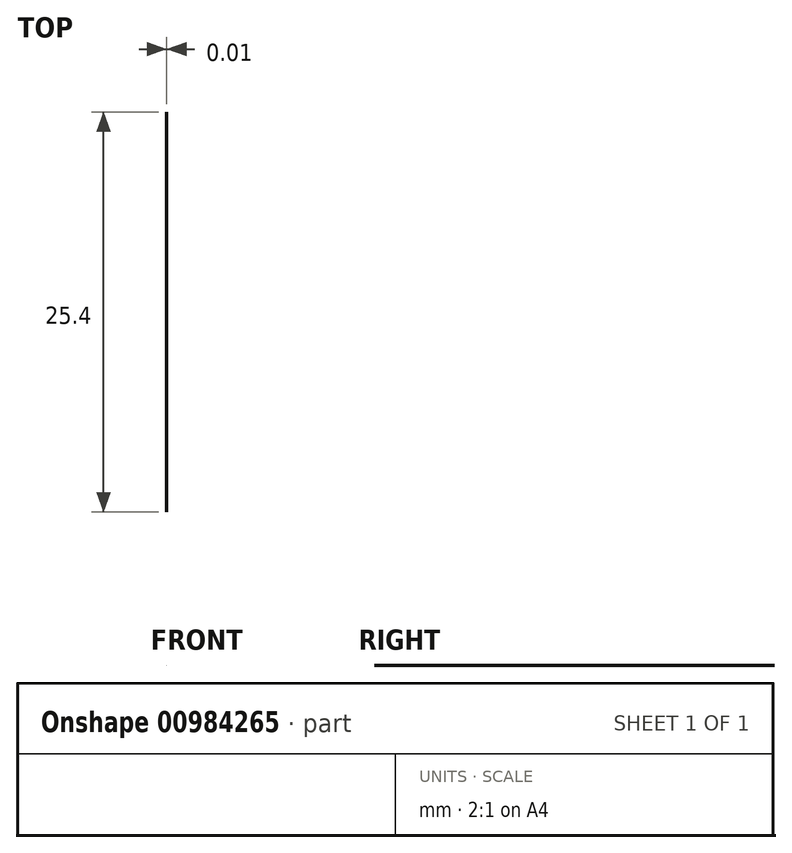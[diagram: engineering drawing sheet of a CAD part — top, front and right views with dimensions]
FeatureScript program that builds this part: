
annotation { "Feature Type Name" : "Feature", "Feature Type Description" : "" }
export const myFeature = defineFeature(function(context is Context, id is Id, definition is map)
    precondition{}
    {
        {
            var Q0;
            Q0=qCreatedBy(makeId("Front.planeOp"),FACE);
            var sketch = newSketch(context, id + "F0", { "sketchPlane" : qUnion([Q0])});
            skLineSegment(sketch, "E0", {"start": v(0.03, 1.18) * mm, "end": v(0.02, 1.18) * mm});
            skLineSegment(sketch, "E1", {"start": v(0.02, 1.18) * mm, "end": v(-0.02, 1.17) * mm});
            skLineSegment(sketch, "E2", {"start": v(-0.02, 1.17) * mm, "end": v(-0.06, 1.16) * mm});
            skLineSegment(sketch, "E3", {"start": v(-0.06, 1.16) * mm, "end": v(-0.1, 1.15) * mm});
            skLineSegment(sketch, "E4", {"start": v(-0.1, 1.15) * mm, "end": v(-0.11, 1.15) * mm});
            skLineSegment(sketch, "E5", {"start": v(-0.11, 1.15) * mm, "end": v(-0.12, 1.14) * mm});
            skLineSegment(sketch, "E6", {"start": v(-0.12, 1.14) * mm, "end": v(-0.12, 1.14) * mm});
            skLineSegment(sketch, "E7", {"start": v(-0.12, 1.14) * mm, "end": v(-0.15, 1.13) * mm});
            skLineSegment(sketch, "E8", {"start": v(-0.15, 1.13) * mm, "end": v(-0.2, 1.12) * mm});
            skLineSegment(sketch, "E9", {"start": v(-0.2, 1.12) * mm, "end": v(-0.24, 1.13) * mm});
            skLineSegment(sketch, "E10", {"start": v(-0.24, 1.13) * mm, "end": v(-0.26, 1.14) * mm});
            skLineSegment(sketch, "E11", {"start": v(-0.26, 1.14) * mm, "end": v(-0.27, 1.14) * mm});
            skLineSegment(sketch, "E12", {"start": v(-0.27, 1.14) * mm, "end": v(-0.27, 1.14) * mm});
            skLineSegment(sketch, "E13", {"start": v(-0.27, 1.14) * mm, "end": v(-0.29, 1.16) * mm});
            skLineSegment(sketch, "E14", {"start": v(-0.29, 1.16) * mm, "end": v(-0.3, 1.16) * mm});
            skLineSegment(sketch, "E15", {"start": v(-0.3, 1.16) * mm, "end": v(-0.3, 1.16) * mm});
            skLineSegment(sketch, "E16", {"start": v(-0.3, 1.16) * mm, "end": v(-0.31, 1.16) * mm});
            skLineSegment(sketch, "E17", {"start": v(-0.31, 1.16) * mm, "end": v(-0.33, 1.16) * mm});
            skLineSegment(sketch, "E18", {"start": v(-0.33, 1.16) * mm, "end": v(-0.34, 1.17) * mm});
            skLineSegment(sketch, "E19", {"start": v(-0.34, 1.17) * mm, "end": v(-0.34, 1.17) * mm});
            skLineSegment(sketch, "E20", {"start": v(-0.34, 1.17) * mm, "end": v(-0.35, 1.18) * mm});
            skLineSegment(sketch, "E21", {"start": v(-0.35, 1.18) * mm, "end": v(-0.37, 1.18) * mm});
            skLineSegment(sketch, "E22", {"start": v(-0.37, 1.18) * mm, "end": v(-0.42, 1.18) * mm});
            skLineSegment(sketch, "E23", {"start": v(-0.42, 1.18) * mm, "end": v(-0.5, 1.17) * mm});
            skLineSegment(sketch, "E24", {"start": v(-0.5, 1.17) * mm, "end": v(-0.55, 1.16) * mm});
            skLineSegment(sketch, "E25", {"start": v(-0.55, 1.16) * mm, "end": v(-0.57, 1.15) * mm});
            skLineSegment(sketch, "E26", {"start": v(-0.57, 1.15) * mm, "end": v(-0.58, 1.15) * mm});
            skLineSegment(sketch, "E27", {"start": v(-0.58, 1.15) * mm, "end": v(-0.62, 1.15) * mm});
            skLineSegment(sketch, "E28", {"start": v(-0.62, 1.15) * mm, "end": v(-0.65, 1.14) * mm});
            skLineSegment(sketch, "E29", {"start": v(-0.65, 1.14) * mm, "end": v(-0.65, 1.14) * mm});
            skLineSegment(sketch, "E30", {"start": v(-0.65, 1.14) * mm, "end": v(-0.66, 1.14) * mm});
            skLineSegment(sketch, "E31", {"start": v(-0.66, 1.14) * mm, "end": v(-0.68, 1.14) * mm});
            skLineSegment(sketch, "E32", {"start": v(-0.68, 1.14) * mm, "end": v(-0.7, 1.13) * mm});
            skLineSegment(sketch, "E33", {"start": v(-0.7, 1.13) * mm, "end": v(-0.7, 1.13) * mm});
            skLineSegment(sketch, "E34", {"start": v(-0.7, 1.13) * mm, "end": v(-0.72, 1.13) * mm});
            skLineSegment(sketch, "E35", {"start": v(-0.72, 1.13) * mm, "end": v(-0.72, 1.13) * mm});
            skLineSegment(sketch, "E36", {"start": v(-0.72, 1.13) * mm, "end": v(-0.72, 1.14) * mm});
            skLineSegment(sketch, "E37", {"start": v(-0.72, 1.14) * mm, "end": v(-0.74, 1.14) * mm});
            skLineSegment(sketch, "E38", {"start": v(-0.74, 1.14) * mm, "end": v(-0.76, 1.13) * mm});
            skLineSegment(sketch, "E39", {"start": v(-0.76, 1.13) * mm, "end": v(-0.76, 1.13) * mm});
            skLineSegment(sketch, "E40", {"start": v(-0.76, 1.13) * mm, "end": v(-0.76, 1.12) * mm});
            skLineSegment(sketch, "E41", {"start": v(-0.76, 1.12) * mm, "end": v(-0.78, 1.11) * mm});
            skLineSegment(sketch, "E42", {"start": v(-0.78, 1.11) * mm, "end": v(-0.8, 1.1) * mm});
            skLineSegment(sketch, "E43", {"start": v(-0.8, 1.1) * mm, "end": v(-0.8, 1.1) * mm});
            skLineSegment(sketch, "E44", {"start": v(-0.8, 1.1) * mm, "end": v(-0.8, 1.09) * mm});
            skLineSegment(sketch, "E45", {"start": v(-0.8, 1.09) * mm, "end": v(-0.8, 1.08) * mm});
            skLineSegment(sketch, "E46", {"start": v(-0.8, 1.08) * mm, "end": v(-0.81, 1.08) * mm});
            skLineSegment(sketch, "E47", {"start": v(-0.81, 1.08) * mm, "end": v(-0.82, 1.06) * mm});
            skLineSegment(sketch, "E48", {"start": v(-0.82, 1.06) * mm, "end": v(-0.83, 1.04) * mm});
            skLineSegment(sketch, "E49", {"start": v(-0.83, 1.04) * mm, "end": v(-0.85, 1.03) * mm});
            skLineSegment(sketch, "E50", {"start": v(-0.85, 1.03) * mm, "end": v(-0.87, 1) * mm});
            skLineSegment(sketch, "E51", {"start": v(-0.87, 1) * mm, "end": v(-0.88, 1) * mm});
            skLineSegment(sketch, "E52", {"start": v(-0.88, 1) * mm, "end": v(-0.9, 0.98) * mm});
            skLineSegment(sketch, "E53", {"start": v(-0.9, 0.98) * mm, "end": v(-0.9, 0.98) * mm});
            skLineSegment(sketch, "E54", {"start": v(-0.9, 0.98) * mm, "end": v(-0.92, 0.97) * mm});
            skLineSegment(sketch, "E55", {"start": v(-0.92, 0.97) * mm, "end": v(-0.92, 0.96) * mm});
            skLineSegment(sketch, "E56", {"start": v(-0.92, 0.96) * mm, "end": v(-0.93, 0.96) * mm});
            skLineSegment(sketch, "E57", {"start": v(-0.93, 0.96) * mm, "end": v(-0.93, 0.95) * mm});
            skLineSegment(sketch, "E58", {"start": v(-0.93, 0.95) * mm, "end": v(-0.93, 0.94) * mm});
            skLineSegment(sketch, "E59", {"start": v(-0.93, 0.94) * mm, "end": v(-0.95, 0.91) * mm});
            skLineSegment(sketch, "E60", {"start": v(-0.95, 0.91) * mm, "end": v(-0.98, 0.88) * mm});
            skLineSegment(sketch, "E61", {"start": v(-0.98, 0.88) * mm, "end": v(-1, 0.84) * mm});
            skLineSegment(sketch, "E62", {"start": v(-1, 0.84) * mm, "end": v(-1.02, 0.83) * mm});
            skLineSegment(sketch, "E63", {"start": v(-1.02, 0.83) * mm, "end": v(-1.02, 0.83) * mm});
            skLineSegment(sketch, "E64", {"start": v(-1.02, 0.83) * mm, "end": v(-1.04, 0.8) * mm});
            skLineSegment(sketch, "E65", {"start": v(-1.04, 0.8) * mm, "end": v(-1.06, 0.74) * mm});
            skLineSegment(sketch, "E66", {"start": v(-1.06, 0.74) * mm, "end": v(-1.1, 0.66) * mm});
            skLineSegment(sketch, "E67", {"start": v(-1.1, 0.66) * mm, "end": v(-1.1, 0.61) * mm});
            skLineSegment(sketch, "E68", {"start": v(-1.1, 0.61) * mm, "end": v(-1.12, 0.6) * mm});
            skLineSegment(sketch, "E69", {"start": v(-1.12, 0.6) * mm, "end": v(-1.12, 0.58) * mm});
            skLineSegment(sketch, "E70", {"start": v(-1.12, 0.58) * mm, "end": v(-1.13, 0.56) * mm});
            skLineSegment(sketch, "E71", {"start": v(-1.13, 0.56) * mm, "end": v(-1.14, 0.54) * mm});
            skLineSegment(sketch, "E72", {"start": v(-1.14, 0.54) * mm, "end": v(-1.17, 0.52) * mm});
            skLineSegment(sketch, "E73", {"start": v(-1.17, 0.52) * mm, "end": v(-1.2, 0.5) * mm});
            skLineSegment(sketch, "E74", {"start": v(-1.2, 0.5) * mm, "end": v(-1.2, 0.5) * mm});
            skLineSegment(sketch, "E75", {"start": v(-1.2, 0.5) * mm, "end": v(-1.22, 0.5) * mm});
            skLineSegment(sketch, "E76", {"start": v(-1.22, 0.5) * mm, "end": v(-1.27, 0.47) * mm});
            skLineSegment(sketch, "E77", {"start": v(-1.27, 0.47) * mm, "end": v(-1.31, 0.44) * mm});
            skLineSegment(sketch, "E78", {"start": v(-1.31, 0.44) * mm, "end": v(-1.32, 0.43) * mm});
            skLineSegment(sketch, "E79", {"start": v(-1.32, 0.43) * mm, "end": v(-1.37, 0.38) * mm});
            skLineSegment(sketch, "E80", {"start": v(-1.37, 0.38) * mm, "end": v(-1.36, 0.47) * mm});
            skLineSegment(sketch, "E81", {"start": v(-1.36, 0.47) * mm, "end": v(-1.36, 0.5) * mm});
            skLineSegment(sketch, "E82", {"start": v(-1.36, 0.5) * mm, "end": v(-1.34, 0.57) * mm});
            skLineSegment(sketch, "E83", {"start": v(-1.34, 0.57) * mm, "end": v(-1.32, 0.68) * mm});
            skLineSegment(sketch, "E84", {"start": v(-1.32, 0.68) * mm, "end": v(-1.3, 0.77) * mm});
            skLineSegment(sketch, "E85", {"start": v(-1.3, 0.77) * mm, "end": v(-1.25, 0.85) * mm});
            skLineSegment(sketch, "E86", {"start": v(-1.25, 0.85) * mm, "end": v(-1.21, 0.92) * mm});
            skLineSegment(sketch, "E87", {"start": v(-1.21, 0.92) * mm, "end": v(-1.16, 0.97) * mm});
            skLineSegment(sketch, "E88", {"start": v(-1.16, 0.97) * mm, "end": v(-1.11, 1) * mm});
            skLineSegment(sketch, "E89", {"start": v(-1.11, 1) * mm, "end": v(-1.07, 1.03) * mm});
            skLineSegment(sketch, "E90", {"start": v(-1.07, 1.03) * mm, "end": v(-1.06, 1.03) * mm});
            skLineSegment(sketch, "E91", {"start": v(-1.06, 1.03) * mm, "end": v(-1.05, 1.03) * mm});
            skLineSegment(sketch, "E92", {"start": v(-1.05, 1.03) * mm, "end": v(-1.03, 1.04) * mm});
            skLineSegment(sketch, "E93", {"start": v(-1.03, 1.04) * mm, "end": v(-1, 1.05) * mm});
            skLineSegment(sketch, "E94", {"start": v(-1, 1.05) * mm, "end": v(-0.97, 1.06) * mm});
            skLineSegment(sketch, "E95", {"start": v(-0.97, 1.06) * mm, "end": v(-0.94, 1.07) * mm});
            skLineSegment(sketch, "E96", {"start": v(-0.94, 1.07) * mm, "end": v(-0.91, 1.07) * mm});
            skLineSegment(sketch, "E97", {"start": v(-0.91, 1.07) * mm, "end": v(-0.9, 1.08) * mm});
            skLineSegment(sketch, "E98", {"start": v(-0.9, 1.08) * mm, "end": v(-0.9, 1.08) * mm});
            skLineSegment(sketch, "E99", {"start": v(-0.9, 1.08) * mm, "end": v(-0.91, 1.08) * mm});
            skLineSegment(sketch, "E100", {"start": v(-0.91, 1.08) * mm, "end": v(-0.93, 1.08) * mm});
            skLineSegment(sketch, "E101", {"start": v(-0.93, 1.08) * mm, "end": v(-0.98, 1.07) * mm});
            skLineSegment(sketch, "E102", {"start": v(-0.98, 1.07) * mm, "end": v(-1.03, 1.06) * mm});
            skLineSegment(sketch, "E103", {"start": v(-1.03, 1.06) * mm, "end": v(-1.07, 1.06) * mm});
            skLineSegment(sketch, "E104", {"start": v(-1.07, 1.06) * mm, "end": v(-1.09, 1.06) * mm});
            skLineSegment(sketch, "E105", {"start": v(-1.09, 1.06) * mm, "end": v(-1.1, 1.05) * mm});
            skLineSegment(sketch, "E106", {"start": v(-1.1, 1.05) * mm, "end": v(-1.14, 1.05) * mm});
            skLineSegment(sketch, "E107", {"start": v(-1.14, 1.05) * mm, "end": v(-1.2, 1.04) * mm});
            skLineSegment(sketch, "E108", {"start": v(-1.2, 1.04) * mm, "end": v(-1.24, 1.03) * mm});
            skLineSegment(sketch, "E109", {"start": v(-1.24, 1.03) * mm, "end": v(-1.27, 1.03) * mm});
            skLineSegment(sketch, "E110", {"start": v(-1.27, 1.03) * mm, "end": v(-1.27, 1.03) * mm});
            skLineSegment(sketch, "E111", {"start": v(-1.27, 1.03) * mm, "end": v(-1.3, 1.03) * mm});
            skLineSegment(sketch, "E112", {"start": v(-1.3, 1.03) * mm, "end": v(-1.35, 1) * mm});
            skLineSegment(sketch, "E113", {"start": v(-1.35, 1) * mm, "end": v(-1.43, 0.97) * mm});
            skLineSegment(sketch, "E114", {"start": v(-1.43, 0.97) * mm, "end": v(-1.52, 0.92) * mm});
            skLineSegment(sketch, "E115", {"start": v(-1.52, 0.92) * mm, "end": v(-1.56, 0.9) * mm});
            skLineSegment(sketch, "E116", {"start": v(-1.56, 0.9) * mm, "end": v(-1.58, 0.88) * mm});
            skLineSegment(sketch, "E117", {"start": v(-1.58, 0.88) * mm, "end": v(-1.58, 0.87) * mm});
            skLineSegment(sketch, "E118", {"start": v(-1.58, 0.87) * mm, "end": v(-1.62, 0.84) * mm});
            skLineSegment(sketch, "E119", {"start": v(-1.62, 0.84) * mm, "end": v(-1.65, 0.81) * mm});
            skLineSegment(sketch, "E120", {"start": v(-1.65, 0.81) * mm, "end": v(-1.66, 0.8) * mm});
            skLineSegment(sketch, "E121", {"start": v(-1.66, 0.8) * mm, "end": v(-1.66, 0.8) * mm});
            skLineSegment(sketch, "E122", {"start": v(-1.66, 0.8) * mm, "end": v(-1.69, 0.79) * mm});
            skLineSegment(sketch, "E123", {"start": v(-1.69, 0.79) * mm, "end": v(-1.7, 0.77) * mm});
            skLineSegment(sketch, "E124", {"start": v(-1.7, 0.77) * mm, "end": v(-1.7, 0.77) * mm});
            skLineSegment(sketch, "E125", {"start": v(-1.7, 0.77) * mm, "end": v(-1.7, 0.76) * mm});
            skLineSegment(sketch, "E126", {"start": v(-1.7, 0.76) * mm, "end": v(-1.7, 0.75) * mm});
            skLineSegment(sketch, "E127", {"start": v(-1.7, 0.75) * mm, "end": v(-1.7, 0.74) * mm});
            skLineSegment(sketch, "E128", {"start": v(-1.7, 0.74) * mm, "end": v(-1.7, 0.74) * mm});
            skLineSegment(sketch, "E129", {"start": v(-1.7, 0.74) * mm, "end": v(-1.71, 0.74) * mm});
            skLineSegment(sketch, "E130", {"start": v(-1.71, 0.74) * mm, "end": v(-1.72, 0.74) * mm});
            skLineSegment(sketch, "E131", {"start": v(-1.72, 0.74) * mm, "end": v(-1.73, 0.73) * mm});
            skLineSegment(sketch, "E132", {"start": v(-1.73, 0.73) * mm, "end": v(-1.75, 0.7) * mm});
            skLineSegment(sketch, "E133", {"start": v(-1.75, 0.7) * mm, "end": v(-1.76, 0.68) * mm});
            skLineSegment(sketch, "E134", {"start": v(-1.76, 0.68) * mm, "end": v(-1.78, 0.66) * mm});
            skLineSegment(sketch, "E135", {"start": v(-1.78, 0.66) * mm, "end": v(-1.8, 0.63) * mm});
            skLineSegment(sketch, "E136", {"start": v(-1.8, 0.63) * mm, "end": v(-1.8, 0.61) * mm});
            skLineSegment(sketch, "E137", {"start": v(-1.8, 0.61) * mm, "end": v(-1.81, 0.6) * mm});
            skLineSegment(sketch, "E138", {"start": v(-1.81, 0.6) * mm, "end": v(-1.81, 0.6) * mm});
            skLineSegment(sketch, "E139", {"start": v(-1.81, 0.6) * mm, "end": v(-1.83, 0.54) * mm});
            skLineSegment(sketch, "E140", {"start": v(-1.83, 0.54) * mm, "end": v(-1.86, 0.4) * mm});
            skLineSegment(sketch, "E141", {"start": v(-1.86, 0.4) * mm, "end": v(-1.89, 0.2) * mm});
            skLineSegment(sketch, "E142", {"start": v(-1.89, 0.2) * mm, "end": v(-1.9, 0) * mm});
            skLineSegment(sketch, "E143", {"start": v(-1.9, 0) * mm, "end": v(-1.88, -0.18) * mm});
            skLineSegment(sketch, "E144", {"start": v(-1.88, -0.18) * mm, "end": v(-1.84, -0.35) * mm});
            skLineSegment(sketch, "E145", {"start": v(-1.84, -0.35) * mm, "end": v(-1.79, -0.52) * mm});
            skLineSegment(sketch, "E146", {"start": v(-1.79, -0.52) * mm, "end": v(-1.72, -0.66) * mm});
            skLineSegment(sketch, "E147", {"start": v(-1.72, -0.66) * mm, "end": v(-1.65, -0.76) * mm});
            skLineSegment(sketch, "E148", {"start": v(-1.65, -0.76) * mm, "end": v(-1.63, -0.78) * mm});
            skLineSegment(sketch, "E149", {"start": v(-1.63, -0.78) * mm, "end": v(-1.61, -0.8) * mm});
            skLineSegment(sketch, "E150", {"start": v(-1.61, -0.8) * mm, "end": v(-1.57, -0.84) * mm});
            skLineSegment(sketch, "E151", {"start": v(-1.57, -0.84) * mm, "end": v(-1.51, -0.9) * mm});
            skLineSegment(sketch, "E152", {"start": v(-1.51, -0.9) * mm, "end": v(-1.45, -0.97) * mm});
            skLineSegment(sketch, "E153", {"start": v(-1.45, -0.97) * mm, "end": v(-1.41, -1) * mm});
            skLineSegment(sketch, "E154", {"start": v(-1.41, -1) * mm, "end": v(-1.4, -1.02) * mm});
            skLineSegment(sketch, "E155", {"start": v(-1.4, -1.02) * mm, "end": v(-1.4, -1.02) * mm});
            skLineSegment(sketch, "E156", {"start": v(-1.4, -1.02) * mm, "end": v(-1.38, -1.04) * mm});
            skLineSegment(sketch, "E157", {"start": v(-1.38, -1.04) * mm, "end": v(-1.36, -1.06) * mm});
            skLineSegment(sketch, "E158", {"start": v(-1.36, -1.06) * mm, "end": v(-1.34, -1.08) * mm});
            skLineSegment(sketch, "E159", {"start": v(-1.34, -1.08) * mm, "end": v(-1.34, -1.1) * mm});
            skLineSegment(sketch, "E160", {"start": v(-1.34, -1.1) * mm, "end": v(-1.34, -1.1) * mm});
            skLineSegment(sketch, "E161", {"start": v(-1.34, -1.1) * mm, "end": v(-1.33, -1.11) * mm});
            skLineSegment(sketch, "E162", {"start": v(-1.33, -1.11) * mm, "end": v(-1.3, -1.11) * mm});
            skLineSegment(sketch, "E163", {"start": v(-1.3, -1.11) * mm, "end": v(-1.3, -1.11) * mm});
            skLineSegment(sketch, "E164", {"start": v(-1.3, -1.11) * mm, "end": v(-1.27, -1.12) * mm});
            skLineSegment(sketch, "E165", {"start": v(-1.27, -1.12) * mm, "end": v(-1.23, -1.14) * mm});
            skLineSegment(sketch, "E166", {"start": v(-1.23, -1.14) * mm, "end": v(-1.22, -1.14) * mm});
            skLineSegment(sketch, "E167", {"start": v(-1.22, -1.14) * mm, "end": v(-1.21, -1.15) * mm});
            skLineSegment(sketch, "E168", {"start": v(-1.21, -1.15) * mm, "end": v(-1.17, -1.16) * mm});
            skLineSegment(sketch, "E169", {"start": v(-1.17, -1.16) * mm, "end": v(-1.11, -1.17) * mm});
            skLineSegment(sketch, "E170", {"start": v(-1.11, -1.17) * mm, "end": v(-1.1, -1.17) * mm});
            skLineSegment(sketch, "E171", {"start": v(-1.1, -1.17) * mm, "end": v(-1.1, -1.17) * mm});
            skLineSegment(sketch, "E172", {"start": v(-1.1, -1.17) * mm, "end": v(-1.07, -1.17) * mm});
            skLineSegment(sketch, "E173", {"start": v(-1.07, -1.17) * mm, "end": v(-1.05, -1.17) * mm});
            skLineSegment(sketch, "E174", {"start": v(-1.05, -1.17) * mm, "end": v(-1.06, -1.16) * mm});
            skLineSegment(sketch, "E175", {"start": v(-1.06, -1.16) * mm, "end": v(-1.08, -1.16) * mm});
            skLineSegment(sketch, "E176", {"start": v(-1.08, -1.16) * mm, "end": v(-1.09, -1.16) * mm});
            skLineSegment(sketch, "E177", {"start": v(-1.09, -1.16) * mm, "end": v(-1.1, -1.16) * mm});
            skLineSegment(sketch, "E178", {"start": v(-1.1, -1.16) * mm, "end": v(-1.12, -1.15) * mm});
            skLineSegment(sketch, "E179", {"start": v(-1.12, -1.15) * mm, "end": v(-1.16, -1.14) * mm});
            skLineSegment(sketch, "E180", {"start": v(-1.16, -1.14) * mm, "end": v(-1.2, -1.12) * mm});
            skLineSegment(sketch, "E181", {"start": v(-1.2, -1.12) * mm, "end": v(-1.22, -1.1) * mm});
            skLineSegment(sketch, "E182", {"start": v(-1.22, -1.1) * mm, "end": v(-1.25, -1.09) * mm});
            skLineSegment(sketch, "E183", {"start": v(-1.25, -1.09) * mm, "end": v(-1.26, -1.07) * mm});
            skLineSegment(sketch, "E184", {"start": v(-1.26, -1.07) * mm, "end": v(-1.26, -1.06) * mm});
            skLineSegment(sketch, "E185", {"start": v(-1.26, -1.06) * mm, "end": v(-1.26, -1.05) * mm});
            skLineSegment(sketch, "E186", {"start": v(-1.26, -1.05) * mm, "end": v(-1.26, -1.05) * mm});
            skLineSegment(sketch, "E187", {"start": v(-1.26, -1.05) * mm, "end": v(-1.25, -1.05) * mm});
            skLineSegment(sketch, "E188", {"start": v(-1.25, -1.05) * mm, "end": v(-1.23, -1.04) * mm});
            skLineSegment(sketch, "E189", {"start": v(-1.23, -1.04) * mm, "end": v(-1.21, -1.02) * mm});
            skLineSegment(sketch, "E190", {"start": v(-1.21, -1.02) * mm, "end": v(-1.2, -1.02) * mm});
            skLineSegment(sketch, "E191", {"start": v(-1.2, -1.02) * mm, "end": v(-1.18, -1) * mm});
            skLineSegment(sketch, "E192", {"start": v(-1.18, -1) * mm, "end": v(-1.2, -1) * mm});
            skLineSegment(sketch, "E193", {"start": v(-1.2, -1) * mm, "end": v(-1.21, -1) * mm});
            skLineSegment(sketch, "E194", {"start": v(-1.21, -1) * mm, "end": v(-1.23, -1.01) * mm});
            skLineSegment(sketch, "E195", {"start": v(-1.23, -1.01) * mm, "end": v(-1.23, -1.02) * mm});
            skLineSegment(sketch, "E196", {"start": v(-1.23, -1.02) * mm, "end": v(-1.23, -1) * mm});
            skLineSegment(sketch, "E197", {"start": v(-1.23, -1) * mm, "end": v(-1.23, -1) * mm});
            skLineSegment(sketch, "E198", {"start": v(-1.23, -1) * mm, "end": v(-1.22, -0.98) * mm});
            skLineSegment(sketch, "E199", {"start": v(-1.22, -0.98) * mm, "end": v(-1.18, -0.94) * mm});
            skLineSegment(sketch, "E200", {"start": v(-1.18, -0.94) * mm, "end": v(-1.08, -0.86) * mm});
            skLineSegment(sketch, "E201", {"start": v(-1.08, -0.86) * mm, "end": v(-0.97, -0.78) * mm});
            skLineSegment(sketch, "E202", {"start": v(-0.97, -0.78) * mm, "end": v(-0.88, -0.73) * mm});
            skLineSegment(sketch, "E203", {"start": v(-0.88, -0.73) * mm, "end": v(-0.85, -0.71) * mm});
            skLineSegment(sketch, "E204", {"start": v(-0.85, -0.71) * mm, "end": v(-0.84, -0.7) * mm});
            skLineSegment(sketch, "E205", {"start": v(-0.84, -0.7) * mm, "end": v(-0.81, -0.7) * mm});
            skLineSegment(sketch, "E206", {"start": v(-0.81, -0.7) * mm, "end": v(-0.8, -0.7) * mm});
            skLineSegment(sketch, "E207", {"start": v(-0.8, -0.7) * mm, "end": v(-0.8, -0.7) * mm});
            skLineSegment(sketch, "E208", {"start": v(-0.8, -0.7) * mm, "end": v(-0.82, -0.73) * mm});
            skLineSegment(sketch, "E209", {"start": v(-0.82, -0.73) * mm, "end": v(-0.82, -0.74) * mm});
            skLineSegment(sketch, "E210", {"start": v(-0.82, -0.74) * mm, "end": v(-0.83, -0.75) * mm});
            skLineSegment(sketch, "E211", {"start": v(-0.83, -0.75) * mm, "end": v(-0.85, -0.79) * mm});
            skLineSegment(sketch, "E212", {"start": v(-0.85, -0.79) * mm, "end": v(-0.88, -0.85) * mm});
            skLineSegment(sketch, "E213", {"start": v(-0.88, -0.85) * mm, "end": v(-0.91, -0.92) * mm});
            skLineSegment(sketch, "E214", {"start": v(-0.91, -0.92) * mm, "end": v(-0.94, -1) * mm});
            skLineSegment(sketch, "E215", {"start": v(-0.94, -1) * mm, "end": v(-0.96, -1.06) * mm});
            skLineSegment(sketch, "E216", {"start": v(-0.96, -1.06) * mm, "end": v(-0.97, -1.12) * mm});
            skLineSegment(sketch, "E217", {"start": v(-0.97, -1.12) * mm, "end": v(-0.98, -1.16) * mm});
            skLineSegment(sketch, "E218", {"start": v(-0.98, -1.16) * mm, "end": v(-0.97, -1.17) * mm});
            skLineSegment(sketch, "E219", {"start": v(-0.97, -1.17) * mm, "end": v(-0.97, -1.17) * mm});
            skLineSegment(sketch, "E220", {"start": v(-0.97, -1.17) * mm, "end": v(-0.96, -1.17) * mm});
            skLineSegment(sketch, "E221", {"start": v(-0.96, -1.17) * mm, "end": v(-0.95, -1.16) * mm});
            skLineSegment(sketch, "E222", {"start": v(-0.95, -1.16) * mm, "end": v(-0.95, -1.15) * mm});
            skLineSegment(sketch, "E223", {"start": v(-0.95, -1.15) * mm, "end": v(-0.95, -1.14) * mm});
            skLineSegment(sketch, "E224", {"start": v(-0.95, -1.14) * mm, "end": v(-0.95, -1.13) * mm});
            skLineSegment(sketch, "E225", {"start": v(-0.95, -1.13) * mm, "end": v(-0.94, -1.1) * mm});
            skLineSegment(sketch, "E226", {"start": v(-0.94, -1.1) * mm, "end": v(-0.92, -1.05) * mm});
            skLineSegment(sketch, "E227", {"start": v(-0.92, -1.05) * mm, "end": v(-0.9, -0.98) * mm});
            skLineSegment(sketch, "E228", {"start": v(-0.9, -0.98) * mm, "end": v(-0.87, -0.9) * mm});
            skLineSegment(sketch, "E229", {"start": v(-0.87, -0.9) * mm, "end": v(-0.84, -0.84) * mm});
            skLineSegment(sketch, "E230", {"start": v(-0.84, -0.84) * mm, "end": v(-0.82, -0.78) * mm});
            skLineSegment(sketch, "E231", {"start": v(-0.82, -0.78) * mm, "end": v(-0.8, -0.74) * mm});
            skLineSegment(sketch, "E232", {"start": v(-0.8, -0.74) * mm, "end": v(-0.79, -0.73) * mm});
            skLineSegment(sketch, "E233", {"start": v(-0.79, -0.73) * mm, "end": v(-0.79, -0.73) * mm});
            skLineSegment(sketch, "E234", {"start": v(-0.79, -0.73) * mm, "end": v(-0.78, -0.74) * mm});
            skLineSegment(sketch, "E235", {"start": v(-0.78, -0.74) * mm, "end": v(-0.79, -0.76) * mm});
            skLineSegment(sketch, "E236", {"start": v(-0.79, -0.76) * mm, "end": v(-0.79, -0.8) * mm});
            skLineSegment(sketch, "E237", {"start": v(-0.79, -0.8) * mm, "end": v(-0.8, -0.82) * mm});
            skLineSegment(sketch, "E238", {"start": v(-0.8, -0.82) * mm, "end": v(-0.8, -0.83) * mm});
            skLineSegment(sketch, "E239", {"start": v(-0.8, -0.83) * mm, "end": v(-0.8, -0.86) * mm});
            skLineSegment(sketch, "E240", {"start": v(-0.8, -0.86) * mm, "end": v(-0.8, -0.97) * mm});
            skLineSegment(sketch, "E241", {"start": v(-0.8, -0.97) * mm, "end": v(-0.8, -1.08) * mm});
            skLineSegment(sketch, "E242", {"start": v(-0.8, -1.08) * mm, "end": v(-0.8, -1.15) * mm});
            skLineSegment(sketch, "E243", {"start": v(-0.8, -1.15) * mm, "end": v(-0.77, -1.17) * mm});
            skLineSegment(sketch, "E244", {"start": v(-0.77, -1.17) * mm, "end": v(-0.77, -1.17) * mm});
            skLineSegment(sketch, "E245", {"start": v(-0.77, -1.17) * mm, "end": v(-0.76, -1.17) * mm});
            skLineSegment(sketch, "E246", {"start": v(-0.76, -1.17) * mm, "end": v(-0.74, -1.17) * mm});
            skLineSegment(sketch, "E247", {"start": v(-0.74, -1.17) * mm, "end": v(-0.73, -1.15) * mm});
            skLineSegment(sketch, "E248", {"start": v(-0.73, -1.15) * mm, "end": v(-0.72, -1.14) * mm});
            skLineSegment(sketch, "E249", {"start": v(-0.72, -1.14) * mm, "end": v(-0.72, -1.13) * mm});
            skLineSegment(sketch, "E250", {"start": v(-0.72, -1.13) * mm, "end": v(-0.72, -1.12) * mm});
            skLineSegment(sketch, "E251", {"start": v(-0.72, -1.12) * mm, "end": v(-0.73, -1.12) * mm});
            skLineSegment(sketch, "E252", {"start": v(-0.73, -1.12) * mm, "end": v(-0.74, -1.11) * mm});
            skLineSegment(sketch, "E253", {"start": v(-0.74, -1.11) * mm, "end": v(-0.74, -1.1) * mm});
            skLineSegment(sketch, "E254", {"start": v(-0.74, -1.1) * mm, "end": v(-0.73, -1.1) * mm});
            skLineSegment(sketch, "E255", {"start": v(-0.73, -1.1) * mm, "end": v(-0.7, -1.09) * mm});
            skLineSegment(sketch, "E256", {"start": v(-0.7, -1.09) * mm, "end": v(-0.7, -1.09) * mm});
            skLineSegment(sketch, "E257", {"start": v(-0.7, -1.09) * mm, "end": v(-0.68, -1.1) * mm});
            skLineSegment(sketch, "E258", {"start": v(-0.68, -1.1) * mm, "end": v(-0.67, -1.1) * mm});
            skLineSegment(sketch, "E259", {"start": v(-0.67, -1.1) * mm, "end": v(-0.67, -1.1) * mm});
            skLineSegment(sketch, "E260", {"start": v(-0.67, -1.1) * mm, "end": v(-0.67, -1.11) * mm});
            skLineSegment(sketch, "E261", {"start": v(-0.67, -1.11) * mm, "end": v(-0.67, -1.13) * mm});
            skLineSegment(sketch, "E262", {"start": v(-0.67, -1.13) * mm, "end": v(-0.65, -1.14) * mm});
            skLineSegment(sketch, "E263", {"start": v(-0.65, -1.14) * mm, "end": v(-0.64, -1.14) * mm});
            skLineSegment(sketch, "E264", {"start": v(-0.64, -1.14) * mm, "end": v(-0.63, -1.13) * mm});
            skLineSegment(sketch, "E265", {"start": v(-0.63, -1.13) * mm, "end": v(-0.63, -1.13) * mm});
            skLineSegment(sketch, "E266", {"start": v(-0.63, -1.13) * mm, "end": v(-0.61, -1.13) * mm});
            skLineSegment(sketch, "E267", {"start": v(-0.61, -1.13) * mm, "end": v(-0.6, -1.14) * mm});
            skLineSegment(sketch, "E268", {"start": v(-0.6, -1.14) * mm, "end": v(-0.6, -1.15) * mm});
            skLineSegment(sketch, "E269", {"start": v(-0.6, -1.15) * mm, "end": v(-0.6, -1.15) * mm});
            skLineSegment(sketch, "E270", {"start": v(-0.6, -1.15) * mm, "end": v(-0.58, -1.16) * mm});
            skLineSegment(sketch, "E271", {"start": v(-0.58, -1.16) * mm, "end": v(-0.57, -1.17) * mm});
            skLineSegment(sketch, "E272", {"start": v(-0.57, -1.17) * mm, "end": v(-0.57, -1.17) * mm});
            skLineSegment(sketch, "E273", {"start": v(-0.57, -1.17) * mm, "end": v(-0.56, -1.16) * mm});
            skLineSegment(sketch, "E274", {"start": v(-0.56, -1.16) * mm, "end": v(-0.56, -1.16) * mm});
            skLineSegment(sketch, "E275", {"start": v(-0.56, -1.16) * mm, "end": v(-0.55, -1.15) * mm});
            skLineSegment(sketch, "E276", {"start": v(-0.55, -1.15) * mm, "end": v(-0.54, -1.15) * mm});
            skLineSegment(sketch, "E277", {"start": v(-0.54, -1.15) * mm, "end": v(-0.54, -1.15) * mm});
            skLineSegment(sketch, "E278", {"start": v(-0.54, -1.15) * mm, "end": v(-0.53, -1.16) * mm});
            skLineSegment(sketch, "E279", {"start": v(-0.53, -1.16) * mm, "end": v(-0.53, -1.16) * mm});
            skLineSegment(sketch, "E280", {"start": v(-0.53, -1.16) * mm, "end": v(-0.51, -1.16) * mm});
            skLineSegment(sketch, "E281", {"start": v(-0.51, -1.16) * mm, "end": v(-0.5, -1.16) * mm});
            skLineSegment(sketch, "E282", {"start": v(-0.5, -1.16) * mm, "end": v(-0.5, -1.16) * mm});
            skLineSegment(sketch, "E283", {"start": v(-0.5, -1.16) * mm, "end": v(-0.5, -1.15) * mm});
            skLineSegment(sketch, "E284", {"start": v(-0.5, -1.15) * mm, "end": v(-0.51, -1.13) * mm});
            skLineSegment(sketch, "E285", {"start": v(-0.51, -1.13) * mm, "end": v(-0.53, -1.11) * mm});
            skLineSegment(sketch, "E286", {"start": v(-0.53, -1.11) * mm, "end": v(-0.53, -1.1) * mm});
            skLineSegment(sketch, "E287", {"start": v(-0.53, -1.1) * mm, "end": v(-0.54, -1.1) * mm});
            skLineSegment(sketch, "E288", {"start": v(-0.54, -1.1) * mm, "end": v(-0.56, -1.07) * mm});
            skLineSegment(sketch, "E289", {"start": v(-0.56, -1.07) * mm, "end": v(-0.58, -1.03) * mm});
            skLineSegment(sketch, "E290", {"start": v(-0.58, -1.03) * mm, "end": v(-0.58, -1) * mm});
            skLineSegment(sketch, "E291", {"start": v(-0.58, -1) * mm, "end": v(-0.58, -0.98) * mm});
            skLineSegment(sketch, "E292", {"start": v(-0.58, -0.98) * mm, "end": v(-0.58, -0.98) * mm});
            skLineSegment(sketch, "E293", {"start": v(-0.58, -0.98) * mm, "end": v(-0.58, -0.97) * mm});
            skLineSegment(sketch, "E294", {"start": v(-0.58, -0.97) * mm, "end": v(-0.59, -0.97) * mm});
            skLineSegment(sketch, "E295", {"start": v(-0.59, -0.97) * mm, "end": v(-0.6, -0.97) * mm});
            skLineSegment(sketch, "E296", {"start": v(-0.6, -0.97) * mm, "end": v(-0.6, -0.97) * mm});
            skLineSegment(sketch, "E297", {"start": v(-0.6, -0.97) * mm, "end": v(-0.61, -0.96) * mm});
            skLineSegment(sketch, "E298", {"start": v(-0.61, -0.96) * mm, "end": v(-0.62, -0.93) * mm});
            skLineSegment(sketch, "E299", {"start": v(-0.62, -0.93) * mm, "end": v(-0.63, -0.9) * mm});
            skLineSegment(sketch, "E300", {"start": v(-0.63, -0.9) * mm, "end": v(-0.63, -0.89) * mm});
            skLineSegment(sketch, "E301", {"start": v(-0.63, -0.89) * mm, "end": v(-0.64, -0.88) * mm});
            skLineSegment(sketch, "E302", {"start": v(-0.64, -0.88) * mm, "end": v(-0.64, -0.85) * mm});
            skLineSegment(sketch, "E303", {"start": v(-0.64, -0.85) * mm, "end": v(-0.65, -0.81) * mm});
            skLineSegment(sketch, "E304", {"start": v(-0.65, -0.81) * mm, "end": v(-0.65, -0.8) * mm});
            skLineSegment(sketch, "E305", {"start": v(-0.65, -0.8) * mm, "end": v(-0.65, -0.78) * mm});
            skLineSegment(sketch, "E306", {"start": v(-0.65, -0.78) * mm, "end": v(-0.64, -0.79) * mm});
            skLineSegment(sketch, "E307", {"start": v(-0.64, -0.79) * mm, "end": v(-0.63, -0.8) * mm});
            skLineSegment(sketch, "E308", {"start": v(-0.63, -0.8) * mm, "end": v(-0.6, -0.82) * mm});
            skLineSegment(sketch, "E309", {"start": v(-0.6, -0.82) * mm, "end": v(-0.58, -0.84) * mm});
            skLineSegment(sketch, "E310", {"start": v(-0.58, -0.84) * mm, "end": v(-0.58, -0.85) * mm});
            skLineSegment(sketch, "E311", {"start": v(-0.58, -0.85) * mm, "end": v(-0.56, -0.87) * mm});
            skLineSegment(sketch, "E312", {"start": v(-0.56, -0.87) * mm, "end": v(-0.52, -0.9) * mm});
            skLineSegment(sketch, "E313", {"start": v(-0.52, -0.9) * mm, "end": v(-0.45, -0.97) * mm});
            skLineSegment(sketch, "E314", {"start": v(-0.45, -0.97) * mm, "end": v(-0.38, -1.02) * mm});
            skLineSegment(sketch, "E315", {"start": v(-0.38, -1.02) * mm, "end": v(-0.3, -1.07) * mm});
            skLineSegment(sketch, "E316", {"start": v(-0.3, -1.07) * mm, "end": v(-0.24, -1.11) * mm});
            skLineSegment(sketch, "E317", {"start": v(-0.24, -1.11) * mm, "end": v(-0.18, -1.14) * mm});
            skLineSegment(sketch, "E318", {"start": v(-0.18, -1.14) * mm, "end": v(-0.13, -1.16) * mm});
            skLineSegment(sketch, "E319", {"start": v(-0.13, -1.16) * mm, "end": v(-0.1, -1.17) * mm});
            skLineSegment(sketch, "E320", {"start": v(-0.1, -1.17) * mm, "end": v(-0.09, -1.17) * mm});
            skLineSegment(sketch, "E321", {"start": v(-0.09, -1.17) * mm, "end": v(-0.08, -1.17) * mm});
            skLineSegment(sketch, "E322", {"start": v(-0.08, -1.17) * mm, "end": v(-0.07, -1.17) * mm});
            skLineSegment(sketch, "E323", {"start": v(-0.07, -1.17) * mm, "end": v(-0.07, -1.16) * mm});
            skLineSegment(sketch, "E324", {"start": v(-0.07, -1.16) * mm, "end": v(-0.08, -1.16) * mm});
            skLineSegment(sketch, "E325", {"start": v(-0.08, -1.16) * mm, "end": v(-0.1, -1.15) * mm});
            skLineSegment(sketch, "E326", {"start": v(-0.1, -1.15) * mm, "end": v(-0.1, -1.15) * mm});
            skLineSegment(sketch, "E327", {"start": v(-0.1, -1.15) * mm, "end": v(-0.11, -1.14) * mm});
            skLineSegment(sketch, "E328", {"start": v(-0.11, -1.14) * mm, "end": v(-0.16, -1.13) * mm});
            skLineSegment(sketch, "E329", {"start": v(-0.16, -1.13) * mm, "end": v(-0.2, -1.1) * mm});
            skLineSegment(sketch, "E330", {"start": v(-0.2, -1.1) * mm, "end": v(-0.2, -1.1) * mm});
            skLineSegment(sketch, "E331", {"start": v(-0.2, -1.1) * mm, "end": v(-0.21, -1.1) * mm});
            skLineSegment(sketch, "E332", {"start": v(-0.21, -1.1) * mm, "end": v(-0.23, -1.08) * mm});
            skLineSegment(sketch, "E333", {"start": v(-0.23, -1.08) * mm, "end": v(-0.27, -1.05) * mm});
            skLineSegment(sketch, "E334", {"start": v(-0.27, -1.05) * mm, "end": v(-0.32, -1.02) * mm});
            skLineSegment(sketch, "E335", {"start": v(-0.32, -1.02) * mm, "end": v(-0.36, -1) * mm});
            skLineSegment(sketch, "E336", {"start": v(-0.36, -1) * mm, "end": v(-0.37, -0.99) * mm});
            skLineSegment(sketch, "E337", {"start": v(-0.37, -0.99) * mm, "end": v(-0.38, -0.98) * mm});
            skLineSegment(sketch, "E338", {"start": v(-0.38, -0.98) * mm, "end": v(-0.41, -0.96) * mm});
            skLineSegment(sketch, "E339", {"start": v(-0.41, -0.96) * mm, "end": v(-0.45, -0.93) * mm});
            skLineSegment(sketch, "E340", {"start": v(-0.45, -0.93) * mm, "end": v(-0.5, -0.9) * mm});
            skLineSegment(sketch, "E341", {"start": v(-0.5, -0.9) * mm, "end": v(-0.52, -0.88) * mm});
            skLineSegment(sketch, "E342", {"start": v(-0.52, -0.88) * mm, "end": v(-0.55, -0.86) * mm});
            skLineSegment(sketch, "E343", {"start": v(-0.55, -0.86) * mm, "end": v(-0.57, -0.84) * mm});
            skLineSegment(sketch, "E344", {"start": v(-0.57, -0.84) * mm, "end": v(-0.58, -0.83) * mm});
            skLineSegment(sketch, "E345", {"start": v(-0.58, -0.83) * mm, "end": v(-0.58, -0.83) * mm});
            skLineSegment(sketch, "E346", {"start": v(-0.58, -0.83) * mm, "end": v(-0.57, -0.83) * mm});
            skLineSegment(sketch, "E347", {"start": v(-0.57, -0.83) * mm, "end": v(-0.56, -0.83) * mm});
            skLineSegment(sketch, "E348", {"start": v(-0.56, -0.83) * mm, "end": v(-0.54, -0.84) * mm});
            skLineSegment(sketch, "E349", {"start": v(-0.54, -0.84) * mm, "end": v(-0.52, -0.85) * mm});
            skLineSegment(sketch, "E350", {"start": v(-0.52, -0.85) * mm, "end": v(-0.51, -0.85) * mm});
            skLineSegment(sketch, "E351", {"start": v(-0.51, -0.85) * mm, "end": v(-0.49, -0.86) * mm});
            skLineSegment(sketch, "E352", {"start": v(-0.49, -0.86) * mm, "end": v(-0.36, -0.88) * mm});
            skLineSegment(sketch, "E353", {"start": v(-0.36, -0.88) * mm, "end": v(-0.25, -0.85) * mm});
            skLineSegment(sketch, "E354", {"start": v(-0.25, -0.85) * mm, "end": v(-0.22, -0.84) * mm});
            skLineSegment(sketch, "E355", {"start": v(-0.22, -0.84) * mm, "end": v(-0.22, -0.84) * mm});
            skLineSegment(sketch, "E356", {"start": v(-0.22, -0.84) * mm, "end": v(-0.2, -0.82) * mm});
            skLineSegment(sketch, "E357", {"start": v(-0.2, -0.82) * mm, "end": v(-0.17, -0.8) * mm});
            skLineSegment(sketch, "E358", {"start": v(-0.17, -0.8) * mm, "end": v(-0.16, -0.8) * mm});
            skLineSegment(sketch, "E359", {"start": v(-0.16, -0.8) * mm, "end": v(-0.15, -0.8) * mm});
            skLineSegment(sketch, "E360", {"start": v(-0.15, -0.8) * mm, "end": v(-0.15, -0.8) * mm});
            skLineSegment(sketch, "E361", {"start": v(-0.15, -0.8) * mm, "end": v(-0.14, -0.82) * mm});
            skLineSegment(sketch, "E362", {"start": v(-0.14, -0.82) * mm, "end": v(-0.1, -0.87) * mm});
            skLineSegment(sketch, "E363", {"start": v(-0.1, -0.87) * mm, "end": v(-0.06, -0.97) * mm});
            skLineSegment(sketch, "E364", {"start": v(-0.06, -0.97) * mm, "end": v(-0.03, -1.06) * mm});
            skLineSegment(sketch, "E365", {"start": v(-0.03, -1.06) * mm, "end": v(-0.02, -1.12) * mm});
            skLineSegment(sketch, "E366", {"start": v(-0.02, -1.12) * mm, "end": v(-0.02, -1.13) * mm});
            skLineSegment(sketch, "E367", {"start": v(-0.02, -1.13) * mm, "end": v(-0.02, -1.14) * mm});
            skLineSegment(sketch, "E368", {"start": v(-0.02, -1.14) * mm, "end": v(0, -1.16) * mm});
            skLineSegment(sketch, "E369", {"start": v(0, -1.16) * mm, "end": v(0.01, -1.17) * mm});
            skLineSegment(sketch, "E370", {"start": v(0.01, -1.17) * mm, "end": v(0.04, -1.16) * mm});
            skLineSegment(sketch, "E371", {"start": v(0.04, -1.16) * mm, "end": v(0.05, -1.13) * mm});
            skLineSegment(sketch, "E372", {"start": v(0.05, -1.13) * mm, "end": v(0.05, -1.12) * mm});
            skLineSegment(sketch, "E373", {"start": v(0.05, -1.12) * mm, "end": v(0.05, -1.12) * mm});
            skLineSegment(sketch, "E374", {"start": v(0.05, -1.12) * mm, "end": v(0.06, -1.1) * mm});
            skLineSegment(sketch, "E375", {"start": v(0.06, -1.1) * mm, "end": v(0.08, -1.05) * mm});
            skLineSegment(sketch, "E376", {"start": v(0.08, -1.05) * mm, "end": v(0.1, -1) * mm});
            skLineSegment(sketch, "E377", {"start": v(0.1, -1) * mm, "end": v(0.13, -0.96) * mm});
            skLineSegment(sketch, "E378", {"start": v(0.13, -0.96) * mm, "end": v(0.16, -0.91) * mm});
            skLineSegment(sketch, "E379", {"start": v(0.16, -0.91) * mm, "end": v(0.19, -0.87) * mm});
            skLineSegment(sketch, "E380", {"start": v(0.19, -0.87) * mm, "end": v(0.21, -0.85) * mm});
            skLineSegment(sketch, "E381", {"start": v(0.21, -0.85) * mm, "end": v(0.22, -0.84) * mm});
            skLineSegment(sketch, "E382", {"start": v(0.22, -0.84) * mm, "end": v(0.23, -0.84) * mm});
            skLineSegment(sketch, "E383", {"start": v(0.23, -0.84) * mm, "end": v(0.23, -0.85) * mm});
            skLineSegment(sketch, "E384", {"start": v(0.23, -0.85) * mm, "end": v(0.24, -0.87) * mm});
            skLineSegment(sketch, "E385", {"start": v(0.24, -0.87) * mm, "end": v(0.26, -0.94) * mm});
            skLineSegment(sketch, "E386", {"start": v(0.26, -0.94) * mm, "end": v(0.28, -1.02) * mm});
            skLineSegment(sketch, "E387", {"start": v(0.28, -1.02) * mm, "end": v(0.3, -1.09) * mm});
            skLineSegment(sketch, "E388", {"start": v(0.3, -1.09) * mm, "end": v(0.3, -1.1) * mm});
            skLineSegment(sketch, "E389", {"start": v(0.3, -1.1) * mm, "end": v(0.3, -1.12) * mm});
            skLineSegment(sketch, "E390", {"start": v(0.3, -1.12) * mm, "end": v(0.3, -1.15) * mm});
            skLineSegment(sketch, "E391", {"start": v(0.3, -1.15) * mm, "end": v(0.32, -1.17) * mm});
            skLineSegment(sketch, "E392", {"start": v(0.32, -1.17) * mm, "end": v(0.32, -1.17) * mm});
            skLineSegment(sketch, "E393", {"start": v(0.32, -1.17) * mm, "end": v(0.33, -1.15) * mm});
            skLineSegment(sketch, "E394", {"start": v(0.33, -1.15) * mm, "end": v(0.33, -1.08) * mm});
            skLineSegment(sketch, "E395", {"start": v(0.33, -1.08) * mm, "end": v(0.31, -1) * mm});
            skLineSegment(sketch, "E396", {"start": v(0.31, -1) * mm, "end": v(0.3, -0.94) * mm});
            skLineSegment(sketch, "E397", {"start": v(0.3, -0.94) * mm, "end": v(0.29, -0.92) * mm});
            skLineSegment(sketch, "E398", {"start": v(0.29, -0.92) * mm, "end": v(0.28, -0.9) * mm});
            skLineSegment(sketch, "E399", {"start": v(0.28, -0.9) * mm, "end": v(0.27, -0.86) * mm});
            skLineSegment(sketch, "E400", {"start": v(0.27, -0.86) * mm, "end": v(0.26, -0.84) * mm});
            skLineSegment(sketch, "E401", {"start": v(0.26, -0.84) * mm, "end": v(0.28, -0.83) * mm});
            skLineSegment(sketch, "E402", {"start": v(0.28, -0.83) * mm, "end": v(0.3, -0.83) * mm});
            skLineSegment(sketch, "E403", {"start": v(0.3, -0.83) * mm, "end": v(0.3, -0.83) * mm});
            skLineSegment(sketch, "E404", {"start": v(0.3, -0.83) * mm, "end": v(0.32, -0.83) * mm});
            skLineSegment(sketch, "E405", {"start": v(0.32, -0.83) * mm, "end": v(0.36, -0.84) * mm});
            skLineSegment(sketch, "E406", {"start": v(0.36, -0.84) * mm, "end": v(0.4, -0.84) * mm});
            skLineSegment(sketch, "E407", {"start": v(0.4, -0.84) * mm, "end": v(0.46, -0.83) * mm});
            skLineSegment(sketch, "E408", {"start": v(0.46, -0.83) * mm, "end": v(0.49, -0.82) * mm});
            skLineSegment(sketch, "E409", {"start": v(0.49, -0.82) * mm, "end": v(0.5, -0.82) * mm});
            skLineSegment(sketch, "E410", {"start": v(0.5, -0.82) * mm, "end": v(0.5, -0.81) * mm});
            skLineSegment(sketch, "E411", {"start": v(0.5, -0.81) * mm, "end": v(0.53, -0.8) * mm});
            skLineSegment(sketch, "E412", {"start": v(0.53, -0.8) * mm, "end": v(0.54, -0.8) * mm});
            skLineSegment(sketch, "E413", {"start": v(0.54, -0.8) * mm, "end": v(0.54, -0.8) * mm});
            skLineSegment(sketch, "E414", {"start": v(0.54, -0.8) * mm, "end": v(0.54, -0.81) * mm});
            skLineSegment(sketch, "E415", {"start": v(0.54, -0.81) * mm, "end": v(0.53, -0.85) * mm});
            skLineSegment(sketch, "E416", {"start": v(0.53, -0.85) * mm, "end": v(0.52, -0.9) * mm});
            skLineSegment(sketch, "E417", {"start": v(0.52, -0.9) * mm, "end": v(0.5, -0.96) * mm});
            skLineSegment(sketch, "E418", {"start": v(0.5, -0.96) * mm, "end": v(0.5, -0.98) * mm});
            skLineSegment(sketch, "E419", {"start": v(0.5, -0.98) * mm, "end": v(0.5, -0.98) * mm});
            skLineSegment(sketch, "E420", {"start": v(0.5, -0.98) * mm, "end": v(0.5, -1) * mm});
            skLineSegment(sketch, "E421", {"start": v(0.5, -1) * mm, "end": v(0.49, -1.03) * mm});
            skLineSegment(sketch, "E422", {"start": v(0.49, -1.03) * mm, "end": v(0.48, -1.07) * mm});
            skLineSegment(sketch, "E423", {"start": v(0.48, -1.07) * mm, "end": v(0.48, -1.1) * mm});
            skLineSegment(sketch, "E424", {"start": v(0.48, -1.1) * mm, "end": v(0.48, -1.13) * mm});
            skLineSegment(sketch, "E425", {"start": v(0.48, -1.13) * mm, "end": v(0.49, -1.15) * mm});
            skLineSegment(sketch, "E426", {"start": v(0.49, -1.15) * mm, "end": v(0.5, -1.17) * mm});
            skLineSegment(sketch, "E427", {"start": v(0.5, -1.17) * mm, "end": v(0.5, -1.17) * mm});
            skLineSegment(sketch, "E428", {"start": v(0.5, -1.17) * mm, "end": v(0.52, -1.17) * mm});
            skLineSegment(sketch, "E429", {"start": v(0.52, -1.17) * mm, "end": v(0.54, -1.14) * mm});
            skLineSegment(sketch, "E430", {"start": v(0.54, -1.14) * mm, "end": v(0.55, -1.1) * mm});
            skLineSegment(sketch, "E431", {"start": v(0.55, -1.1) * mm, "end": v(0.55, -1.07) * mm});
            skLineSegment(sketch, "E432", {"start": v(0.55, -1.07) * mm, "end": v(0.55, -1.06) * mm});
            skLineSegment(sketch, "E433", {"start": v(0.55, -1.06) * mm, "end": v(0.55, -1.05) * mm});
            skLineSegment(sketch, "E434", {"start": v(0.55, -1.05) * mm, "end": v(0.55, -1) * mm});
            skLineSegment(sketch, "E435", {"start": v(0.55, -1) * mm, "end": v(0.56, -0.98) * mm});
            skLineSegment(sketch, "E436", {"start": v(0.56, -0.98) * mm, "end": v(0.56, -0.98) * mm});
            skLineSegment(sketch, "E437", {"start": v(0.56, -0.98) * mm, "end": v(0.57, -0.99) * mm});
            skLineSegment(sketch, "E438", {"start": v(0.57, -0.99) * mm, "end": v(0.57, -1.02) * mm});
            skLineSegment(sketch, "E439", {"start": v(0.57, -1.02) * mm, "end": v(0.57, -1.03) * mm});
            skLineSegment(sketch, "E440", {"start": v(0.57, -1.03) * mm, "end": v(0.56, -1.04) * mm});
            skLineSegment(sketch, "E441", {"start": v(0.56, -1.04) * mm, "end": v(0.57, -1.08) * mm});
            skLineSegment(sketch, "E442", {"start": v(0.57, -1.08) * mm, "end": v(0.58, -1.1) * mm});
            skLineSegment(sketch, "E443", {"start": v(0.58, -1.1) * mm, "end": v(0.6, -1.12) * mm});
            skLineSegment(sketch, "E444", {"start": v(0.6, -1.12) * mm, "end": v(0.6, -1.11) * mm});
            skLineSegment(sketch, "E445", {"start": v(0.6, -1.11) * mm, "end": v(0.61, -1.1) * mm});
            skLineSegment(sketch, "E446", {"start": v(0.61, -1.1) * mm, "end": v(0.62, -1.1) * mm});
            skLineSegment(sketch, "E447", {"start": v(0.62, -1.1) * mm, "end": v(0.63, -1.1) * mm});
            skLineSegment(sketch, "E448", {"start": v(0.63, -1.1) * mm, "end": v(0.63, -1.1) * mm});
            skLineSegment(sketch, "E449", {"start": v(0.63, -1.1) * mm, "end": v(0.64, -1.1) * mm});
            skLineSegment(sketch, "E450", {"start": v(0.64, -1.1) * mm, "end": v(0.63, -1.1) * mm});
            skLineSegment(sketch, "E451", {"start": v(0.63, -1.1) * mm, "end": v(0.63, -1.11) * mm});
            skLineSegment(sketch, "E452", {"start": v(0.63, -1.11) * mm, "end": v(0.63, -1.12) * mm});
            skLineSegment(sketch, "E453", {"start": v(0.63, -1.12) * mm, "end": v(0.63, -1.14) * mm});
            skLineSegment(sketch, "E454", {"start": v(0.63, -1.14) * mm, "end": v(0.63, -1.15) * mm});
            skLineSegment(sketch, "E455", {"start": v(0.63, -1.15) * mm, "end": v(0.64, -1.15) * mm});
            skLineSegment(sketch, "E456", {"start": v(0.64, -1.15) * mm, "end": v(0.64, -1.15) * mm});
            skLineSegment(sketch, "E457", {"start": v(0.64, -1.15) * mm, "end": v(0.65, -1.15) * mm});
            skLineSegment(sketch, "E458", {"start": v(0.65, -1.15) * mm, "end": v(0.65, -1.15) * mm});
            skLineSegment(sketch, "E459", {"start": v(0.65, -1.15) * mm, "end": v(0.65, -1.14) * mm});
            skLineSegment(sketch, "E460", {"start": v(0.65, -1.14) * mm, "end": v(0.65, -1.13) * mm});
            skLineSegment(sketch, "E461", {"start": v(0.65, -1.13) * mm, "end": v(0.66, -1.12) * mm});
            skLineSegment(sketch, "E462", {"start": v(0.66, -1.12) * mm, "end": v(0.66, -1.11) * mm});
            skLineSegment(sketch, "E463", {"start": v(0.66, -1.11) * mm, "end": v(0.66, -1.1) * mm});
            skLineSegment(sketch, "E464", {"start": v(0.66, -1.1) * mm, "end": v(0.66, -1.1) * mm});
            skLineSegment(sketch, "E465", {"start": v(0.66, -1.1) * mm, "end": v(0.65, -1.08) * mm});
            skLineSegment(sketch, "E466", {"start": v(0.65, -1.08) * mm, "end": v(0.65, -1.08) * mm});
            skLineSegment(sketch, "E467", {"start": v(0.65, -1.08) * mm, "end": v(0.64, -1.08) * mm});
            skLineSegment(sketch, "E468", {"start": v(0.64, -1.08) * mm, "end": v(0.64, -1.06) * mm});
            skLineSegment(sketch, "E469", {"start": v(0.64, -1.06) * mm, "end": v(0.64, -1.03) * mm});
            skLineSegment(sketch, "E470", {"start": v(0.64, -1.03) * mm, "end": v(0.64, -1) * mm});
            skLineSegment(sketch, "E471", {"start": v(0.64, -1) * mm, "end": v(0.64, -1) * mm});
            skLineSegment(sketch, "E472", {"start": v(0.64, -1) * mm, "end": v(0.65, -1) * mm});
            skLineSegment(sketch, "E473", {"start": v(0.65, -1) * mm, "end": v(0.66, -1) * mm});
            skLineSegment(sketch, "E474", {"start": v(0.66, -1) * mm, "end": v(0.68, -1.02) * mm});
            skLineSegment(sketch, "E475", {"start": v(0.68, -1.02) * mm, "end": v(0.7, -1.05) * mm});
            skLineSegment(sketch, "E476", {"start": v(0.7, -1.05) * mm, "end": v(0.7, -1.06) * mm});
            skLineSegment(sketch, "E477", {"start": v(0.7, -1.06) * mm, "end": v(0.7, -1.06) * mm});
            skLineSegment(sketch, "E478", {"start": v(0.7, -1.06) * mm, "end": v(0.69, -1.06) * mm});
            skLineSegment(sketch, "E479", {"start": v(0.69, -1.06) * mm, "end": v(0.68, -1.07) * mm});
            skLineSegment(sketch, "E480", {"start": v(0.68, -1.07) * mm, "end": v(0.67, -1.08) * mm});
            skLineSegment(sketch, "E481", {"start": v(0.67, -1.08) * mm, "end": v(0.68, -1.1) * mm});
            skLineSegment(sketch, "E482", {"start": v(0.68, -1.1) * mm, "end": v(0.68, -1.11) * mm});
            skLineSegment(sketch, "E483", {"start": v(0.68, -1.11) * mm, "end": v(0.7, -1.13) * mm});
            skLineSegment(sketch, "E484", {"start": v(0.7, -1.13) * mm, "end": v(0.71, -1.14) * mm});
            skLineSegment(sketch, "E485", {"start": v(0.71, -1.14) * mm, "end": v(0.73, -1.15) * mm});
            skLineSegment(sketch, "E486", {"start": v(0.73, -1.15) * mm, "end": v(0.75, -1.15) * mm});
            skLineSegment(sketch, "E487", {"start": v(0.75, -1.15) * mm, "end": v(0.75, -1.15) * mm});
            skLineSegment(sketch, "E488", {"start": v(0.75, -1.15) * mm, "end": v(0.76, -1.15) * mm});
            skLineSegment(sketch, "E489", {"start": v(0.76, -1.15) * mm, "end": v(0.77, -1.15) * mm});
            skLineSegment(sketch, "E490", {"start": v(0.77, -1.15) * mm, "end": v(0.78, -1.13) * mm});
            skLineSegment(sketch, "E491", {"start": v(0.78, -1.13) * mm, "end": v(0.78, -1.1) * mm});
            skLineSegment(sketch, "E492", {"start": v(0.78, -1.1) * mm, "end": v(0.79, -1.04) * mm});
            skLineSegment(sketch, "E493", {"start": v(0.79, -1.04) * mm, "end": v(0.79, -1.02) * mm});
            skLineSegment(sketch, "E494", {"start": v(0.79, -1.02) * mm, "end": v(0.79, -1) * mm});
            skLineSegment(sketch, "E495", {"start": v(0.79, -1) * mm, "end": v(0.78, -0.93) * mm});
            skLineSegment(sketch, "E496", {"start": v(0.78, -0.93) * mm, "end": v(0.77, -0.83) * mm});
            skLineSegment(sketch, "E497", {"start": v(0.77, -0.83) * mm, "end": v(0.75, -0.77) * mm});
            skLineSegment(sketch, "E498", {"start": v(0.75, -0.77) * mm, "end": v(0.74, -0.75) * mm});
            skLineSegment(sketch, "E499", {"start": v(0.74, -0.75) * mm, "end": v(0.74, -0.75) * mm});
            skLineSegment(sketch, "E500", {"start": v(0.74, -0.75) * mm, "end": v(0.73, -0.74) * mm});
            skLineSegment(sketch, "E501", {"start": v(0.73, -0.74) * mm, "end": v(0.73, -0.72) * mm});
            skLineSegment(sketch, "E502", {"start": v(0.73, -0.72) * mm, "end": v(0.73, -0.71) * mm});
            skLineSegment(sketch, "E503", {"start": v(0.73, -0.71) * mm, "end": v(0.73, -0.7) * mm});
            skLineSegment(sketch, "E504", {"start": v(0.73, -0.7) * mm, "end": v(0.73, -0.69) * mm});
            skLineSegment(sketch, "E505", {"start": v(0.73, -0.69) * mm, "end": v(0.73, -0.67) * mm});
            skLineSegment(sketch, "E506", {"start": v(0.73, -0.67) * mm, "end": v(0.75, -0.68) * mm});
            skLineSegment(sketch, "E507", {"start": v(0.75, -0.68) * mm, "end": v(0.77, -0.7) * mm});
            skLineSegment(sketch, "E508", {"start": v(0.77, -0.7) * mm, "end": v(0.78, -0.7) * mm});
            skLineSegment(sketch, "E509", {"start": v(0.78, -0.7) * mm, "end": v(0.8, -0.71) * mm});
            skLineSegment(sketch, "E510", {"start": v(0.8, -0.71) * mm, "end": v(0.86, -0.76) * mm});
            skLineSegment(sketch, "E511", {"start": v(0.86, -0.76) * mm, "end": v(0.93, -0.83) * mm});
            skLineSegment(sketch, "E512", {"start": v(0.93, -0.83) * mm, "end": v(0.98, -0.9) * mm});
            skLineSegment(sketch, "E513", {"start": v(0.98, -0.9) * mm, "end": v(1.03, -0.96) * mm});
            skLineSegment(sketch, "E514", {"start": v(1.03, -0.96) * mm, "end": v(1.05, -1.02) * mm});
            skLineSegment(sketch, "E515", {"start": v(1.05, -1.02) * mm, "end": v(1.06, -1.07) * mm});
            skLineSegment(sketch, "E516", {"start": v(1.06, -1.07) * mm, "end": v(1.04, -1.1) * mm});
            skLineSegment(sketch, "E517", {"start": v(1.04, -1.1) * mm, "end": v(1, -1.12) * mm});
            skLineSegment(sketch, "E518", {"start": v(1, -1.12) * mm, "end": v(1, -1.12) * mm});
            skLineSegment(sketch, "E519", {"start": v(1, -1.12) * mm, "end": v(0.95, -1.13) * mm});
            skLineSegment(sketch, "E520", {"start": v(0.95, -1.13) * mm, "end": v(0.9, -1.14) * mm});
            skLineSegment(sketch, "E521", {"start": v(0.9, -1.14) * mm, "end": v(0.9, -1.15) * mm});
            skLineSegment(sketch, "E522", {"start": v(0.9, -1.15) * mm, "end": v(0.84, -1.17) * mm});
            skLineSegment(sketch, "E523", {"start": v(0.84, -1.17) * mm, "end": v(0.9, -1.16) * mm});
            skLineSegment(sketch, "E524", {"start": v(0.9, -1.16) * mm, "end": v(0.92, -1.16) * mm});
            skLineSegment(sketch, "E525", {"start": v(0.92, -1.16) * mm, "end": v(0.99, -1.15) * mm});
            skLineSegment(sketch, "E526", {"start": v(0.99, -1.15) * mm, "end": v(1.05, -1.13) * mm});
            skLineSegment(sketch, "E527", {"start": v(1.05, -1.13) * mm, "end": v(1.1, -1.12) * mm});
            skLineSegment(sketch, "E528", {"start": v(1.1, -1.12) * mm, "end": v(1.15, -1.1) * mm});
            skLineSegment(sketch, "E529", {"start": v(1.15, -1.1) * mm, "end": v(1.17, -1.1) * mm});
            skLineSegment(sketch, "E530", {"start": v(1.17, -1.1) * mm, "end": v(1.18, -1.1) * mm});
            skLineSegment(sketch, "E531", {"start": v(1.18, -1.1) * mm, "end": v(1.2, -1.08) * mm});
            skLineSegment(sketch, "E532", {"start": v(1.2, -1.08) * mm, "end": v(1.24, -1.07) * mm});
            skLineSegment(sketch, "E533", {"start": v(1.24, -1.07) * mm, "end": v(1.27, -1.06) * mm});
            skLineSegment(sketch, "E534", {"start": v(1.27, -1.06) * mm, "end": v(1.28, -1.06) * mm});
            skLineSegment(sketch, "E535", {"start": v(1.28, -1.06) * mm, "end": v(1.29, -1.06) * mm});
            skLineSegment(sketch, "E536", {"start": v(1.29, -1.06) * mm, "end": v(1.29, -1.06) * mm});
            skLineSegment(sketch, "E537", {"start": v(1.29, -1.06) * mm, "end": v(1.3, -1.05) * mm});
            skLineSegment(sketch, "E538", {"start": v(1.3, -1.05) * mm, "end": v(1.3, -1.05) * mm});
            skLineSegment(sketch, "E539", {"start": v(1.3, -1.05) * mm, "end": v(1.32, -1.04) * mm});
            skLineSegment(sketch, "E540", {"start": v(1.32, -1.04) * mm, "end": v(1.33, -1.03) * mm});
            skLineSegment(sketch, "E541", {"start": v(1.33, -1.03) * mm, "end": v(1.35, -1.02) * mm});
            skLineSegment(sketch, "E542", {"start": v(1.35, -1.02) * mm, "end": v(1.38, -1) * mm});
            skLineSegment(sketch, "E543", {"start": v(1.38, -1) * mm, "end": v(1.41, -0.97) * mm});
            skLineSegment(sketch, "E544", {"start": v(1.41, -0.97) * mm, "end": v(1.44, -0.94) * mm});
            skLineSegment(sketch, "E545", {"start": v(1.44, -0.94) * mm, "end": v(1.45, -0.93) * mm});
            skLineSegment(sketch, "E546", {"start": v(1.45, -0.93) * mm, "end": v(1.46, -0.92) * mm});
            skLineSegment(sketch, "E547", {"start": v(1.46, -0.92) * mm, "end": v(1.49, -0.9) * mm});
            skLineSegment(sketch, "E548", {"start": v(1.49, -0.9) * mm, "end": v(1.53, -0.85) * mm});
            skLineSegment(sketch, "E549", {"start": v(1.53, -0.85) * mm, "end": v(1.56, -0.8) * mm});
            skLineSegment(sketch, "E550", {"start": v(1.56, -0.8) * mm, "end": v(1.58, -0.78) * mm});
            skLineSegment(sketch, "E551", {"start": v(1.58, -0.78) * mm, "end": v(1.59, -0.77) * mm});
            skLineSegment(sketch, "E552", {"start": v(1.59, -0.77) * mm, "end": v(1.6, -0.77) * mm});
            skLineSegment(sketch, "E553", {"start": v(1.6, -0.77) * mm, "end": v(1.6, -0.74) * mm});
            skLineSegment(sketch, "E554", {"start": v(1.6, -0.74) * mm, "end": v(1.64, -0.69) * mm});
            skLineSegment(sketch, "E555", {"start": v(1.64, -0.69) * mm, "end": v(1.67, -0.64) * mm});
            skLineSegment(sketch, "E556", {"start": v(1.67, -0.64) * mm, "end": v(1.7, -0.6) * mm});
            skLineSegment(sketch, "E557", {"start": v(1.7, -0.6) * mm, "end": v(1.7, -0.59) * mm});
            skLineSegment(sketch, "E558", {"start": v(1.7, -0.59) * mm, "end": v(1.72, -0.57) * mm});
            skLineSegment(sketch, "E559", {"start": v(1.72, -0.57) * mm, "end": v(1.76, -0.5) * mm});
            skLineSegment(sketch, "E560", {"start": v(1.76, -0.5) * mm, "end": v(1.8, -0.43) * mm});
            skLineSegment(sketch, "E561", {"start": v(1.8, -0.43) * mm, "end": v(1.83, -0.36) * mm});
            skLineSegment(sketch, "E562", {"start": v(1.83, -0.36) * mm, "end": v(1.85, -0.28) * mm});
            skLineSegment(sketch, "E563", {"start": v(1.85, -0.28) * mm, "end": v(1.87, -0.2) * mm});
            skLineSegment(sketch, "E564", {"start": v(1.87, -0.2) * mm, "end": v(1.88, -0.1) * mm});
            skLineSegment(sketch, "E565", {"start": v(1.88, -0.1) * mm, "end": v(1.89, 0) * mm});
            skLineSegment(sketch, "E566", {"start": v(1.89, 0) * mm, "end": v(1.9, 0.09) * mm});
            skLineSegment(sketch, "E567", {"start": v(1.9, 0.09) * mm, "end": v(1.9, 0.12) * mm});
            skLineSegment(sketch, "E568", {"start": v(1.9, 0.12) * mm, "end": v(1.9, 0.15) * mm});
            skLineSegment(sketch, "E569", {"start": v(1.9, 0.15) * mm, "end": v(1.89, 0.26) * mm});
            skLineSegment(sketch, "E570", {"start": v(1.89, 0.26) * mm, "end": v(1.88, 0.35) * mm});
            skLineSegment(sketch, "E571", {"start": v(1.88, 0.35) * mm, "end": v(1.87, 0.4) * mm});
            skLineSegment(sketch, "E572", {"start": v(1.87, 0.4) * mm, "end": v(1.85, 0.44) * mm});
            skLineSegment(sketch, "E573", {"start": v(1.85, 0.44) * mm, "end": v(1.84, 0.44) * mm});
            skLineSegment(sketch, "E574", {"start": v(1.84, 0.44) * mm, "end": v(1.84, 0.45) * mm});
            skLineSegment(sketch, "E575", {"start": v(1.84, 0.45) * mm, "end": v(1.82, 0.47) * mm});
            skLineSegment(sketch, "E576", {"start": v(1.82, 0.47) * mm, "end": v(1.82, 0.48) * mm});
            skLineSegment(sketch, "E577", {"start": v(1.82, 0.48) * mm, "end": v(1.82, 0.49) * mm});
            skLineSegment(sketch, "E578", {"start": v(1.82, 0.49) * mm, "end": v(1.82, 0.5) * mm});
            skLineSegment(sketch, "E579", {"start": v(1.82, 0.5) * mm, "end": v(1.8, 0.5) * mm});
            skLineSegment(sketch, "E580", {"start": v(1.8, 0.5) * mm, "end": v(1.78, 0.55) * mm});
            skLineSegment(sketch, "E581", {"start": v(1.78, 0.55) * mm, "end": v(1.74, 0.6) * mm});
            skLineSegment(sketch, "E582", {"start": v(1.74, 0.6) * mm, "end": v(1.7, 0.65) * mm});
            skLineSegment(sketch, "E583", {"start": v(1.7, 0.65) * mm, "end": v(1.65, 0.7) * mm});
            skLineSegment(sketch, "E584", {"start": v(1.65, 0.7) * mm, "end": v(1.6, 0.75) * mm});
            skLineSegment(sketch, "E585", {"start": v(1.6, 0.75) * mm, "end": v(1.56, 0.8) * mm});
            skLineSegment(sketch, "E586", {"start": v(1.56, 0.8) * mm, "end": v(1.53, 0.82) * mm});
            skLineSegment(sketch, "E587", {"start": v(1.53, 0.82) * mm, "end": v(1.52, 0.83) * mm});
            skLineSegment(sketch, "E588", {"start": v(1.52, 0.83) * mm, "end": v(1.52, 0.84) * mm});
            skLineSegment(sketch, "E589", {"start": v(1.52, 0.84) * mm, "end": v(1.5, 0.85) * mm});
            skLineSegment(sketch, "E590", {"start": v(1.5, 0.85) * mm, "end": v(1.47, 0.87) * mm});
            skLineSegment(sketch, "E591", {"start": v(1.47, 0.87) * mm, "end": v(1.45, 0.9) * mm});
            skLineSegment(sketch, "E592", {"start": v(1.45, 0.9) * mm, "end": v(1.44, 0.9) * mm});
            skLineSegment(sketch, "E593", {"start": v(1.44, 0.9) * mm, "end": v(1.44, 0.9) * mm});
            skLineSegment(sketch, "E594", {"start": v(1.44, 0.9) * mm, "end": v(1.43, 0.91) * mm});
            skLineSegment(sketch, "E595", {"start": v(1.43, 0.91) * mm, "end": v(1.42, 0.91) * mm});
            skLineSegment(sketch, "E596", {"start": v(1.42, 0.91) * mm, "end": v(1.42, 0.91) * mm});
            skLineSegment(sketch, "E597", {"start": v(1.42, 0.91) * mm, "end": v(1.41, 0.91) * mm});
            skLineSegment(sketch, "E598", {"start": v(1.41, 0.91) * mm, "end": v(1.39, 0.92) * mm});
            skLineSegment(sketch, "E599", {"start": v(1.39, 0.92) * mm, "end": v(1.36, 0.93) * mm});
            skLineSegment(sketch, "E600", {"start": v(1.36, 0.93) * mm, "end": v(1.34, 0.94) * mm});
            skLineSegment(sketch, "E601", {"start": v(1.34, 0.94) * mm, "end": v(1.34, 0.94) * mm});
            skLineSegment(sketch, "E602", {"start": v(1.34, 0.94) * mm, "end": v(1.33, 0.95) * mm});
            skLineSegment(sketch, "E603", {"start": v(1.33, 0.95) * mm, "end": v(1.3, 0.96) * mm});
            skLineSegment(sketch, "E604", {"start": v(1.3, 0.96) * mm, "end": v(1.28, 0.97) * mm});
            skLineSegment(sketch, "E605", {"start": v(1.28, 0.97) * mm, "end": v(1.25, 0.98) * mm});
            skLineSegment(sketch, "E606", {"start": v(1.25, 0.98) * mm, "end": v(1.24, 0.99) * mm});
            skLineSegment(sketch, "E607", {"start": v(1.24, 0.99) * mm, "end": v(1.23, 0.99) * mm});
            skLineSegment(sketch, "E608", {"start": v(1.23, 0.99) * mm, "end": v(1.23, 0.99) * mm});
            skLineSegment(sketch, "E609", {"start": v(1.23, 0.99) * mm, "end": v(1.2, 1) * mm});
            skLineSegment(sketch, "E610", {"start": v(1.2, 1) * mm, "end": v(1.17, 1.02) * mm});
            skLineSegment(sketch, "E611", {"start": v(1.17, 1.02) * mm, "end": v(1.16, 1.02) * mm});
            skLineSegment(sketch, "E612", {"start": v(1.16, 1.02) * mm, "end": v(1.15, 1.03) * mm});
            skLineSegment(sketch, "E613", {"start": v(1.15, 1.03) * mm, "end": v(1.12, 1.04) * mm});
            skLineSegment(sketch, "E614", {"start": v(1.12, 1.04) * mm, "end": v(1.05, 1.06) * mm});
            skLineSegment(sketch, "E615", {"start": v(1.05, 1.06) * mm, "end": v(0.96, 1.07) * mm});
            skLineSegment(sketch, "E616", {"start": v(0.96, 1.07) * mm, "end": v(0.88, 1.07) * mm});
            skLineSegment(sketch, "E617", {"start": v(0.88, 1.07) * mm, "end": v(0.85, 1.07) * mm});
            skLineSegment(sketch, "E618", {"start": v(0.85, 1.07) * mm, "end": v(0.83, 1.07) * mm});
            skLineSegment(sketch, "E619", {"start": v(0.83, 1.07) * mm, "end": v(0.75, 1.08) * mm});
            skLineSegment(sketch, "E620", {"start": v(0.75, 1.08) * mm, "end": v(0.7, 1.1) * mm});
            skLineSegment(sketch, "E621", {"start": v(0.7, 1.1) * mm, "end": v(0.68, 1.1) * mm});
            skLineSegment(sketch, "E622", {"start": v(0.68, 1.1) * mm, "end": v(0.65, 1.11) * mm});
            skLineSegment(sketch, "E623", {"start": v(0.65, 1.11) * mm, "end": v(0.54, 1.15) * mm});
            skLineSegment(sketch, "E624", {"start": v(0.54, 1.15) * mm, "end": v(0.37, 1.18) * mm});
            skLineSegment(sketch, "E625", {"start": v(0.37, 1.18) * mm, "end": v(0.2, 1.2) * mm});
            skLineSegment(sketch, "E626", {"start": v(0.2, 1.2) * mm, "end": v(0.07, 1.19) * mm});
            skLineSegment(sketch, "E627", {"start": v(0.07, 1.19) * mm, "end": v(0.03, 1.18) * mm});
            skLineSegment(sketch, "E628", {"start": v(0.48, 1.13) * mm, "end": v(0.5, 1.13) * mm});
            skLineSegment(sketch, "E629", {"start": v(0.5, 1.13) * mm, "end": v(0.55, 1.12) * mm});
            skLineSegment(sketch, "E630", {"start": v(0.55, 1.12) * mm, "end": v(0.61, 1.1) * mm});
            skLineSegment(sketch, "E631", {"start": v(0.61, 1.1) * mm, "end": v(0.65, 1.09) * mm});
            skLineSegment(sketch, "E632", {"start": v(0.65, 1.09) * mm, "end": v(0.67, 1.08) * mm});
            skLineSegment(sketch, "E633", {"start": v(0.67, 1.08) * mm, "end": v(0.66, 1.07) * mm});
            skLineSegment(sketch, "E634", {"start": v(0.66, 1.07) * mm, "end": v(0.64, 1.06) * mm});
            skLineSegment(sketch, "E635", {"start": v(0.64, 1.06) * mm, "end": v(0.6, 1.04) * mm});
            skLineSegment(sketch, "E636", {"start": v(0.6, 1.04) * mm, "end": v(0.56, 1.03) * mm});
            skLineSegment(sketch, "E637", {"start": v(0.56, 1.03) * mm, "end": v(0.55, 1.03) * mm});
            skLineSegment(sketch, "E638", {"start": v(0.55, 1.03) * mm, "end": v(0.53, 1.02) * mm});
            skLineSegment(sketch, "E639", {"start": v(0.53, 1.02) * mm, "end": v(0.47, 1.02) * mm});
            skLineSegment(sketch, "E640", {"start": v(0.47, 1.02) * mm, "end": v(0.4, 1.01) * mm});
            skLineSegment(sketch, "E641", {"start": v(0.4, 1.01) * mm, "end": v(0.34, 1.02) * mm});
            skLineSegment(sketch, "E642", {"start": v(0.34, 1.02) * mm, "end": v(0.31, 1.03) * mm});
            skLineSegment(sketch, "E643", {"start": v(0.31, 1.03) * mm, "end": v(0.3, 1.03) * mm});
            skLineSegment(sketch, "E644", {"start": v(0.3, 1.03) * mm, "end": v(0.3, 1.03) * mm});
            skLineSegment(sketch, "E645", {"start": v(0.3, 1.03) * mm, "end": v(0.3, 1.04) * mm});
            skLineSegment(sketch, "E646", {"start": v(0.3, 1.04) * mm, "end": v(0.29, 1.04) * mm});
            skLineSegment(sketch, "E647", {"start": v(0.29, 1.04) * mm, "end": v(0.27, 1.04) * mm});
            skLineSegment(sketch, "E648", {"start": v(0.27, 1.04) * mm, "end": v(0.24, 1.03) * mm});
            skLineSegment(sketch, "E649", {"start": v(0.24, 1.03) * mm, "end": v(0.24, 1.03) * mm});
            skLineSegment(sketch, "E650", {"start": v(0.24, 1.03) * mm, "end": v(0.23, 1.03) * mm});
            skLineSegment(sketch, "E651", {"start": v(0.23, 1.03) * mm, "end": v(0.2, 1.03) * mm});
            skLineSegment(sketch, "E652", {"start": v(0.2, 1.03) * mm, "end": v(0.17, 1.02) * mm});
            skLineSegment(sketch, "E653", {"start": v(0.17, 1.02) * mm, "end": v(0.14, 1.03) * mm});
            skLineSegment(sketch, "E654", {"start": v(0.14, 1.03) * mm, "end": v(0.1, 1.04) * mm});
            skLineSegment(sketch, "E655", {"start": v(0.1, 1.04) * mm, "end": v(0.1, 1.04) * mm});
            skLineSegment(sketch, "E656", {"start": v(0.1, 1.04) * mm, "end": v(0.08, 1.04) * mm});
            skLineSegment(sketch, "E657", {"start": v(0.08, 1.04) * mm, "end": v(0.05, 1.05) * mm});
            skLineSegment(sketch, "E658", {"start": v(0.05, 1.05) * mm, "end": v(0, 1.06) * mm});
            skLineSegment(sketch, "E659", {"start": v(0, 1.06) * mm, "end": v(-0.03, 1.07) * mm});
            skLineSegment(sketch, "E660", {"start": v(-0.03, 1.07) * mm, "end": v(-0.05, 1.08) * mm});
            skLineSegment(sketch, "E661", {"start": v(-0.05, 1.08) * mm, "end": v(-0.06, 1.08) * mm});
            skLineSegment(sketch, "E662", {"start": v(-0.06, 1.08) * mm, "end": v(-0.07, 1.08) * mm});
            skLineSegment(sketch, "E663", {"start": v(-0.07, 1.08) * mm, "end": v(-0.1, 1.1) * mm});
            skLineSegment(sketch, "E664", {"start": v(-0.1, 1.1) * mm, "end": v(-0.12, 1.1) * mm});
            skLineSegment(sketch, "E665", {"start": v(-0.12, 1.1) * mm, "end": v(-0.11, 1.12) * mm});
            skLineSegment(sketch, "E666", {"start": v(-0.11, 1.12) * mm, "end": v(-0.09, 1.12) * mm});
            skLineSegment(sketch, "E667", {"start": v(-0.09, 1.12) * mm, "end": v(-0.08, 1.12) * mm});
            skLineSegment(sketch, "E668", {"start": v(-0.08, 1.12) * mm, "end": v(-0.07, 1.12) * mm});
            skLineSegment(sketch, "E669", {"start": v(-0.07, 1.12) * mm, "end": v(-0.06, 1.12) * mm});
            skLineSegment(sketch, "E670", {"start": v(-0.06, 1.12) * mm, "end": v(-0.04, 1.13) * mm});
            skLineSegment(sketch, "E671", {"start": v(-0.04, 1.13) * mm, "end": v(-0.04, 1.13) * mm});
            skLineSegment(sketch, "E672", {"start": v(-0.04, 1.13) * mm, "end": v(-0.03, 1.14) * mm});
            skLineSegment(sketch, "E673", {"start": v(-0.03, 1.14) * mm, "end": v(0.03, 1.16) * mm});
            skLineSegment(sketch, "E674", {"start": v(0.03, 1.16) * mm, "end": v(0.15, 1.17) * mm});
            skLineSegment(sketch, "E675", {"start": v(0.15, 1.17) * mm, "end": v(0.3, 1.16) * mm});
            skLineSegment(sketch, "E676", {"start": v(0.3, 1.16) * mm, "end": v(0.43, 1.14) * mm});
            skLineSegment(sketch, "E677", {"start": v(0.43, 1.14) * mm, "end": v(0.48, 1.13) * mm});
            skLineSegment(sketch, "E678", {"start": v(-0.3, 1.12) * mm, "end": v(-0.3, 1.12) * mm});
            skLineSegment(sketch, "E679", {"start": v(-0.3, 1.12) * mm, "end": v(-0.31, 1.11) * mm});
            skLineSegment(sketch, "E680", {"start": v(-0.31, 1.11) * mm, "end": v(-0.32, 1.1) * mm});
            skLineSegment(sketch, "E681", {"start": v(-0.32, 1.1) * mm, "end": v(-0.3, 1.1) * mm});
            skLineSegment(sketch, "E682", {"start": v(-0.3, 1.1) * mm, "end": v(-0.3, 1.1) * mm});
            skLineSegment(sketch, "E683", {"start": v(-0.3, 1.1) * mm, "end": v(-0.29, 1.1) * mm});
            skLineSegment(sketch, "E684", {"start": v(-0.29, 1.1) * mm, "end": v(-0.28, 1.1) * mm});
            skLineSegment(sketch, "E685", {"start": v(-0.28, 1.1) * mm, "end": v(-0.26, 1.1) * mm});
            skLineSegment(sketch, "E686", {"start": v(-0.26, 1.1) * mm, "end": v(-0.26, 1.1) * mm});
            skLineSegment(sketch, "E687", {"start": v(-0.26, 1.1) * mm, "end": v(-0.3, 1.07) * mm});
            skLineSegment(sketch, "E688", {"start": v(-0.3, 1.07) * mm, "end": v(-0.34, 1.06) * mm});
            skLineSegment(sketch, "E689", {"start": v(-0.34, 1.06) * mm, "end": v(-0.36, 1.05) * mm});
            skLineSegment(sketch, "E690", {"start": v(-0.36, 1.05) * mm, "end": v(-0.37, 1.05) * mm});
            skLineSegment(sketch, "E691", {"start": v(-0.37, 1.05) * mm, "end": v(-0.4, 1.03) * mm});
            skLineSegment(sketch, "E692", {"start": v(-0.4, 1.03) * mm, "end": v(-0.45, 1) * mm});
            skLineSegment(sketch, "E693", {"start": v(-0.45, 1) * mm, "end": v(-0.5, 0.98) * mm});
            skLineSegment(sketch, "E694", {"start": v(-0.5, 0.98) * mm, "end": v(-0.52, 0.96) * mm});
            skLineSegment(sketch, "E695", {"start": v(-0.52, 0.96) * mm, "end": v(-0.53, 0.96) * mm});
            skLineSegment(sketch, "E696", {"start": v(-0.53, 0.96) * mm, "end": v(-0.54, 0.95) * mm});
            skLineSegment(sketch, "E697", {"start": v(-0.54, 0.95) * mm, "end": v(-0.57, 0.93) * mm});
            skLineSegment(sketch, "E698", {"start": v(-0.57, 0.93) * mm, "end": v(-0.6, 0.91) * mm});
            skLineSegment(sketch, "E699", {"start": v(-0.6, 0.91) * mm, "end": v(-0.62, 0.9) * mm});
            skLineSegment(sketch, "E700", {"start": v(-0.62, 0.9) * mm, "end": v(-0.63, 0.9) * mm});
            skLineSegment(sketch, "E701", {"start": v(-0.63, 0.9) * mm, "end": v(-0.63, 0.9) * mm});
            skLineSegment(sketch, "E702", {"start": v(-0.63, 0.9) * mm, "end": v(-0.64, 0.9) * mm});
            skLineSegment(sketch, "E703", {"start": v(-0.64, 0.9) * mm, "end": v(-0.67, 0.88) * mm});
            skLineSegment(sketch, "E704", {"start": v(-0.67, 0.88) * mm, "end": v(-0.74, 0.83) * mm});
            skLineSegment(sketch, "E705", {"start": v(-0.74, 0.83) * mm, "end": v(-0.82, 0.76) * mm});
            skLineSegment(sketch, "E706", {"start": v(-0.82, 0.76) * mm, "end": v(-0.87, 0.71) * mm});
            skLineSegment(sketch, "E707", {"start": v(-0.87, 0.71) * mm, "end": v(-0.89, 0.7) * mm});
            skLineSegment(sketch, "E708", {"start": v(-0.89, 0.7) * mm, "end": v(-0.94, 0.64) * mm});
            skLineSegment(sketch, "E709", {"start": v(-0.94, 0.64) * mm, "end": v(-0.9, 0.68) * mm});
            skLineSegment(sketch, "E710", {"start": v(-0.9, 0.68) * mm, "end": v(-0.84, 0.72) * mm});
            skLineSegment(sketch, "E711", {"start": v(-0.84, 0.72) * mm, "end": v(-0.8, 0.68) * mm});
            skLineSegment(sketch, "E712", {"start": v(-0.8, 0.68) * mm, "end": v(-0.8, 0.67) * mm});
            skLineSegment(sketch, "E713", {"start": v(-0.8, 0.67) * mm, "end": v(-0.78, 0.65) * mm});
            skLineSegment(sketch, "E714", {"start": v(-0.78, 0.65) * mm, "end": v(-0.76, 0.62) * mm});
            skLineSegment(sketch, "E715", {"start": v(-0.76, 0.62) * mm, "end": v(-0.74, 0.59) * mm});
            skLineSegment(sketch, "E716", {"start": v(-0.74, 0.59) * mm, "end": v(-0.73, 0.56) * mm});
            skLineSegment(sketch, "E717", {"start": v(-0.73, 0.56) * mm, "end": v(-0.72, 0.53) * mm});
            skLineSegment(sketch, "E718", {"start": v(-0.72, 0.53) * mm, "end": v(-0.72, 0.51) * mm});
            skLineSegment(sketch, "E719", {"start": v(-0.72, 0.51) * mm, "end": v(-0.72, 0.5) * mm});
            skLineSegment(sketch, "E720", {"start": v(-0.72, 0.5) * mm, "end": v(-0.73, 0.5) * mm});
            skLineSegment(sketch, "E721", {"start": v(-0.73, 0.5) * mm, "end": v(-0.73, 0.5) * mm});
            skLineSegment(sketch, "E722", {"start": v(-0.73, 0.5) * mm, "end": v(-0.73, 0.49) * mm});
            skLineSegment(sketch, "E723", {"start": v(-0.73, 0.49) * mm, "end": v(-0.72, 0.48) * mm});
            skLineSegment(sketch, "E724", {"start": v(-0.72, 0.48) * mm, "end": v(-0.72, 0.48) * mm});
            skLineSegment(sketch, "E725", {"start": v(-0.72, 0.48) * mm, "end": v(-0.7, 0.47) * mm});
            skLineSegment(sketch, "E726", {"start": v(-0.7, 0.47) * mm, "end": v(-0.7, 0.45) * mm});
            skLineSegment(sketch, "E727", {"start": v(-0.7, 0.45) * mm, "end": v(-0.68, 0.43) * mm});
            skLineSegment(sketch, "E728", {"start": v(-0.68, 0.43) * mm, "end": v(-0.67, 0.4) * mm});
            skLineSegment(sketch, "E729", {"start": v(-0.67, 0.4) * mm, "end": v(-0.66, 0.37) * mm});
            skLineSegment(sketch, "E730", {"start": v(-0.66, 0.37) * mm, "end": v(-0.65, 0.35) * mm});
            skLineSegment(sketch, "E731", {"start": v(-0.65, 0.35) * mm, "end": v(-0.64, 0.33) * mm});
            skLineSegment(sketch, "E732", {"start": v(-0.64, 0.33) * mm, "end": v(-0.65, 0.32) * mm});
            skLineSegment(sketch, "E733", {"start": v(-0.65, 0.32) * mm, "end": v(-0.65, 0.32) * mm});
            skLineSegment(sketch, "E734", {"start": v(-0.65, 0.32) * mm, "end": v(-0.66, 0.33) * mm});
            skLineSegment(sketch, "E735", {"start": v(-0.66, 0.33) * mm, "end": v(-0.68, 0.35) * mm});
            skLineSegment(sketch, "E736", {"start": v(-0.68, 0.35) * mm, "end": v(-0.7, 0.37) * mm});
            skLineSegment(sketch, "E737", {"start": v(-0.7, 0.37) * mm, "end": v(-0.7, 0.37) * mm});
            skLineSegment(sketch, "E738", {"start": v(-0.7, 0.37) * mm, "end": v(-0.7, 0.4) * mm});
            skLineSegment(sketch, "E739", {"start": v(-0.7, 0.4) * mm, "end": v(-0.76, 0.44) * mm});
            skLineSegment(sketch, "E740", {"start": v(-0.76, 0.44) * mm, "end": v(-0.85, 0.5) * mm});
            skLineSegment(sketch, "E741", {"start": v(-0.85, 0.5) * mm, "end": v(-0.94, 0.52) * mm});
            skLineSegment(sketch, "E742", {"start": v(-0.94, 0.52) * mm, "end": v(-1, 0.52) * mm});
            skLineSegment(sketch, "E743", {"start": v(-1, 0.52) * mm, "end": v(-1, 0.51) * mm});
            skLineSegment(sketch, "E744", {"start": v(-1, 0.51) * mm, "end": v(-1, 0.51) * mm});
            skLineSegment(sketch, "E745", {"start": v(-1, 0.51) * mm, "end": v(-1.02, 0.5) * mm});
            skLineSegment(sketch, "E746", {"start": v(-1.02, 0.5) * mm, "end": v(-1.03, 0.52) * mm});
            skLineSegment(sketch, "E747", {"start": v(-1.03, 0.52) * mm, "end": v(-1.03, 0.54) * mm});
            skLineSegment(sketch, "E748", {"start": v(-1.03, 0.54) * mm, "end": v(-1.02, 0.57) * mm});
            skLineSegment(sketch, "E749", {"start": v(-1.02, 0.57) * mm, "end": v(-1, 0.61) * mm});
            skLineSegment(sketch, "E750", {"start": v(-1, 0.61) * mm, "end": v(-0.98, 0.65) * mm});
            skLineSegment(sketch, "E751", {"start": v(-0.98, 0.65) * mm, "end": v(-0.96, 0.7) * mm});
            skLineSegment(sketch, "E752", {"start": v(-0.96, 0.7) * mm, "end": v(-0.94, 0.72) * mm});
            skLineSegment(sketch, "E753", {"start": v(-0.94, 0.72) * mm, "end": v(-0.93, 0.73) * mm});
            skLineSegment(sketch, "E754", {"start": v(-0.93, 0.73) * mm, "end": v(-0.93, 0.74) * mm});
            skLineSegment(sketch, "E755", {"start": v(-0.93, 0.74) * mm, "end": v(-0.9, 0.77) * mm});
            skLineSegment(sketch, "E756", {"start": v(-0.9, 0.77) * mm, "end": v(-0.87, 0.8) * mm});
            skLineSegment(sketch, "E757", {"start": v(-0.87, 0.8) * mm, "end": v(-0.86, 0.83) * mm});
            skLineSegment(sketch, "E758", {"start": v(-0.86, 0.83) * mm, "end": v(-0.85, 0.84) * mm});
            skLineSegment(sketch, "E759", {"start": v(-0.85, 0.84) * mm, "end": v(-0.85, 0.84) * mm});
            skLineSegment(sketch, "E760", {"start": v(-0.85, 0.84) * mm, "end": v(-0.85, 0.85) * mm});
            skLineSegment(sketch, "E761", {"start": v(-0.85, 0.85) * mm, "end": v(-0.85, 0.85) * mm});
            skLineSegment(sketch, "E762", {"start": v(-0.85, 0.85) * mm, "end": v(-0.84, 0.85) * mm});
            skLineSegment(sketch, "E763", {"start": v(-0.84, 0.85) * mm, "end": v(-0.84, 0.85) * mm});
            skLineSegment(sketch, "E764", {"start": v(-0.84, 0.85) * mm, "end": v(-0.83, 0.85) * mm});
            skLineSegment(sketch, "E765", {"start": v(-0.83, 0.85) * mm, "end": v(-0.82, 0.85) * mm});
            skLineSegment(sketch, "E766", {"start": v(-0.82, 0.85) * mm, "end": v(-0.81, 0.86) * mm});
            skLineSegment(sketch, "E767", {"start": v(-0.81, 0.86) * mm, "end": v(-0.81, 0.86) * mm});
            skLineSegment(sketch, "E768", {"start": v(-0.81, 0.86) * mm, "end": v(-0.81, 0.87) * mm});
            skLineSegment(sketch, "E769", {"start": v(-0.81, 0.87) * mm, "end": v(-0.8, 0.89) * mm});
            skLineSegment(sketch, "E770", {"start": v(-0.8, 0.89) * mm, "end": v(-0.76, 0.92) * mm});
            skLineSegment(sketch, "E771", {"start": v(-0.76, 0.92) * mm, "end": v(-0.71, 0.96) * mm});
            skLineSegment(sketch, "E772", {"start": v(-0.71, 0.96) * mm, "end": v(-0.66, 1) * mm});
            skLineSegment(sketch, "E773", {"start": v(-0.66, 1) * mm, "end": v(-0.6, 1.02) * mm});
            skLineSegment(sketch, "E774", {"start": v(-0.6, 1.02) * mm, "end": v(-0.55, 1.05) * mm});
            skLineSegment(sketch, "E775", {"start": v(-0.55, 1.05) * mm, "end": v(-0.5, 1.07) * mm});
            skLineSegment(sketch, "E776", {"start": v(-0.5, 1.07) * mm, "end": v(-0.48, 1.08) * mm});
            skLineSegment(sketch, "E777", {"start": v(-0.48, 1.08) * mm, "end": v(-0.48, 1.08) * mm});
            skLineSegment(sketch, "E778", {"start": v(-0.48, 1.08) * mm, "end": v(-0.47, 1.08) * mm});
            skLineSegment(sketch, "E779", {"start": v(-0.47, 1.08) * mm, "end": v(-0.45, 1.08) * mm});
            skLineSegment(sketch, "E780", {"start": v(-0.45, 1.08) * mm, "end": v(-0.42, 1.1) * mm});
            skLineSegment(sketch, "E781", {"start": v(-0.42, 1.1) * mm, "end": v(-0.41, 1.1) * mm});
            skLineSegment(sketch, "E782", {"start": v(-0.41, 1.1) * mm, "end": v(-0.4, 1.1) * mm});
            skLineSegment(sketch, "E783", {"start": v(-0.4, 1.1) * mm, "end": v(-0.35, 1.12) * mm});
            skLineSegment(sketch, "E784", {"start": v(-0.35, 1.12) * mm, "end": v(-0.3, 1.13) * mm});
            skLineSegment(sketch, "E785", {"start": v(-0.3, 1.13) * mm, "end": v(-0.3, 1.13) * mm});
            skLineSegment(sketch, "E786", {"start": v(-0.3, 1.13) * mm, "end": v(-0.29, 1.13) * mm});
            skLineSegment(sketch, "E787", {"start": v(-0.29, 1.13) * mm, "end": v(-0.3, 1.12) * mm});
            skLineSegment(sketch, "E788", {"start": v(-0.03, 1.05) * mm, "end": v(-0.01, 1.04) * mm});
            skLineSegment(sketch, "E789", {"start": v(-0.01, 1.04) * mm, "end": v(0.04, 1.03) * mm});
            skLineSegment(sketch, "E790", {"start": v(0.04, 1.03) * mm, "end": v(0.1, 1.01) * mm});
            skLineSegment(sketch, "E791", {"start": v(0.1, 1.01) * mm, "end": v(0.14, 1) * mm});
            skLineSegment(sketch, "E792", {"start": v(0.14, 1) * mm, "end": v(0.19, 1) * mm});
            skLineSegment(sketch, "E793", {"start": v(0.19, 1) * mm, "end": v(0.2, 1) * mm});
            skLineSegment(sketch, "E794", {"start": v(0.2, 1) * mm, "end": v(0.2, 1) * mm});
            skLineSegment(sketch, "E795", {"start": v(0.2, 1) * mm, "end": v(0.2, 0.99) * mm});
            skLineSegment(sketch, "E796", {"start": v(0.2, 0.99) * mm, "end": v(0.2, 0.96) * mm});
            skLineSegment(sketch, "E797", {"start": v(0.2, 0.96) * mm, "end": v(0.2, 0.93) * mm});
            skLineSegment(sketch, "E798", {"start": v(0.2, 0.93) * mm, "end": v(0.18, 0.9) * mm});
            skLineSegment(sketch, "E799", {"start": v(0.18, 0.9) * mm, "end": v(0.18, 0.89) * mm});
            skLineSegment(sketch, "E800", {"start": v(0.18, 0.89) * mm, "end": v(0.17, 0.88) * mm});
            skLineSegment(sketch, "E801", {"start": v(0.17, 0.88) * mm, "end": v(0.16, 0.84) * mm});
            skLineSegment(sketch, "E802", {"start": v(0.16, 0.84) * mm, "end": v(0.14, 0.77) * mm});
            skLineSegment(sketch, "E803", {"start": v(0.14, 0.77) * mm, "end": v(0.13, 0.7) * mm});
            skLineSegment(sketch, "E804", {"start": v(0.13, 0.7) * mm, "end": v(0.12, 0.65) * mm});
            skLineSegment(sketch, "E805", {"start": v(0.12, 0.65) * mm, "end": v(0.12, 0.63) * mm});
            skLineSegment(sketch, "E806", {"start": v(0.12, 0.63) * mm, "end": v(0.12, 0.64) * mm});
            skLineSegment(sketch, "E807", {"start": v(0.12, 0.64) * mm, "end": v(0.1, 0.66) * mm});
            skLineSegment(sketch, "E808", {"start": v(0.1, 0.66) * mm, "end": v(0.09, 0.69) * mm});
            skLineSegment(sketch, "E809", {"start": v(0.09, 0.69) * mm, "end": v(0.07, 0.72) * mm});
            skLineSegment(sketch, "E810", {"start": v(0.07, 0.72) * mm, "end": v(0.06, 0.73) * mm});
            skLineSegment(sketch, "E811", {"start": v(0.06, 0.73) * mm, "end": v(0.05, 0.75) * mm});
            skLineSegment(sketch, "E812", {"start": v(0.05, 0.75) * mm, "end": v(0.02, 0.82) * mm});
            skLineSegment(sketch, "E813", {"start": v(0.02, 0.82) * mm, "end": v(-0.03, 0.89) * mm});
            skLineSegment(sketch, "E814", {"start": v(-0.03, 0.89) * mm, "end": v(-0.07, 0.95) * mm});
            skLineSegment(sketch, "E815", {"start": v(-0.07, 0.95) * mm, "end": v(-0.11, 1) * mm});
            skLineSegment(sketch, "E816", {"start": v(-0.11, 1) * mm, "end": v(-0.12, 1) * mm});
            skLineSegment(sketch, "E817", {"start": v(-0.12, 1) * mm, "end": v(-0.13, 1.01) * mm});
            skLineSegment(sketch, "E818", {"start": v(-0.13, 1.01) * mm, "end": v(-0.15, 1.04) * mm});
            skLineSegment(sketch, "E819", {"start": v(-0.15, 1.04) * mm, "end": v(-0.17, 1.06) * mm});
            skLineSegment(sketch, "E820", {"start": v(-0.17, 1.06) * mm, "end": v(-0.18, 1.07) * mm});
            skLineSegment(sketch, "E821", {"start": v(-0.18, 1.07) * mm, "end": v(-0.17, 1.08) * mm});
            skLineSegment(sketch, "E822", {"start": v(-0.17, 1.08) * mm, "end": v(-0.16, 1.08) * mm});
            skLineSegment(sketch, "E823", {"start": v(-0.16, 1.08) * mm, "end": v(-0.13, 1.08) * mm});
            skLineSegment(sketch, "E824", {"start": v(-0.13, 1.08) * mm, "end": v(-0.08, 1.07) * mm});
            skLineSegment(sketch, "E825", {"start": v(-0.08, 1.07) * mm, "end": v(-0.04, 1.05) * mm});
            skLineSegment(sketch, "E826", {"start": v(-0.04, 1.05) * mm, "end": v(-0.03, 1.05) * mm});
            skLineSegment(sketch, "E827", {"start": v(-0.1, 0.92) * mm, "end": v(-0.09, 0.91) * mm});
            skLineSegment(sketch, "E828", {"start": v(-0.09, 0.91) * mm, "end": v(-0.07, 0.88) * mm});
            skLineSegment(sketch, "E829", {"start": v(-0.07, 0.88) * mm, "end": v(-0.04, 0.83) * mm});
            skLineSegment(sketch, "E830", {"start": v(-0.04, 0.83) * mm, "end": v(0, 0.78) * mm});
            skLineSegment(sketch, "E831", {"start": v(0, 0.78) * mm, "end": v(0.03, 0.72) * mm});
            skLineSegment(sketch, "E832", {"start": v(0.03, 0.72) * mm, "end": v(0.06, 0.66) * mm});
            skLineSegment(sketch, "E833", {"start": v(0.06, 0.66) * mm, "end": v(0.09, 0.62) * mm});
            skLineSegment(sketch, "E834", {"start": v(0.09, 0.62) * mm, "end": v(0.1, 0.58) * mm});
            skLineSegment(sketch, "E835", {"start": v(0.1, 0.58) * mm, "end": v(0.1, 0.57) * mm});
            skLineSegment(sketch, "E836", {"start": v(0.1, 0.57) * mm, "end": v(0.1, 0.56) * mm});
            skLineSegment(sketch, "E837", {"start": v(0.1, 0.56) * mm, "end": v(0.1, 0.56) * mm});
            skLineSegment(sketch, "E838", {"start": v(0.1, 0.56) * mm, "end": v(0.09, 0.57) * mm});
            skLineSegment(sketch, "E839", {"start": v(0.09, 0.57) * mm, "end": v(0.06, 0.58) * mm});
            skLineSegment(sketch, "E840", {"start": v(0.06, 0.58) * mm, "end": v(0.04, 0.6) * mm});
            skLineSegment(sketch, "E841", {"start": v(0.04, 0.6) * mm, "end": v(0.04, 0.6) * mm});
            skLineSegment(sketch, "E842", {"start": v(0.04, 0.6) * mm, "end": v(0.03, 0.6) * mm});
            skLineSegment(sketch, "E843", {"start": v(0.03, 0.6) * mm, "end": v(0, 0.62) * mm});
            skLineSegment(sketch, "E844", {"start": v(0, 0.62) * mm, "end": v(-0.02, 0.63) * mm});
            skLineSegment(sketch, "E845", {"start": v(-0.02, 0.63) * mm, "end": v(-0.04, 0.64) * mm});
            skLineSegment(sketch, "E846", {"start": v(-0.04, 0.64) * mm, "end": v(-0.05, 0.65) * mm});
            skLineSegment(sketch, "E847", {"start": v(-0.05, 0.65) * mm, "end": v(-0.06, 0.65) * mm});
            skLineSegment(sketch, "E848", {"start": v(-0.06, 0.65) * mm, "end": v(-0.06, 0.65) * mm});
            skLineSegment(sketch, "E849", {"start": v(-0.06, 0.65) * mm, "end": v(-0.07, 0.64) * mm});
            skLineSegment(sketch, "E850", {"start": v(-0.07, 0.64) * mm, "end": v(-0.1, 0.64) * mm});
            skLineSegment(sketch, "E851", {"start": v(-0.1, 0.64) * mm, "end": v(-0.12, 0.63) * mm});
            skLineSegment(sketch, "E852", {"start": v(-0.12, 0.63) * mm, "end": v(-0.15, 0.62) * mm});
            skLineSegment(sketch, "E853", {"start": v(-0.15, 0.62) * mm, "end": v(-0.18, 0.6) * mm});
            skLineSegment(sketch, "E854", {"start": v(-0.18, 0.6) * mm, "end": v(-0.21, 0.6) * mm});
            skLineSegment(sketch, "E855", {"start": v(-0.21, 0.6) * mm, "end": v(-0.23, 0.58) * mm});
            skLineSegment(sketch, "E856", {"start": v(-0.23, 0.58) * mm, "end": v(-0.25, 0.58) * mm});
            skLineSegment(sketch, "E857", {"start": v(-0.25, 0.58) * mm, "end": v(-0.25, 0.58) * mm});
            skLineSegment(sketch, "E858", {"start": v(-0.25, 0.58) * mm, "end": v(-0.25, 0.57) * mm});
            skLineSegment(sketch, "E859", {"start": v(-0.25, 0.57) * mm, "end": v(-0.26, 0.57) * mm});
            skLineSegment(sketch, "E860", {"start": v(-0.26, 0.57) * mm, "end": v(-0.26, 0.57) * mm});
            skLineSegment(sketch, "E861", {"start": v(-0.26, 0.57) * mm, "end": v(-0.26, 0.6) * mm});
            skLineSegment(sketch, "E862", {"start": v(-0.26, 0.6) * mm, "end": v(-0.26, 0.62) * mm});
            skLineSegment(sketch, "E863", {"start": v(-0.26, 0.62) * mm, "end": v(-0.26, 0.63) * mm});
            skLineSegment(sketch, "E864", {"start": v(-0.26, 0.63) * mm, "end": v(-0.26, 0.64) * mm});
            skLineSegment(sketch, "E865", {"start": v(-0.26, 0.64) * mm, "end": v(-0.25, 0.71) * mm});
            skLineSegment(sketch, "E866", {"start": v(-0.25, 0.71) * mm, "end": v(-0.25, 0.78) * mm});
            skLineSegment(sketch, "E867", {"start": v(-0.25, 0.78) * mm, "end": v(-0.25, 0.8) * mm});
            skLineSegment(sketch, "E868", {"start": v(-0.25, 0.8) * mm, "end": v(-0.24, 0.81) * mm});
            skLineSegment(sketch, "E869", {"start": v(-0.24, 0.81) * mm, "end": v(-0.23, 0.88) * mm});
            skLineSegment(sketch, "E870", {"start": v(-0.23, 0.88) * mm, "end": v(-0.22, 0.96) * mm});
            skLineSegment(sketch, "E871", {"start": v(-0.22, 0.96) * mm, "end": v(-0.2, 1.02) * mm});
            skLineSegment(sketch, "E872", {"start": v(-0.2, 1.02) * mm, "end": v(-0.18, 1.04) * mm});
            skLineSegment(sketch, "E873", {"start": v(-0.18, 1.04) * mm, "end": v(-0.18, 1.04) * mm});
            skLineSegment(sketch, "E874", {"start": v(-0.18, 1.04) * mm, "end": v(-0.17, 1.03) * mm});
            skLineSegment(sketch, "E875", {"start": v(-0.17, 1.03) * mm, "end": v(-0.15, 1) * mm});
            skLineSegment(sketch, "E876", {"start": v(-0.15, 1) * mm, "end": v(-0.13, 0.97) * mm});
            skLineSegment(sketch, "E877", {"start": v(-0.13, 0.97) * mm, "end": v(-0.1, 0.93) * mm});
            skLineSegment(sketch, "E878", {"start": v(-0.1, 0.93) * mm, "end": v(-0.1, 0.92) * mm});
            skLineSegment(sketch, "E879", {"start": v(1, 1.04) * mm, "end": v(1, 1.03) * mm});
            skLineSegment(sketch, "E880", {"start": v(1, 1.03) * mm, "end": v(1, 1.03) * mm});
            skLineSegment(sketch, "E881", {"start": v(1, 1.03) * mm, "end": v(1.02, 1.02) * mm});
            skLineSegment(sketch, "E882", {"start": v(1.02, 1.02) * mm, "end": v(1.03, 1.01) * mm});
            skLineSegment(sketch, "E883", {"start": v(1.03, 1.01) * mm, "end": v(1.04, 1) * mm});
            skLineSegment(sketch, "E884", {"start": v(1.04, 1) * mm, "end": v(1.05, 0.98) * mm});
            skLineSegment(sketch, "E885", {"start": v(1.05, 0.98) * mm, "end": v(1.06, 0.95) * mm});
            skLineSegment(sketch, "E886", {"start": v(1.06, 0.95) * mm, "end": v(1.07, 0.92) * mm});
            skLineSegment(sketch, "E887", {"start": v(1.07, 0.92) * mm, "end": v(1.08, 0.89) * mm});
            skLineSegment(sketch, "E888", {"start": v(1.08, 0.89) * mm, "end": v(1.09, 0.88) * mm});
            skLineSegment(sketch, "E889", {"start": v(1.09, 0.88) * mm, "end": v(1.1, 0.86) * mm});
            skLineSegment(sketch, "E890", {"start": v(1.1, 0.86) * mm, "end": v(1.1, 0.8) * mm});
            skLineSegment(sketch, "E891", {"start": v(1.1, 0.8) * mm, "end": v(1.12, 0.73) * mm});
            skLineSegment(sketch, "E892", {"start": v(1.12, 0.73) * mm, "end": v(1.13, 0.66) * mm});
            skLineSegment(sketch, "E893", {"start": v(1.13, 0.66) * mm, "end": v(1.14, 0.59) * mm});
            skLineSegment(sketch, "E894", {"start": v(1.14, 0.59) * mm, "end": v(1.14, 0.52) * mm});
            skLineSegment(sketch, "E895", {"start": v(1.14, 0.52) * mm, "end": v(1.14, 0.47) * mm});
            skLineSegment(sketch, "E896", {"start": v(1.14, 0.47) * mm, "end": v(1.13, 0.44) * mm});
            skLineSegment(sketch, "E897", {"start": v(1.13, 0.44) * mm, "end": v(1.12, 0.42) * mm});
            skLineSegment(sketch, "E898", {"start": v(1.12, 0.42) * mm, "end": v(1.12, 0.42) * mm});
            skLineSegment(sketch, "E899", {"start": v(1.12, 0.42) * mm, "end": v(1.11, 0.43) * mm});
            skLineSegment(sketch, "E900", {"start": v(1.11, 0.43) * mm, "end": v(1.1, 0.44) * mm});
            skLineSegment(sketch, "E901", {"start": v(1.1, 0.44) * mm, "end": v(1.1, 0.45) * mm});
            skLineSegment(sketch, "E902", {"start": v(1.1, 0.45) * mm, "end": v(1.1, 0.46) * mm});
            skLineSegment(sketch, "E903", {"start": v(1.1, 0.46) * mm, "end": v(1.1, 0.5) * mm});
            skLineSegment(sketch, "E904", {"start": v(1.1, 0.5) * mm, "end": v(1.08, 0.56) * mm});
            skLineSegment(sketch, "E905", {"start": v(1.08, 0.56) * mm, "end": v(1.04, 0.64) * mm});
            skLineSegment(sketch, "E906", {"start": v(1.04, 0.64) * mm, "end": v(1, 0.73) * mm});
            skLineSegment(sketch, "E907", {"start": v(1, 0.73) * mm, "end": v(0.95, 0.81) * mm});
            skLineSegment(sketch, "E908", {"start": v(0.95, 0.81) * mm, "end": v(0.9, 0.89) * mm});
            skLineSegment(sketch, "E909", {"start": v(0.9, 0.89) * mm, "end": v(0.86, 0.95) * mm});
            skLineSegment(sketch, "E910", {"start": v(0.86, 0.95) * mm, "end": v(0.83, 0.98) * mm});
            skLineSegment(sketch, "E911", {"start": v(0.83, 0.98) * mm, "end": v(0.82, 0.98) * mm});
            skLineSegment(sketch, "E912", {"start": v(0.82, 0.98) * mm, "end": v(0.82, 0.99) * mm});
            skLineSegment(sketch, "E913", {"start": v(0.82, 0.99) * mm, "end": v(0.8, 1) * mm});
            skLineSegment(sketch, "E914", {"start": v(0.8, 1) * mm, "end": v(0.78, 1.02) * mm});
            skLineSegment(sketch, "E915", {"start": v(0.78, 1.02) * mm, "end": v(0.77, 1.03) * mm});
            skLineSegment(sketch, "E916", {"start": v(0.77, 1.03) * mm, "end": v(0.76, 1.04) * mm});
            skLineSegment(sketch, "E917", {"start": v(0.76, 1.04) * mm, "end": v(0.76, 1.04) * mm});
            skLineSegment(sketch, "E918", {"start": v(0.76, 1.04) * mm, "end": v(0.8, 1.05) * mm});
            skLineSegment(sketch, "E919", {"start": v(0.8, 1.05) * mm, "end": v(0.86, 1.05) * mm});
            skLineSegment(sketch, "E920", {"start": v(0.86, 1.05) * mm, "end": v(0.94, 1.05) * mm});
            skLineSegment(sketch, "E921", {"start": v(0.94, 1.05) * mm, "end": v(0.98, 1.04) * mm});
            skLineSegment(sketch, "E922", {"start": v(0.98, 1.04) * mm, "end": v(1, 1.04) * mm});
            skLineSegment(sketch, "E923", {"start": v(0.75, 0.97) * mm, "end": v(0.77, 0.94) * mm});
            skLineSegment(sketch, "E924", {"start": v(0.77, 0.94) * mm, "end": v(0.84, 0.79) * mm});
            skLineSegment(sketch, "E925", {"start": v(0.84, 0.79) * mm, "end": v(0.88, 0.64) * mm});
            skLineSegment(sketch, "E926", {"start": v(0.88, 0.64) * mm, "end": v(0.88, 0.61) * mm});
            skLineSegment(sketch, "E927", {"start": v(0.88, 0.61) * mm, "end": v(0.9, 0.5) * mm});
            skLineSegment(sketch, "E928", {"start": v(0.9, 0.5) * mm, "end": v(0.82, 0.5) * mm});
            skLineSegment(sketch, "E929", {"start": v(0.82, 0.5) * mm, "end": v(0.8, 0.5) * mm});
            skLineSegment(sketch, "E930", {"start": v(0.8, 0.5) * mm, "end": v(0.75, 0.5) * mm});
            skLineSegment(sketch, "E931", {"start": v(0.75, 0.5) * mm, "end": v(0.69, 0.5) * mm});
            skLineSegment(sketch, "E932", {"start": v(0.69, 0.5) * mm, "end": v(0.64, 0.48) * mm});
            skLineSegment(sketch, "E933", {"start": v(0.64, 0.48) * mm, "end": v(0.6, 0.46) * mm});
            skLineSegment(sketch, "E934", {"start": v(0.6, 0.46) * mm, "end": v(0.6, 0.45) * mm});
            skLineSegment(sketch, "E935", {"start": v(0.6, 0.45) * mm, "end": v(0.6, 0.45) * mm});
            skLineSegment(sketch, "E936", {"start": v(0.6, 0.45) * mm, "end": v(0.57, 0.43) * mm});
            skLineSegment(sketch, "E937", {"start": v(0.57, 0.43) * mm, "end": v(0.56, 0.43) * mm});
            skLineSegment(sketch, "E938", {"start": v(0.56, 0.43) * mm, "end": v(0.56, 0.45) * mm});
            skLineSegment(sketch, "E939", {"start": v(0.56, 0.45) * mm, "end": v(0.56, 0.48) * mm});
            skLineSegment(sketch, "E940", {"start": v(0.56, 0.48) * mm, "end": v(0.56, 0.49) * mm});
            skLineSegment(sketch, "E941", {"start": v(0.56, 0.49) * mm, "end": v(0.57, 0.5) * mm});
            skLineSegment(sketch, "E942", {"start": v(0.57, 0.5) * mm, "end": v(0.57, 0.52) * mm});
            skLineSegment(sketch, "E943", {"start": v(0.57, 0.52) * mm, "end": v(0.58, 0.56) * mm});
            skLineSegment(sketch, "E944", {"start": v(0.58, 0.56) * mm, "end": v(0.58, 0.6) * mm});
            skLineSegment(sketch, "E945", {"start": v(0.58, 0.6) * mm, "end": v(0.58, 0.63) * mm});
            skLineSegment(sketch, "E946", {"start": v(0.58, 0.63) * mm, "end": v(0.59, 0.64) * mm});
            skLineSegment(sketch, "E947", {"start": v(0.59, 0.64) * mm, "end": v(0.59, 0.66) * mm});
            skLineSegment(sketch, "E948", {"start": v(0.59, 0.66) * mm, "end": v(0.6, 0.69) * mm});
            skLineSegment(sketch, "E949", {"start": v(0.6, 0.69) * mm, "end": v(0.6, 0.75) * mm});
            skLineSegment(sketch, "E950", {"start": v(0.6, 0.75) * mm, "end": v(0.62, 0.8) * mm});
            skLineSegment(sketch, "E951", {"start": v(0.62, 0.8) * mm, "end": v(0.64, 0.87) * mm});
            skLineSegment(sketch, "E952", {"start": v(0.64, 0.87) * mm, "end": v(0.66, 0.93) * mm});
            skLineSegment(sketch, "E953", {"start": v(0.66, 0.93) * mm, "end": v(0.68, 0.98) * mm});
            skLineSegment(sketch, "E954", {"start": v(0.68, 0.98) * mm, "end": v(0.7, 1) * mm});
            skLineSegment(sketch, "E955", {"start": v(0.7, 1) * mm, "end": v(0.7, 1.02) * mm});
            skLineSegment(sketch, "E956", {"start": v(0.7, 1.02) * mm, "end": v(0.7, 1.02) * mm});
            skLineSegment(sketch, "E957", {"start": v(0.7, 1.02) * mm, "end": v(0.71, 1.02) * mm});
            skLineSegment(sketch, "E958", {"start": v(0.71, 1.02) * mm, "end": v(0.72, 1) * mm});
            skLineSegment(sketch, "E959", {"start": v(0.72, 1) * mm, "end": v(0.74, 1) * mm});
            skLineSegment(sketch, "E960", {"start": v(0.74, 1) * mm, "end": v(0.75, 0.98) * mm});
            skLineSegment(sketch, "E961", {"start": v(0.75, 0.98) * mm, "end": v(0.75, 0.97) * mm});
            skLineSegment(sketch, "E962", {"start": v(-1.22, 0.95) * mm, "end": v(-1.22, 0.95) * mm});
            skLineSegment(sketch, "E963", {"start": v(-1.22, 0.95) * mm, "end": v(-1.24, 0.94) * mm});
            skLineSegment(sketch, "E964", {"start": v(-1.24, 0.94) * mm, "end": v(-1.26, 0.93) * mm});
            skLineSegment(sketch, "E965", {"start": v(-1.26, 0.93) * mm, "end": v(-1.26, 0.93) * mm});
            skLineSegment(sketch, "E966", {"start": v(-1.26, 0.93) * mm, "end": v(-1.26, 0.94) * mm});
            skLineSegment(sketch, "E967", {"start": v(-1.26, 0.94) * mm, "end": v(-1.26, 0.94) * mm});
            skLineSegment(sketch, "E968", {"start": v(-1.26, 0.94) * mm, "end": v(-1.26, 0.93) * mm});
            skLineSegment(sketch, "E969", {"start": v(-1.26, 0.93) * mm, "end": v(-1.26, 0.9) * mm});
            skLineSegment(sketch, "E970", {"start": v(-1.26, 0.9) * mm, "end": v(-1.28, 0.86) * mm});
            skLineSegment(sketch, "E971", {"start": v(-1.28, 0.86) * mm, "end": v(-1.28, 0.86) * mm});
            skLineSegment(sketch, "E972", {"start": v(-1.28, 0.86) * mm, "end": v(-1.3, 0.82) * mm});
            skLineSegment(sketch, "E973", {"start": v(-1.3, 0.82) * mm, "end": v(-1.33, 0.72) * mm});
            skLineSegment(sketch, "E974", {"start": v(-1.33, 0.72) * mm, "end": v(-1.37, 0.55) * mm});
            skLineSegment(sketch, "E975", {"start": v(-1.37, 0.55) * mm, "end": v(-1.4, 0.34) * mm});
            skLineSegment(sketch, "E976", {"start": v(-1.4, 0.34) * mm, "end": v(-1.4, 0.17) * mm});
            skLineSegment(sketch, "E977", {"start": v(-1.4, 0.17) * mm, "end": v(-1.4, 0.12) * mm});
            skLineSegment(sketch, "E978", {"start": v(-1.4, 0.12) * mm, "end": v(-1.4, 0.1) * mm});
            skLineSegment(sketch, "E979", {"start": v(-1.4, 0.1) * mm, "end": v(-1.4, 0.07) * mm});
            skLineSegment(sketch, "E980", {"start": v(-1.4, 0.07) * mm, "end": v(-1.4, 0.06) * mm});
            skLineSegment(sketch, "E981", {"start": v(-1.4, 0.06) * mm, "end": v(-1.42, 0.09) * mm});
            skLineSegment(sketch, "E982", {"start": v(-1.42, 0.09) * mm, "end": v(-1.45, 0.14) * mm});
            skLineSegment(sketch, "E983", {"start": v(-1.45, 0.14) * mm, "end": v(-1.45, 0.16) * mm});
            skLineSegment(sketch, "E984", {"start": v(-1.45, 0.16) * mm, "end": v(-1.46, 0.2) * mm});
            skLineSegment(sketch, "E985", {"start": v(-1.46, 0.2) * mm, "end": v(-1.5, 0.37) * mm});
            skLineSegment(sketch, "E986", {"start": v(-1.5, 0.37) * mm, "end": v(-1.49, 0.54) * mm});
            skLineSegment(sketch, "E987", {"start": v(-1.49, 0.54) * mm, "end": v(-1.48, 0.57) * mm});
            skLineSegment(sketch, "E988", {"start": v(-1.48, 0.57) * mm, "end": v(-1.48, 0.59) * mm});
            skLineSegment(sketch, "E989", {"start": v(-1.48, 0.59) * mm, "end": v(-1.47, 0.63) * mm});
            skLineSegment(sketch, "E990", {"start": v(-1.47, 0.63) * mm, "end": v(-1.47, 0.66) * mm});
            skLineSegment(sketch, "E991", {"start": v(-1.47, 0.66) * mm, "end": v(-1.47, 0.68) * mm});
            skLineSegment(sketch, "E992", {"start": v(-1.47, 0.68) * mm, "end": v(-1.48, 0.69) * mm});
            skLineSegment(sketch, "E993", {"start": v(-1.48, 0.69) * mm, "end": v(-1.48, 0.7) * mm});
            skLineSegment(sketch, "E994", {"start": v(-1.48, 0.7) * mm, "end": v(-1.48, 0.7) * mm});
            skLineSegment(sketch, "E995", {"start": v(-1.48, 0.7) * mm, "end": v(-1.49, 0.7) * mm});
            skLineSegment(sketch, "E996", {"start": v(-1.49, 0.7) * mm, "end": v(-1.48, 0.7) * mm});
            skLineSegment(sketch, "E997", {"start": v(-1.48, 0.7) * mm, "end": v(-1.47, 0.7) * mm});
            skLineSegment(sketch, "E998", {"start": v(-1.47, 0.7) * mm, "end": v(-1.45, 0.72) * mm});
            skLineSegment(sketch, "E999", {"start": v(-1.45, 0.72) * mm, "end": v(-1.44, 0.74) * mm});
            skLineSegment(sketch, "E1000", {"start": v(-1.44, 0.74) * mm, "end": v(-1.43, 0.75) * mm});
            skLineSegment(sketch, "E1001", {"start": v(-1.43, 0.75) * mm, "end": v(-1.43, 0.76) * mm});
            skLineSegment(sketch, "E1002", {"start": v(-1.43, 0.76) * mm, "end": v(-1.42, 0.78) * mm});
            skLineSegment(sketch, "E1003", {"start": v(-1.42, 0.78) * mm, "end": v(-1.43, 0.79) * mm});
            skLineSegment(sketch, "E1004", {"start": v(-1.43, 0.79) * mm, "end": v(-1.42, 0.8) * mm});
            skLineSegment(sketch, "E1005", {"start": v(-1.42, 0.8) * mm, "end": v(-1.41, 0.8) * mm});
            skLineSegment(sketch, "E1006", {"start": v(-1.41, 0.8) * mm, "end": v(-1.39, 0.83) * mm});
            skLineSegment(sketch, "E1007", {"start": v(-1.39, 0.83) * mm, "end": v(-1.37, 0.86) * mm});
            skLineSegment(sketch, "E1008", {"start": v(-1.37, 0.86) * mm, "end": v(-1.36, 0.87) * mm});
            skLineSegment(sketch, "E1009", {"start": v(-1.36, 0.87) * mm, "end": v(-1.35, 0.87) * mm});
            skLineSegment(sketch, "E1010", {"start": v(-1.35, 0.87) * mm, "end": v(-1.32, 0.9) * mm});
            skLineSegment(sketch, "E1011", {"start": v(-1.32, 0.9) * mm, "end": v(-1.3, 0.93) * mm});
            skLineSegment(sketch, "E1012", {"start": v(-1.3, 0.93) * mm, "end": v(-1.26, 0.95) * mm});
            skLineSegment(sketch, "E1013", {"start": v(-1.26, 0.95) * mm, "end": v(-1.23, 0.97) * mm});
            skLineSegment(sketch, "E1014", {"start": v(-1.23, 0.97) * mm, "end": v(-1.2, 0.98) * mm});
            skLineSegment(sketch, "E1015", {"start": v(-1.2, 0.98) * mm, "end": v(-1.2, 0.98) * mm});
            skLineSegment(sketch, "E1016", {"start": v(-1.2, 0.98) * mm, "end": v(-1.2, 0.97) * mm});
            skLineSegment(sketch, "E1017", {"start": v(-1.2, 0.97) * mm, "end": v(-1.21, 0.96) * mm});
            skLineSegment(sketch, "E1018", {"start": v(-1.21, 0.96) * mm, "end": v(-1.22, 0.95) * mm});
            skLineSegment(sketch, "E1019", {"start": v(0.96, 0.72) * mm, "end": v(0.97, 0.7) * mm});
            skLineSegment(sketch, "E1020", {"start": v(0.97, 0.7) * mm, "end": v(1, 0.64) * mm});
            skLineSegment(sketch, "E1021", {"start": v(1, 0.64) * mm, "end": v(1.03, 0.58) * mm});
            skLineSegment(sketch, "E1022", {"start": v(1.03, 0.58) * mm, "end": v(1.05, 0.53) * mm});
            skLineSegment(sketch, "E1023", {"start": v(1.05, 0.53) * mm, "end": v(1.07, 0.5) * mm});
            skLineSegment(sketch, "E1024", {"start": v(1.07, 0.5) * mm, "end": v(1.09, 0.47) * mm});
            skLineSegment(sketch, "E1025", {"start": v(1.09, 0.47) * mm, "end": v(1.1, 0.44) * mm});
            skLineSegment(sketch, "E1026", {"start": v(1.1, 0.44) * mm, "end": v(1.1, 0.42) * mm});
            skLineSegment(sketch, "E1027", {"start": v(1.1, 0.42) * mm, "end": v(1.1, 0.4) * mm});
            skLineSegment(sketch, "E1028", {"start": v(1.1, 0.4) * mm, "end": v(1.1, 0.4) * mm});
            skLineSegment(sketch, "E1029", {"start": v(1.1, 0.4) * mm, "end": v(1.11, 0.39) * mm});
            skLineSegment(sketch, "E1030", {"start": v(1.11, 0.39) * mm, "end": v(1.12, 0.35) * mm});
            skLineSegment(sketch, "E1031", {"start": v(1.12, 0.35) * mm, "end": v(1.11, 0.34) * mm});
            skLineSegment(sketch, "E1032", {"start": v(1.11, 0.34) * mm, "end": v(1.1, 0.35) * mm});
            skLineSegment(sketch, "E1033", {"start": v(1.1, 0.35) * mm, "end": v(1.06, 0.38) * mm});
            skLineSegment(sketch, "E1034", {"start": v(1.06, 0.38) * mm, "end": v(1.05, 0.39) * mm});
            skLineSegment(sketch, "E1035", {"start": v(1.05, 0.39) * mm, "end": v(1.05, 0.4) * mm});
            skLineSegment(sketch, "E1036", {"start": v(1.05, 0.4) * mm, "end": v(1.03, 0.42) * mm});
            skLineSegment(sketch, "E1037", {"start": v(1.03, 0.42) * mm, "end": v(1, 0.44) * mm});
            skLineSegment(sketch, "E1038", {"start": v(1, 0.44) * mm, "end": v(0.97, 0.46) * mm});
            skLineSegment(sketch, "E1039", {"start": v(0.97, 0.46) * mm, "end": v(0.96, 0.47) * mm});
            skLineSegment(sketch, "E1040", {"start": v(0.96, 0.47) * mm, "end": v(0.95, 0.48) * mm});
            skLineSegment(sketch, "E1041", {"start": v(0.95, 0.48) * mm, "end": v(0.95, 0.48) * mm});
            skLineSegment(sketch, "E1042", {"start": v(0.95, 0.48) * mm, "end": v(0.93, 0.5) * mm});
            skLineSegment(sketch, "E1043", {"start": v(0.93, 0.5) * mm, "end": v(0.92, 0.5) * mm});
            skLineSegment(sketch, "E1044", {"start": v(0.92, 0.5) * mm, "end": v(0.92, 0.52) * mm});
            skLineSegment(sketch, "E1045", {"start": v(0.92, 0.52) * mm, "end": v(0.91, 0.54) * mm});
            skLineSegment(sketch, "E1046", {"start": v(0.91, 0.54) * mm, "end": v(0.91, 0.55) * mm});
            skLineSegment(sketch, "E1047", {"start": v(0.91, 0.55) * mm, "end": v(0.91, 0.58) * mm});
            skLineSegment(sketch, "E1048", {"start": v(0.91, 0.58) * mm, "end": v(0.9, 0.66) * mm});
            skLineSegment(sketch, "E1049", {"start": v(0.9, 0.66) * mm, "end": v(0.87, 0.78) * mm});
            skLineSegment(sketch, "E1050", {"start": v(0.87, 0.78) * mm, "end": v(0.83, 0.89) * mm});
            skLineSegment(sketch, "E1051", {"start": v(0.83, 0.89) * mm, "end": v(0.8, 0.94) * mm});
            skLineSegment(sketch, "E1052", {"start": v(0.8, 0.94) * mm, "end": v(0.79, 0.95) * mm});
            skLineSegment(sketch, "E1053", {"start": v(0.79, 0.95) * mm, "end": v(0.79, 0.95) * mm});
            skLineSegment(sketch, "E1054", {"start": v(0.79, 0.95) * mm, "end": v(0.78, 0.96) * mm});
            skLineSegment(sketch, "E1055", {"start": v(0.78, 0.96) * mm, "end": v(0.78, 0.97) * mm});
            skLineSegment(sketch, "E1056", {"start": v(0.78, 0.97) * mm, "end": v(0.78, 0.97) * mm});
            skLineSegment(sketch, "E1057", {"start": v(0.78, 0.97) * mm, "end": v(0.78, 0.98) * mm});
            skLineSegment(sketch, "E1058", {"start": v(0.78, 0.98) * mm, "end": v(0.8, 0.97) * mm});
            skLineSegment(sketch, "E1059", {"start": v(0.8, 0.97) * mm, "end": v(0.82, 0.94) * mm});
            skLineSegment(sketch, "E1060", {"start": v(0.82, 0.94) * mm, "end": v(0.85, 0.9) * mm});
            skLineSegment(sketch, "E1061", {"start": v(0.85, 0.9) * mm, "end": v(0.88, 0.87) * mm});
            skLineSegment(sketch, "E1062", {"start": v(0.88, 0.87) * mm, "end": v(0.9, 0.82) * mm});
            skLineSegment(sketch, "E1063", {"start": v(0.9, 0.82) * mm, "end": v(0.94, 0.77) * mm});
            skLineSegment(sketch, "E1064", {"start": v(0.94, 0.77) * mm, "end": v(0.96, 0.73) * mm});
            skLineSegment(sketch, "E1065", {"start": v(0.96, 0.73) * mm, "end": v(0.96, 0.72) * mm});
            skLineSegment(sketch, "E1066", {"start": v(-0.4, 0.96) * mm, "end": v(-0.39, 0.95) * mm});
            skLineSegment(sketch, "E1067", {"start": v(-0.39, 0.95) * mm, "end": v(-0.37, 0.93) * mm});
            skLineSegment(sketch, "E1068", {"start": v(-0.37, 0.93) * mm, "end": v(-0.36, 0.88) * mm});
            skLineSegment(sketch, "E1069", {"start": v(-0.36, 0.88) * mm, "end": v(-0.34, 0.8) * mm});
            skLineSegment(sketch, "E1070", {"start": v(-0.34, 0.8) * mm, "end": v(-0.33, 0.7) * mm});
            skLineSegment(sketch, "E1071", {"start": v(-0.33, 0.7) * mm, "end": v(-0.33, 0.67) * mm});
            skLineSegment(sketch, "E1072", {"start": v(-0.33, 0.67) * mm, "end": v(-0.33, 0.66) * mm});
            skLineSegment(sketch, "E1073", {"start": v(-0.33, 0.66) * mm, "end": v(-0.32, 0.62) * mm});
            skLineSegment(sketch, "E1074", {"start": v(-0.32, 0.62) * mm, "end": v(-0.32, 0.58) * mm});
            skLineSegment(sketch, "E1075", {"start": v(-0.32, 0.58) * mm, "end": v(-0.31, 0.56) * mm});
            skLineSegment(sketch, "E1076", {"start": v(-0.31, 0.56) * mm, "end": v(-0.3, 0.54) * mm});
            skLineSegment(sketch, "E1077", {"start": v(-0.3, 0.54) * mm, "end": v(-0.3, 0.54) * mm});
            skLineSegment(sketch, "E1078", {"start": v(-0.3, 0.54) * mm, "end": v(-0.31, 0.52) * mm});
            skLineSegment(sketch, "E1079", {"start": v(-0.31, 0.52) * mm, "end": v(-0.34, 0.49) * mm});
            skLineSegment(sketch, "E1080", {"start": v(-0.34, 0.49) * mm, "end": v(-0.34, 0.48) * mm});
            skLineSegment(sketch, "E1081", {"start": v(-0.34, 0.48) * mm, "end": v(-0.35, 0.47) * mm});
            skLineSegment(sketch, "E1082", {"start": v(-0.35, 0.47) * mm, "end": v(-0.37, 0.45) * mm});
            skLineSegment(sketch, "E1083", {"start": v(-0.37, 0.45) * mm, "end": v(-0.4, 0.42) * mm});
            skLineSegment(sketch, "E1084", {"start": v(-0.4, 0.42) * mm, "end": v(-0.43, 0.38) * mm});
            skLineSegment(sketch, "E1085", {"start": v(-0.43, 0.38) * mm, "end": v(-0.45, 0.35) * mm});
            skLineSegment(sketch, "E1086", {"start": v(-0.45, 0.35) * mm, "end": v(-0.45, 0.34) * mm});
            skLineSegment(sketch, "E1087", {"start": v(-0.45, 0.34) * mm, "end": v(-0.46, 0.33) * mm});
            skLineSegment(sketch, "E1088", {"start": v(-0.46, 0.33) * mm, "end": v(-0.48, 0.3) * mm});
            skLineSegment(sketch, "E1089", {"start": v(-0.48, 0.3) * mm, "end": v(-0.5, 0.26) * mm});
            skLineSegment(sketch, "E1090", {"start": v(-0.5, 0.26) * mm, "end": v(-0.53, 0.25) * mm});
            skLineSegment(sketch, "E1091", {"start": v(-0.53, 0.25) * mm, "end": v(-0.54, 0.24) * mm});
            skLineSegment(sketch, "E1092", {"start": v(-0.54, 0.24) * mm, "end": v(-0.55, 0.25) * mm});
            skLineSegment(sketch, "E1093", {"start": v(-0.55, 0.25) * mm, "end": v(-0.55, 0.27) * mm});
            skLineSegment(sketch, "E1094", {"start": v(-0.55, 0.27) * mm, "end": v(-0.54, 0.3) * mm});
            skLineSegment(sketch, "E1095", {"start": v(-0.54, 0.3) * mm, "end": v(-0.53, 0.33) * mm});
            skLineSegment(sketch, "E1096", {"start": v(-0.53, 0.33) * mm, "end": v(-0.53, 0.34) * mm});
            skLineSegment(sketch, "E1097", {"start": v(-0.53, 0.34) * mm, "end": v(-0.52, 0.36) * mm});
            skLineSegment(sketch, "E1098", {"start": v(-0.52, 0.36) * mm, "end": v(-0.52, 0.43) * mm});
            skLineSegment(sketch, "E1099", {"start": v(-0.52, 0.43) * mm, "end": v(-0.51, 0.56) * mm});
            skLineSegment(sketch, "E1100", {"start": v(-0.51, 0.56) * mm, "end": v(-0.52, 0.69) * mm});
            skLineSegment(sketch, "E1101", {"start": v(-0.52, 0.69) * mm, "end": v(-0.52, 0.76) * mm});
            skLineSegment(sketch, "E1102", {"start": v(-0.52, 0.76) * mm, "end": v(-0.53, 0.79) * mm});
            skLineSegment(sketch, "E1103", {"start": v(-0.53, 0.79) * mm, "end": v(-0.55, 0.88) * mm});
            skLineSegment(sketch, "E1104", {"start": v(-0.55, 0.88) * mm, "end": v(-0.5, 0.92) * mm});
            skLineSegment(sketch, "E1105", {"start": v(-0.5, 0.92) * mm, "end": v(-0.5, 0.93) * mm});
            skLineSegment(sketch, "E1106", {"start": v(-0.5, 0.93) * mm, "end": v(-0.47, 0.95) * mm});
            skLineSegment(sketch, "E1107", {"start": v(-0.47, 0.95) * mm, "end": v(-0.44, 0.96) * mm});
            skLineSegment(sketch, "E1108", {"start": v(-0.44, 0.96) * mm, "end": v(-0.42, 0.96) * mm});
            skLineSegment(sketch, "E1109", {"start": v(-0.42, 0.96) * mm, "end": v(-0.4, 0.96) * mm});
            skLineSegment(sketch, "E1110", {"start": v(-0.4, 0.96) * mm, "end": v(-0.4, 0.96) * mm});
            skLineSegment(sketch, "E1111", {"start": v(0.46, 0.94) * mm, "end": v(0.47, 0.94) * mm});
            skLineSegment(sketch, "E1112", {"start": v(0.47, 0.94) * mm, "end": v(0.48, 0.93) * mm});
            skLineSegment(sketch, "E1113", {"start": v(0.48, 0.93) * mm, "end": v(0.48, 0.93) * mm});
            skLineSegment(sketch, "E1114", {"start": v(0.48, 0.93) * mm, "end": v(0.48, 0.94) * mm});
            skLineSegment(sketch, "E1115", {"start": v(0.48, 0.94) * mm, "end": v(0.48, 0.94) * mm});
            skLineSegment(sketch, "E1116", {"start": v(0.48, 0.94) * mm, "end": v(0.49, 0.95) * mm});
            skLineSegment(sketch, "E1117", {"start": v(0.49, 0.95) * mm, "end": v(0.5, 0.95) * mm});
            skLineSegment(sketch, "E1118", {"start": v(0.5, 0.95) * mm, "end": v(0.52, 0.95) * mm});
            skLineSegment(sketch, "E1119", {"start": v(0.52, 0.95) * mm, "end": v(0.52, 0.94) * mm});
            skLineSegment(sketch, "E1120", {"start": v(0.52, 0.94) * mm, "end": v(0.52, 0.94) * mm});
            skLineSegment(sketch, "E1121", {"start": v(0.52, 0.94) * mm, "end": v(0.52, 0.93) * mm});
            skLineSegment(sketch, "E1122", {"start": v(0.52, 0.93) * mm, "end": v(0.51, 0.92) * mm});
            skLineSegment(sketch, "E1123", {"start": v(0.51, 0.92) * mm, "end": v(0.51, 0.92) * mm});
            skLineSegment(sketch, "E1124", {"start": v(0.51, 0.92) * mm, "end": v(0.5, 0.92) * mm});
            skLineSegment(sketch, "E1125", {"start": v(0.5, 0.92) * mm, "end": v(0.5, 0.92) * mm});
            skLineSegment(sketch, "E1126", {"start": v(0.5, 0.92) * mm, "end": v(0.5, 0.9) * mm});
            skLineSegment(sketch, "E1127", {"start": v(0.5, 0.9) * mm, "end": v(0.5, 0.9) * mm});
            skLineSegment(sketch, "E1128", {"start": v(0.5, 0.9) * mm, "end": v(0.5, 0.89) * mm});
            skLineSegment(sketch, "E1129", {"start": v(0.5, 0.89) * mm, "end": v(0.5, 0.88) * mm});
            skLineSegment(sketch, "E1130", {"start": v(0.5, 0.88) * mm, "end": v(0.5, 0.88) * mm});
            skLineSegment(sketch, "E1131", {"start": v(0.5, 0.88) * mm, "end": v(0.49, 0.88) * mm});
            skLineSegment(sketch, "E1132", {"start": v(0.49, 0.88) * mm, "end": v(0.48, 0.87) * mm});
            skLineSegment(sketch, "E1133", {"start": v(0.48, 0.87) * mm, "end": v(0.48, 0.87) * mm});
            skLineSegment(sketch, "E1134", {"start": v(0.48, 0.87) * mm, "end": v(0.49, 0.86) * mm});
            skLineSegment(sketch, "E1135", {"start": v(0.49, 0.86) * mm, "end": v(0.5, 0.86) * mm});
            skLineSegment(sketch, "E1136", {"start": v(0.5, 0.86) * mm, "end": v(0.5, 0.86) * mm});
            skLineSegment(sketch, "E1137", {"start": v(0.5, 0.86) * mm, "end": v(0.5, 0.85) * mm});
            skLineSegment(sketch, "E1138", {"start": v(0.5, 0.85) * mm, "end": v(0.5, 0.85) * mm});
            skLineSegment(sketch, "E1139", {"start": v(0.5, 0.85) * mm, "end": v(0.5, 0.83) * mm});
            skLineSegment(sketch, "E1140", {"start": v(0.5, 0.83) * mm, "end": v(0.48, 0.84) * mm});
            skLineSegment(sketch, "E1141", {"start": v(0.48, 0.84) * mm, "end": v(0.47, 0.84) * mm});
            skLineSegment(sketch, "E1142", {"start": v(0.47, 0.84) * mm, "end": v(0.47, 0.85) * mm});
            skLineSegment(sketch, "E1143", {"start": v(0.47, 0.85) * mm, "end": v(0.46, 0.86) * mm});
            skLineSegment(sketch, "E1144", {"start": v(0.46, 0.86) * mm, "end": v(0.46, 0.87) * mm});
            skLineSegment(sketch, "E1145", {"start": v(0.46, 0.87) * mm, "end": v(0.46, 0.87) * mm});
            skLineSegment(sketch, "E1146", {"start": v(0.46, 0.87) * mm, "end": v(0.47, 0.88) * mm});
            skLineSegment(sketch, "E1147", {"start": v(0.47, 0.88) * mm, "end": v(0.46, 0.88) * mm});
            skLineSegment(sketch, "E1148", {"start": v(0.46, 0.88) * mm, "end": v(0.45, 0.88) * mm});
            skLineSegment(sketch, "E1149", {"start": v(0.45, 0.88) * mm, "end": v(0.44, 0.87) * mm});
            skLineSegment(sketch, "E1150", {"start": v(0.44, 0.87) * mm, "end": v(0.43, 0.87) * mm});
            skLineSegment(sketch, "E1151", {"start": v(0.43, 0.87) * mm, "end": v(0.43, 0.87) * mm});
            skLineSegment(sketch, "E1152", {"start": v(0.43, 0.87) * mm, "end": v(0.42, 0.86) * mm});
            skLineSegment(sketch, "E1153", {"start": v(0.42, 0.86) * mm, "end": v(0.41, 0.88) * mm});
            skLineSegment(sketch, "E1154", {"start": v(0.41, 0.88) * mm, "end": v(0.4, 0.88) * mm});
            skLineSegment(sketch, "E1155", {"start": v(0.4, 0.88) * mm, "end": v(0.4, 0.89) * mm});
            skLineSegment(sketch, "E1156", {"start": v(0.4, 0.89) * mm, "end": v(0.4, 0.9) * mm});
            skLineSegment(sketch, "E1157", {"start": v(0.4, 0.9) * mm, "end": v(0.4, 0.9) * mm});
            skLineSegment(sketch, "E1158", {"start": v(0.4, 0.9) * mm, "end": v(0.42, 0.9) * mm});
            skLineSegment(sketch, "E1159", {"start": v(0.42, 0.9) * mm, "end": v(0.43, 0.9) * mm});
            skLineSegment(sketch, "E1160", {"start": v(0.43, 0.9) * mm, "end": v(0.43, 0.9) * mm});
            skLineSegment(sketch, "E1161", {"start": v(0.43, 0.9) * mm, "end": v(0.45, 0.9) * mm});
            skLineSegment(sketch, "E1162", {"start": v(0.45, 0.9) * mm, "end": v(0.45, 0.91) * mm});
            skLineSegment(sketch, "E1163", {"start": v(0.45, 0.91) * mm, "end": v(0.45, 0.92) * mm});
            skLineSegment(sketch, "E1164", {"start": v(0.45, 0.92) * mm, "end": v(0.44, 0.92) * mm});
            skLineSegment(sketch, "E1165", {"start": v(0.44, 0.92) * mm, "end": v(0.43, 0.94) * mm});
            skLineSegment(sketch, "E1166", {"start": v(0.43, 0.94) * mm, "end": v(0.43, 0.96) * mm});
            skLineSegment(sketch, "E1167", {"start": v(0.43, 0.96) * mm, "end": v(0.44, 0.96) * mm});
            skLineSegment(sketch, "E1168", {"start": v(0.44, 0.96) * mm, "end": v(0.46, 0.95) * mm});
            skLineSegment(sketch, "E1169", {"start": v(0.46, 0.95) * mm, "end": v(0.46, 0.94) * mm});
            skLineSegment(sketch, "E1170", {"start": v(0.3, 0.86) * mm, "end": v(0.3, 0.86) * mm});
            skLineSegment(sketch, "E1171", {"start": v(0.3, 0.86) * mm, "end": v(0.31, 0.83) * mm});
            skLineSegment(sketch, "E1172", {"start": v(0.31, 0.83) * mm, "end": v(0.33, 0.81) * mm});
            skLineSegment(sketch, "E1173", {"start": v(0.33, 0.81) * mm, "end": v(0.35, 0.8) * mm});
            skLineSegment(sketch, "E1174", {"start": v(0.35, 0.8) * mm, "end": v(0.36, 0.8) * mm});
            skLineSegment(sketch, "E1175", {"start": v(0.36, 0.8) * mm, "end": v(0.36, 0.8) * mm});
            skLineSegment(sketch, "E1176", {"start": v(0.36, 0.8) * mm, "end": v(0.37, 0.8) * mm});
            skLineSegment(sketch, "E1177", {"start": v(0.37, 0.8) * mm, "end": v(0.37, 0.78) * mm});
            skLineSegment(sketch, "E1178", {"start": v(0.37, 0.78) * mm, "end": v(0.36, 0.78) * mm});
            skLineSegment(sketch, "E1179", {"start": v(0.36, 0.78) * mm, "end": v(0.36, 0.78) * mm});
            skLineSegment(sketch, "E1180", {"start": v(0.36, 0.78) * mm, "end": v(0.36, 0.76) * mm});
            skLineSegment(sketch, "E1181", {"start": v(0.36, 0.76) * mm, "end": v(0.37, 0.75) * mm});
            skLineSegment(sketch, "E1182", {"start": v(0.37, 0.75) * mm, "end": v(0.37, 0.74) * mm});
            skLineSegment(sketch, "E1183", {"start": v(0.37, 0.74) * mm, "end": v(0.38, 0.74) * mm});
            skLineSegment(sketch, "E1184", {"start": v(0.38, 0.74) * mm, "end": v(0.4, 0.72) * mm});
            skLineSegment(sketch, "E1185", {"start": v(0.4, 0.72) * mm, "end": v(0.42, 0.68) * mm});
            skLineSegment(sketch, "E1186", {"start": v(0.42, 0.68) * mm, "end": v(0.44, 0.65) * mm});
            skLineSegment(sketch, "E1187", {"start": v(0.44, 0.65) * mm, "end": v(0.44, 0.64) * mm});
            skLineSegment(sketch, "E1188", {"start": v(0.44, 0.64) * mm, "end": v(0.44, 0.63) * mm});
            skLineSegment(sketch, "E1189", {"start": v(0.44, 0.63) * mm, "end": v(0.44, 0.63) * mm});
            skLineSegment(sketch, "E1190", {"start": v(0.44, 0.63) * mm, "end": v(0.45, 0.6) * mm});
            skLineSegment(sketch, "E1191", {"start": v(0.45, 0.6) * mm, "end": v(0.47, 0.59) * mm});
            skLineSegment(sketch, "E1192", {"start": v(0.47, 0.59) * mm, "end": v(0.47, 0.58) * mm});
            skLineSegment(sketch, "E1193", {"start": v(0.47, 0.58) * mm, "end": v(0.48, 0.58) * mm});
            skLineSegment(sketch, "E1194", {"start": v(0.48, 0.58) * mm, "end": v(0.5, 0.56) * mm});
            skLineSegment(sketch, "E1195", {"start": v(0.5, 0.56) * mm, "end": v(0.48, 0.55) * mm});
            skLineSegment(sketch, "E1196", {"start": v(0.48, 0.55) * mm, "end": v(0.48, 0.55) * mm});
            skLineSegment(sketch, "E1197", {"start": v(0.48, 0.55) * mm, "end": v(0.47, 0.55) * mm});
            skLineSegment(sketch, "E1198", {"start": v(0.47, 0.55) * mm, "end": v(0.48, 0.54) * mm});
            skLineSegment(sketch, "E1199", {"start": v(0.48, 0.54) * mm, "end": v(0.48, 0.54) * mm});
            skLineSegment(sketch, "E1200", {"start": v(0.48, 0.54) * mm, "end": v(0.48, 0.53) * mm});
            skLineSegment(sketch, "E1201", {"start": v(0.48, 0.53) * mm, "end": v(0.5, 0.51) * mm});
            skLineSegment(sketch, "E1202", {"start": v(0.5, 0.51) * mm, "end": v(0.52, 0.48) * mm});
            skLineSegment(sketch, "E1203", {"start": v(0.52, 0.48) * mm, "end": v(0.52, 0.44) * mm});
            skLineSegment(sketch, "E1204", {"start": v(0.52, 0.44) * mm, "end": v(0.5, 0.4) * mm});
            skLineSegment(sketch, "E1205", {"start": v(0.5, 0.4) * mm, "end": v(0.48, 0.36) * mm});
            skLineSegment(sketch, "E1206", {"start": v(0.48, 0.36) * mm, "end": v(0.45, 0.33) * mm});
            skLineSegment(sketch, "E1207", {"start": v(0.45, 0.33) * mm, "end": v(0.42, 0.3) * mm});
            skLineSegment(sketch, "E1208", {"start": v(0.42, 0.3) * mm, "end": v(0.38, 0.3) * mm});
            skLineSegment(sketch, "E1209", {"start": v(0.38, 0.3) * mm, "end": v(0.37, 0.3) * mm});
            skLineSegment(sketch, "E1210", {"start": v(0.37, 0.3) * mm, "end": v(0.36, 0.3) * mm});
            skLineSegment(sketch, "E1211", {"start": v(0.36, 0.3) * mm, "end": v(0.3, 0.31) * mm});
            skLineSegment(sketch, "E1212", {"start": v(0.3, 0.31) * mm, "end": v(0.25, 0.35) * mm});
            skLineSegment(sketch, "E1213", {"start": v(0.25, 0.35) * mm, "end": v(0.2, 0.4) * mm});
            skLineSegment(sketch, "E1214", {"start": v(0.2, 0.4) * mm, "end": v(0.17, 0.49) * mm});
            skLineSegment(sketch, "E1215", {"start": v(0.17, 0.49) * mm, "end": v(0.16, 0.58) * mm});
            skLineSegment(sketch, "E1216", {"start": v(0.16, 0.58) * mm, "end": v(0.16, 0.68) * mm});
            skLineSegment(sketch, "E1217", {"start": v(0.16, 0.68) * mm, "end": v(0.18, 0.8) * mm});
            skLineSegment(sketch, "E1218", {"start": v(0.18, 0.8) * mm, "end": v(0.2, 0.9) * mm});
            skLineSegment(sketch, "E1219", {"start": v(0.2, 0.9) * mm, "end": v(0.21, 0.92) * mm});
            skLineSegment(sketch, "E1220", {"start": v(0.21, 0.92) * mm, "end": v(0.21, 0.93) * mm});
            skLineSegment(sketch, "E1221", {"start": v(0.21, 0.93) * mm, "end": v(0.22, 0.94) * mm});
            skLineSegment(sketch, "E1222", {"start": v(0.22, 0.94) * mm, "end": v(0.23, 0.93) * mm});
            skLineSegment(sketch, "E1223", {"start": v(0.23, 0.93) * mm, "end": v(0.25, 0.9) * mm});
            skLineSegment(sketch, "E1224", {"start": v(0.25, 0.9) * mm, "end": v(0.28, 0.87) * mm});
            skLineSegment(sketch, "E1225", {"start": v(0.28, 0.87) * mm, "end": v(0.3, 0.86) * mm});
            skLineSegment(sketch, "E1226", {"start": v(1.3, 0.9) * mm, "end": v(1.3, 0.9) * mm});
            skLineSegment(sketch, "E1227", {"start": v(1.3, 0.9) * mm, "end": v(1.3, 0.89) * mm});
            skLineSegment(sketch, "E1228", {"start": v(1.3, 0.89) * mm, "end": v(1.3, 0.88) * mm});
            skLineSegment(sketch, "E1229", {"start": v(1.3, 0.88) * mm, "end": v(1.3, 0.88) * mm});
            skLineSegment(sketch, "E1230", {"start": v(1.3, 0.88) * mm, "end": v(1.31, 0.88) * mm});
            skLineSegment(sketch, "E1231", {"start": v(1.31, 0.88) * mm, "end": v(1.3, 0.86) * mm});
            skLineSegment(sketch, "E1232", {"start": v(1.3, 0.86) * mm, "end": v(1.3, 0.86) * mm});
            skLineSegment(sketch, "E1233", {"start": v(1.3, 0.86) * mm, "end": v(1.3, 0.85) * mm});
            skLineSegment(sketch, "E1234", {"start": v(1.3, 0.85) * mm, "end": v(1.3, 0.83) * mm});
            skLineSegment(sketch, "E1235", {"start": v(1.3, 0.83) * mm, "end": v(1.3, 0.8) * mm});
            skLineSegment(sketch, "E1236", {"start": v(1.3, 0.8) * mm, "end": v(1.3, 0.8) * mm});
            skLineSegment(sketch, "E1237", {"start": v(1.3, 0.8) * mm, "end": v(1.31, 0.8) * mm});
            skLineSegment(sketch, "E1238", {"start": v(1.31, 0.8) * mm, "end": v(1.32, 0.79) * mm});
            skLineSegment(sketch, "E1239", {"start": v(1.32, 0.79) * mm, "end": v(1.31, 0.8) * mm});
            skLineSegment(sketch, "E1240", {"start": v(1.31, 0.8) * mm, "end": v(1.31, 0.8) * mm});
            skLineSegment(sketch, "E1241", {"start": v(1.31, 0.8) * mm, "end": v(1.3, 0.8) * mm});
            skLineSegment(sketch, "E1242", {"start": v(1.3, 0.8) * mm, "end": v(1.31, 0.83) * mm});
            skLineSegment(sketch, "E1243", {"start": v(1.31, 0.83) * mm, "end": v(1.33, 0.84) * mm});
            skLineSegment(sketch, "E1244", {"start": v(1.33, 0.84) * mm, "end": v(1.36, 0.85) * mm});
            skLineSegment(sketch, "E1245", {"start": v(1.36, 0.85) * mm, "end": v(1.38, 0.84) * mm});
            skLineSegment(sketch, "E1246", {"start": v(1.38, 0.84) * mm, "end": v(1.38, 0.84) * mm});
            skLineSegment(sketch, "E1247", {"start": v(1.38, 0.84) * mm, "end": v(1.4, 0.82) * mm});
            skLineSegment(sketch, "E1248", {"start": v(1.4, 0.82) * mm, "end": v(1.4, 0.8) * mm});
            skLineSegment(sketch, "E1249", {"start": v(1.4, 0.8) * mm, "end": v(1.39, 0.78) * mm});
            skLineSegment(sketch, "E1250", {"start": v(1.39, 0.78) * mm, "end": v(1.38, 0.77) * mm});
            skLineSegment(sketch, "E1251", {"start": v(1.38, 0.77) * mm, "end": v(1.37, 0.77) * mm});
            skLineSegment(sketch, "E1252", {"start": v(1.37, 0.77) * mm, "end": v(1.37, 0.77) * mm});
            skLineSegment(sketch, "E1253", {"start": v(1.37, 0.77) * mm, "end": v(1.37, 0.76) * mm});
            skLineSegment(sketch, "E1254", {"start": v(1.37, 0.76) * mm, "end": v(1.37, 0.74) * mm});
            skLineSegment(sketch, "E1255", {"start": v(1.37, 0.74) * mm, "end": v(1.37, 0.73) * mm});
            skLineSegment(sketch, "E1256", {"start": v(1.37, 0.73) * mm, "end": v(1.37, 0.72) * mm});
            skLineSegment(sketch, "E1257", {"start": v(1.37, 0.72) * mm, "end": v(1.37, 0.7) * mm});
            skLineSegment(sketch, "E1258", {"start": v(1.37, 0.7) * mm, "end": v(1.36, 0.69) * mm});
            skLineSegment(sketch, "E1259", {"start": v(1.36, 0.69) * mm, "end": v(1.36, 0.69) * mm});
            skLineSegment(sketch, "E1260", {"start": v(1.36, 0.69) * mm, "end": v(1.35, 0.7) * mm});
            skLineSegment(sketch, "E1261", {"start": v(1.35, 0.7) * mm, "end": v(1.35, 0.7) * mm});
            skLineSegment(sketch, "E1262", {"start": v(1.35, 0.7) * mm, "end": v(1.36, 0.71) * mm});
            skLineSegment(sketch, "E1263", {"start": v(1.36, 0.71) * mm, "end": v(1.35, 0.71) * mm});
            skLineSegment(sketch, "E1264", {"start": v(1.35, 0.71) * mm, "end": v(1.35, 0.71) * mm});
            skLineSegment(sketch, "E1265", {"start": v(1.35, 0.71) * mm, "end": v(1.34, 0.7) * mm});
            skLineSegment(sketch, "E1266", {"start": v(1.34, 0.7) * mm, "end": v(1.34, 0.7) * mm});
            skLineSegment(sketch, "E1267", {"start": v(1.34, 0.7) * mm, "end": v(1.34, 0.68) * mm});
            skLineSegment(sketch, "E1268", {"start": v(1.34, 0.68) * mm, "end": v(1.34, 0.68) * mm});
            skLineSegment(sketch, "E1269", {"start": v(1.34, 0.68) * mm, "end": v(1.34, 0.67) * mm});
            skLineSegment(sketch, "E1270", {"start": v(1.34, 0.67) * mm, "end": v(1.34, 0.64) * mm});
            skLineSegment(sketch, "E1271", {"start": v(1.34, 0.64) * mm, "end": v(1.33, 0.62) * mm});
            skLineSegment(sketch, "E1272", {"start": v(1.33, 0.62) * mm, "end": v(1.32, 0.6) * mm});
            skLineSegment(sketch, "E1273", {"start": v(1.32, 0.6) * mm, "end": v(1.3, 0.56) * mm});
            skLineSegment(sketch, "E1274", {"start": v(1.3, 0.56) * mm, "end": v(1.3, 0.54) * mm});
            skLineSegment(sketch, "E1275", {"start": v(1.3, 0.54) * mm, "end": v(1.29, 0.53) * mm});
            skLineSegment(sketch, "E1276", {"start": v(1.29, 0.53) * mm, "end": v(1.28, 0.52) * mm});
            skLineSegment(sketch, "E1277", {"start": v(1.28, 0.52) * mm, "end": v(1.28, 0.52) * mm});
            skLineSegment(sketch, "E1278", {"start": v(1.28, 0.52) * mm, "end": v(1.27, 0.52) * mm});
            skLineSegment(sketch, "E1279", {"start": v(1.27, 0.52) * mm, "end": v(1.26, 0.52) * mm});
            skLineSegment(sketch, "E1280", {"start": v(1.26, 0.52) * mm, "end": v(1.27, 0.51) * mm});
            skLineSegment(sketch, "E1281", {"start": v(1.27, 0.51) * mm, "end": v(1.27, 0.51) * mm});
            skLineSegment(sketch, "E1282", {"start": v(1.27, 0.51) * mm, "end": v(1.27, 0.5) * mm});
            skLineSegment(sketch, "E1283", {"start": v(1.27, 0.5) * mm, "end": v(1.28, 0.5) * mm});
            skLineSegment(sketch, "E1284", {"start": v(1.28, 0.5) * mm, "end": v(1.28, 0.47) * mm});
            skLineSegment(sketch, "E1285", {"start": v(1.28, 0.47) * mm, "end": v(1.27, 0.44) * mm});
            skLineSegment(sketch, "E1286", {"start": v(1.27, 0.44) * mm, "end": v(1.25, 0.43) * mm});
            skLineSegment(sketch, "E1287", {"start": v(1.25, 0.43) * mm, "end": v(1.25, 0.43) * mm});
            skLineSegment(sketch, "E1288", {"start": v(1.25, 0.43) * mm, "end": v(1.24, 0.43) * mm});
            skLineSegment(sketch, "E1289", {"start": v(1.24, 0.43) * mm, "end": v(1.23, 0.44) * mm});
            skLineSegment(sketch, "E1290", {"start": v(1.23, 0.44) * mm, "end": v(1.22, 0.46) * mm});
            skLineSegment(sketch, "E1291", {"start": v(1.22, 0.46) * mm, "end": v(1.22, 0.47) * mm});
            skLineSegment(sketch, "E1292", {"start": v(1.22, 0.47) * mm, "end": v(1.22, 0.47) * mm});
            skLineSegment(sketch, "E1293", {"start": v(1.22, 0.47) * mm, "end": v(1.22, 0.5) * mm});
            skLineSegment(sketch, "E1294", {"start": v(1.22, 0.5) * mm, "end": v(1.23, 0.5) * mm});
            skLineSegment(sketch, "E1295", {"start": v(1.23, 0.5) * mm, "end": v(1.23, 0.5) * mm});
            skLineSegment(sketch, "E1296", {"start": v(1.23, 0.5) * mm, "end": v(1.24, 0.5) * mm});
            skLineSegment(sketch, "E1297", {"start": v(1.24, 0.5) * mm, "end": v(1.24, 0.52) * mm});
            skLineSegment(sketch, "E1298", {"start": v(1.24, 0.52) * mm, "end": v(1.25, 0.56) * mm});
            skLineSegment(sketch, "E1299", {"start": v(1.25, 0.56) * mm, "end": v(1.24, 0.6) * mm});
            skLineSegment(sketch, "E1300", {"start": v(1.24, 0.6) * mm, "end": v(1.24, 0.62) * mm});
            skLineSegment(sketch, "E1301", {"start": v(1.24, 0.62) * mm, "end": v(1.23, 0.63) * mm});
            skLineSegment(sketch, "E1302", {"start": v(1.23, 0.63) * mm, "end": v(1.23, 0.64) * mm});
            skLineSegment(sketch, "E1303", {"start": v(1.23, 0.64) * mm, "end": v(1.23, 0.65) * mm});
            skLineSegment(sketch, "E1304", {"start": v(1.23, 0.65) * mm, "end": v(1.23, 0.68) * mm});
            skLineSegment(sketch, "E1305", {"start": v(1.23, 0.68) * mm, "end": v(1.24, 0.7) * mm});
            skLineSegment(sketch, "E1306", {"start": v(1.24, 0.7) * mm, "end": v(1.25, 0.7) * mm});
            skLineSegment(sketch, "E1307", {"start": v(1.25, 0.7) * mm, "end": v(1.25, 0.7) * mm});
            skLineSegment(sketch, "E1308", {"start": v(1.25, 0.7) * mm, "end": v(1.26, 0.7) * mm});
            skLineSegment(sketch, "E1309", {"start": v(1.26, 0.7) * mm, "end": v(1.26, 0.7) * mm});
            skLineSegment(sketch, "E1310", {"start": v(1.26, 0.7) * mm, "end": v(1.26, 0.71) * mm});
            skLineSegment(sketch, "E1311", {"start": v(1.26, 0.71) * mm, "end": v(1.26, 0.72) * mm});
            skLineSegment(sketch, "E1312", {"start": v(1.26, 0.72) * mm, "end": v(1.24, 0.72) * mm});
            skLineSegment(sketch, "E1313", {"start": v(1.24, 0.72) * mm, "end": v(1.24, 0.72) * mm});
            skLineSegment(sketch, "E1314", {"start": v(1.24, 0.72) * mm, "end": v(1.23, 0.73) * mm});
            skLineSegment(sketch, "E1315", {"start": v(1.23, 0.73) * mm, "end": v(1.22, 0.76) * mm});
            skLineSegment(sketch, "E1316", {"start": v(1.22, 0.76) * mm, "end": v(1.22, 0.79) * mm});
            skLineSegment(sketch, "E1317", {"start": v(1.22, 0.79) * mm, "end": v(1.23, 0.8) * mm});
            skLineSegment(sketch, "E1318", {"start": v(1.23, 0.8) * mm, "end": v(1.23, 0.8) * mm});
            skLineSegment(sketch, "E1319", {"start": v(1.23, 0.8) * mm, "end": v(1.24, 0.8) * mm});
            skLineSegment(sketch, "E1320", {"start": v(1.24, 0.8) * mm, "end": v(1.24, 0.8) * mm});
            skLineSegment(sketch, "E1321", {"start": v(1.24, 0.8) * mm, "end": v(1.24, 0.79) * mm});
            skLineSegment(sketch, "E1322", {"start": v(1.24, 0.79) * mm, "end": v(1.24, 0.78) * mm});
            skLineSegment(sketch, "E1323", {"start": v(1.24, 0.78) * mm, "end": v(1.24, 0.76) * mm});
            skLineSegment(sketch, "E1324", {"start": v(1.24, 0.76) * mm, "end": v(1.25, 0.76) * mm});
            skLineSegment(sketch, "E1325", {"start": v(1.25, 0.76) * mm, "end": v(1.25, 0.76) * mm});
            skLineSegment(sketch, "E1326", {"start": v(1.25, 0.76) * mm, "end": v(1.26, 0.78) * mm});
            skLineSegment(sketch, "E1327", {"start": v(1.26, 0.78) * mm, "end": v(1.27, 0.81) * mm});
            skLineSegment(sketch, "E1328", {"start": v(1.27, 0.81) * mm, "end": v(1.26, 0.85) * mm});
            skLineSegment(sketch, "E1329", {"start": v(1.26, 0.85) * mm, "end": v(1.25, 0.86) * mm});
            skLineSegment(sketch, "E1330", {"start": v(1.25, 0.86) * mm, "end": v(1.25, 0.87) * mm});
            skLineSegment(sketch, "E1331", {"start": v(1.25, 0.87) * mm, "end": v(1.25, 0.87) * mm});
            skLineSegment(sketch, "E1332", {"start": v(1.25, 0.87) * mm, "end": v(1.24, 0.87) * mm});
            skLineSegment(sketch, "E1333", {"start": v(1.24, 0.87) * mm, "end": v(1.23, 0.86) * mm});
            skLineSegment(sketch, "E1334", {"start": v(1.23, 0.86) * mm, "end": v(1.23, 0.86) * mm});
            skLineSegment(sketch, "E1335", {"start": v(1.23, 0.86) * mm, "end": v(1.23, 0.85) * mm});
            skLineSegment(sketch, "E1336", {"start": v(1.23, 0.85) * mm, "end": v(1.23, 0.85) * mm});
            skLineSegment(sketch, "E1337", {"start": v(1.23, 0.85) * mm, "end": v(1.22, 0.84) * mm});
            skLineSegment(sketch, "E1338", {"start": v(1.22, 0.84) * mm, "end": v(1.22, 0.84) * mm});
            skLineSegment(sketch, "E1339", {"start": v(1.22, 0.84) * mm, "end": v(1.2, 0.85) * mm});
            skLineSegment(sketch, "E1340", {"start": v(1.2, 0.85) * mm, "end": v(1.2, 0.86) * mm});
            skLineSegment(sketch, "E1341", {"start": v(1.2, 0.86) * mm, "end": v(1.2, 0.86) * mm});
            skLineSegment(sketch, "E1342", {"start": v(1.2, 0.86) * mm, "end": v(1.2, 0.87) * mm});
            skLineSegment(sketch, "E1343", {"start": v(1.2, 0.87) * mm, "end": v(1.21, 0.88) * mm});
            skLineSegment(sketch, "E1344", {"start": v(1.21, 0.88) * mm, "end": v(1.23, 0.88) * mm});
            skLineSegment(sketch, "E1345", {"start": v(1.23, 0.88) * mm, "end": v(1.23, 0.88) * mm});
            skLineSegment(sketch, "E1346", {"start": v(1.23, 0.88) * mm, "end": v(1.24, 0.88) * mm});
            skLineSegment(sketch, "E1347", {"start": v(1.24, 0.88) * mm, "end": v(1.25, 0.9) * mm});
            skLineSegment(sketch, "E1348", {"start": v(1.25, 0.9) * mm, "end": v(1.27, 0.9) * mm});
            skLineSegment(sketch, "E1349", {"start": v(1.27, 0.9) * mm, "end": v(1.27, 0.91) * mm});
            skLineSegment(sketch, "E1350", {"start": v(1.27, 0.91) * mm, "end": v(1.27, 0.92) * mm});
            skLineSegment(sketch, "E1351", {"start": v(1.27, 0.92) * mm, "end": v(1.28, 0.93) * mm});
            skLineSegment(sketch, "E1352", {"start": v(1.28, 0.93) * mm, "end": v(1.29, 0.93) * mm});
            skLineSegment(sketch, "E1353", {"start": v(1.29, 0.93) * mm, "end": v(1.29, 0.92) * mm});
            skLineSegment(sketch, "E1354", {"start": v(1.29, 0.92) * mm, "end": v(1.3, 0.92) * mm});
            skLineSegment(sketch, "E1355", {"start": v(1.3, 0.92) * mm, "end": v(1.3, 0.9) * mm});
            skLineSegment(sketch, "E1356", {"start": v(-0.56, 0.76) * mm, "end": v(-0.56, 0.74) * mm});
            skLineSegment(sketch, "E1357", {"start": v(-0.56, 0.74) * mm, "end": v(-0.55, 0.63) * mm});
            skLineSegment(sketch, "E1358", {"start": v(-0.55, 0.63) * mm, "end": v(-0.55, 0.49) * mm});
            skLineSegment(sketch, "E1359", {"start": v(-0.55, 0.49) * mm, "end": v(-0.55, 0.45) * mm});
            skLineSegment(sketch, "E1360", {"start": v(-0.55, 0.45) * mm, "end": v(-0.55, 0.43) * mm});
            skLineSegment(sketch, "E1361", {"start": v(-0.55, 0.43) * mm, "end": v(-0.56, 0.37) * mm});
            skLineSegment(sketch, "E1362", {"start": v(-0.56, 0.37) * mm, "end": v(-0.56, 0.3) * mm});
            skLineSegment(sketch, "E1363", {"start": v(-0.56, 0.3) * mm, "end": v(-0.56, 0.25) * mm});
            skLineSegment(sketch, "E1364", {"start": v(-0.56, 0.25) * mm, "end": v(-0.56, 0.23) * mm});
            skLineSegment(sketch, "E1365", {"start": v(-0.56, 0.23) * mm, "end": v(-0.56, 0.23) * mm});
            skLineSegment(sketch, "E1366", {"start": v(-0.56, 0.23) * mm, "end": v(-0.56, 0.22) * mm});
            skLineSegment(sketch, "E1367", {"start": v(-0.56, 0.22) * mm, "end": v(-0.56, 0.2) * mm});
            skLineSegment(sketch, "E1368", {"start": v(-0.56, 0.2) * mm, "end": v(-0.57, 0.2) * mm});
            skLineSegment(sketch, "E1369", {"start": v(-0.57, 0.2) * mm, "end": v(-0.57, 0.2) * mm});
            skLineSegment(sketch, "E1370", {"start": v(-0.57, 0.2) * mm, "end": v(-0.58, 0.2) * mm});
            skLineSegment(sketch, "E1371", {"start": v(-0.58, 0.2) * mm, "end": v(-0.59, 0.2) * mm});
            skLineSegment(sketch, "E1372", {"start": v(-0.59, 0.2) * mm, "end": v(-0.59, 0.2) * mm});
            skLineSegment(sketch, "E1373", {"start": v(-0.59, 0.2) * mm, "end": v(-0.59, 0.22) * mm});
            skLineSegment(sketch, "E1374", {"start": v(-0.59, 0.22) * mm, "end": v(-0.6, 0.25) * mm});
            skLineSegment(sketch, "E1375", {"start": v(-0.6, 0.25) * mm, "end": v(-0.6, 0.31) * mm});
            skLineSegment(sketch, "E1376", {"start": v(-0.6, 0.31) * mm, "end": v(-0.63, 0.39) * mm});
            skLineSegment(sketch, "E1377", {"start": v(-0.63, 0.39) * mm, "end": v(-0.66, 0.46) * mm});
            skLineSegment(sketch, "E1378", {"start": v(-0.66, 0.46) * mm, "end": v(-0.7, 0.54) * mm});
            skLineSegment(sketch, "E1379", {"start": v(-0.7, 0.54) * mm, "end": v(-0.73, 0.61) * mm});
            skLineSegment(sketch, "E1380", {"start": v(-0.73, 0.61) * mm, "end": v(-0.76, 0.66) * mm});
            skLineSegment(sketch, "E1381", {"start": v(-0.76, 0.66) * mm, "end": v(-0.77, 0.69) * mm});
            skLineSegment(sketch, "E1382", {"start": v(-0.77, 0.69) * mm, "end": v(-0.78, 0.7) * mm});
            skLineSegment(sketch, "E1383", {"start": v(-0.78, 0.7) * mm, "end": v(-0.79, 0.7) * mm});
            skLineSegment(sketch, "E1384", {"start": v(-0.79, 0.7) * mm, "end": v(-0.8, 0.72) * mm});
            skLineSegment(sketch, "E1385", {"start": v(-0.8, 0.72) * mm, "end": v(-0.8, 0.74) * mm});
            skLineSegment(sketch, "E1386", {"start": v(-0.8, 0.74) * mm, "end": v(-0.79, 0.76) * mm});
            skLineSegment(sketch, "E1387", {"start": v(-0.79, 0.76) * mm, "end": v(-0.76, 0.79) * mm});
            skLineSegment(sketch, "E1388", {"start": v(-0.76, 0.79) * mm, "end": v(-0.75, 0.8) * mm});
            skLineSegment(sketch, "E1389", {"start": v(-0.75, 0.8) * mm, "end": v(-0.74, 0.8) * mm});
            skLineSegment(sketch, "E1390", {"start": v(-0.74, 0.8) * mm, "end": v(-0.7, 0.83) * mm});
            skLineSegment(sketch, "E1391", {"start": v(-0.7, 0.83) * mm, "end": v(-0.65, 0.86) * mm});
            skLineSegment(sketch, "E1392", {"start": v(-0.65, 0.86) * mm, "end": v(-0.62, 0.88) * mm});
            skLineSegment(sketch, "E1393", {"start": v(-0.62, 0.88) * mm, "end": v(-0.6, 0.88) * mm});
            skLineSegment(sketch, "E1394", {"start": v(-0.6, 0.88) * mm, "end": v(-0.59, 0.87) * mm});
            skLineSegment(sketch, "E1395", {"start": v(-0.59, 0.87) * mm, "end": v(-0.58, 0.85) * mm});
            skLineSegment(sketch, "E1396", {"start": v(-0.58, 0.85) * mm, "end": v(-0.57, 0.81) * mm});
            skLineSegment(sketch, "E1397", {"start": v(-0.57, 0.81) * mm, "end": v(-0.56, 0.77) * mm});
            skLineSegment(sketch, "E1398", {"start": v(-0.56, 0.77) * mm, "end": v(-0.56, 0.76) * mm});
            skLineSegment(sketch, "E1399", {"start": v(0.57, 0.87) * mm, "end": v(0.56, 0.87) * mm});
            skLineSegment(sketch, "E1400", {"start": v(0.56, 0.87) * mm, "end": v(0.56, 0.85) * mm});
            skLineSegment(sketch, "E1401", {"start": v(0.56, 0.85) * mm, "end": v(0.56, 0.82) * mm});
            skLineSegment(sketch, "E1402", {"start": v(0.56, 0.82) * mm, "end": v(0.55, 0.81) * mm});
            skLineSegment(sketch, "E1403", {"start": v(0.55, 0.81) * mm, "end": v(0.55, 0.8) * mm});
            skLineSegment(sketch, "E1404", {"start": v(0.55, 0.8) * mm, "end": v(0.54, 0.8) * mm});
            skLineSegment(sketch, "E1405", {"start": v(0.54, 0.8) * mm, "end": v(0.54, 0.8) * mm});
            skLineSegment(sketch, "E1406", {"start": v(0.54, 0.8) * mm, "end": v(0.53, 0.83) * mm});
            skLineSegment(sketch, "E1407", {"start": v(0.53, 0.83) * mm, "end": v(0.53, 0.86) * mm});
            skLineSegment(sketch, "E1408", {"start": v(0.53, 0.86) * mm, "end": v(0.53, 0.87) * mm});
            skLineSegment(sketch, "E1409", {"start": v(0.53, 0.87) * mm, "end": v(0.54, 0.87) * mm});
            skLineSegment(sketch, "E1410", {"start": v(0.54, 0.87) * mm, "end": v(0.54, 0.89) * mm});
            skLineSegment(sketch, "E1411", {"start": v(0.54, 0.89) * mm, "end": v(0.55, 0.9) * mm});
            skLineSegment(sketch, "E1412", {"start": v(0.55, 0.9) * mm, "end": v(0.56, 0.9) * mm});
            skLineSegment(sketch, "E1413", {"start": v(0.56, 0.9) * mm, "end": v(0.57, 0.88) * mm});
            skLineSegment(sketch, "E1414", {"start": v(0.57, 0.88) * mm, "end": v(0.57, 0.87) * mm});
            skLineSegment(sketch, "E1415", {"start": v(-1.47, 0.8) * mm, "end": v(-1.47, 0.8) * mm});
            skLineSegment(sketch, "E1416", {"start": v(-1.47, 0.8) * mm, "end": v(-1.48, 0.79) * mm});
            skLineSegment(sketch, "E1417", {"start": v(-1.48, 0.79) * mm, "end": v(-1.49, 0.79) * mm});
            skLineSegment(sketch, "E1418", {"start": v(-1.49, 0.79) * mm, "end": v(-1.49, 0.79) * mm});
            skLineSegment(sketch, "E1419", {"start": v(-1.49, 0.79) * mm, "end": v(-1.5, 0.8) * mm});
            skLineSegment(sketch, "E1420", {"start": v(-1.5, 0.8) * mm, "end": v(-1.5, 0.8) * mm});
            skLineSegment(sketch, "E1421", {"start": v(-1.5, 0.8) * mm, "end": v(-1.5, 0.81) * mm});
            skLineSegment(sketch, "E1422", {"start": v(-1.5, 0.81) * mm, "end": v(-1.5, 0.81) * mm});
            skLineSegment(sketch, "E1423", {"start": v(-1.5, 0.81) * mm, "end": v(-1.52, 0.8) * mm});
            skLineSegment(sketch, "E1424", {"start": v(-1.52, 0.8) * mm, "end": v(-1.52, 0.8) * mm});
            skLineSegment(sketch, "E1425", {"start": v(-1.52, 0.8) * mm, "end": v(-1.53, 0.8) * mm});
            skLineSegment(sketch, "E1426", {"start": v(-1.53, 0.8) * mm, "end": v(-1.54, 0.8) * mm});
            skLineSegment(sketch, "E1427", {"start": v(-1.54, 0.8) * mm, "end": v(-1.53, 0.79) * mm});
            skLineSegment(sketch, "E1428", {"start": v(-1.53, 0.79) * mm, "end": v(-1.53, 0.79) * mm});
            skLineSegment(sketch, "E1429", {"start": v(-1.53, 0.79) * mm, "end": v(-1.53, 0.77) * mm});
            skLineSegment(sketch, "E1430", {"start": v(-1.53, 0.77) * mm, "end": v(-1.53, 0.73) * mm});
            skLineSegment(sketch, "E1431", {"start": v(-1.53, 0.73) * mm, "end": v(-1.55, 0.7) * mm});
            skLineSegment(sketch, "E1432", {"start": v(-1.55, 0.7) * mm, "end": v(-1.56, 0.67) * mm});
            skLineSegment(sketch, "E1433", {"start": v(-1.56, 0.67) * mm, "end": v(-1.56, 0.67) * mm});
            skLineSegment(sketch, "E1434", {"start": v(-1.56, 0.67) * mm, "end": v(-1.57, 0.67) * mm});
            skLineSegment(sketch, "E1435", {"start": v(-1.57, 0.67) * mm, "end": v(-1.57, 0.65) * mm});
            skLineSegment(sketch, "E1436", {"start": v(-1.57, 0.65) * mm, "end": v(-1.56, 0.64) * mm});
            skLineSegment(sketch, "E1437", {"start": v(-1.56, 0.64) * mm, "end": v(-1.56, 0.64) * mm});
            skLineSegment(sketch, "E1438", {"start": v(-1.56, 0.64) * mm, "end": v(-1.57, 0.62) * mm});
            skLineSegment(sketch, "E1439", {"start": v(-1.57, 0.62) * mm, "end": v(-1.57, 0.6) * mm});
            skLineSegment(sketch, "E1440", {"start": v(-1.57, 0.6) * mm, "end": v(-1.57, 0.6) * mm});
            skLineSegment(sketch, "E1441", {"start": v(-1.57, 0.6) * mm, "end": v(-1.58, 0.6) * mm});
            skLineSegment(sketch, "E1442", {"start": v(-1.58, 0.6) * mm, "end": v(-1.58, 0.58) * mm});
            skLineSegment(sketch, "E1443", {"start": v(-1.58, 0.58) * mm, "end": v(-1.58, 0.58) * mm});
            skLineSegment(sketch, "E1444", {"start": v(-1.58, 0.58) * mm, "end": v(-1.57, 0.58) * mm});
            skLineSegment(sketch, "E1445", {"start": v(-1.57, 0.58) * mm, "end": v(-1.57, 0.58) * mm});
            skLineSegment(sketch, "E1446", {"start": v(-1.57, 0.58) * mm, "end": v(-1.57, 0.57) * mm});
            skLineSegment(sketch, "E1447", {"start": v(-1.57, 0.57) * mm, "end": v(-1.56, 0.55) * mm});
            skLineSegment(sketch, "E1448", {"start": v(-1.56, 0.55) * mm, "end": v(-1.56, 0.51) * mm});
            skLineSegment(sketch, "E1449", {"start": v(-1.56, 0.51) * mm, "end": v(-1.56, 0.47) * mm});
            skLineSegment(sketch, "E1450", {"start": v(-1.56, 0.47) * mm, "end": v(-1.56, 0.46) * mm});
            skLineSegment(sketch, "E1451", {"start": v(-1.56, 0.46) * mm, "end": v(-1.56, 0.44) * mm});
            skLineSegment(sketch, "E1452", {"start": v(-1.56, 0.44) * mm, "end": v(-1.57, 0.4) * mm});
            skLineSegment(sketch, "E1453", {"start": v(-1.57, 0.4) * mm, "end": v(-1.56, 0.36) * mm});
            skLineSegment(sketch, "E1454", {"start": v(-1.56, 0.36) * mm, "end": v(-1.56, 0.33) * mm});
            skLineSegment(sketch, "E1455", {"start": v(-1.56, 0.33) * mm, "end": v(-1.55, 0.32) * mm});
            skLineSegment(sketch, "E1456", {"start": v(-1.55, 0.32) * mm, "end": v(-1.54, 0.31) * mm});
            skLineSegment(sketch, "E1457", {"start": v(-1.54, 0.31) * mm, "end": v(-1.54, 0.3) * mm});
            skLineSegment(sketch, "E1458", {"start": v(-1.54, 0.3) * mm, "end": v(-1.53, 0.29) * mm});
            skLineSegment(sketch, "E1459", {"start": v(-1.53, 0.29) * mm, "end": v(-1.52, 0.28) * mm});
            skLineSegment(sketch, "E1460", {"start": v(-1.52, 0.28) * mm, "end": v(-1.52, 0.27) * mm});
            skLineSegment(sketch, "E1461", {"start": v(-1.52, 0.27) * mm, "end": v(-1.53, 0.28) * mm});
            skLineSegment(sketch, "E1462", {"start": v(-1.53, 0.28) * mm, "end": v(-1.54, 0.28) * mm});
            skLineSegment(sketch, "E1463", {"start": v(-1.54, 0.28) * mm, "end": v(-1.54, 0.28) * mm});
            skLineSegment(sketch, "E1464", {"start": v(-1.54, 0.28) * mm, "end": v(-1.55, 0.28) * mm});
            skLineSegment(sketch, "E1465", {"start": v(-1.55, 0.28) * mm, "end": v(-1.55, 0.26) * mm});
            skLineSegment(sketch, "E1466", {"start": v(-1.55, 0.26) * mm, "end": v(-1.55, 0.25) * mm});
            skLineSegment(sketch, "E1467", {"start": v(-1.55, 0.25) * mm, "end": v(-1.55, 0.25) * mm});
            skLineSegment(sketch, "E1468", {"start": v(-1.55, 0.25) * mm, "end": v(-1.55, 0.24) * mm});
            skLineSegment(sketch, "E1469", {"start": v(-1.55, 0.24) * mm, "end": v(-1.55, 0.24) * mm});
            skLineSegment(sketch, "E1470", {"start": v(-1.55, 0.24) * mm, "end": v(-1.56, 0.25) * mm});
            skLineSegment(sketch, "E1471", {"start": v(-1.56, 0.25) * mm, "end": v(-1.58, 0.26) * mm});
            skLineSegment(sketch, "E1472", {"start": v(-1.58, 0.26) * mm, "end": v(-1.58, 0.26) * mm});
            skLineSegment(sketch, "E1473", {"start": v(-1.58, 0.26) * mm, "end": v(-1.59, 0.26) * mm});
            skLineSegment(sketch, "E1474", {"start": v(-1.59, 0.26) * mm, "end": v(-1.6, 0.27) * mm});
            skLineSegment(sketch, "E1475", {"start": v(-1.6, 0.27) * mm, "end": v(-1.6, 0.3) * mm});
            skLineSegment(sketch, "E1476", {"start": v(-1.6, 0.3) * mm, "end": v(-1.6, 0.32) * mm});
            skLineSegment(sketch, "E1477", {"start": v(-1.6, 0.32) * mm, "end": v(-1.6, 0.33) * mm});
            skLineSegment(sketch, "E1478", {"start": v(-1.6, 0.33) * mm, "end": v(-1.6, 0.35) * mm});
            skLineSegment(sketch, "E1479", {"start": v(-1.6, 0.35) * mm, "end": v(-1.6, 0.38) * mm});
            skLineSegment(sketch, "E1480", {"start": v(-1.6, 0.38) * mm, "end": v(-1.6, 0.41) * mm});
            skLineSegment(sketch, "E1481", {"start": v(-1.6, 0.41) * mm, "end": v(-1.62, 0.42) * mm});
            skLineSegment(sketch, "E1482", {"start": v(-1.62, 0.42) * mm, "end": v(-1.63, 0.4) * mm});
            skLineSegment(sketch, "E1483", {"start": v(-1.63, 0.4) * mm, "end": v(-1.64, 0.4) * mm});
            skLineSegment(sketch, "E1484", {"start": v(-1.64, 0.4) * mm, "end": v(-1.64, 0.4) * mm});
            skLineSegment(sketch, "E1485", {"start": v(-1.64, 0.4) * mm, "end": v(-1.65, 0.39) * mm});
            skLineSegment(sketch, "E1486", {"start": v(-1.65, 0.39) * mm, "end": v(-1.66, 0.39) * mm});
            skLineSegment(sketch, "E1487", {"start": v(-1.66, 0.39) * mm, "end": v(-1.66, 0.39) * mm});
            skLineSegment(sketch, "E1488", {"start": v(-1.66, 0.39) * mm, "end": v(-1.67, 0.4) * mm});
            skLineSegment(sketch, "E1489", {"start": v(-1.67, 0.4) * mm, "end": v(-1.67, 0.4) * mm});
            skLineSegment(sketch, "E1490", {"start": v(-1.67, 0.4) * mm, "end": v(-1.66, 0.4) * mm});
            skLineSegment(sketch, "E1491", {"start": v(-1.66, 0.4) * mm, "end": v(-1.66, 0.4) * mm});
            skLineSegment(sketch, "E1492", {"start": v(-1.66, 0.4) * mm, "end": v(-1.65, 0.42) * mm});
            skLineSegment(sketch, "E1493", {"start": v(-1.65, 0.42) * mm, "end": v(-1.65, 0.45) * mm});
            skLineSegment(sketch, "E1494", {"start": v(-1.65, 0.45) * mm, "end": v(-1.66, 0.48) * mm});
            skLineSegment(sketch, "E1495", {"start": v(-1.66, 0.48) * mm, "end": v(-1.67, 0.5) * mm});
            skLineSegment(sketch, "E1496", {"start": v(-1.67, 0.5) * mm, "end": v(-1.67, 0.5) * mm});
            skLineSegment(sketch, "E1497", {"start": v(-1.67, 0.5) * mm, "end": v(-1.68, 0.5) * mm});
            skLineSegment(sketch, "E1498", {"start": v(-1.68, 0.5) * mm, "end": v(-1.68, 0.5) * mm});
            skLineSegment(sketch, "E1499", {"start": v(-1.68, 0.5) * mm, "end": v(-1.67, 0.5) * mm});
            skLineSegment(sketch, "E1500", {"start": v(-1.67, 0.5) * mm, "end": v(-1.66, 0.51) * mm});
            skLineSegment(sketch, "E1501", {"start": v(-1.66, 0.51) * mm, "end": v(-1.65, 0.52) * mm});
            skLineSegment(sketch, "E1502", {"start": v(-1.65, 0.52) * mm, "end": v(-1.64, 0.53) * mm});
            skLineSegment(sketch, "E1503", {"start": v(-1.64, 0.53) * mm, "end": v(-1.64, 0.54) * mm});
            skLineSegment(sketch, "E1504", {"start": v(-1.64, 0.54) * mm, "end": v(-1.64, 0.54) * mm});
            skLineSegment(sketch, "E1505", {"start": v(-1.64, 0.54) * mm, "end": v(-1.65, 0.54) * mm});
            skLineSegment(sketch, "E1506", {"start": v(-1.65, 0.54) * mm, "end": v(-1.66, 0.54) * mm});
            skLineSegment(sketch, "E1507", {"start": v(-1.66, 0.54) * mm, "end": v(-1.66, 0.54) * mm});
            skLineSegment(sketch, "E1508", {"start": v(-1.66, 0.54) * mm, "end": v(-1.67, 0.53) * mm});
            skLineSegment(sketch, "E1509", {"start": v(-1.67, 0.53) * mm, "end": v(-1.68, 0.53) * mm});
            skLineSegment(sketch, "E1510", {"start": v(-1.68, 0.53) * mm, "end": v(-1.69, 0.54) * mm});
            skLineSegment(sketch, "E1511", {"start": v(-1.69, 0.54) * mm, "end": v(-1.7, 0.54) * mm});
            skLineSegment(sketch, "E1512", {"start": v(-1.7, 0.54) * mm, "end": v(-1.7, 0.55) * mm});
            skLineSegment(sketch, "E1513", {"start": v(-1.7, 0.55) * mm, "end": v(-1.7, 0.58) * mm});
            skLineSegment(sketch, "E1514", {"start": v(-1.7, 0.58) * mm, "end": v(-1.7, 0.6) * mm});
            skLineSegment(sketch, "E1515", {"start": v(-1.7, 0.6) * mm, "end": v(-1.7, 0.6) * mm});
            skLineSegment(sketch, "E1516", {"start": v(-1.7, 0.6) * mm, "end": v(-1.68, 0.59) * mm});
            skLineSegment(sketch, "E1517", {"start": v(-1.68, 0.59) * mm, "end": v(-1.67, 0.58) * mm});
            skLineSegment(sketch, "E1518", {"start": v(-1.67, 0.58) * mm, "end": v(-1.66, 0.58) * mm});
            skLineSegment(sketch, "E1519", {"start": v(-1.66, 0.58) * mm, "end": v(-1.64, 0.56) * mm});
            skLineSegment(sketch, "E1520", {"start": v(-1.64, 0.56) * mm, "end": v(-1.63, 0.54) * mm});
            skLineSegment(sketch, "E1521", {"start": v(-1.63, 0.54) * mm, "end": v(-1.63, 0.54) * mm});
            skLineSegment(sketch, "E1522", {"start": v(-1.63, 0.54) * mm, "end": v(-1.62, 0.53) * mm});
            skLineSegment(sketch, "E1523", {"start": v(-1.62, 0.53) * mm, "end": v(-1.61, 0.53) * mm});
            skLineSegment(sketch, "E1524", {"start": v(-1.61, 0.53) * mm, "end": v(-1.61, 0.53) * mm});
            skLineSegment(sketch, "E1525", {"start": v(-1.61, 0.53) * mm, "end": v(-1.6, 0.53) * mm});
            skLineSegment(sketch, "E1526", {"start": v(-1.6, 0.53) * mm, "end": v(-1.6, 0.53) * mm});
            skLineSegment(sketch, "E1527", {"start": v(-1.6, 0.53) * mm, "end": v(-1.62, 0.52) * mm});
            skLineSegment(sketch, "E1528", {"start": v(-1.62, 0.52) * mm, "end": v(-1.62, 0.52) * mm});
            skLineSegment(sketch, "E1529", {"start": v(-1.62, 0.52) * mm, "end": v(-1.62, 0.51) * mm});
            skLineSegment(sketch, "E1530", {"start": v(-1.62, 0.51) * mm, "end": v(-1.63, 0.5) * mm});
            skLineSegment(sketch, "E1531", {"start": v(-1.63, 0.5) * mm, "end": v(-1.63, 0.5) * mm});
            skLineSegment(sketch, "E1532", {"start": v(-1.63, 0.5) * mm, "end": v(-1.62, 0.49) * mm});
            skLineSegment(sketch, "E1533", {"start": v(-1.62, 0.49) * mm, "end": v(-1.6, 0.47) * mm});
            skLineSegment(sketch, "E1534", {"start": v(-1.6, 0.47) * mm, "end": v(-1.6, 0.46) * mm});
            skLineSegment(sketch, "E1535", {"start": v(-1.6, 0.46) * mm, "end": v(-1.6, 0.46) * mm});
            skLineSegment(sketch, "E1536", {"start": v(-1.6, 0.46) * mm, "end": v(-1.6, 0.45) * mm});
            skLineSegment(sketch, "E1537", {"start": v(-1.6, 0.45) * mm, "end": v(-1.6, 0.45) * mm});
            skLineSegment(sketch, "E1538", {"start": v(-1.6, 0.45) * mm, "end": v(-1.59, 0.46) * mm});
            skLineSegment(sketch, "E1539", {"start": v(-1.59, 0.46) * mm, "end": v(-1.6, 0.48) * mm});
            skLineSegment(sketch, "E1540", {"start": v(-1.6, 0.48) * mm, "end": v(-1.6, 0.49) * mm});
            skLineSegment(sketch, "E1541", {"start": v(-1.6, 0.49) * mm, "end": v(-1.6, 0.5) * mm});
            skLineSegment(sketch, "E1542", {"start": v(-1.6, 0.5) * mm, "end": v(-1.6, 0.53) * mm});
            skLineSegment(sketch, "E1543", {"start": v(-1.6, 0.53) * mm, "end": v(-1.6, 0.56) * mm});
            skLineSegment(sketch, "E1544", {"start": v(-1.6, 0.56) * mm, "end": v(-1.6, 0.56) * mm});
            skLineSegment(sketch, "E1545", {"start": v(-1.6, 0.56) * mm, "end": v(-1.6, 0.57) * mm});
            skLineSegment(sketch, "E1546", {"start": v(-1.6, 0.57) * mm, "end": v(-1.61, 0.57) * mm});
            skLineSegment(sketch, "E1547", {"start": v(-1.61, 0.57) * mm, "end": v(-1.6, 0.57) * mm});
            skLineSegment(sketch, "E1548", {"start": v(-1.6, 0.57) * mm, "end": v(-1.6, 0.57) * mm});
            skLineSegment(sketch, "E1549", {"start": v(-1.6, 0.57) * mm, "end": v(-1.6, 0.58) * mm});
            skLineSegment(sketch, "E1550", {"start": v(-1.6, 0.58) * mm, "end": v(-1.6, 0.58) * mm});
            skLineSegment(sketch, "E1551", {"start": v(-1.6, 0.58) * mm, "end": v(-1.6, 0.59) * mm});
            skLineSegment(sketch, "E1552", {"start": v(-1.6, 0.59) * mm, "end": v(-1.6, 0.6) * mm});
            skLineSegment(sketch, "E1553", {"start": v(-1.6, 0.6) * mm, "end": v(-1.62, 0.6) * mm});
            skLineSegment(sketch, "E1554", {"start": v(-1.62, 0.6) * mm, "end": v(-1.62, 0.6) * mm});
            skLineSegment(sketch, "E1555", {"start": v(-1.62, 0.6) * mm, "end": v(-1.63, 0.6) * mm});
            skLineSegment(sketch, "E1556", {"start": v(-1.63, 0.6) * mm, "end": v(-1.64, 0.6) * mm});
            skLineSegment(sketch, "E1557", {"start": v(-1.64, 0.6) * mm, "end": v(-1.64, 0.6) * mm});
            skLineSegment(sketch, "E1558", {"start": v(-1.64, 0.6) * mm, "end": v(-1.63, 0.61) * mm});
            skLineSegment(sketch, "E1559", {"start": v(-1.63, 0.61) * mm, "end": v(-1.65, 0.61) * mm});
            skLineSegment(sketch, "E1560", {"start": v(-1.65, 0.61) * mm, "end": v(-1.65, 0.61) * mm});
            skLineSegment(sketch, "E1561", {"start": v(-1.65, 0.61) * mm, "end": v(-1.65, 0.6) * mm});
            skLineSegment(sketch, "E1562", {"start": v(-1.65, 0.6) * mm, "end": v(-1.66, 0.6) * mm});
            skLineSegment(sketch, "E1563", {"start": v(-1.66, 0.6) * mm, "end": v(-1.67, 0.62) * mm});
            skLineSegment(sketch, "E1564", {"start": v(-1.67, 0.62) * mm, "end": v(-1.67, 0.62) * mm});
            skLineSegment(sketch, "E1565", {"start": v(-1.67, 0.62) * mm, "end": v(-1.67, 0.63) * mm});
            skLineSegment(sketch, "E1566", {"start": v(-1.67, 0.63) * mm, "end": v(-1.66, 0.63) * mm});
            skLineSegment(sketch, "E1567", {"start": v(-1.66, 0.63) * mm, "end": v(-1.66, 0.63) * mm});
            skLineSegment(sketch, "E1568", {"start": v(-1.66, 0.63) * mm, "end": v(-1.65, 0.63) * mm});
            skLineSegment(sketch, "E1569", {"start": v(-1.65, 0.63) * mm, "end": v(-1.64, 0.65) * mm});
            skLineSegment(sketch, "E1570", {"start": v(-1.64, 0.65) * mm, "end": v(-1.64, 0.67) * mm});
            skLineSegment(sketch, "E1571", {"start": v(-1.64, 0.67) * mm, "end": v(-1.63, 0.7) * mm});
            skLineSegment(sketch, "E1572", {"start": v(-1.63, 0.7) * mm, "end": v(-1.64, 0.71) * mm});
            skLineSegment(sketch, "E1573", {"start": v(-1.64, 0.71) * mm, "end": v(-1.64, 0.71) * mm});
            skLineSegment(sketch, "E1574", {"start": v(-1.64, 0.71) * mm, "end": v(-1.65, 0.72) * mm});
            skLineSegment(sketch, "E1575", {"start": v(-1.65, 0.72) * mm, "end": v(-1.64, 0.74) * mm});
            skLineSegment(sketch, "E1576", {"start": v(-1.64, 0.74) * mm, "end": v(-1.64, 0.75) * mm});
            skLineSegment(sketch, "E1577", {"start": v(-1.64, 0.75) * mm, "end": v(-1.64, 0.75) * mm});
            skLineSegment(sketch, "E1578", {"start": v(-1.64, 0.75) * mm, "end": v(-1.63, 0.77) * mm});
            skLineSegment(sketch, "E1579", {"start": v(-1.63, 0.77) * mm, "end": v(-1.62, 0.77) * mm});
            skLineSegment(sketch, "E1580", {"start": v(-1.62, 0.77) * mm, "end": v(-1.6, 0.76) * mm});
            skLineSegment(sketch, "E1581", {"start": v(-1.6, 0.76) * mm, "end": v(-1.6, 0.75) * mm});
            skLineSegment(sketch, "E1582", {"start": v(-1.6, 0.75) * mm, "end": v(-1.61, 0.74) * mm});
            skLineSegment(sketch, "E1583", {"start": v(-1.61, 0.74) * mm, "end": v(-1.61, 0.74) * mm});
            skLineSegment(sketch, "E1584", {"start": v(-1.61, 0.74) * mm, "end": v(-1.61, 0.73) * mm});
            skLineSegment(sketch, "E1585", {"start": v(-1.61, 0.73) * mm, "end": v(-1.61, 0.72) * mm});
            skLineSegment(sketch, "E1586", {"start": v(-1.61, 0.72) * mm, "end": v(-1.6, 0.73) * mm});
            skLineSegment(sketch, "E1587", {"start": v(-1.6, 0.73) * mm, "end": v(-1.59, 0.74) * mm});
            skLineSegment(sketch, "E1588", {"start": v(-1.59, 0.74) * mm, "end": v(-1.58, 0.75) * mm});
            skLineSegment(sketch, "E1589", {"start": v(-1.58, 0.75) * mm, "end": v(-1.58, 0.75) * mm});
            skLineSegment(sketch, "E1590", {"start": v(-1.58, 0.75) * mm, "end": v(-1.56, 0.77) * mm});
            skLineSegment(sketch, "E1591", {"start": v(-1.56, 0.77) * mm, "end": v(-1.55, 0.79) * mm});
            skLineSegment(sketch, "E1592", {"start": v(-1.55, 0.79) * mm, "end": v(-1.55, 0.79) * mm});
            skLineSegment(sketch, "E1593", {"start": v(-1.55, 0.79) * mm, "end": v(-1.55, 0.8) * mm});
            skLineSegment(sketch, "E1594", {"start": v(-1.55, 0.8) * mm, "end": v(-1.55, 0.81) * mm});
            skLineSegment(sketch, "E1595", {"start": v(-1.55, 0.81) * mm, "end": v(-1.55, 0.81) * mm});
            skLineSegment(sketch, "E1596", {"start": v(-1.55, 0.81) * mm, "end": v(-1.55, 0.82) * mm});
            skLineSegment(sketch, "E1597", {"start": v(-1.55, 0.82) * mm, "end": v(-1.53, 0.83) * mm});
            skLineSegment(sketch, "E1598", {"start": v(-1.53, 0.83) * mm, "end": v(-1.5, 0.83) * mm});
            skLineSegment(sketch, "E1599", {"start": v(-1.5, 0.83) * mm, "end": v(-1.48, 0.82) * mm});
            skLineSegment(sketch, "E1600", {"start": v(-1.48, 0.82) * mm, "end": v(-1.47, 0.81) * mm});
            skLineSegment(sketch, "E1601", {"start": v(-1.47, 0.81) * mm, "end": v(-1.47, 0.8) * mm});
            skLineSegment(sketch, "E1602", {"start": v(1.56, 0.75) * mm, "end": v(1.57, 0.74) * mm});
            skLineSegment(sketch, "E1603", {"start": v(1.57, 0.74) * mm, "end": v(1.6, 0.71) * mm});
            skLineSegment(sketch, "E1604", {"start": v(1.6, 0.71) * mm, "end": v(1.63, 0.68) * mm});
            skLineSegment(sketch, "E1605", {"start": v(1.63, 0.68) * mm, "end": v(1.65, 0.65) * mm});
            skLineSegment(sketch, "E1606", {"start": v(1.65, 0.65) * mm, "end": v(1.67, 0.63) * mm});
            skLineSegment(sketch, "E1607", {"start": v(1.67, 0.63) * mm, "end": v(1.67, 0.62) * mm});
            skLineSegment(sketch, "E1608", {"start": v(1.67, 0.62) * mm, "end": v(1.67, 0.6) * mm});
            skLineSegment(sketch, "E1609", {"start": v(1.67, 0.6) * mm, "end": v(1.66, 0.59) * mm});
            skLineSegment(sketch, "E1610", {"start": v(1.66, 0.59) * mm, "end": v(1.65, 0.57) * mm});
            skLineSegment(sketch, "E1611", {"start": v(1.65, 0.57) * mm, "end": v(1.65, 0.56) * mm});
            skLineSegment(sketch, "E1612", {"start": v(1.65, 0.56) * mm, "end": v(1.64, 0.55) * mm});
            skLineSegment(sketch, "E1613", {"start": v(1.64, 0.55) * mm, "end": v(1.61, 0.5) * mm});
            skLineSegment(sketch, "E1614", {"start": v(1.61, 0.5) * mm, "end": v(1.56, 0.43) * mm});
            skLineSegment(sketch, "E1615", {"start": v(1.56, 0.43) * mm, "end": v(1.5, 0.36) * mm});
            skLineSegment(sketch, "E1616", {"start": v(1.5, 0.36) * mm, "end": v(1.47, 0.32) * mm});
            skLineSegment(sketch, "E1617", {"start": v(1.47, 0.32) * mm, "end": v(1.46, 0.31) * mm});
            skLineSegment(sketch, "E1618", {"start": v(1.46, 0.31) * mm, "end": v(1.46, 0.3) * mm});
            skLineSegment(sketch, "E1619", {"start": v(1.46, 0.3) * mm, "end": v(1.43, 0.29) * mm});
            skLineSegment(sketch, "E1620", {"start": v(1.43, 0.29) * mm, "end": v(1.4, 0.26) * mm});
            skLineSegment(sketch, "E1621", {"start": v(1.4, 0.26) * mm, "end": v(1.35, 0.23) * mm});
            skLineSegment(sketch, "E1622", {"start": v(1.35, 0.23) * mm, "end": v(1.3, 0.21) * mm});
            skLineSegment(sketch, "E1623", {"start": v(1.3, 0.21) * mm, "end": v(1.27, 0.2) * mm});
            skLineSegment(sketch, "E1624", {"start": v(1.27, 0.2) * mm, "end": v(1.24, 0.18) * mm});
            skLineSegment(sketch, "E1625", {"start": v(1.24, 0.18) * mm, "end": v(1.21, 0.18) * mm});
            skLineSegment(sketch, "E1626", {"start": v(1.21, 0.18) * mm, "end": v(1.2, 0.18) * mm});
            skLineSegment(sketch, "E1627", {"start": v(1.2, 0.18) * mm, "end": v(1.2, 0.18) * mm});
            skLineSegment(sketch, "E1628", {"start": v(1.2, 0.18) * mm, "end": v(1.2, 0.19) * mm});
            skLineSegment(sketch, "E1629", {"start": v(1.2, 0.19) * mm, "end": v(1.2, 0.2) * mm});
            skLineSegment(sketch, "E1630", {"start": v(1.2, 0.2) * mm, "end": v(1.22, 0.22) * mm});
            skLineSegment(sketch, "E1631", {"start": v(1.22, 0.22) * mm, "end": v(1.23, 0.23) * mm});
            skLineSegment(sketch, "E1632", {"start": v(1.23, 0.23) * mm, "end": v(1.24, 0.23) * mm});
            skLineSegment(sketch, "E1633", {"start": v(1.24, 0.23) * mm, "end": v(1.25, 0.23) * mm});
            skLineSegment(sketch, "E1634", {"start": v(1.25, 0.23) * mm, "end": v(1.25, 0.23) * mm});
            skLineSegment(sketch, "E1635", {"start": v(1.25, 0.23) * mm, "end": v(1.26, 0.23) * mm});
            skLineSegment(sketch, "E1636", {"start": v(1.26, 0.23) * mm, "end": v(1.27, 0.24) * mm});
            skLineSegment(sketch, "E1637", {"start": v(1.27, 0.24) * mm, "end": v(1.28, 0.26) * mm});
            skLineSegment(sketch, "E1638", {"start": v(1.28, 0.26) * mm, "end": v(1.28, 0.28) * mm});
            skLineSegment(sketch, "E1639", {"start": v(1.28, 0.28) * mm, "end": v(1.28, 0.3) * mm});
            skLineSegment(sketch, "E1640", {"start": v(1.28, 0.3) * mm, "end": v(1.28, 0.3) * mm});
            skLineSegment(sketch, "E1641", {"start": v(1.28, 0.3) * mm, "end": v(1.29, 0.31) * mm});
            skLineSegment(sketch, "E1642", {"start": v(1.29, 0.31) * mm, "end": v(1.3, 0.32) * mm});
            skLineSegment(sketch, "E1643", {"start": v(1.3, 0.32) * mm, "end": v(1.3, 0.32) * mm});
            skLineSegment(sketch, "E1644", {"start": v(1.3, 0.32) * mm, "end": v(1.32, 0.33) * mm});
            skLineSegment(sketch, "E1645", {"start": v(1.32, 0.33) * mm, "end": v(1.33, 0.33) * mm});
            skLineSegment(sketch, "E1646", {"start": v(1.33, 0.33) * mm, "end": v(1.33, 0.33) * mm});
            skLineSegment(sketch, "E1647", {"start": v(1.33, 0.33) * mm, "end": v(1.32, 0.34) * mm});
            skLineSegment(sketch, "E1648", {"start": v(1.32, 0.34) * mm, "end": v(1.32, 0.34) * mm});
            skLineSegment(sketch, "E1649", {"start": v(1.32, 0.34) * mm, "end": v(1.31, 0.34) * mm});
            skLineSegment(sketch, "E1650", {"start": v(1.31, 0.34) * mm, "end": v(1.3, 0.35) * mm});
            skLineSegment(sketch, "E1651", {"start": v(1.3, 0.35) * mm, "end": v(1.3, 0.37) * mm});
            skLineSegment(sketch, "E1652", {"start": v(1.3, 0.37) * mm, "end": v(1.31, 0.37) * mm});
            skLineSegment(sketch, "E1653", {"start": v(1.31, 0.37) * mm, "end": v(1.32, 0.37) * mm});
            skLineSegment(sketch, "E1654", {"start": v(1.32, 0.37) * mm, "end": v(1.33, 0.4) * mm});
            skLineSegment(sketch, "E1655", {"start": v(1.33, 0.4) * mm, "end": v(1.33, 0.4) * mm});
            skLineSegment(sketch, "E1656", {"start": v(1.33, 0.4) * mm, "end": v(1.33, 0.41) * mm});
            skLineSegment(sketch, "E1657", {"start": v(1.33, 0.41) * mm, "end": v(1.33, 0.42) * mm});
            skLineSegment(sketch, "E1658", {"start": v(1.33, 0.42) * mm, "end": v(1.34, 0.43) * mm});
            skLineSegment(sketch, "E1659", {"start": v(1.34, 0.43) * mm, "end": v(1.35, 0.43) * mm});
            skLineSegment(sketch, "E1660", {"start": v(1.35, 0.43) * mm, "end": v(1.35, 0.43) * mm});
            skLineSegment(sketch, "E1661", {"start": v(1.35, 0.43) * mm, "end": v(1.36, 0.43) * mm});
            skLineSegment(sketch, "E1662", {"start": v(1.36, 0.43) * mm, "end": v(1.37, 0.45) * mm});
            skLineSegment(sketch, "E1663", {"start": v(1.37, 0.45) * mm, "end": v(1.38, 0.47) * mm});
            skLineSegment(sketch, "E1664", {"start": v(1.38, 0.47) * mm, "end": v(1.38, 0.5) * mm});
            skLineSegment(sketch, "E1665", {"start": v(1.38, 0.5) * mm, "end": v(1.38, 0.52) * mm});
            skLineSegment(sketch, "E1666", {"start": v(1.38, 0.52) * mm, "end": v(1.38, 0.52) * mm});
            skLineSegment(sketch, "E1667", {"start": v(1.38, 0.52) * mm, "end": v(1.38, 0.53) * mm});
            skLineSegment(sketch, "E1668", {"start": v(1.38, 0.53) * mm, "end": v(1.39, 0.53) * mm});
            skLineSegment(sketch, "E1669", {"start": v(1.39, 0.53) * mm, "end": v(1.39, 0.53) * mm});
            skLineSegment(sketch, "E1670", {"start": v(1.39, 0.53) * mm, "end": v(1.4, 0.54) * mm});
            skLineSegment(sketch, "E1671", {"start": v(1.4, 0.54) * mm, "end": v(1.41, 0.57) * mm});
            skLineSegment(sketch, "E1672", {"start": v(1.41, 0.57) * mm, "end": v(1.43, 0.62) * mm});
            skLineSegment(sketch, "E1673", {"start": v(1.43, 0.62) * mm, "end": v(1.43, 0.67) * mm});
            skLineSegment(sketch, "E1674", {"start": v(1.43, 0.67) * mm, "end": v(1.44, 0.68) * mm});
            skLineSegment(sketch, "E1675", {"start": v(1.44, 0.68) * mm, "end": v(1.44, 0.69) * mm});
            skLineSegment(sketch, "E1676", {"start": v(1.44, 0.69) * mm, "end": v(1.45, 0.72) * mm});
            skLineSegment(sketch, "E1677", {"start": v(1.45, 0.72) * mm, "end": v(1.45, 0.74) * mm});
            skLineSegment(sketch, "E1678", {"start": v(1.45, 0.74) * mm, "end": v(1.46, 0.75) * mm});
            skLineSegment(sketch, "E1679", {"start": v(1.46, 0.75) * mm, "end": v(1.46, 0.75) * mm});
            skLineSegment(sketch, "E1680", {"start": v(1.46, 0.75) * mm, "end": v(1.47, 0.77) * mm});
            skLineSegment(sketch, "E1681", {"start": v(1.47, 0.77) * mm, "end": v(1.47, 0.8) * mm});
            skLineSegment(sketch, "E1682", {"start": v(1.47, 0.8) * mm, "end": v(1.47, 0.8) * mm});
            skLineSegment(sketch, "E1683", {"start": v(1.47, 0.8) * mm, "end": v(1.47, 0.82) * mm});
            skLineSegment(sketch, "E1684", {"start": v(1.47, 0.82) * mm, "end": v(1.49, 0.82) * mm});
            skLineSegment(sketch, "E1685", {"start": v(1.49, 0.82) * mm, "end": v(1.51, 0.8) * mm});
            skLineSegment(sketch, "E1686", {"start": v(1.51, 0.8) * mm, "end": v(1.55, 0.77) * mm});
            skLineSegment(sketch, "E1687", {"start": v(1.55, 0.77) * mm, "end": v(1.56, 0.75) * mm});
            skLineSegment(sketch, "E1688", {"start": v(0.5, 0.76) * mm, "end": v(0.5, 0.76) * mm});
            skLineSegment(sketch, "E1689", {"start": v(0.5, 0.76) * mm, "end": v(0.5, 0.75) * mm});
            skLineSegment(sketch, "E1690", {"start": v(0.5, 0.75) * mm, "end": v(0.5, 0.74) * mm});
            skLineSegment(sketch, "E1691", {"start": v(0.5, 0.74) * mm, "end": v(0.5, 0.74) * mm});
            skLineSegment(sketch, "E1692", {"start": v(0.5, 0.74) * mm, "end": v(0.49, 0.74) * mm});
            skLineSegment(sketch, "E1693", {"start": v(0.49, 0.74) * mm, "end": v(0.48, 0.72) * mm});
            skLineSegment(sketch, "E1694", {"start": v(0.48, 0.72) * mm, "end": v(0.48, 0.72) * mm});
            skLineSegment(sketch, "E1695", {"start": v(0.48, 0.72) * mm, "end": v(0.48, 0.7) * mm});
            skLineSegment(sketch, "E1696", {"start": v(0.48, 0.7) * mm, "end": v(0.48, 0.7) * mm});
            skLineSegment(sketch, "E1697", {"start": v(0.48, 0.7) * mm, "end": v(0.47, 0.71) * mm});
            skLineSegment(sketch, "E1698", {"start": v(0.47, 0.71) * mm, "end": v(0.47, 0.72) * mm});
            skLineSegment(sketch, "E1699", {"start": v(0.47, 0.72) * mm, "end": v(0.46, 0.72) * mm});
            skLineSegment(sketch, "E1700", {"start": v(0.46, 0.72) * mm, "end": v(0.46, 0.73) * mm});
            skLineSegment(sketch, "E1701", {"start": v(0.46, 0.73) * mm, "end": v(0.45, 0.75) * mm});
            skLineSegment(sketch, "E1702", {"start": v(0.45, 0.75) * mm, "end": v(0.45, 0.76) * mm});
            skLineSegment(sketch, "E1703", {"start": v(0.45, 0.76) * mm, "end": v(0.45, 0.76) * mm});
            skLineSegment(sketch, "E1704", {"start": v(0.45, 0.76) * mm, "end": v(0.46, 0.77) * mm});
            skLineSegment(sketch, "E1705", {"start": v(0.46, 0.77) * mm, "end": v(0.48, 0.77) * mm});
            skLineSegment(sketch, "E1706", {"start": v(0.48, 0.77) * mm, "end": v(0.5, 0.77) * mm});
            skLineSegment(sketch, "E1707", {"start": v(0.5, 0.77) * mm, "end": v(0.5, 0.76) * mm});
            skLineSegment(sketch, "E1708", {"start": v(0.02, 0.58) * mm, "end": v(0.03, 0.58) * mm});
            skLineSegment(sketch, "E1709", {"start": v(0.03, 0.58) * mm, "end": v(0.05, 0.56) * mm});
            skLineSegment(sketch, "E1710", {"start": v(0.05, 0.56) * mm, "end": v(0.09, 0.52) * mm});
            skLineSegment(sketch, "E1711", {"start": v(0.09, 0.52) * mm, "end": v(0.12, 0.48) * mm});
            skLineSegment(sketch, "E1712", {"start": v(0.12, 0.48) * mm, "end": v(0.14, 0.44) * mm});
            skLineSegment(sketch, "E1713", {"start": v(0.14, 0.44) * mm, "end": v(0.15, 0.43) * mm});
            skLineSegment(sketch, "E1714", {"start": v(0.15, 0.43) * mm, "end": v(0.16, 0.41) * mm});
            skLineSegment(sketch, "E1715", {"start": v(0.16, 0.41) * mm, "end": v(0.2, 0.36) * mm});
            skLineSegment(sketch, "E1716", {"start": v(0.2, 0.36) * mm, "end": v(0.27, 0.3) * mm});
            skLineSegment(sketch, "E1717", {"start": v(0.27, 0.3) * mm, "end": v(0.35, 0.27) * mm});
            skLineSegment(sketch, "E1718", {"start": v(0.35, 0.27) * mm, "end": v(0.4, 0.26) * mm});
            skLineSegment(sketch, "E1719", {"start": v(0.4, 0.26) * mm, "end": v(0.42, 0.27) * mm});
            skLineSegment(sketch, "E1720", {"start": v(0.42, 0.27) * mm, "end": v(0.42, 0.27) * mm});
            skLineSegment(sketch, "E1721", {"start": v(0.42, 0.27) * mm, "end": v(0.43, 0.28) * mm});
            skLineSegment(sketch, "E1722", {"start": v(0.43, 0.28) * mm, "end": v(0.46, 0.3) * mm});
            skLineSegment(sketch, "E1723", {"start": v(0.46, 0.3) * mm, "end": v(0.5, 0.33) * mm});
            skLineSegment(sketch, "E1724", {"start": v(0.5, 0.33) * mm, "end": v(0.53, 0.35) * mm});
            skLineSegment(sketch, "E1725", {"start": v(0.53, 0.35) * mm, "end": v(0.54, 0.36) * mm});
            skLineSegment(sketch, "E1726", {"start": v(0.54, 0.36) * mm, "end": v(0.56, 0.38) * mm});
            skLineSegment(sketch, "E1727", {"start": v(0.56, 0.38) * mm, "end": v(0.64, 0.43) * mm});
            skLineSegment(sketch, "E1728", {"start": v(0.64, 0.43) * mm, "end": v(0.73, 0.47) * mm});
            skLineSegment(sketch, "E1729", {"start": v(0.73, 0.47) * mm, "end": v(0.83, 0.48) * mm});
            skLineSegment(sketch, "E1730", {"start": v(0.83, 0.48) * mm, "end": v(0.9, 0.47) * mm});
            skLineSegment(sketch, "E1731", {"start": v(0.9, 0.47) * mm, "end": v(0.92, 0.46) * mm});
            skLineSegment(sketch, "E1732", {"start": v(0.92, 0.46) * mm, "end": v(0.93, 0.45) * mm});
            skLineSegment(sketch, "E1733", {"start": v(0.93, 0.45) * mm, "end": v(0.95, 0.44) * mm});
            skLineSegment(sketch, "E1734", {"start": v(0.95, 0.44) * mm, "end": v(0.98, 0.42) * mm});
            skLineSegment(sketch, "E1735", {"start": v(0.98, 0.42) * mm, "end": v(1.02, 0.39) * mm});
            skLineSegment(sketch, "E1736", {"start": v(1.02, 0.39) * mm, "end": v(1.05, 0.36) * mm});
            skLineSegment(sketch, "E1737", {"start": v(1.05, 0.36) * mm, "end": v(1.08, 0.33) * mm});
            skLineSegment(sketch, "E1738", {"start": v(1.08, 0.33) * mm, "end": v(1.1, 0.3) * mm});
            skLineSegment(sketch, "E1739", {"start": v(1.1, 0.3) * mm, "end": v(1.12, 0.28) * mm});
            skLineSegment(sketch, "E1740", {"start": v(1.12, 0.28) * mm, "end": v(1.12, 0.27) * mm});
            skLineSegment(sketch, "E1741", {"start": v(1.12, 0.27) * mm, "end": v(1.12, 0.27) * mm});
            skLineSegment(sketch, "E1742", {"start": v(1.12, 0.27) * mm, "end": v(1.12, 0.26) * mm});
            skLineSegment(sketch, "E1743", {"start": v(1.12, 0.26) * mm, "end": v(1.12, 0.25) * mm});
            skLineSegment(sketch, "E1744", {"start": v(1.12, 0.25) * mm, "end": v(1.12, 0.23) * mm});
            skLineSegment(sketch, "E1745", {"start": v(1.12, 0.23) * mm, "end": v(1.13, 0.23) * mm});
            skLineSegment(sketch, "E1746", {"start": v(1.13, 0.23) * mm, "end": v(1.13, 0.22) * mm});
            skLineSegment(sketch, "E1747", {"start": v(1.13, 0.22) * mm, "end": v(1.14, 0.2) * mm});
            skLineSegment(sketch, "E1748", {"start": v(1.14, 0.2) * mm, "end": v(1.15, 0.18) * mm});
            skLineSegment(sketch, "E1749", {"start": v(1.15, 0.18) * mm, "end": v(1.15, 0.15) * mm});
            skLineSegment(sketch, "E1750", {"start": v(1.15, 0.15) * mm, "end": v(1.15, 0.12) * mm});
            skLineSegment(sketch, "E1751", {"start": v(1.15, 0.12) * mm, "end": v(1.15, 0.11) * mm});
            skLineSegment(sketch, "E1752", {"start": v(1.15, 0.11) * mm, "end": v(1.15, 0.08) * mm});
            skLineSegment(sketch, "E1753", {"start": v(1.15, 0.08) * mm, "end": v(1.14, 0) * mm});
            skLineSegment(sketch, "E1754", {"start": v(1.14, 0) * mm, "end": v(1.12, -0.08) * mm});
            skLineSegment(sketch, "E1755", {"start": v(1.12, -0.08) * mm, "end": v(1.09, -0.15) * mm});
            skLineSegment(sketch, "E1756", {"start": v(1.09, -0.15) * mm, "end": v(1.05, -0.2) * mm});
            skLineSegment(sketch, "E1757", {"start": v(1.05, -0.2) * mm, "end": v(1.03, -0.2) * mm});
            skLineSegment(sketch, "E1758", {"start": v(1.03, -0.2) * mm, "end": v(1.03, -0.21) * mm});
            skLineSegment(sketch, "E1759", {"start": v(1.03, -0.21) * mm, "end": v(1, -0.23) * mm});
            skLineSegment(sketch, "E1760", {"start": v(1, -0.23) * mm, "end": v(0.98, -0.26) * mm});
            skLineSegment(sketch, "E1761", {"start": v(0.98, -0.26) * mm, "end": v(0.97, -0.28) * mm});
            skLineSegment(sketch, "E1762", {"start": v(0.97, -0.28) * mm, "end": v(0.97, -0.3) * mm});
            skLineSegment(sketch, "E1763", {"start": v(0.97, -0.3) * mm, "end": v(0.97, -0.3) * mm});
            skLineSegment(sketch, "E1764", {"start": v(0.97, -0.3) * mm, "end": v(0.96, -0.32) * mm});
            skLineSegment(sketch, "E1765", {"start": v(0.96, -0.32) * mm, "end": v(0.93, -0.36) * mm});
            skLineSegment(sketch, "E1766", {"start": v(0.93, -0.36) * mm, "end": v(0.9, -0.41) * mm});
            skLineSegment(sketch, "E1767", {"start": v(0.9, -0.41) * mm, "end": v(0.84, -0.47) * mm});
            skLineSegment(sketch, "E1768", {"start": v(0.84, -0.47) * mm, "end": v(0.8, -0.53) * mm});
            skLineSegment(sketch, "E1769", {"start": v(0.8, -0.53) * mm, "end": v(0.74, -0.58) * mm});
            skLineSegment(sketch, "E1770", {"start": v(0.74, -0.58) * mm, "end": v(0.7, -0.6) * mm});
            skLineSegment(sketch, "E1771", {"start": v(0.7, -0.6) * mm, "end": v(0.69, -0.62) * mm});
            skLineSegment(sketch, "E1772", {"start": v(0.69, -0.62) * mm, "end": v(0.69, -0.62) * mm});
            skLineSegment(sketch, "E1773", {"start": v(0.69, -0.62) * mm, "end": v(0.68, -0.62) * mm});
            skLineSegment(sketch, "E1774", {"start": v(0.68, -0.62) * mm, "end": v(0.67, -0.63) * mm});
            skLineSegment(sketch, "E1775", {"start": v(0.67, -0.63) * mm, "end": v(0.66, -0.64) * mm});
            skLineSegment(sketch, "E1776", {"start": v(0.66, -0.64) * mm, "end": v(0.63, -0.66) * mm});
            skLineSegment(sketch, "E1777", {"start": v(0.63, -0.66) * mm, "end": v(0.62, -0.68) * mm});
            skLineSegment(sketch, "E1778", {"start": v(0.62, -0.68) * mm, "end": v(0.61, -0.7) * mm});
            skLineSegment(sketch, "E1779", {"start": v(0.61, -0.7) * mm, "end": v(0.59, -0.72) * mm});
            skLineSegment(sketch, "E1780", {"start": v(0.59, -0.72) * mm, "end": v(0.5, -0.78) * mm});
            skLineSegment(sketch, "E1781", {"start": v(0.5, -0.78) * mm, "end": v(0.38, -0.81) * mm});
            skLineSegment(sketch, "E1782", {"start": v(0.38, -0.81) * mm, "end": v(0.26, -0.79) * mm});
            skLineSegment(sketch, "E1783", {"start": v(0.26, -0.79) * mm, "end": v(0.18, -0.74) * mm});
            skLineSegment(sketch, "E1784", {"start": v(0.18, -0.74) * mm, "end": v(0.16, -0.71) * mm});
            skLineSegment(sketch, "E1785", {"start": v(0.16, -0.71) * mm, "end": v(0.15, -0.7) * mm});
            skLineSegment(sketch, "E1786", {"start": v(0.15, -0.7) * mm, "end": v(0.1, -0.65) * mm});
            skLineSegment(sketch, "E1787", {"start": v(0.1, -0.65) * mm, "end": v(0.03, -0.62) * mm});
            skLineSegment(sketch, "E1788", {"start": v(0.03, -0.62) * mm, "end": v(-0.04, -0.63) * mm});
            skLineSegment(sketch, "E1789", {"start": v(-0.04, -0.63) * mm, "end": v(-0.08, -0.66) * mm});
            skLineSegment(sketch, "E1790", {"start": v(-0.08, -0.66) * mm, "end": v(-0.1, -0.67) * mm});
            skLineSegment(sketch, "E1791", {"start": v(-0.1, -0.67) * mm, "end": v(-0.11, -0.7) * mm});
            skLineSegment(sketch, "E1792", {"start": v(-0.11, -0.7) * mm, "end": v(-0.17, -0.76) * mm});
            skLineSegment(sketch, "E1793", {"start": v(-0.17, -0.76) * mm, "end": v(-0.25, -0.81) * mm});
            skLineSegment(sketch, "E1794", {"start": v(-0.25, -0.81) * mm, "end": v(-0.32, -0.84) * mm});
            skLineSegment(sketch, "E1795", {"start": v(-0.32, -0.84) * mm, "end": v(-0.38, -0.85) * mm});
            skLineSegment(sketch, "E1796", {"start": v(-0.38, -0.85) * mm, "end": v(-0.4, -0.85) * mm});
            skLineSegment(sketch, "E1797", {"start": v(-0.4, -0.85) * mm, "end": v(-0.42, -0.85) * mm});
            skLineSegment(sketch, "E1798", {"start": v(-0.42, -0.85) * mm, "end": v(-0.48, -0.83) * mm});
            skLineSegment(sketch, "E1799", {"start": v(-0.48, -0.83) * mm, "end": v(-0.55, -0.8) * mm});
            skLineSegment(sketch, "E1800", {"start": v(-0.55, -0.8) * mm, "end": v(-0.61, -0.77) * mm});
            skLineSegment(sketch, "E1801", {"start": v(-0.61, -0.77) * mm, "end": v(-0.64, -0.75) * mm});
            skLineSegment(sketch, "E1802", {"start": v(-0.64, -0.75) * mm, "end": v(-0.64, -0.74) * mm});
            skLineSegment(sketch, "E1803", {"start": v(-0.64, -0.74) * mm, "end": v(-0.65, -0.73) * mm});
            skLineSegment(sketch, "E1804", {"start": v(-0.65, -0.73) * mm, "end": v(-0.66, -0.7) * mm});
            skLineSegment(sketch, "E1805", {"start": v(-0.66, -0.7) * mm, "end": v(-0.67, -0.67) * mm});
            skLineSegment(sketch, "E1806", {"start": v(-0.67, -0.67) * mm, "end": v(-0.67, -0.65) * mm});
            skLineSegment(sketch, "E1807", {"start": v(-0.67, -0.65) * mm, "end": v(-0.67, -0.63) * mm});
            skLineSegment(sketch, "E1808", {"start": v(-0.67, -0.63) * mm, "end": v(-0.67, -0.63) * mm});
            skLineSegment(sketch, "E1809", {"start": v(-0.67, -0.63) * mm, "end": v(-0.67, -0.62) * mm});
            skLineSegment(sketch, "E1810", {"start": v(-0.67, -0.62) * mm, "end": v(-0.69, -0.6) * mm});
            skLineSegment(sketch, "E1811", {"start": v(-0.69, -0.6) * mm, "end": v(-0.74, -0.58) * mm});
            skLineSegment(sketch, "E1812", {"start": v(-0.74, -0.58) * mm, "end": v(-0.84, -0.57) * mm});
            skLineSegment(sketch, "E1813", {"start": v(-0.84, -0.57) * mm, "end": v(-0.95, -0.56) * mm});
            skLineSegment(sketch, "E1814", {"start": v(-0.95, -0.56) * mm, "end": v(-0.99, -0.56) * mm});
            skLineSegment(sketch, "E1815", {"start": v(-0.99, -0.56) * mm, "end": v(-1.03, -0.56) * mm});
            skLineSegment(sketch, "E1816", {"start": v(-1.03, -0.56) * mm, "end": v(-1.14, -0.55) * mm});
            skLineSegment(sketch, "E1817", {"start": v(-1.14, -0.55) * mm, "end": v(-1.24, -0.53) * mm});
            skLineSegment(sketch, "E1818", {"start": v(-1.24, -0.53) * mm, "end": v(-1.32, -0.5) * mm});
            skLineSegment(sketch, "E1819", {"start": v(-1.32, -0.5) * mm, "end": v(-1.37, -0.48) * mm});
            skLineSegment(sketch, "E1820", {"start": v(-1.37, -0.48) * mm, "end": v(-1.39, -0.47) * mm});
            skLineSegment(sketch, "E1821", {"start": v(-1.39, -0.47) * mm, "end": v(-1.4, -0.47) * mm});
            skLineSegment(sketch, "E1822", {"start": v(-1.4, -0.47) * mm, "end": v(-1.42, -0.45) * mm});
            skLineSegment(sketch, "E1823", {"start": v(-1.42, -0.45) * mm, "end": v(-1.46, -0.41) * mm});
            skLineSegment(sketch, "E1824", {"start": v(-1.46, -0.41) * mm, "end": v(-1.49, -0.37) * mm});
            skLineSegment(sketch, "E1825", {"start": v(-1.49, -0.37) * mm, "end": v(-1.52, -0.33) * mm});
            skLineSegment(sketch, "E1826", {"start": v(-1.52, -0.33) * mm, "end": v(-1.54, -0.3) * mm});
            skLineSegment(sketch, "E1827", {"start": v(-1.54, -0.3) * mm, "end": v(-1.55, -0.26) * mm});
            skLineSegment(sketch, "E1828", {"start": v(-1.55, -0.26) * mm, "end": v(-1.54, -0.25) * mm});
            skLineSegment(sketch, "E1829", {"start": v(-1.54, -0.25) * mm, "end": v(-1.53, -0.25) * mm});
            skLineSegment(sketch, "E1830", {"start": v(-1.53, -0.25) * mm, "end": v(-1.52, -0.25) * mm});
            skLineSegment(sketch, "E1831", {"start": v(-1.52, -0.25) * mm, "end": v(-1.52, -0.25) * mm});
            skLineSegment(sketch, "E1832", {"start": v(-1.52, -0.25) * mm, "end": v(-1.5, -0.25) * mm});
            skLineSegment(sketch, "E1833", {"start": v(-1.5, -0.25) * mm, "end": v(-1.5, -0.24) * mm});
            skLineSegment(sketch, "E1834", {"start": v(-1.5, -0.24) * mm, "end": v(-1.5, -0.23) * mm});
            skLineSegment(sketch, "E1835", {"start": v(-1.5, -0.23) * mm, "end": v(-1.5, -0.23) * mm});
            skLineSegment(sketch, "E1836", {"start": v(-1.5, -0.23) * mm, "end": v(-1.51, -0.22) * mm});
            skLineSegment(sketch, "E1837", {"start": v(-1.51, -0.22) * mm, "end": v(-1.52, -0.21) * mm});
            skLineSegment(sketch, "E1838", {"start": v(-1.52, -0.21) * mm, "end": v(-1.53, -0.21) * mm});
            skLineSegment(sketch, "E1839", {"start": v(-1.53, -0.21) * mm, "end": v(-1.53, -0.21) * mm});
            skLineSegment(sketch, "E1840", {"start": v(-1.53, -0.21) * mm, "end": v(-1.54, -0.21) * mm});
            skLineSegment(sketch, "E1841", {"start": v(-1.54, -0.21) * mm, "end": v(-1.55, -0.2) * mm});
            skLineSegment(sketch, "E1842", {"start": v(-1.55, -0.2) * mm, "end": v(-1.55, -0.18) * mm});
            skLineSegment(sketch, "E1843", {"start": v(-1.55, -0.18) * mm, "end": v(-1.56, -0.16) * mm});
            skLineSegment(sketch, "E1844", {"start": v(-1.56, -0.16) * mm, "end": v(-1.56, -0.16) * mm});
            skLineSegment(sketch, "E1845", {"start": v(-1.56, -0.16) * mm, "end": v(-1.56, -0.15) * mm});
            skLineSegment(sketch, "E1846", {"start": v(-1.56, -0.15) * mm, "end": v(-1.55, -0.13) * mm});
            skLineSegment(sketch, "E1847", {"start": v(-1.55, -0.13) * mm, "end": v(-1.55, -0.1) * mm});
            skLineSegment(sketch, "E1848", {"start": v(-1.55, -0.1) * mm, "end": v(-1.53, -0.07) * mm});
            skLineSegment(sketch, "E1849", {"start": v(-1.53, -0.07) * mm, "end": v(-1.51, -0.05) * mm});
            skLineSegment(sketch, "E1850", {"start": v(-1.51, -0.05) * mm, "end": v(-1.5, -0.03) * mm});
            skLineSegment(sketch, "E1851", {"start": v(-1.5, -0.03) * mm, "end": v(-1.47, -0.02) * mm});
            skLineSegment(sketch, "E1852", {"start": v(-1.47, -0.02) * mm, "end": v(-1.44, 0) * mm});
            skLineSegment(sketch, "E1853", {"start": v(-1.44, 0) * mm, "end": v(-1.42, 0) * mm});
            skLineSegment(sketch, "E1854", {"start": v(-1.42, 0) * mm, "end": v(-1.41, 0) * mm});
            skLineSegment(sketch, "E1855", {"start": v(-1.41, 0) * mm, "end": v(-1.4, -0.01) * mm});
            skLineSegment(sketch, "E1856", {"start": v(-1.4, -0.01) * mm, "end": v(-1.38, 0) * mm});
            skLineSegment(sketch, "E1857", {"start": v(-1.38, 0) * mm, "end": v(-1.36, 0) * mm});
            skLineSegment(sketch, "E1858", {"start": v(-1.36, 0) * mm, "end": v(-1.35, 0.03) * mm});
            skLineSegment(sketch, "E1859", {"start": v(-1.35, 0.03) * mm, "end": v(-1.36, 0.04) * mm});
            skLineSegment(sketch, "E1860", {"start": v(-1.36, 0.04) * mm, "end": v(-1.37, 0.04) * mm});
            skLineSegment(sketch, "E1861", {"start": v(-1.37, 0.04) * mm, "end": v(-1.37, 0.05) * mm});
            skLineSegment(sketch, "E1862", {"start": v(-1.37, 0.05) * mm, "end": v(-1.38, 0.08) * mm});
            skLineSegment(sketch, "E1863", {"start": v(-1.38, 0.08) * mm, "end": v(-1.38, 0.14) * mm});
            skLineSegment(sketch, "E1864", {"start": v(-1.38, 0.14) * mm, "end": v(-1.37, 0.22) * mm});
            skLineSegment(sketch, "E1865", {"start": v(-1.37, 0.22) * mm, "end": v(-1.36, 0.28) * mm});
            skLineSegment(sketch, "E1866", {"start": v(-1.36, 0.28) * mm, "end": v(-1.36, 0.3) * mm});
            skLineSegment(sketch, "E1867", {"start": v(-1.36, 0.3) * mm, "end": v(-1.35, 0.32) * mm});
            skLineSegment(sketch, "E1868", {"start": v(-1.35, 0.32) * mm, "end": v(-1.3, 0.4) * mm});
            skLineSegment(sketch, "E1869", {"start": v(-1.3, 0.4) * mm, "end": v(-1.22, 0.47) * mm});
            skLineSegment(sketch, "E1870", {"start": v(-1.22, 0.47) * mm, "end": v(-1.1, 0.5) * mm});
            skLineSegment(sketch, "E1871", {"start": v(-1.1, 0.5) * mm, "end": v(-0.97, 0.49) * mm});
            skLineSegment(sketch, "E1872", {"start": v(-0.97, 0.49) * mm, "end": v(-0.93, 0.48) * mm});
            skLineSegment(sketch, "E1873", {"start": v(-0.93, 0.48) * mm, "end": v(-0.9, 0.48) * mm});
            skLineSegment(sketch, "E1874", {"start": v(-0.9, 0.48) * mm, "end": v(-0.83, 0.45) * mm});
            skLineSegment(sketch, "E1875", {"start": v(-0.83, 0.45) * mm, "end": v(-0.75, 0.4) * mm});
            skLineSegment(sketch, "E1876", {"start": v(-0.75, 0.4) * mm, "end": v(-0.69, 0.32) * mm});
            skLineSegment(sketch, "E1877", {"start": v(-0.69, 0.32) * mm, "end": v(-0.65, 0.25) * mm});
            skLineSegment(sketch, "E1878", {"start": v(-0.65, 0.25) * mm, "end": v(-0.64, 0.23) * mm});
            skLineSegment(sketch, "E1879", {"start": v(-0.64, 0.23) * mm, "end": v(-0.63, 0.21) * mm});
            skLineSegment(sketch, "E1880", {"start": v(-0.63, 0.21) * mm, "end": v(-0.6, 0.18) * mm});
            skLineSegment(sketch, "E1881", {"start": v(-0.6, 0.18) * mm, "end": v(-0.54, 0.2) * mm});
            skLineSegment(sketch, "E1882", {"start": v(-0.54, 0.2) * mm, "end": v(-0.48, 0.25) * mm});
            skLineSegment(sketch, "E1883", {"start": v(-0.48, 0.25) * mm, "end": v(-0.43, 0.32) * mm});
            skLineSegment(sketch, "E1884", {"start": v(-0.43, 0.32) * mm, "end": v(-0.41, 0.35) * mm});
            skLineSegment(sketch, "E1885", {"start": v(-0.41, 0.35) * mm, "end": v(-0.4, 0.38) * mm});
            skLineSegment(sketch, "E1886", {"start": v(-0.4, 0.38) * mm, "end": v(-0.32, 0.47) * mm});
            skLineSegment(sketch, "E1887", {"start": v(-0.32, 0.47) * mm, "end": v(-0.2, 0.56) * mm});
            skLineSegment(sketch, "E1888", {"start": v(-0.2, 0.56) * mm, "end": v(-0.09, 0.6) * mm});
            skLineSegment(sketch, "E1889", {"start": v(-0.09, 0.6) * mm, "end": v(0, 0.6) * mm});
            skLineSegment(sketch, "E1890", {"start": v(0, 0.6) * mm, "end": v(0.02, 0.58) * mm});
            skLineSegment(sketch, "E1891", {"start": v(-1.73, 0.56) * mm, "end": v(-1.74, 0.55) * mm});
            skLineSegment(sketch, "E1892", {"start": v(-1.74, 0.55) * mm, "end": v(-1.75, 0.5) * mm});
            skLineSegment(sketch, "E1893", {"start": v(-1.75, 0.5) * mm, "end": v(-1.74, 0.43) * mm});
            skLineSegment(sketch, "E1894", {"start": v(-1.74, 0.43) * mm, "end": v(-1.71, 0.35) * mm});
            skLineSegment(sketch, "E1895", {"start": v(-1.71, 0.35) * mm, "end": v(-1.69, 0.3) * mm});
            skLineSegment(sketch, "E1896", {"start": v(-1.69, 0.3) * mm, "end": v(-1.67, 0.28) * mm});
            skLineSegment(sketch, "E1897", {"start": v(-1.67, 0.28) * mm, "end": v(-1.67, 0.28) * mm});
            skLineSegment(sketch, "E1898", {"start": v(-1.67, 0.28) * mm, "end": v(-1.66, 0.27) * mm});
            skLineSegment(sketch, "E1899", {"start": v(-1.66, 0.27) * mm, "end": v(-1.66, 0.25) * mm});
            skLineSegment(sketch, "E1900", {"start": v(-1.66, 0.25) * mm, "end": v(-1.66, 0.25) * mm});
            skLineSegment(sketch, "E1901", {"start": v(-1.66, 0.25) * mm, "end": v(-1.66, 0.24) * mm});
            skLineSegment(sketch, "E1902", {"start": v(-1.66, 0.24) * mm, "end": v(-1.65, 0.23) * mm});
            skLineSegment(sketch, "E1903", {"start": v(-1.65, 0.23) * mm, "end": v(-1.63, 0.2) * mm});
            skLineSegment(sketch, "E1904", {"start": v(-1.63, 0.2) * mm, "end": v(-1.62, 0.2) * mm});
            skLineSegment(sketch, "E1905", {"start": v(-1.62, 0.2) * mm, "end": v(-1.62, 0.2) * mm});
            skLineSegment(sketch, "E1906", {"start": v(-1.62, 0.2) * mm, "end": v(-1.6, 0.17) * mm});
            skLineSegment(sketch, "E1907", {"start": v(-1.6, 0.17) * mm, "end": v(-1.59, 0.15) * mm});
            skLineSegment(sketch, "E1908", {"start": v(-1.59, 0.15) * mm, "end": v(-1.59, 0.15) * mm});
            skLineSegment(sketch, "E1909", {"start": v(-1.59, 0.15) * mm, "end": v(-1.58, 0.14) * mm});
            skLineSegment(sketch, "E1910", {"start": v(-1.58, 0.14) * mm, "end": v(-1.57, 0.13) * mm});
            skLineSegment(sketch, "E1911", {"start": v(-1.57, 0.13) * mm, "end": v(-1.56, 0.11) * mm});
            skLineSegment(sketch, "E1912", {"start": v(-1.56, 0.11) * mm, "end": v(-1.55, 0.1) * mm});
            skLineSegment(sketch, "E1913", {"start": v(-1.55, 0.1) * mm, "end": v(-1.55, 0.1) * mm});
            skLineSegment(sketch, "E1914", {"start": v(-1.55, 0.1) * mm, "end": v(-1.54, 0.09) * mm});
            skLineSegment(sketch, "E1915", {"start": v(-1.54, 0.09) * mm, "end": v(-1.52, 0.07) * mm});
            skLineSegment(sketch, "E1916", {"start": v(-1.52, 0.07) * mm, "end": v(-1.52, 0.06) * mm});
            skLineSegment(sketch, "E1917", {"start": v(-1.52, 0.06) * mm, "end": v(-1.52, 0.05) * mm});
            skLineSegment(sketch, "E1918", {"start": v(-1.52, 0.05) * mm, "end": v(-1.53, 0.05) * mm});
            skLineSegment(sketch, "E1919", {"start": v(-1.53, 0.05) * mm, "end": v(-1.53, 0.05) * mm});
            skLineSegment(sketch, "E1920", {"start": v(-1.53, 0.05) * mm, "end": v(-1.55, 0.05) * mm});
            skLineSegment(sketch, "E1921", {"start": v(-1.55, 0.05) * mm, "end": v(-1.6, 0.04) * mm});
            skLineSegment(sketch, "E1922", {"start": v(-1.6, 0.04) * mm, "end": v(-1.7, 0.01) * mm});
            skLineSegment(sketch, "E1923", {"start": v(-1.7, 0.01) * mm, "end": v(-1.77, -0.02) * mm});
            skLineSegment(sketch, "E1924", {"start": v(-1.77, -0.02) * mm, "end": v(-1.81, -0.04) * mm});
            skLineSegment(sketch, "E1925", {"start": v(-1.81, -0.04) * mm, "end": v(-1.82, -0.05) * mm});
            skLineSegment(sketch, "E1926", {"start": v(-1.82, -0.05) * mm, "end": v(-1.83, -0.06) * mm});
            skLineSegment(sketch, "E1927", {"start": v(-1.83, -0.06) * mm, "end": v(-1.84, -0.07) * mm});
            skLineSegment(sketch, "E1928", {"start": v(-1.84, -0.07) * mm, "end": v(-1.85, -0.07) * mm});
            skLineSegment(sketch, "E1929", {"start": v(-1.85, -0.07) * mm, "end": v(-1.85, -0.07) * mm});
            skLineSegment(sketch, "E1930", {"start": v(-1.85, -0.07) * mm, "end": v(-1.86, -0.06) * mm});
            skLineSegment(sketch, "E1931", {"start": v(-1.86, -0.06) * mm, "end": v(-1.86, -0.03) * mm});
            skLineSegment(sketch, "E1932", {"start": v(-1.86, -0.03) * mm, "end": v(-1.86, 0) * mm});
            skLineSegment(sketch, "E1933", {"start": v(-1.86, 0) * mm, "end": v(-1.86, 0.05) * mm});
            skLineSegment(sketch, "E1934", {"start": v(-1.86, 0.05) * mm, "end": v(-1.86, 0.1) * mm});
            skLineSegment(sketch, "E1935", {"start": v(-1.86, 0.1) * mm, "end": v(-1.86, 0.1) * mm});
            skLineSegment(sketch, "E1936", {"start": v(-1.86, 0.1) * mm, "end": v(-1.86, 0.15) * mm});
            skLineSegment(sketch, "E1937", {"start": v(-1.86, 0.15) * mm, "end": v(-1.85, 0.25) * mm});
            skLineSegment(sketch, "E1938", {"start": v(-1.85, 0.25) * mm, "end": v(-1.83, 0.38) * mm});
            skLineSegment(sketch, "E1939", {"start": v(-1.83, 0.38) * mm, "end": v(-1.8, 0.47) * mm});
            skLineSegment(sketch, "E1940", {"start": v(-1.8, 0.47) * mm, "end": v(-1.8, 0.52) * mm});
            skLineSegment(sketch, "E1941", {"start": v(-1.8, 0.52) * mm, "end": v(-1.78, 0.53) * mm});
            skLineSegment(sketch, "E1942", {"start": v(-1.78, 0.53) * mm, "end": v(-1.78, 0.54) * mm});
            skLineSegment(sketch, "E1943", {"start": v(-1.78, 0.54) * mm, "end": v(-1.76, 0.56) * mm});
            skLineSegment(sketch, "E1944", {"start": v(-1.76, 0.56) * mm, "end": v(-1.75, 0.58) * mm});
            skLineSegment(sketch, "E1945", {"start": v(-1.75, 0.58) * mm, "end": v(-1.75, 0.6) * mm});
            skLineSegment(sketch, "E1946", {"start": v(-1.75, 0.6) * mm, "end": v(-1.75, 0.6) * mm});
            skLineSegment(sketch, "E1947", {"start": v(-1.75, 0.6) * mm, "end": v(-1.74, 0.6) * mm});
            skLineSegment(sketch, "E1948", {"start": v(-1.74, 0.6) * mm, "end": v(-1.74, 0.6) * mm});
            skLineSegment(sketch, "E1949", {"start": v(-1.74, 0.6) * mm, "end": v(-1.74, 0.59) * mm});
            skLineSegment(sketch, "E1950", {"start": v(-1.74, 0.59) * mm, "end": v(-1.73, 0.57) * mm});
            skLineSegment(sketch, "E1951", {"start": v(-1.73, 0.57) * mm, "end": v(-1.73, 0.56) * mm});
            skLineSegment(sketch, "E1952", {"start": v(-1.73, 0.56) * mm, "end": v(-1.73, 0.56) * mm});
            skLineSegment(sketch, "E1953", {"start": v(1.75, 0.54) * mm, "end": v(1.77, 0.5) * mm});
            skLineSegment(sketch, "E1954", {"start": v(1.77, 0.5) * mm, "end": v(1.82, 0.38) * mm});
            skLineSegment(sketch, "E1955", {"start": v(1.82, 0.38) * mm, "end": v(1.8, 0.24) * mm});
            skLineSegment(sketch, "E1956", {"start": v(1.8, 0.24) * mm, "end": v(1.68, 0.1) * mm});
            skLineSegment(sketch, "E1957", {"start": v(1.68, 0.1) * mm, "end": v(1.54, 0) * mm});
            skLineSegment(sketch, "E1958", {"start": v(1.54, 0) * mm, "end": v(1.48, -0.02) * mm});
            skLineSegment(sketch, "E1959", {"start": v(1.48, -0.02) * mm, "end": v(1.47, -0.03) * mm});
            skLineSegment(sketch, "E1960", {"start": v(1.47, -0.03) * mm, "end": v(1.42, -0.06) * mm});
            skLineSegment(sketch, "E1961", {"start": v(1.42, -0.06) * mm, "end": v(1.35, -0.09) * mm});
            skLineSegment(sketch, "E1962", {"start": v(1.35, -0.09) * mm, "end": v(1.29, -0.11) * mm});
            skLineSegment(sketch, "E1963", {"start": v(1.29, -0.11) * mm, "end": v(1.26, -0.13) * mm});
            skLineSegment(sketch, "E1964", {"start": v(1.26, -0.13) * mm, "end": v(1.25, -0.13) * mm});
            skLineSegment(sketch, "E1965", {"start": v(1.25, -0.13) * mm, "end": v(1.24, -0.13) * mm});
            skLineSegment(sketch, "E1966", {"start": v(1.24, -0.13) * mm, "end": v(1.21, -0.14) * mm});
            skLineSegment(sketch, "E1967", {"start": v(1.21, -0.14) * mm, "end": v(1.18, -0.16) * mm});
            skLineSegment(sketch, "E1968", {"start": v(1.18, -0.16) * mm, "end": v(1.15, -0.18) * mm});
            skLineSegment(sketch, "E1969", {"start": v(1.15, -0.18) * mm, "end": v(1.13, -0.2) * mm});
            skLineSegment(sketch, "E1970", {"start": v(1.13, -0.2) * mm, "end": v(1.13, -0.2) * mm});
            skLineSegment(sketch, "E1971", {"start": v(1.13, -0.2) * mm, "end": v(1.12, -0.2) * mm});
            skLineSegment(sketch, "E1972", {"start": v(1.12, -0.2) * mm, "end": v(1.1, -0.22) * mm});
            skLineSegment(sketch, "E1973", {"start": v(1.1, -0.22) * mm, "end": v(1.08, -0.23) * mm});
            skLineSegment(sketch, "E1974", {"start": v(1.08, -0.23) * mm, "end": v(1.07, -0.22) * mm});
            skLineSegment(sketch, "E1975", {"start": v(1.07, -0.22) * mm, "end": v(1.08, -0.21) * mm});
            skLineSegment(sketch, "E1976", {"start": v(1.08, -0.21) * mm, "end": v(1.08, -0.2) * mm});
            skLineSegment(sketch, "E1977", {"start": v(1.08, -0.2) * mm, "end": v(1.1, -0.2) * mm});
            skLineSegment(sketch, "E1978", {"start": v(1.1, -0.2) * mm, "end": v(1.12, -0.15) * mm});
            skLineSegment(sketch, "E1979", {"start": v(1.12, -0.15) * mm, "end": v(1.15, -0.07) * mm});
            skLineSegment(sketch, "E1980", {"start": v(1.15, -0.07) * mm, "end": v(1.18, 0.02) * mm});
            skLineSegment(sketch, "E1981", {"start": v(1.18, 0.02) * mm, "end": v(1.2, 0.07) * mm});
            skLineSegment(sketch, "E1982", {"start": v(1.2, 0.07) * mm, "end": v(1.2, 0.1) * mm});
            skLineSegment(sketch, "E1983", {"start": v(1.2, 0.1) * mm, "end": v(1.2, 0.16) * mm});
            skLineSegment(sketch, "E1984", {"start": v(1.2, 0.16) * mm, "end": v(1.26, 0.15) * mm});
            skLineSegment(sketch, "E1985", {"start": v(1.26, 0.15) * mm, "end": v(1.28, 0.15) * mm});
            skLineSegment(sketch, "E1986", {"start": v(1.28, 0.15) * mm, "end": v(1.32, 0.15) * mm});
            skLineSegment(sketch, "E1987", {"start": v(1.32, 0.15) * mm, "end": v(1.34, 0.14) * mm});
            skLineSegment(sketch, "E1988", {"start": v(1.34, 0.14) * mm, "end": v(1.35, 0.12) * mm});
            skLineSegment(sketch, "E1989", {"start": v(1.35, 0.12) * mm, "end": v(1.34, 0.1) * mm});
            skLineSegment(sketch, "E1990", {"start": v(1.34, 0.1) * mm, "end": v(1.34, 0.1) * mm});
            skLineSegment(sketch, "E1991", {"start": v(1.34, 0.1) * mm, "end": v(1.33, 0.1) * mm});
            skLineSegment(sketch, "E1992", {"start": v(1.33, 0.1) * mm, "end": v(1.32, 0.09) * mm});
            skLineSegment(sketch, "E1993", {"start": v(1.32, 0.09) * mm, "end": v(1.32, 0.08) * mm});
            skLineSegment(sketch, "E1994", {"start": v(1.32, 0.08) * mm, "end": v(1.32, 0.07) * mm});
            skLineSegment(sketch, "E1995", {"start": v(1.32, 0.07) * mm, "end": v(1.32, 0.07) * mm});
            skLineSegment(sketch, "E1996", {"start": v(1.32, 0.07) * mm, "end": v(1.31, 0.06) * mm});
            skLineSegment(sketch, "E1997", {"start": v(1.31, 0.06) * mm, "end": v(1.3, 0.03) * mm});
            skLineSegment(sketch, "E1998", {"start": v(1.3, 0.03) * mm, "end": v(1.28, 0) * mm});
            skLineSegment(sketch, "E1999", {"start": v(1.28, 0) * mm, "end": v(1.26, -0.02) * mm});
            skLineSegment(sketch, "E2000", {"start": v(1.26, -0.02) * mm, "end": v(1.25, -0.03) * mm});
            skLineSegment(sketch, "E2001", {"start": v(1.25, -0.03) * mm, "end": v(1.25, -0.04) * mm});
            skLineSegment(sketch, "E2002", {"start": v(1.25, -0.04) * mm, "end": v(1.23, -0.07) * mm});
            skLineSegment(sketch, "E2003", {"start": v(1.23, -0.07) * mm, "end": v(1.2, -0.1) * mm});
            skLineSegment(sketch, "E2004", {"start": v(1.2, -0.1) * mm, "end": v(1.2, -0.12) * mm});
            skLineSegment(sketch, "E2005", {"start": v(1.2, -0.12) * mm, "end": v(1.2, -0.12) * mm});
            skLineSegment(sketch, "E2006", {"start": v(1.2, -0.12) * mm, "end": v(1.2, -0.13) * mm});
            skLineSegment(sketch, "E2007", {"start": v(1.2, -0.13) * mm, "end": v(1.2, -0.13) * mm});
            skLineSegment(sketch, "E2008", {"start": v(1.2, -0.13) * mm, "end": v(1.2, -0.12) * mm});
            skLineSegment(sketch, "E2009", {"start": v(1.2, -0.12) * mm, "end": v(1.23, -0.1) * mm});
            skLineSegment(sketch, "E2010", {"start": v(1.23, -0.1) * mm, "end": v(1.25, -0.07) * mm});
            skLineSegment(sketch, "E2011", {"start": v(1.25, -0.07) * mm, "end": v(1.28, -0.04) * mm});
            skLineSegment(sketch, "E2012", {"start": v(1.28, -0.04) * mm, "end": v(1.3, 0) * mm});
            skLineSegment(sketch, "E2013", {"start": v(1.3, 0) * mm, "end": v(1.32, 0.03) * mm});
            skLineSegment(sketch, "E2014", {"start": v(1.32, 0.03) * mm, "end": v(1.34, 0.05) * mm});
            skLineSegment(sketch, "E2015", {"start": v(1.34, 0.05) * mm, "end": v(1.34, 0.06) * mm});
            skLineSegment(sketch, "E2016", {"start": v(1.34, 0.06) * mm, "end": v(1.35, 0.07) * mm});
            skLineSegment(sketch, "E2017", {"start": v(1.35, 0.07) * mm, "end": v(1.36, 0.1) * mm});
            skLineSegment(sketch, "E2018", {"start": v(1.36, 0.1) * mm, "end": v(1.38, 0.12) * mm});
            skLineSegment(sketch, "E2019", {"start": v(1.38, 0.12) * mm, "end": v(1.4, 0.13) * mm});
            skLineSegment(sketch, "E2020", {"start": v(1.4, 0.13) * mm, "end": v(1.43, 0.13) * mm});
            skLineSegment(sketch, "E2021", {"start": v(1.43, 0.13) * mm, "end": v(1.44, 0.13) * mm});
            skLineSegment(sketch, "E2022", {"start": v(1.44, 0.13) * mm, "end": v(1.48, 0.13) * mm});
            skLineSegment(sketch, "E2023", {"start": v(1.48, 0.13) * mm, "end": v(1.6, 0.15) * mm});
            skLineSegment(sketch, "E2024", {"start": v(1.6, 0.15) * mm, "end": v(1.7, 0.19) * mm});
            skLineSegment(sketch, "E2025", {"start": v(1.7, 0.19) * mm, "end": v(1.72, 0.2) * mm});
            skLineSegment(sketch, "E2026", {"start": v(1.72, 0.2) * mm, "end": v(1.73, 0.2) * mm});
            skLineSegment(sketch, "E2027", {"start": v(1.73, 0.2) * mm, "end": v(1.76, 0.22) * mm});
            skLineSegment(sketch, "E2028", {"start": v(1.76, 0.22) * mm, "end": v(1.77, 0.24) * mm});
            skLineSegment(sketch, "E2029", {"start": v(1.77, 0.24) * mm, "end": v(1.75, 0.24) * mm});
            skLineSegment(sketch, "E2030", {"start": v(1.75, 0.24) * mm, "end": v(1.72, 0.22) * mm});
            skLineSegment(sketch, "E2031", {"start": v(1.72, 0.22) * mm, "end": v(1.71, 0.22) * mm});
            skLineSegment(sketch, "E2032", {"start": v(1.71, 0.22) * mm, "end": v(1.7, 0.2) * mm});
            skLineSegment(sketch, "E2033", {"start": v(1.7, 0.2) * mm, "end": v(1.64, 0.2) * mm});
            skLineSegment(sketch, "E2034", {"start": v(1.64, 0.2) * mm, "end": v(1.53, 0.17) * mm});
            skLineSegment(sketch, "E2035", {"start": v(1.53, 0.17) * mm, "end": v(1.42, 0.16) * mm});
            skLineSegment(sketch, "E2036", {"start": v(1.42, 0.16) * mm, "end": v(1.35, 0.16) * mm});
            skLineSegment(sketch, "E2037", {"start": v(1.35, 0.16) * mm, "end": v(1.34, 0.17) * mm});
            skLineSegment(sketch, "E2038", {"start": v(1.34, 0.17) * mm, "end": v(1.3, 0.18) * mm});
            skLineSegment(sketch, "E2039", {"start": v(1.3, 0.18) * mm, "end": v(1.35, 0.2) * mm});
            skLineSegment(sketch, "E2040", {"start": v(1.35, 0.2) * mm, "end": v(1.38, 0.21) * mm});
            skLineSegment(sketch, "E2041", {"start": v(1.38, 0.21) * mm, "end": v(1.44, 0.26) * mm});
            skLineSegment(sketch, "E2042", {"start": v(1.44, 0.26) * mm, "end": v(1.54, 0.34) * mm});
            skLineSegment(sketch, "E2043", {"start": v(1.54, 0.34) * mm, "end": v(1.62, 0.44) * mm});
            skLineSegment(sketch, "E2044", {"start": v(1.62, 0.44) * mm, "end": v(1.66, 0.52) * mm});
            skLineSegment(sketch, "E2045", {"start": v(1.66, 0.52) * mm, "end": v(1.67, 0.54) * mm});
            skLineSegment(sketch, "E2046", {"start": v(1.67, 0.54) * mm, "end": v(1.68, 0.55) * mm});
            skLineSegment(sketch, "E2047", {"start": v(1.68, 0.55) * mm, "end": v(1.69, 0.58) * mm});
            skLineSegment(sketch, "E2048", {"start": v(1.69, 0.58) * mm, "end": v(1.7, 0.59) * mm});
            skLineSegment(sketch, "E2049", {"start": v(1.7, 0.59) * mm, "end": v(1.72, 0.58) * mm});
            skLineSegment(sketch, "E2050", {"start": v(1.72, 0.58) * mm, "end": v(1.74, 0.55) * mm});
            skLineSegment(sketch, "E2051", {"start": v(1.74, 0.55) * mm, "end": v(1.75, 0.54) * mm});
            skLineSegment(sketch, "E2052", {"start": v(-1.47, 0.02) * mm, "end": v(-1.47, 0.02) * mm});
            skLineSegment(sketch, "E2053", {"start": v(-1.47, 0.02) * mm, "end": v(-1.47, 0.01) * mm});
            skLineSegment(sketch, "E2054", {"start": v(-1.47, 0.01) * mm, "end": v(-1.48, 0) * mm});
            skLineSegment(sketch, "E2055", {"start": v(-1.48, 0) * mm, "end": v(-1.49, 0) * mm});
            skLineSegment(sketch, "E2056", {"start": v(-1.49, 0) * mm, "end": v(-1.5, 0) * mm});
            skLineSegment(sketch, "E2057", {"start": v(-1.5, 0) * mm, "end": v(-1.53, -0.02) * mm});
            skLineSegment(sketch, "E2058", {"start": v(-1.53, -0.02) * mm, "end": v(-1.56, -0.06) * mm});
            skLineSegment(sketch, "E2059", {"start": v(-1.56, -0.06) * mm, "end": v(-1.58, -0.1) * mm});
            skLineSegment(sketch, "E2060", {"start": v(-1.58, -0.1) * mm, "end": v(-1.59, -0.14) * mm});
            skLineSegment(sketch, "E2061", {"start": v(-1.59, -0.14) * mm, "end": v(-1.59, -0.15) * mm});
            skLineSegment(sketch, "E2062", {"start": v(-1.59, -0.15) * mm, "end": v(-1.59, -0.16) * mm});
            skLineSegment(sketch, "E2063", {"start": v(-1.59, -0.16) * mm, "end": v(-1.59, -0.19) * mm});
            skLineSegment(sketch, "E2064", {"start": v(-1.59, -0.19) * mm, "end": v(-1.6, -0.2) * mm});
            skLineSegment(sketch, "E2065", {"start": v(-1.6, -0.2) * mm, "end": v(-1.6, -0.21) * mm});
            skLineSegment(sketch, "E2066", {"start": v(-1.6, -0.21) * mm, "end": v(-1.61, -0.21) * mm});
            skLineSegment(sketch, "E2067", {"start": v(-1.61, -0.21) * mm, "end": v(-1.62, -0.2) * mm});
            skLineSegment(sketch, "E2068", {"start": v(-1.62, -0.2) * mm, "end": v(-1.62, -0.2) * mm});
            skLineSegment(sketch, "E2069", {"start": v(-1.62, -0.2) * mm, "end": v(-1.64, -0.2) * mm});
            skLineSegment(sketch, "E2070", {"start": v(-1.64, -0.2) * mm, "end": v(-1.68, -0.19) * mm});
            skLineSegment(sketch, "E2071", {"start": v(-1.68, -0.19) * mm, "end": v(-1.71, -0.17) * mm});
            skLineSegment(sketch, "E2072", {"start": v(-1.71, -0.17) * mm, "end": v(-1.75, -0.16) * mm});
            skLineSegment(sketch, "E2073", {"start": v(-1.75, -0.16) * mm, "end": v(-1.78, -0.14) * mm});
            skLineSegment(sketch, "E2074", {"start": v(-1.78, -0.14) * mm, "end": v(-1.81, -0.12) * mm});
            skLineSegment(sketch, "E2075", {"start": v(-1.81, -0.12) * mm, "end": v(-1.83, -0.11) * mm});
            skLineSegment(sketch, "E2076", {"start": v(-1.83, -0.11) * mm, "end": v(-1.84, -0.1) * mm});
            skLineSegment(sketch, "E2077", {"start": v(-1.84, -0.1) * mm, "end": v(-1.84, -0.1) * mm});
            skLineSegment(sketch, "E2078", {"start": v(-1.84, -0.1) * mm, "end": v(-1.82, -0.08) * mm});
            skLineSegment(sketch, "E2079", {"start": v(-1.82, -0.08) * mm, "end": v(-1.78, -0.06) * mm});
            skLineSegment(sketch, "E2080", {"start": v(-1.78, -0.06) * mm, "end": v(-1.73, -0.03) * mm});
            skLineSegment(sketch, "E2081", {"start": v(-1.73, -0.03) * mm, "end": v(-1.66, 0) * mm});
            skLineSegment(sketch, "E2082", {"start": v(-1.66, 0) * mm, "end": v(-1.6, 0.01) * mm});
            skLineSegment(sketch, "E2083", {"start": v(-1.6, 0.01) * mm, "end": v(-1.54, 0.03) * mm});
            skLineSegment(sketch, "E2084", {"start": v(-1.54, 0.03) * mm, "end": v(-1.5, 0.03) * mm});
            skLineSegment(sketch, "E2085", {"start": v(-1.5, 0.03) * mm, "end": v(-1.47, 0.03) * mm});
            skLineSegment(sketch, "E2086", {"start": v(-1.47, 0.03) * mm, "end": v(-1.47, 0.02) * mm});
            skLineSegment(sketch, "E2087", {"start": v(1.72, -0.05) * mm, "end": v(1.72, -0.05) * mm});
            skLineSegment(sketch, "E2088", {"start": v(1.72, -0.05) * mm, "end": v(1.74, -0.06) * mm});
            skLineSegment(sketch, "E2089", {"start": v(1.74, -0.06) * mm, "end": v(1.77, -0.06) * mm});
            skLineSegment(sketch, "E2090", {"start": v(1.77, -0.06) * mm, "end": v(1.77, -0.07) * mm});
            skLineSegment(sketch, "E2091", {"start": v(1.77, -0.07) * mm, "end": v(1.78, -0.07) * mm});
            skLineSegment(sketch, "E2092", {"start": v(1.78, -0.07) * mm, "end": v(1.8, -0.07) * mm});
            skLineSegment(sketch, "E2093", {"start": v(1.8, -0.07) * mm, "end": v(1.82, -0.08) * mm});
            skLineSegment(sketch, "E2094", {"start": v(1.82, -0.08) * mm, "end": v(1.84, -0.1) * mm});
            skLineSegment(sketch, "E2095", {"start": v(1.84, -0.1) * mm, "end": v(1.84, -0.1) * mm});
            skLineSegment(sketch, "E2096", {"start": v(1.84, -0.1) * mm, "end": v(1.85, -0.13) * mm});
            skLineSegment(sketch, "E2097", {"start": v(1.85, -0.13) * mm, "end": v(1.84, -0.17) * mm});
            skLineSegment(sketch, "E2098", {"start": v(1.84, -0.17) * mm, "end": v(1.83, -0.21) * mm});
            skLineSegment(sketch, "E2099", {"start": v(1.83, -0.21) * mm, "end": v(1.82, -0.26) * mm});
            skLineSegment(sketch, "E2100", {"start": v(1.82, -0.26) * mm, "end": v(1.82, -0.28) * mm});
            skLineSegment(sketch, "E2101", {"start": v(1.82, -0.28) * mm, "end": v(1.81, -0.3) * mm});
            skLineSegment(sketch, "E2102", {"start": v(1.81, -0.3) * mm, "end": v(1.8, -0.34) * mm});
            skLineSegment(sketch, "E2103", {"start": v(1.8, -0.34) * mm, "end": v(1.79, -0.39) * mm});
            skLineSegment(sketch, "E2104", {"start": v(1.79, -0.39) * mm, "end": v(1.78, -0.42) * mm});
            skLineSegment(sketch, "E2105", {"start": v(1.78, -0.42) * mm, "end": v(1.76, -0.44) * mm});
            skLineSegment(sketch, "E2106", {"start": v(1.76, -0.44) * mm, "end": v(1.75, -0.45) * mm});
            skLineSegment(sketch, "E2107", {"start": v(1.75, -0.45) * mm, "end": v(1.74, -0.45) * mm});
            skLineSegment(sketch, "E2108", {"start": v(1.74, -0.45) * mm, "end": v(1.72, -0.44) * mm});
            skLineSegment(sketch, "E2109", {"start": v(1.72, -0.44) * mm, "end": v(1.7, -0.43) * mm});
            skLineSegment(sketch, "E2110", {"start": v(1.7, -0.43) * mm, "end": v(1.7, -0.43) * mm});
            skLineSegment(sketch, "E2111", {"start": v(1.7, -0.43) * mm, "end": v(1.68, -0.42) * mm});
            skLineSegment(sketch, "E2112", {"start": v(1.68, -0.42) * mm, "end": v(1.66, -0.4) * mm});
            skLineSegment(sketch, "E2113", {"start": v(1.66, -0.4) * mm, "end": v(1.65, -0.4) * mm});
            skLineSegment(sketch, "E2114", {"start": v(1.65, -0.4) * mm, "end": v(1.64, -0.4) * mm});
            skLineSegment(sketch, "E2115", {"start": v(1.64, -0.4) * mm, "end": v(1.64, -0.4) * mm});
            skLineSegment(sketch, "E2116", {"start": v(1.64, -0.4) * mm, "end": v(1.63, -0.4) * mm});
            skLineSegment(sketch, "E2117", {"start": v(1.63, -0.4) * mm, "end": v(1.6, -0.38) * mm});
            skLineSegment(sketch, "E2118", {"start": v(1.6, -0.38) * mm, "end": v(1.57, -0.36) * mm});
            skLineSegment(sketch, "E2119", {"start": v(1.57, -0.36) * mm, "end": v(1.54, -0.35) * mm});
            skLineSegment(sketch, "E2120", {"start": v(1.54, -0.35) * mm, "end": v(1.53, -0.35) * mm});
            skLineSegment(sketch, "E2121", {"start": v(1.53, -0.35) * mm, "end": v(1.5, -0.34) * mm});
            skLineSegment(sketch, "E2122", {"start": v(1.5, -0.34) * mm, "end": v(1.45, -0.31) * mm});
            skLineSegment(sketch, "E2123", {"start": v(1.45, -0.31) * mm, "end": v(1.37, -0.28) * mm});
            skLineSegment(sketch, "E2124", {"start": v(1.37, -0.28) * mm, "end": v(1.3, -0.26) * mm});
            skLineSegment(sketch, "E2125", {"start": v(1.3, -0.26) * mm, "end": v(1.25, -0.25) * mm});
            skLineSegment(sketch, "E2126", {"start": v(1.25, -0.25) * mm, "end": v(1.24, -0.25) * mm});
            skLineSegment(sketch, "E2127", {"start": v(1.24, -0.25) * mm, "end": v(1.24, -0.25) * mm});
            skLineSegment(sketch, "E2128", {"start": v(1.24, -0.25) * mm, "end": v(1.21, -0.25) * mm});
            skLineSegment(sketch, "E2129", {"start": v(1.21, -0.25) * mm, "end": v(1.18, -0.24) * mm});
            skLineSegment(sketch, "E2130", {"start": v(1.18, -0.24) * mm, "end": v(1.18, -0.24) * mm});
            skLineSegment(sketch, "E2131", {"start": v(1.18, -0.24) * mm, "end": v(1.14, -0.24) * mm});
            skLineSegment(sketch, "E2132", {"start": v(1.14, -0.24) * mm, "end": v(1.18, -0.22) * mm});
            skLineSegment(sketch, "E2133", {"start": v(1.18, -0.22) * mm, "end": v(1.18, -0.22) * mm});
            skLineSegment(sketch, "E2134", {"start": v(1.18, -0.22) * mm, "end": v(1.21, -0.2) * mm});
            skLineSegment(sketch, "E2135", {"start": v(1.21, -0.2) * mm, "end": v(1.24, -0.19) * mm});
            skLineSegment(sketch, "E2136", {"start": v(1.24, -0.19) * mm, "end": v(1.24, -0.18) * mm});
            skLineSegment(sketch, "E2137", {"start": v(1.24, -0.18) * mm, "end": v(1.24, -0.18) * mm});
            skLineSegment(sketch, "E2138", {"start": v(1.24, -0.18) * mm, "end": v(1.27, -0.17) * mm});
            skLineSegment(sketch, "E2139", {"start": v(1.27, -0.17) * mm, "end": v(1.3, -0.17) * mm});
            skLineSegment(sketch, "E2140", {"start": v(1.3, -0.17) * mm, "end": v(1.3, -0.17) * mm});
            skLineSegment(sketch, "E2141", {"start": v(1.3, -0.17) * mm, "end": v(1.33, -0.17) * mm});
            skLineSegment(sketch, "E2142", {"start": v(1.33, -0.17) * mm, "end": v(1.37, -0.15) * mm});
            skLineSegment(sketch, "E2143", {"start": v(1.37, -0.15) * mm, "end": v(1.38, -0.14) * mm});
            skLineSegment(sketch, "E2144", {"start": v(1.38, -0.14) * mm, "end": v(1.38, -0.14) * mm});
            skLineSegment(sketch, "E2145", {"start": v(1.38, -0.14) * mm, "end": v(1.4, -0.12) * mm});
            skLineSegment(sketch, "E2146", {"start": v(1.4, -0.12) * mm, "end": v(1.43, -0.1) * mm});
            skLineSegment(sketch, "E2147", {"start": v(1.43, -0.1) * mm, "end": v(1.47, -0.1) * mm});
            skLineSegment(sketch, "E2148", {"start": v(1.47, -0.1) * mm, "end": v(1.49, -0.09) * mm});
            skLineSegment(sketch, "E2149", {"start": v(1.49, -0.09) * mm, "end": v(1.5, -0.08) * mm});
            skLineSegment(sketch, "E2150", {"start": v(1.5, -0.08) * mm, "end": v(1.5, -0.08) * mm});
            skLineSegment(sketch, "E2151", {"start": v(1.5, -0.08) * mm, "end": v(1.53, -0.07) * mm});
            skLineSegment(sketch, "E2152", {"start": v(1.53, -0.07) * mm, "end": v(1.56, -0.06) * mm});
            skLineSegment(sketch, "E2153", {"start": v(1.56, -0.06) * mm, "end": v(1.58, -0.05) * mm});
            skLineSegment(sketch, "E2154", {"start": v(1.58, -0.05) * mm, "end": v(1.6, -0.05) * mm});
            skLineSegment(sketch, "E2155", {"start": v(1.6, -0.05) * mm, "end": v(1.6, -0.05) * mm});
            skLineSegment(sketch, "E2156", {"start": v(1.6, -0.05) * mm, "end": v(1.6, -0.04) * mm});
            skLineSegment(sketch, "E2157", {"start": v(1.6, -0.04) * mm, "end": v(1.62, -0.04) * mm});
            skLineSegment(sketch, "E2158", {"start": v(1.62, -0.04) * mm, "end": v(1.67, -0.03) * mm});
            skLineSegment(sketch, "E2159", {"start": v(1.67, -0.03) * mm, "end": v(1.7, -0.04) * mm});
            skLineSegment(sketch, "E2160", {"start": v(1.7, -0.04) * mm, "end": v(1.72, -0.04) * mm});
            skLineSegment(sketch, "E2161", {"start": v(1.72, -0.04) * mm, "end": v(1.72, -0.05) * mm});
            skLineSegment(sketch, "E2162", {"start": v(-1.75, -0.19) * mm, "end": v(-1.74, -0.2) * mm});
            skLineSegment(sketch, "E2163", {"start": v(-1.74, -0.2) * mm, "end": v(-1.72, -0.2) * mm});
            skLineSegment(sketch, "E2164", {"start": v(-1.72, -0.2) * mm, "end": v(-1.69, -0.22) * mm});
            skLineSegment(sketch, "E2165", {"start": v(-1.69, -0.22) * mm, "end": v(-1.66, -0.22) * mm});
            skLineSegment(sketch, "E2166", {"start": v(-1.66, -0.22) * mm, "end": v(-1.65, -0.23) * mm});
            skLineSegment(sketch, "E2167", {"start": v(-1.65, -0.23) * mm, "end": v(-1.64, -0.23) * mm});
            skLineSegment(sketch, "E2168", {"start": v(-1.64, -0.23) * mm, "end": v(-1.64, -0.23) * mm});
            skLineSegment(sketch, "E2169", {"start": v(-1.64, -0.23) * mm, "end": v(-1.62, -0.23) * mm});
            skLineSegment(sketch, "E2170", {"start": v(-1.62, -0.23) * mm, "end": v(-1.62, -0.25) * mm});
            skLineSegment(sketch, "E2171", {"start": v(-1.62, -0.25) * mm, "end": v(-1.62, -0.25) * mm});
            skLineSegment(sketch, "E2172", {"start": v(-1.62, -0.25) * mm, "end": v(-1.63, -0.27) * mm});
            skLineSegment(sketch, "E2173", {"start": v(-1.63, -0.27) * mm, "end": v(-1.65, -0.33) * mm});
            skLineSegment(sketch, "E2174", {"start": v(-1.65, -0.33) * mm, "end": v(-1.66, -0.4) * mm});
            skLineSegment(sketch, "E2175", {"start": v(-1.66, -0.4) * mm, "end": v(-1.67, -0.47) * mm});
            skLineSegment(sketch, "E2176", {"start": v(-1.67, -0.47) * mm, "end": v(-1.67, -0.53) * mm});
            skLineSegment(sketch, "E2177", {"start": v(-1.67, -0.53) * mm, "end": v(-1.66, -0.55) * mm});
            skLineSegment(sketch, "E2178", {"start": v(-1.66, -0.55) * mm, "end": v(-1.66, -0.57) * mm});
            skLineSegment(sketch, "E2179", {"start": v(-1.66, -0.57) * mm, "end": v(-1.66, -0.6) * mm});
            skLineSegment(sketch, "E2180", {"start": v(-1.66, -0.6) * mm, "end": v(-1.66, -0.64) * mm});
            skLineSegment(sketch, "E2181", {"start": v(-1.66, -0.64) * mm, "end": v(-1.66, -0.67) * mm});
            skLineSegment(sketch, "E2182", {"start": v(-1.66, -0.67) * mm, "end": v(-1.67, -0.67) * mm});
            skLineSegment(sketch, "E2183", {"start": v(-1.67, -0.67) * mm, "end": v(-1.68, -0.66) * mm});
            skLineSegment(sketch, "E2184", {"start": v(-1.68, -0.66) * mm, "end": v(-1.7, -0.64) * mm});
            skLineSegment(sketch, "E2185", {"start": v(-1.7, -0.64) * mm, "end": v(-1.72, -0.6) * mm});
            skLineSegment(sketch, "E2186", {"start": v(-1.72, -0.6) * mm, "end": v(-1.74, -0.55) * mm});
            skLineSegment(sketch, "E2187", {"start": v(-1.74, -0.55) * mm, "end": v(-1.75, -0.54) * mm});
            skLineSegment(sketch, "E2188", {"start": v(-1.75, -0.54) * mm, "end": v(-1.75, -0.53) * mm});
            skLineSegment(sketch, "E2189", {"start": v(-1.75, -0.53) * mm, "end": v(-1.77, -0.49) * mm});
            skLineSegment(sketch, "E2190", {"start": v(-1.77, -0.49) * mm, "end": v(-1.79, -0.43) * mm});
            skLineSegment(sketch, "E2191", {"start": v(-1.79, -0.43) * mm, "end": v(-1.8, -0.37) * mm});
            skLineSegment(sketch, "E2192", {"start": v(-1.8, -0.37) * mm, "end": v(-1.82, -0.3) * mm});
            skLineSegment(sketch, "E2193", {"start": v(-1.82, -0.3) * mm, "end": v(-1.84, -0.24) * mm});
            skLineSegment(sketch, "E2194", {"start": v(-1.84, -0.24) * mm, "end": v(-1.85, -0.2) * mm});
            skLineSegment(sketch, "E2195", {"start": v(-1.85, -0.2) * mm, "end": v(-1.85, -0.16) * mm});
            skLineSegment(sketch, "E2196", {"start": v(-1.85, -0.16) * mm, "end": v(-1.84, -0.14) * mm});
            skLineSegment(sketch, "E2197", {"start": v(-1.84, -0.14) * mm, "end": v(-1.84, -0.14) * mm});
            skLineSegment(sketch, "E2198", {"start": v(-1.84, -0.14) * mm, "end": v(-1.83, -0.15) * mm});
            skLineSegment(sketch, "E2199", {"start": v(-1.83, -0.15) * mm, "end": v(-1.81, -0.16) * mm});
            skLineSegment(sketch, "E2200", {"start": v(-1.81, -0.16) * mm, "end": v(-1.79, -0.17) * mm});
            skLineSegment(sketch, "E2201", {"start": v(-1.79, -0.17) * mm, "end": v(-1.76, -0.18) * mm});
            skLineSegment(sketch, "E2202", {"start": v(-1.76, -0.18) * mm, "end": v(-1.75, -0.19) * mm});
            skLineSegment(sketch, "E2203", {"start": v(-1.48, -0.42) * mm, "end": v(-1.43, -0.48) * mm});
            skLineSegment(sketch, "E2204", {"start": v(-1.43, -0.48) * mm, "end": v(-1.46, -0.55) * mm});
            skLineSegment(sketch, "E2205", {"start": v(-1.46, -0.55) * mm, "end": v(-1.46, -0.56) * mm});
            skLineSegment(sketch, "E2206", {"start": v(-1.46, -0.56) * mm, "end": v(-1.48, -0.6) * mm});
            skLineSegment(sketch, "E2207", {"start": v(-1.48, -0.6) * mm, "end": v(-1.5, -0.64) * mm});
            skLineSegment(sketch, "E2208", {"start": v(-1.5, -0.64) * mm, "end": v(-1.54, -0.68) * mm});
            skLineSegment(sketch, "E2209", {"start": v(-1.54, -0.68) * mm, "end": v(-1.58, -0.7) * mm});
            skLineSegment(sketch, "E2210", {"start": v(-1.58, -0.7) * mm, "end": v(-1.59, -0.7) * mm});
            skLineSegment(sketch, "E2211", {"start": v(-1.59, -0.7) * mm, "end": v(-1.63, -0.73) * mm});
            skLineSegment(sketch, "E2212", {"start": v(-1.63, -0.73) * mm, "end": v(-1.63, -0.62) * mm});
            skLineSegment(sketch, "E2213", {"start": v(-1.63, -0.62) * mm, "end": v(-1.63, -0.6) * mm});
            skLineSegment(sketch, "E2214", {"start": v(-1.63, -0.6) * mm, "end": v(-1.63, -0.58) * mm});
            skLineSegment(sketch, "E2215", {"start": v(-1.63, -0.58) * mm, "end": v(-1.63, -0.53) * mm});
            skLineSegment(sketch, "E2216", {"start": v(-1.63, -0.53) * mm, "end": v(-1.63, -0.5) * mm});
            skLineSegment(sketch, "E2217", {"start": v(-1.63, -0.5) * mm, "end": v(-1.63, -0.48) * mm});
            skLineSegment(sketch, "E2218", {"start": v(-1.63, -0.48) * mm, "end": v(-1.63, -0.47) * mm});
            skLineSegment(sketch, "E2219", {"start": v(-1.63, -0.47) * mm, "end": v(-1.64, -0.46) * mm});
            skLineSegment(sketch, "E2220", {"start": v(-1.64, -0.46) * mm, "end": v(-1.63, -0.43) * mm});
            skLineSegment(sketch, "E2221", {"start": v(-1.63, -0.43) * mm, "end": v(-1.63, -0.38) * mm});
            skLineSegment(sketch, "E2222", {"start": v(-1.63, -0.38) * mm, "end": v(-1.61, -0.33) * mm});
            skLineSegment(sketch, "E2223", {"start": v(-1.61, -0.33) * mm, "end": v(-1.6, -0.3) * mm});
            skLineSegment(sketch, "E2224", {"start": v(-1.6, -0.3) * mm, "end": v(-1.6, -0.28) * mm});
            skLineSegment(sketch, "E2225", {"start": v(-1.6, -0.28) * mm, "end": v(-1.58, -0.24) * mm});
            skLineSegment(sketch, "E2226", {"start": v(-1.58, -0.24) * mm, "end": v(-1.56, -0.3) * mm});
            skLineSegment(sketch, "E2227", {"start": v(-1.56, -0.3) * mm, "end": v(-1.55, -0.31) * mm});
            skLineSegment(sketch, "E2228", {"start": v(-1.55, -0.31) * mm, "end": v(-1.54, -0.34) * mm});
            skLineSegment(sketch, "E2229", {"start": v(-1.54, -0.34) * mm, "end": v(-1.52, -0.37) * mm});
            skLineSegment(sketch, "E2230", {"start": v(-1.52, -0.37) * mm, "end": v(-1.5, -0.4) * mm});
            skLineSegment(sketch, "E2231", {"start": v(-1.5, -0.4) * mm, "end": v(-1.49, -0.42) * mm});
            skLineSegment(sketch, "E2232", {"start": v(-1.49, -0.42) * mm, "end": v(-1.48, -0.42) * mm});
            skLineSegment(sketch, "E2233", {"start": v(1.12, -0.36) * mm, "end": v(1.13, -0.38) * mm});
            skLineSegment(sketch, "E2234", {"start": v(1.13, -0.38) * mm, "end": v(1.18, -0.46) * mm});
            skLineSegment(sketch, "E2235", {"start": v(1.18, -0.46) * mm, "end": v(1.23, -0.58) * mm});
            skLineSegment(sketch, "E2236", {"start": v(1.23, -0.58) * mm, "end": v(1.27, -0.7) * mm});
            skLineSegment(sketch, "E2237", {"start": v(1.27, -0.7) * mm, "end": v(1.3, -0.8) * mm});
            skLineSegment(sketch, "E2238", {"start": v(1.3, -0.8) * mm, "end": v(1.3, -0.84) * mm});
            skLineSegment(sketch, "E2239", {"start": v(1.3, -0.84) * mm, "end": v(1.3, -0.85) * mm});
            skLineSegment(sketch, "E2240", {"start": v(1.3, -0.85) * mm, "end": v(1.3, -0.89) * mm});
            skLineSegment(sketch, "E2241", {"start": v(1.3, -0.89) * mm, "end": v(1.3, -0.93) * mm});
            skLineSegment(sketch, "E2242", {"start": v(1.3, -0.93) * mm, "end": v(1.3, -0.96) * mm});
            skLineSegment(sketch, "E2243", {"start": v(1.3, -0.96) * mm, "end": v(1.3, -0.98) * mm});
            skLineSegment(sketch, "E2244", {"start": v(1.3, -0.98) * mm, "end": v(1.28, -1) * mm});
            skLineSegment(sketch, "E2245", {"start": v(1.28, -1) * mm, "end": v(1.26, -1.02) * mm});
            skLineSegment(sketch, "E2246", {"start": v(1.26, -1.02) * mm, "end": v(1.23, -1.04) * mm});
            skLineSegment(sketch, "E2247", {"start": v(1.23, -1.04) * mm, "end": v(1.21, -1.05) * mm});
            skLineSegment(sketch, "E2248", {"start": v(1.21, -1.05) * mm, "end": v(1.2, -1.05) * mm});
            skLineSegment(sketch, "E2249", {"start": v(1.2, -1.05) * mm, "end": v(1.2, -1.06) * mm});
            skLineSegment(sketch, "E2250", {"start": v(1.2, -1.06) * mm, "end": v(1.17, -1.07) * mm});
            skLineSegment(sketch, "E2251", {"start": v(1.17, -1.07) * mm, "end": v(1.14, -1.07) * mm});
            skLineSegment(sketch, "E2252", {"start": v(1.14, -1.07) * mm, "end": v(1.13, -1.08) * mm});
            skLineSegment(sketch, "E2253", {"start": v(1.13, -1.08) * mm, "end": v(1.12, -1.08) * mm});
            skLineSegment(sketch, "E2254", {"start": v(1.12, -1.08) * mm, "end": v(1.1, -1.07) * mm});
            skLineSegment(sketch, "E2255", {"start": v(1.1, -1.07) * mm, "end": v(1.1, -1.06) * mm});
            skLineSegment(sketch, "E2256", {"start": v(1.1, -1.06) * mm, "end": v(1.1, -1.04) * mm});
            skLineSegment(sketch, "E2257", {"start": v(1.1, -1.04) * mm, "end": v(1.1, -1.02) * mm});
            skLineSegment(sketch, "E2258", {"start": v(1.1, -1.02) * mm, "end": v(1.1, -1.02) * mm});
            skLineSegment(sketch, "E2259", {"start": v(1.1, -1.02) * mm, "end": v(1.1, -0.96) * mm});
            skLineSegment(sketch, "E2260", {"start": v(1.1, -0.96) * mm, "end": v(1.1, -0.78) * mm});
            skLineSegment(sketch, "E2261", {"start": v(1.1, -0.78) * mm, "end": v(1.1, -0.59) * mm});
            skLineSegment(sketch, "E2262", {"start": v(1.1, -0.59) * mm, "end": v(1.07, -0.44) * mm});
            skLineSegment(sketch, "E2263", {"start": v(1.07, -0.44) * mm, "end": v(1.04, -0.35) * mm});
            skLineSegment(sketch, "E2264", {"start": v(1.04, -0.35) * mm, "end": v(1.03, -0.33) * mm});
            skLineSegment(sketch, "E2265", {"start": v(1.03, -0.33) * mm, "end": v(1.03, -0.32) * mm});
            skLineSegment(sketch, "E2266", {"start": v(1.03, -0.32) * mm, "end": v(1.02, -0.31) * mm});
            skLineSegment(sketch, "E2267", {"start": v(1.02, -0.31) * mm, "end": v(1.02, -0.3) * mm});
            skLineSegment(sketch, "E2268", {"start": v(1.02, -0.3) * mm, "end": v(1.01, -0.3) * mm});
            skLineSegment(sketch, "E2269", {"start": v(1.01, -0.3) * mm, "end": v(1.01, -0.3) * mm});
            skLineSegment(sketch, "E2270", {"start": v(1.01, -0.3) * mm, "end": v(1.02, -0.32) * mm});
            skLineSegment(sketch, "E2271", {"start": v(1.02, -0.32) * mm, "end": v(1.02, -0.35) * mm});
            skLineSegment(sketch, "E2272", {"start": v(1.02, -0.35) * mm, "end": v(1.03, -0.38) * mm});
            skLineSegment(sketch, "E2273", {"start": v(1.03, -0.38) * mm, "end": v(1.04, -0.41) * mm});
            skLineSegment(sketch, "E2274", {"start": v(1.04, -0.41) * mm, "end": v(1.04, -0.42) * mm});
            skLineSegment(sketch, "E2275", {"start": v(1.04, -0.42) * mm, "end": v(1.04, -0.45) * mm});
            skLineSegment(sketch, "E2276", {"start": v(1.04, -0.45) * mm, "end": v(1.06, -0.51) * mm});
            skLineSegment(sketch, "E2277", {"start": v(1.06, -0.51) * mm, "end": v(1.07, -0.6) * mm});
            skLineSegment(sketch, "E2278", {"start": v(1.07, -0.6) * mm, "end": v(1.08, -0.7) * mm});
            skLineSegment(sketch, "E2279", {"start": v(1.08, -0.7) * mm, "end": v(1.09, -0.78) * mm});
            skLineSegment(sketch, "E2280", {"start": v(1.09, -0.78) * mm, "end": v(1.1, -0.85) * mm});
            skLineSegment(sketch, "E2281", {"start": v(1.1, -0.85) * mm, "end": v(1.09, -0.91) * mm});
            skLineSegment(sketch, "E2282", {"start": v(1.09, -0.91) * mm, "end": v(1.08, -0.95) * mm});
            skLineSegment(sketch, "E2283", {"start": v(1.08, -0.95) * mm, "end": v(1.07, -0.96) * mm});
            skLineSegment(sketch, "E2284", {"start": v(1.07, -0.96) * mm, "end": v(1.07, -0.96) * mm});
            skLineSegment(sketch, "E2285", {"start": v(1.07, -0.96) * mm, "end": v(1.06, -0.96) * mm});
            skLineSegment(sketch, "E2286", {"start": v(1.06, -0.96) * mm, "end": v(1.05, -0.94) * mm});
            skLineSegment(sketch, "E2287", {"start": v(1.05, -0.94) * mm, "end": v(1.03, -0.92) * mm});
            skLineSegment(sketch, "E2288", {"start": v(1.03, -0.92) * mm, "end": v(1.02, -0.9) * mm});
            skLineSegment(sketch, "E2289", {"start": v(1.02, -0.9) * mm, "end": v(1.01, -0.89) * mm});
            skLineSegment(sketch, "E2290", {"start": v(1.01, -0.89) * mm, "end": v(1, -0.87) * mm});
            skLineSegment(sketch, "E2291", {"start": v(1, -0.87) * mm, "end": v(0.9, -0.77) * mm});
            skLineSegment(sketch, "E2292", {"start": v(0.9, -0.77) * mm, "end": v(0.8, -0.69) * mm});
            skLineSegment(sketch, "E2293", {"start": v(0.8, -0.69) * mm, "end": v(0.78, -0.67) * mm});
            skLineSegment(sketch, "E2294", {"start": v(0.78, -0.67) * mm, "end": v(0.72, -0.64) * mm});
            skLineSegment(sketch, "E2295", {"start": v(0.72, -0.64) * mm, "end": v(0.83, -0.53) * mm});
            skLineSegment(sketch, "E2296", {"start": v(0.83, -0.53) * mm, "end": v(0.85, -0.52) * mm});
            skLineSegment(sketch, "E2297", {"start": v(0.85, -0.52) * mm, "end": v(0.88, -0.48) * mm});
            skLineSegment(sketch, "E2298", {"start": v(0.88, -0.48) * mm, "end": v(0.92, -0.43) * mm});
            skLineSegment(sketch, "E2299", {"start": v(0.92, -0.43) * mm, "end": v(0.96, -0.38) * mm});
            skLineSegment(sketch, "E2300", {"start": v(0.96, -0.38) * mm, "end": v(0.97, -0.35) * mm});
            skLineSegment(sketch, "E2301", {"start": v(0.97, -0.35) * mm, "end": v(0.98, -0.34) * mm});
            skLineSegment(sketch, "E2302", {"start": v(0.98, -0.34) * mm, "end": v(0.98, -0.33) * mm});
            skLineSegment(sketch, "E2303", {"start": v(0.98, -0.33) * mm, "end": v(1, -0.31) * mm});
            skLineSegment(sketch, "E2304", {"start": v(1, -0.31) * mm, "end": v(1, -0.3) * mm});
            skLineSegment(sketch, "E2305", {"start": v(1, -0.3) * mm, "end": v(1.02, -0.28) * mm});
            skLineSegment(sketch, "E2306", {"start": v(1.02, -0.28) * mm, "end": v(1.03, -0.27) * mm});
            skLineSegment(sketch, "E2307", {"start": v(1.03, -0.27) * mm, "end": v(1.05, -0.28) * mm});
            skLineSegment(sketch, "E2308", {"start": v(1.05, -0.28) * mm, "end": v(1.07, -0.3) * mm});
            skLineSegment(sketch, "E2309", {"start": v(1.07, -0.3) * mm, "end": v(1.09, -0.32) * mm});
            skLineSegment(sketch, "E2310", {"start": v(1.09, -0.32) * mm, "end": v(1.1, -0.35) * mm});
            skLineSegment(sketch, "E2311", {"start": v(1.1, -0.35) * mm, "end": v(1.12, -0.36) * mm});
            skLineSegment(sketch, "E2312", {"start": v(1.18, -0.34) * mm, "end": v(1.2, -0.35) * mm});
            skLineSegment(sketch, "E2313", {"start": v(1.2, -0.35) * mm, "end": v(1.24, -0.4) * mm});
            skLineSegment(sketch, "E2314", {"start": v(1.24, -0.4) * mm, "end": v(1.3, -0.44) * mm});
            skLineSegment(sketch, "E2315", {"start": v(1.3, -0.44) * mm, "end": v(1.36, -0.5) * mm});
            skLineSegment(sketch, "E2316", {"start": v(1.36, -0.5) * mm, "end": v(1.4, -0.55) * mm});
            skLineSegment(sketch, "E2317", {"start": v(1.4, -0.55) * mm, "end": v(1.45, -0.6) * mm});
            skLineSegment(sketch, "E2318", {"start": v(1.45, -0.6) * mm, "end": v(1.48, -0.64) * mm});
            skLineSegment(sketch, "E2319", {"start": v(1.48, -0.64) * mm, "end": v(1.5, -0.68) * mm});
            skLineSegment(sketch, "E2320", {"start": v(1.5, -0.68) * mm, "end": v(1.51, -0.7) * mm});
            skLineSegment(sketch, "E2321", {"start": v(1.51, -0.7) * mm, "end": v(1.51, -0.7) * mm});
            skLineSegment(sketch, "E2322", {"start": v(1.51, -0.7) * mm, "end": v(1.51, -0.71) * mm});
            skLineSegment(sketch, "E2323", {"start": v(1.51, -0.71) * mm, "end": v(1.52, -0.71) * mm});
            skLineSegment(sketch, "E2324", {"start": v(1.52, -0.71) * mm, "end": v(1.52, -0.71) * mm});
            skLineSegment(sketch, "E2325", {"start": v(1.52, -0.71) * mm, "end": v(1.53, -0.71) * mm});
            skLineSegment(sketch, "E2326", {"start": v(1.53, -0.71) * mm, "end": v(1.53, -0.72) * mm});
            skLineSegment(sketch, "E2327", {"start": v(1.53, -0.72) * mm, "end": v(1.54, -0.73) * mm});
            skLineSegment(sketch, "E2328", {"start": v(1.54, -0.73) * mm, "end": v(1.54, -0.73) * mm});
            skLineSegment(sketch, "E2329", {"start": v(1.54, -0.73) * mm, "end": v(1.54, -0.74) * mm});
            skLineSegment(sketch, "E2330", {"start": v(1.54, -0.74) * mm, "end": v(1.54, -0.75) * mm});
            skLineSegment(sketch, "E2331", {"start": v(1.54, -0.75) * mm, "end": v(1.55, -0.76) * mm});
            skLineSegment(sketch, "E2332", {"start": v(1.55, -0.76) * mm, "end": v(1.56, -0.76) * mm});
            skLineSegment(sketch, "E2333", {"start": v(1.56, -0.76) * mm, "end": v(1.56, -0.76) * mm});
            skLineSegment(sketch, "E2334", {"start": v(1.56, -0.76) * mm, "end": v(1.55, -0.77) * mm});
            skLineSegment(sketch, "E2335", {"start": v(1.55, -0.77) * mm, "end": v(1.53, -0.8) * mm});
            skLineSegment(sketch, "E2336", {"start": v(1.53, -0.8) * mm, "end": v(1.5, -0.84) * mm});
            skLineSegment(sketch, "E2337", {"start": v(1.5, -0.84) * mm, "end": v(1.46, -0.88) * mm});
            skLineSegment(sketch, "E2338", {"start": v(1.46, -0.88) * mm, "end": v(1.42, -0.92) * mm});
            skLineSegment(sketch, "E2339", {"start": v(1.42, -0.92) * mm, "end": v(1.38, -0.96) * mm});
            skLineSegment(sketch, "E2340", {"start": v(1.38, -0.96) * mm, "end": v(1.35, -0.98) * mm});
            skLineSegment(sketch, "E2341", {"start": v(1.35, -0.98) * mm, "end": v(1.34, -1) * mm});
            skLineSegment(sketch, "E2342", {"start": v(1.34, -1) * mm, "end": v(1.34, -1) * mm});
            skLineSegment(sketch, "E2343", {"start": v(1.34, -1) * mm, "end": v(1.33, -0.98) * mm});
            skLineSegment(sketch, "E2344", {"start": v(1.33, -0.98) * mm, "end": v(1.33, -0.95) * mm});
            skLineSegment(sketch, "E2345", {"start": v(1.33, -0.95) * mm, "end": v(1.32, -0.91) * mm});
            skLineSegment(sketch, "E2346", {"start": v(1.32, -0.91) * mm, "end": v(1.32, -0.88) * mm});
            skLineSegment(sketch, "E2347", {"start": v(1.32, -0.88) * mm, "end": v(1.32, -0.86) * mm});
            skLineSegment(sketch, "E2348", {"start": v(1.32, -0.86) * mm, "end": v(1.32, -0.83) * mm});
            skLineSegment(sketch, "E2349", {"start": v(1.32, -0.83) * mm, "end": v(1.3, -0.73) * mm});
            skLineSegment(sketch, "E2350", {"start": v(1.3, -0.73) * mm, "end": v(1.28, -0.6) * mm});
            skLineSegment(sketch, "E2351", {"start": v(1.28, -0.6) * mm, "end": v(1.22, -0.48) * mm});
            skLineSegment(sketch, "E2352", {"start": v(1.22, -0.48) * mm, "end": v(1.17, -0.4) * mm});
            skLineSegment(sketch, "E2353", {"start": v(1.17, -0.4) * mm, "end": v(1.15, -0.37) * mm});
            skLineSegment(sketch, "E2354", {"start": v(1.15, -0.37) * mm, "end": v(1.15, -0.36) * mm});
            skLineSegment(sketch, "E2355", {"start": v(1.15, -0.36) * mm, "end": v(1.13, -0.34) * mm});
            skLineSegment(sketch, "E2356", {"start": v(1.13, -0.34) * mm, "end": v(1.12, -0.32) * mm});
            skLineSegment(sketch, "E2357", {"start": v(1.12, -0.32) * mm, "end": v(1.1, -0.3) * mm});
            skLineSegment(sketch, "E2358", {"start": v(1.1, -0.3) * mm, "end": v(1.11, -0.3) * mm});
            skLineSegment(sketch, "E2359", {"start": v(1.11, -0.3) * mm, "end": v(1.12, -0.3) * mm});
            skLineSegment(sketch, "E2360", {"start": v(1.12, -0.3) * mm, "end": v(1.13, -0.3) * mm});
            skLineSegment(sketch, "E2361", {"start": v(1.13, -0.3) * mm, "end": v(1.15, -0.32) * mm});
            skLineSegment(sketch, "E2362", {"start": v(1.15, -0.32) * mm, "end": v(1.18, -0.34) * mm});
            skLineSegment(sketch, "E2363", {"start": v(1.18, -0.34) * mm, "end": v(1.18, -0.34) * mm});
            skLineSegment(sketch, "E2364", {"start": v(1.39, -0.37) * mm, "end": v(1.39, -0.37) * mm});
            skLineSegment(sketch, "E2365", {"start": v(1.39, -0.37) * mm, "end": v(1.39, -0.38) * mm});
            skLineSegment(sketch, "E2366", {"start": v(1.39, -0.38) * mm, "end": v(1.4, -0.37) * mm});
            skLineSegment(sketch, "E2367", {"start": v(1.4, -0.37) * mm, "end": v(1.4, -0.37) * mm});
            skLineSegment(sketch, "E2368", {"start": v(1.4, -0.37) * mm, "end": v(1.41, -0.38) * mm});
            skLineSegment(sketch, "E2369", {"start": v(1.41, -0.38) * mm, "end": v(1.41, -0.38) * mm});
            skLineSegment(sketch, "E2370", {"start": v(1.41, -0.38) * mm, "end": v(1.42, -0.4) * mm});
            skLineSegment(sketch, "E2371", {"start": v(1.42, -0.4) * mm, "end": v(1.43, -0.39) * mm});
            skLineSegment(sketch, "E2372", {"start": v(1.43, -0.39) * mm, "end": v(1.43, -0.38) * mm});
            skLineSegment(sketch, "E2373", {"start": v(1.43, -0.38) * mm, "end": v(1.43, -0.38) * mm});
            skLineSegment(sketch, "E2374", {"start": v(1.43, -0.38) * mm, "end": v(1.44, -0.38) * mm});
            skLineSegment(sketch, "E2375", {"start": v(1.44, -0.38) * mm, "end": v(1.45, -0.38) * mm});
            skLineSegment(sketch, "E2376", {"start": v(1.45, -0.38) * mm, "end": v(1.45, -0.4) * mm});
            skLineSegment(sketch, "E2377", {"start": v(1.45, -0.4) * mm, "end": v(1.45, -0.42) * mm});
            skLineSegment(sketch, "E2378", {"start": v(1.45, -0.42) * mm, "end": v(1.45, -0.43) * mm});
            skLineSegment(sketch, "E2379", {"start": v(1.45, -0.43) * mm, "end": v(1.45, -0.43) * mm});
            skLineSegment(sketch, "E2380", {"start": v(1.45, -0.43) * mm, "end": v(1.45, -0.45) * mm});
            skLineSegment(sketch, "E2381", {"start": v(1.45, -0.45) * mm, "end": v(1.45, -0.47) * mm});
            skLineSegment(sketch, "E2382", {"start": v(1.45, -0.47) * mm, "end": v(1.45, -0.47) * mm});
            skLineSegment(sketch, "E2383", {"start": v(1.45, -0.47) * mm, "end": v(1.44, -0.46) * mm});
            skLineSegment(sketch, "E2384", {"start": v(1.44, -0.46) * mm, "end": v(1.44, -0.46) * mm});
            skLineSegment(sketch, "E2385", {"start": v(1.44, -0.46) * mm, "end": v(1.44, -0.45) * mm});
            skLineSegment(sketch, "E2386", {"start": v(1.44, -0.45) * mm, "end": v(1.42, -0.42) * mm});
            skLineSegment(sketch, "E2387", {"start": v(1.42, -0.42) * mm, "end": v(1.4, -0.4) * mm});
            skLineSegment(sketch, "E2388", {"start": v(1.4, -0.4) * mm, "end": v(1.38, -0.39) * mm});
            skLineSegment(sketch, "E2389", {"start": v(1.38, -0.39) * mm, "end": v(1.38, -0.39) * mm});
            skLineSegment(sketch, "E2390", {"start": v(1.38, -0.39) * mm, "end": v(1.36, -0.37) * mm});
            skLineSegment(sketch, "E2391", {"start": v(1.36, -0.37) * mm, "end": v(1.35, -0.36) * mm});
            skLineSegment(sketch, "E2392", {"start": v(1.35, -0.36) * mm, "end": v(1.35, -0.35) * mm});
            skLineSegment(sketch, "E2393", {"start": v(1.35, -0.35) * mm, "end": v(1.36, -0.35) * mm});
            skLineSegment(sketch, "E2394", {"start": v(1.36, -0.35) * mm, "end": v(1.36, -0.35) * mm});
            skLineSegment(sketch, "E2395", {"start": v(1.36, -0.35) * mm, "end": v(1.37, -0.35) * mm});
            skLineSegment(sketch, "E2396", {"start": v(1.37, -0.35) * mm, "end": v(1.38, -0.36) * mm});
            skLineSegment(sketch, "E2397", {"start": v(1.38, -0.36) * mm, "end": v(1.39, -0.36) * mm});
            skLineSegment(sketch, "E2398", {"start": v(1.39, -0.36) * mm, "end": v(1.39, -0.37) * mm});
            skLineSegment(sketch, "E2399", {"start": v(1.5, -0.4) * mm, "end": v(1.5, -0.4) * mm});
            skLineSegment(sketch, "E2400", {"start": v(1.5, -0.4) * mm, "end": v(1.52, -0.41) * mm});
            skLineSegment(sketch, "E2401", {"start": v(1.52, -0.41) * mm, "end": v(1.54, -0.43) * mm});
            skLineSegment(sketch, "E2402", {"start": v(1.54, -0.43) * mm, "end": v(1.55, -0.43) * mm});
            skLineSegment(sketch, "E2403", {"start": v(1.55, -0.43) * mm, "end": v(1.56, -0.43) * mm});
            skLineSegment(sketch, "E2404", {"start": v(1.56, -0.43) * mm, "end": v(1.58, -0.45) * mm});
            skLineSegment(sketch, "E2405", {"start": v(1.58, -0.45) * mm, "end": v(1.6, -0.46) * mm});
            skLineSegment(sketch, "E2406", {"start": v(1.6, -0.46) * mm, "end": v(1.6, -0.47) * mm});
            skLineSegment(sketch, "E2407", {"start": v(1.6, -0.47) * mm, "end": v(1.58, -0.47) * mm});
            skLineSegment(sketch, "E2408", {"start": v(1.58, -0.47) * mm, "end": v(1.57, -0.47) * mm});
            skLineSegment(sketch, "E2409", {"start": v(1.57, -0.47) * mm, "end": v(1.57, -0.47) * mm});
            skLineSegment(sketch, "E2410", {"start": v(1.57, -0.47) * mm, "end": v(1.56, -0.47) * mm});
            skLineSegment(sketch, "E2411", {"start": v(1.56, -0.47) * mm, "end": v(1.56, -0.47) * mm});
            skLineSegment(sketch, "E2412", {"start": v(1.56, -0.47) * mm, "end": v(1.56, -0.48) * mm});
            skLineSegment(sketch, "E2413", {"start": v(1.56, -0.48) * mm, "end": v(1.56, -0.48) * mm});
            skLineSegment(sketch, "E2414", {"start": v(1.56, -0.48) * mm, "end": v(1.58, -0.49) * mm});
            skLineSegment(sketch, "E2415", {"start": v(1.58, -0.49) * mm, "end": v(1.6, -0.49) * mm});
            skLineSegment(sketch, "E2416", {"start": v(1.6, -0.49) * mm, "end": v(1.6, -0.49) * mm});
            skLineSegment(sketch, "E2417", {"start": v(1.6, -0.49) * mm, "end": v(1.6, -0.48) * mm});
            skLineSegment(sketch, "E2418", {"start": v(1.6, -0.48) * mm, "end": v(1.62, -0.48) * mm});
            skLineSegment(sketch, "E2419", {"start": v(1.62, -0.48) * mm, "end": v(1.63, -0.48) * mm});
            skLineSegment(sketch, "E2420", {"start": v(1.63, -0.48) * mm, "end": v(1.63, -0.49) * mm});
            skLineSegment(sketch, "E2421", {"start": v(1.63, -0.49) * mm, "end": v(1.63, -0.5) * mm});
            skLineSegment(sketch, "E2422", {"start": v(1.63, -0.5) * mm, "end": v(1.63, -0.5) * mm});
            skLineSegment(sketch, "E2423", {"start": v(1.63, -0.5) * mm, "end": v(1.63, -0.51) * mm});
            skLineSegment(sketch, "E2424", {"start": v(1.63, -0.51) * mm, "end": v(1.64, -0.52) * mm});
            skLineSegment(sketch, "E2425", {"start": v(1.64, -0.52) * mm, "end": v(1.65, -0.52) * mm});
            skLineSegment(sketch, "E2426", {"start": v(1.65, -0.52) * mm, "end": v(1.65, -0.52) * mm});
            skLineSegment(sketch, "E2427", {"start": v(1.65, -0.52) * mm, "end": v(1.66, -0.52) * mm});
            skLineSegment(sketch, "E2428", {"start": v(1.66, -0.52) * mm, "end": v(1.65, -0.53) * mm});
            skLineSegment(sketch, "E2429", {"start": v(1.65, -0.53) * mm, "end": v(1.65, -0.53) * mm});
            skLineSegment(sketch, "E2430", {"start": v(1.65, -0.53) * mm, "end": v(1.64, -0.54) * mm});
            skLineSegment(sketch, "E2431", {"start": v(1.64, -0.54) * mm, "end": v(1.65, -0.55) * mm});
            skLineSegment(sketch, "E2432", {"start": v(1.65, -0.55) * mm, "end": v(1.65, -0.55) * mm});
            skLineSegment(sketch, "E2433", {"start": v(1.65, -0.55) * mm, "end": v(1.66, -0.56) * mm});
            skLineSegment(sketch, "E2434", {"start": v(1.66, -0.56) * mm, "end": v(1.64, -0.56) * mm});
            skLineSegment(sketch, "E2435", {"start": v(1.64, -0.56) * mm, "end": v(1.63, -0.56) * mm});
            skLineSegment(sketch, "E2436", {"start": v(1.63, -0.56) * mm, "end": v(1.62, -0.56) * mm});
            skLineSegment(sketch, "E2437", {"start": v(1.62, -0.56) * mm, "end": v(1.6, -0.56) * mm});
            skLineSegment(sketch, "E2438", {"start": v(1.6, -0.56) * mm, "end": v(1.57, -0.55) * mm});
            skLineSegment(sketch, "E2439", {"start": v(1.57, -0.55) * mm, "end": v(1.55, -0.54) * mm});
            skLineSegment(sketch, "E2440", {"start": v(1.55, -0.54) * mm, "end": v(1.55, -0.53) * mm});
            skLineSegment(sketch, "E2441", {"start": v(1.55, -0.53) * mm, "end": v(1.56, -0.53) * mm});
            skLineSegment(sketch, "E2442", {"start": v(1.56, -0.53) * mm, "end": v(1.56, -0.52) * mm});
            skLineSegment(sketch, "E2443", {"start": v(1.56, -0.52) * mm, "end": v(1.55, -0.51) * mm});
            skLineSegment(sketch, "E2444", {"start": v(1.55, -0.51) * mm, "end": v(1.54, -0.5) * mm});
            skLineSegment(sketch, "E2445", {"start": v(1.54, -0.5) * mm, "end": v(1.52, -0.47) * mm});
            skLineSegment(sketch, "E2446", {"start": v(1.52, -0.47) * mm, "end": v(1.5, -0.46) * mm});
            skLineSegment(sketch, "E2447", {"start": v(1.5, -0.46) * mm, "end": v(1.5, -0.46) * mm});
            skLineSegment(sketch, "E2448", {"start": v(1.5, -0.46) * mm, "end": v(1.49, -0.46) * mm});
            skLineSegment(sketch, "E2449", {"start": v(1.49, -0.46) * mm, "end": v(1.48, -0.44) * mm});
            skLineSegment(sketch, "E2450", {"start": v(1.48, -0.44) * mm, "end": v(1.48, -0.44) * mm});
            skLineSegment(sketch, "E2451", {"start": v(1.48, -0.44) * mm, "end": v(1.48, -0.43) * mm});
            skLineSegment(sketch, "E2452", {"start": v(1.48, -0.43) * mm, "end": v(1.48, -0.42) * mm});
            skLineSegment(sketch, "E2453", {"start": v(1.48, -0.42) * mm, "end": v(1.48, -0.42) * mm});
            skLineSegment(sketch, "E2454", {"start": v(1.48, -0.42) * mm, "end": v(1.49, -0.42) * mm});
            skLineSegment(sketch, "E2455", {"start": v(1.49, -0.42) * mm, "end": v(1.5, -0.41) * mm});
            skLineSegment(sketch, "E2456", {"start": v(1.5, -0.41) * mm, "end": v(1.5, -0.4) * mm});
            skLineSegment(sketch, "E2457", {"start": v(1.5, -0.4) * mm, "end": v(1.5, -0.39) * mm});
            skLineSegment(sketch, "E2458", {"start": v(1.5, -0.39) * mm, "end": v(1.5, -0.38) * mm});
            skLineSegment(sketch, "E2459", {"start": v(1.5, -0.38) * mm, "end": v(1.5, -0.38) * mm});
            skLineSegment(sketch, "E2460", {"start": v(1.5, -0.38) * mm, "end": v(1.5, -0.39) * mm});
            skLineSegment(sketch, "E2461", {"start": v(1.5, -0.39) * mm, "end": v(1.5, -0.4) * mm});
            skLineSegment(sketch, "E2462", {"start": v(1.7, -0.56) * mm, "end": v(1.7, -0.57) * mm});
            skLineSegment(sketch, "E2463", {"start": v(1.7, -0.57) * mm, "end": v(1.7, -0.59) * mm});
            skLineSegment(sketch, "E2464", {"start": v(1.7, -0.59) * mm, "end": v(1.68, -0.6) * mm});
            skLineSegment(sketch, "E2465", {"start": v(1.68, -0.6) * mm, "end": v(1.67, -0.6) * mm});
            skLineSegment(sketch, "E2466", {"start": v(1.67, -0.6) * mm, "end": v(1.67, -0.6) * mm});
            skLineSegment(sketch, "E2467", {"start": v(1.67, -0.6) * mm, "end": v(1.67, -0.59) * mm});
            skLineSegment(sketch, "E2468", {"start": v(1.67, -0.59) * mm, "end": v(1.7, -0.55) * mm});
            skLineSegment(sketch, "E2469", {"start": v(1.7, -0.55) * mm, "end": v(1.71, -0.52) * mm});
            skLineSegment(sketch, "E2470", {"start": v(1.71, -0.52) * mm, "end": v(1.72, -0.5) * mm});
            skLineSegment(sketch, "E2471", {"start": v(1.72, -0.5) * mm, "end": v(1.73, -0.5) * mm});
            skLineSegment(sketch, "E2472", {"start": v(1.73, -0.5) * mm, "end": v(1.73, -0.51) * mm});
            skLineSegment(sketch, "E2473", {"start": v(1.73, -0.51) * mm, "end": v(1.72, -0.52) * mm});
            skLineSegment(sketch, "E2474", {"start": v(1.72, -0.52) * mm, "end": v(1.71, -0.54) * mm});
            skLineSegment(sketch, "E2475", {"start": v(1.71, -0.54) * mm, "end": v(1.7, -0.56) * mm});
            skLineSegment(sketch, "E2476", {"start": v(1.7, -0.56) * mm, "end": v(1.7, -0.56) * mm});
            skLineSegment(sketch, "E2477", {"start": v(-1.3, -0.55) * mm, "end": v(-1.28, -0.55) * mm});
            skLineSegment(sketch, "E2478", {"start": v(-1.28, -0.55) * mm, "end": v(-1.23, -0.57) * mm});
            skLineSegment(sketch, "E2479", {"start": v(-1.23, -0.57) * mm, "end": v(-1.15, -0.58) * mm});
            skLineSegment(sketch, "E2480", {"start": v(-1.15, -0.58) * mm, "end": v(-1.04, -0.59) * mm});
            skLineSegment(sketch, "E2481", {"start": v(-1.04, -0.59) * mm, "end": v(-0.93, -0.6) * mm});
            skLineSegment(sketch, "E2482", {"start": v(-0.93, -0.6) * mm, "end": v(-0.9, -0.6) * mm});
            skLineSegment(sketch, "E2483", {"start": v(-0.9, -0.6) * mm, "end": v(-0.88, -0.6) * mm});
            skLineSegment(sketch, "E2484", {"start": v(-0.88, -0.6) * mm, "end": v(-0.83, -0.6) * mm});
            skLineSegment(sketch, "E2485", {"start": v(-0.83, -0.6) * mm, "end": v(-0.78, -0.6) * mm});
            skLineSegment(sketch, "E2486", {"start": v(-0.78, -0.6) * mm, "end": v(-0.75, -0.6) * mm});
            skLineSegment(sketch, "E2487", {"start": v(-0.75, -0.6) * mm, "end": v(-0.73, -0.62) * mm});
            skLineSegment(sketch, "E2488", {"start": v(-0.73, -0.62) * mm, "end": v(-0.72, -0.63) * mm});
            skLineSegment(sketch, "E2489", {"start": v(-0.72, -0.63) * mm, "end": v(-0.74, -0.64) * mm});
            skLineSegment(sketch, "E2490", {"start": v(-0.74, -0.64) * mm, "end": v(-0.77, -0.66) * mm});
            skLineSegment(sketch, "E2491", {"start": v(-0.77, -0.66) * mm, "end": v(-0.8, -0.67) * mm});
            skLineSegment(sketch, "E2492", {"start": v(-0.8, -0.67) * mm, "end": v(-0.81, -0.67) * mm});
            skLineSegment(sketch, "E2493", {"start": v(-0.81, -0.67) * mm, "end": v(-0.84, -0.68) * mm});
            skLineSegment(sketch, "E2494", {"start": v(-0.84, -0.68) * mm, "end": v(-0.92, -0.72) * mm});
            skLineSegment(sketch, "E2495", {"start": v(-0.92, -0.72) * mm, "end": v(-1.05, -0.8) * mm});
            skLineSegment(sketch, "E2496", {"start": v(-1.05, -0.8) * mm, "end": v(-1.16, -0.89) * mm});
            skLineSegment(sketch, "E2497", {"start": v(-1.16, -0.89) * mm, "end": v(-1.22, -0.95) * mm});
            skLineSegment(sketch, "E2498", {"start": v(-1.22, -0.95) * mm, "end": v(-1.24, -0.97) * mm});
            skLineSegment(sketch, "E2499", {"start": v(-1.24, -0.97) * mm, "end": v(-1.24, -0.98) * mm});
            skLineSegment(sketch, "E2500", {"start": v(-1.24, -0.98) * mm, "end": v(-1.26, -1) * mm});
            skLineSegment(sketch, "E2501", {"start": v(-1.26, -1) * mm, "end": v(-1.27, -1.01) * mm});
            skLineSegment(sketch, "E2502", {"start": v(-1.27, -1.01) * mm, "end": v(-1.29, -1.02) * mm});
            skLineSegment(sketch, "E2503", {"start": v(-1.29, -1.02) * mm, "end": v(-1.3, -1.01) * mm});
            skLineSegment(sketch, "E2504", {"start": v(-1.3, -1.01) * mm, "end": v(-1.3, -1) * mm});
            skLineSegment(sketch, "E2505", {"start": v(-1.3, -1) * mm, "end": v(-1.3, -0.96) * mm});
            skLineSegment(sketch, "E2506", {"start": v(-1.3, -0.96) * mm, "end": v(-1.31, -0.9) * mm});
            skLineSegment(sketch, "E2507", {"start": v(-1.31, -0.9) * mm, "end": v(-1.31, -0.86) * mm});
            skLineSegment(sketch, "E2508", {"start": v(-1.31, -0.86) * mm, "end": v(-1.31, -0.84) * mm});
            skLineSegment(sketch, "E2509", {"start": v(-1.31, -0.84) * mm, "end": v(-1.32, -0.81) * mm});
            skLineSegment(sketch, "E2510", {"start": v(-1.32, -0.81) * mm, "end": v(-1.33, -0.7) * mm});
            skLineSegment(sketch, "E2511", {"start": v(-1.33, -0.7) * mm, "end": v(-1.34, -0.61) * mm});
            skLineSegment(sketch, "E2512", {"start": v(-1.34, -0.61) * mm, "end": v(-1.34, -0.6) * mm});
            skLineSegment(sketch, "E2513", {"start": v(-1.34, -0.6) * mm, "end": v(-1.35, -0.6) * mm});
            skLineSegment(sketch, "E2514", {"start": v(-1.35, -0.6) * mm, "end": v(-1.35, -0.57) * mm});
            skLineSegment(sketch, "E2515", {"start": v(-1.35, -0.57) * mm, "end": v(-1.36, -0.55) * mm});
            skLineSegment(sketch, "E2516", {"start": v(-1.36, -0.55) * mm, "end": v(-1.36, -0.53) * mm});
            skLineSegment(sketch, "E2517", {"start": v(-1.36, -0.53) * mm, "end": v(-1.36, -0.53) * mm});
            skLineSegment(sketch, "E2518", {"start": v(-1.36, -0.53) * mm, "end": v(-1.35, -0.52) * mm});
            skLineSegment(sketch, "E2519", {"start": v(-1.35, -0.52) * mm, "end": v(-1.34, -0.53) * mm});
            skLineSegment(sketch, "E2520", {"start": v(-1.34, -0.53) * mm, "end": v(-1.32, -0.53) * mm});
            skLineSegment(sketch, "E2521", {"start": v(-1.32, -0.53) * mm, "end": v(-1.3, -0.54) * mm});
            skLineSegment(sketch, "E2522", {"start": v(-1.3, -0.54) * mm, "end": v(-1.3, -0.55) * mm});
            skLineSegment(sketch, "E2523", {"start": v(0.04, -0.66) * mm, "end": v(0.05, -0.66) * mm});
            skLineSegment(sketch, "E2524", {"start": v(0.05, -0.66) * mm, "end": v(0.06, -0.67) * mm});
            skLineSegment(sketch, "E2525", {"start": v(0.06, -0.67) * mm, "end": v(0.1, -0.69) * mm});
            skLineSegment(sketch, "E2526", {"start": v(0.1, -0.69) * mm, "end": v(0.12, -0.7) * mm});
            skLineSegment(sketch, "E2527", {"start": v(0.12, -0.7) * mm, "end": v(0.14, -0.73) * mm});
            skLineSegment(sketch, "E2528", {"start": v(0.14, -0.73) * mm, "end": v(0.15, -0.73) * mm});
            skLineSegment(sketch, "E2529", {"start": v(0.15, -0.73) * mm, "end": v(0.2, -0.8) * mm});
            skLineSegment(sketch, "E2530", {"start": v(0.2, -0.8) * mm, "end": v(0.15, -0.87) * mm});
            skLineSegment(sketch, "E2531", {"start": v(0.15, -0.87) * mm, "end": v(0.14, -0.88) * mm});
            skLineSegment(sketch, "E2532", {"start": v(0.14, -0.88) * mm, "end": v(0.1, -0.93) * mm});
            skLineSegment(sketch, "E2533", {"start": v(0.1, -0.93) * mm, "end": v(0.07, -0.98) * mm});
            skLineSegment(sketch, "E2534", {"start": v(0.07, -0.98) * mm, "end": v(0.05, -1.03) * mm});
            skLineSegment(sketch, "E2535", {"start": v(0.05, -1.03) * mm, "end": v(0.03, -1.07) * mm});
            skLineSegment(sketch, "E2536", {"start": v(0.03, -1.07) * mm, "end": v(0.03, -1.09) * mm});
            skLineSegment(sketch, "E2537", {"start": v(0.03, -1.09) * mm, "end": v(0.03, -1.1) * mm});
            skLineSegment(sketch, "E2538", {"start": v(0.03, -1.1) * mm, "end": v(0.02, -1.12) * mm});
            skLineSegment(sketch, "E2539", {"start": v(0.02, -1.12) * mm, "end": v(0.02, -1.13) * mm});
            skLineSegment(sketch, "E2540", {"start": v(0.02, -1.13) * mm, "end": v(0.01, -1.13) * mm});
            skLineSegment(sketch, "E2541", {"start": v(0.01, -1.13) * mm, "end": v(0.01, -1.12) * mm});
            skLineSegment(sketch, "E2542", {"start": v(0.01, -1.12) * mm, "end": v(0.01, -1.12) * mm});
            skLineSegment(sketch, "E2543", {"start": v(0.01, -1.12) * mm, "end": v(0.01, -1.1) * mm});
            skLineSegment(sketch, "E2544", {"start": v(0.01, -1.1) * mm, "end": v(0, -1.06) * mm});
            skLineSegment(sketch, "E2545", {"start": v(0, -1.06) * mm, "end": v(-0.03, -0.98) * mm});
            skLineSegment(sketch, "E2546", {"start": v(-0.03, -0.98) * mm, "end": v(-0.06, -0.9) * mm});
            skLineSegment(sketch, "E2547", {"start": v(-0.06, -0.9) * mm, "end": v(-0.08, -0.85) * mm});
            skLineSegment(sketch, "E2548", {"start": v(-0.08, -0.85) * mm, "end": v(-0.1, -0.84) * mm});
            skLineSegment(sketch, "E2549", {"start": v(-0.1, -0.84) * mm, "end": v(-0.1, -0.83) * mm});
            skLineSegment(sketch, "E2550", {"start": v(-0.1, -0.83) * mm, "end": v(-0.12, -0.8) * mm});
            skLineSegment(sketch, "E2551", {"start": v(-0.12, -0.8) * mm, "end": v(-0.12, -0.76) * mm});
            skLineSegment(sketch, "E2552", {"start": v(-0.12, -0.76) * mm, "end": v(-0.1, -0.73) * mm});
            skLineSegment(sketch, "E2553", {"start": v(-0.1, -0.73) * mm, "end": v(-0.07, -0.7) * mm});
            skLineSegment(sketch, "E2554", {"start": v(-0.07, -0.7) * mm, "end": v(-0.06, -0.68) * mm});
            skLineSegment(sketch, "E2555", {"start": v(-0.06, -0.68) * mm, "end": v(-0.06, -0.68) * mm});
            skLineSegment(sketch, "E2556", {"start": v(-0.06, -0.68) * mm, "end": v(-0.04, -0.66) * mm});
            skLineSegment(sketch, "E2557", {"start": v(-0.04, -0.66) * mm, "end": v(-0.02, -0.65) * mm});
            skLineSegment(sketch, "E2558", {"start": v(-0.02, -0.65) * mm, "end": v(0, -0.65) * mm});
            skLineSegment(sketch, "E2559", {"start": v(0, -0.65) * mm, "end": v(0.03, -0.66) * mm});
            skLineSegment(sketch, "E2560", {"start": v(0.03, -0.66) * mm, "end": v(0.04, -0.66) * mm});
            skLineSegment(sketch, "E2561", {"start": v(-1.41, -0.75) * mm, "end": v(-1.42, -0.76) * mm});
            skLineSegment(sketch, "E2562", {"start": v(-1.42, -0.76) * mm, "end": v(-1.43, -0.76) * mm});
            skLineSegment(sketch, "E2563", {"start": v(-1.43, -0.76) * mm, "end": v(-1.47, -0.76) * mm});
            skLineSegment(sketch, "E2564", {"start": v(-1.47, -0.76) * mm, "end": v(-1.5, -0.76) * mm});
            skLineSegment(sketch, "E2565", {"start": v(-1.5, -0.76) * mm, "end": v(-1.51, -0.75) * mm});
            skLineSegment(sketch, "E2566", {"start": v(-1.51, -0.75) * mm, "end": v(-1.51, -0.75) * mm});
            skLineSegment(sketch, "E2567", {"start": v(-1.51, -0.75) * mm, "end": v(-1.5, -0.74) * mm});
            skLineSegment(sketch, "E2568", {"start": v(-1.5, -0.74) * mm, "end": v(-1.47, -0.74) * mm});
            skLineSegment(sketch, "E2569", {"start": v(-1.47, -0.74) * mm, "end": v(-1.47, -0.74) * mm});
            skLineSegment(sketch, "E2570", {"start": v(-1.47, -0.74) * mm, "end": v(-1.46, -0.74) * mm});
            skLineSegment(sketch, "E2571", {"start": v(-1.46, -0.74) * mm, "end": v(-1.44, -0.74) * mm});
            skLineSegment(sketch, "E2572", {"start": v(-1.44, -0.74) * mm, "end": v(-1.44, -0.73) * mm});
            skLineSegment(sketch, "E2573", {"start": v(-1.44, -0.73) * mm, "end": v(-1.44, -0.73) * mm});
            skLineSegment(sketch, "E2574", {"start": v(-1.44, -0.73) * mm, "end": v(-1.44, -0.7) * mm});
            skLineSegment(sketch, "E2575", {"start": v(-1.44, -0.7) * mm, "end": v(-1.44, -0.69) * mm});
            skLineSegment(sketch, "E2576", {"start": v(-1.44, -0.69) * mm, "end": v(-1.44, -0.68) * mm});
            skLineSegment(sketch, "E2577", {"start": v(-1.44, -0.68) * mm, "end": v(-1.44, -0.68) * mm});
            skLineSegment(sketch, "E2578", {"start": v(-1.44, -0.68) * mm, "end": v(-1.43, -0.67) * mm});
            skLineSegment(sketch, "E2579", {"start": v(-1.43, -0.67) * mm, "end": v(-1.43, -0.66) * mm});
            skLineSegment(sketch, "E2580", {"start": v(-1.43, -0.66) * mm, "end": v(-1.42, -0.67) * mm});
            skLineSegment(sketch, "E2581", {"start": v(-1.42, -0.67) * mm, "end": v(-1.42, -0.7) * mm});
            skLineSegment(sketch, "E2582", {"start": v(-1.42, -0.7) * mm, "end": v(-1.42, -0.7) * mm});
            skLineSegment(sketch, "E2583", {"start": v(-1.42, -0.7) * mm, "end": v(-1.41, -0.74) * mm});
            skLineSegment(sketch, "E2584", {"start": v(-1.41, -0.74) * mm, "end": v(-1.41, -0.75) * mm});
            skLineSegment(sketch, "E2585", {"start": v(-1.41, -0.75) * mm, "end": v(-1.41, -0.75) * mm});
            skLineSegment(sketch, "E2586", {"start": v(0.66, -0.8) * mm, "end": v(0.66, -0.8) * mm});
            skLineSegment(sketch, "E2587", {"start": v(0.66, -0.8) * mm, "end": v(0.67, -0.8) * mm});
            skLineSegment(sketch, "E2588", {"start": v(0.67, -0.8) * mm, "end": v(0.68, -0.81) * mm});
            skLineSegment(sketch, "E2589", {"start": v(0.68, -0.81) * mm, "end": v(0.68, -0.81) * mm});
            skLineSegment(sketch, "E2590", {"start": v(0.68, -0.81) * mm, "end": v(0.69, -0.81) * mm});
            skLineSegment(sketch, "E2591", {"start": v(0.69, -0.81) * mm, "end": v(0.7, -0.81) * mm});
            skLineSegment(sketch, "E2592", {"start": v(0.7, -0.81) * mm, "end": v(0.7, -0.82) * mm});
            skLineSegment(sketch, "E2593", {"start": v(0.7, -0.82) * mm, "end": v(0.7, -0.83) * mm});
            skLineSegment(sketch, "E2594", {"start": v(0.7, -0.83) * mm, "end": v(0.7, -0.85) * mm});
            skLineSegment(sketch, "E2595", {"start": v(0.7, -0.85) * mm, "end": v(0.7, -0.85) * mm});
            skLineSegment(sketch, "E2596", {"start": v(0.7, -0.85) * mm, "end": v(0.68, -0.86) * mm});
            skLineSegment(sketch, "E2597", {"start": v(0.68, -0.86) * mm, "end": v(0.67, -0.86) * mm});
            skLineSegment(sketch, "E2598", {"start": v(0.67, -0.86) * mm, "end": v(0.67, -0.85) * mm});
            skLineSegment(sketch, "E2599", {"start": v(0.67, -0.85) * mm, "end": v(0.67, -0.85) * mm});
            skLineSegment(sketch, "E2600", {"start": v(0.67, -0.85) * mm, "end": v(0.66, -0.85) * mm});
            skLineSegment(sketch, "E2601", {"start": v(0.66, -0.85) * mm, "end": v(0.65, -0.85) * mm});
            skLineSegment(sketch, "E2602", {"start": v(0.65, -0.85) * mm, "end": v(0.65, -0.85) * mm});
            skLineSegment(sketch, "E2603", {"start": v(0.65, -0.85) * mm, "end": v(0.64, -0.84) * mm});
            skLineSegment(sketch, "E2604", {"start": v(0.64, -0.84) * mm, "end": v(0.64, -0.82) * mm});
            skLineSegment(sketch, "E2605", {"start": v(0.64, -0.82) * mm, "end": v(0.64, -0.81) * mm});
            skLineSegment(sketch, "E2606", {"start": v(0.64, -0.81) * mm, "end": v(0.64, -0.8) * mm});
            skLineSegment(sketch, "E2607", {"start": v(0.64, -0.8) * mm, "end": v(0.64, -0.78) * mm});
            skLineSegment(sketch, "E2608", {"start": v(0.64, -0.78) * mm, "end": v(0.65, -0.77) * mm});
            skLineSegment(sketch, "E2609", {"start": v(0.65, -0.77) * mm, "end": v(0.65, -0.77) * mm});
            skLineSegment(sketch, "E2610", {"start": v(0.65, -0.77) * mm, "end": v(0.66, -0.78) * mm});
            skLineSegment(sketch, "E2611", {"start": v(0.66, -0.78) * mm, "end": v(0.66, -0.79) * mm});
            skLineSegment(sketch, "E2612", {"start": v(0.66, -0.79) * mm, "end": v(0.66, -0.8) * mm});
            skLineSegment(sketch, "E2613", {"start": v(0.65, -0.94) * mm, "end": v(0.65, -0.95) * mm});
            skLineSegment(sketch, "E2614", {"start": v(0.65, -0.95) * mm, "end": v(0.64, -0.97) * mm});
            skLineSegment(sketch, "E2615", {"start": v(0.64, -0.97) * mm, "end": v(0.63, -0.98) * mm});
            skLineSegment(sketch, "E2616", {"start": v(0.63, -0.98) * mm, "end": v(0.63, -0.98) * mm});
            skLineSegment(sketch, "E2617", {"start": v(0.63, -0.98) * mm, "end": v(0.62, -0.99) * mm});
            skLineSegment(sketch, "E2618", {"start": v(0.62, -0.99) * mm, "end": v(0.6, -0.98) * mm});
            skLineSegment(sketch, "E2619", {"start": v(0.6, -0.98) * mm, "end": v(0.61, -0.97) * mm});
            skLineSegment(sketch, "E2620", {"start": v(0.61, -0.97) * mm, "end": v(0.62, -0.95) * mm});
            skLineSegment(sketch, "E2621", {"start": v(0.62, -0.95) * mm, "end": v(0.62, -0.94) * mm});
            skLineSegment(sketch, "E2622", {"start": v(0.62, -0.94) * mm, "end": v(0.62, -0.93) * mm});
            skLineSegment(sketch, "E2623", {"start": v(0.62, -0.93) * mm, "end": v(0.63, -0.92) * mm});
            skLineSegment(sketch, "E2624", {"start": v(0.63, -0.92) * mm, "end": v(0.64, -0.9) * mm});
            skLineSegment(sketch, "E2625", {"start": v(0.64, -0.9) * mm, "end": v(0.65, -0.92) * mm});
            skLineSegment(sketch, "E2626", {"start": v(0.65, -0.92) * mm, "end": v(0.65, -0.94) * mm});
            skLineSegment(sketch, "E2627", {"start": v(0.65, -0.94) * mm, "end": v(0.65, -0.94) * mm});
            skLineSegment(sketch, "E2628", {"start": v(1.3, 0.74) * mm, "end": v(1.3, 0.74) * mm});
            skLineSegment(sketch, "E2629", {"start": v(1.3, 0.74) * mm, "end": v(1.3, 0.72) * mm});
            skLineSegment(sketch, "E2630", {"start": v(1.3, 0.72) * mm, "end": v(1.29, 0.7) * mm});
            skLineSegment(sketch, "E2631", {"start": v(1.29, 0.7) * mm, "end": v(1.3, 0.68) * mm});
            skLineSegment(sketch, "E2632", {"start": v(1.3, 0.68) * mm, "end": v(1.3, 0.67) * mm});
            skLineSegment(sketch, "E2633", {"start": v(1.3, 0.67) * mm, "end": v(1.3, 0.67) * mm});
            skLineSegment(sketch, "E2634", {"start": v(1.3, 0.67) * mm, "end": v(1.31, 0.69) * mm});
            skLineSegment(sketch, "E2635", {"start": v(1.31, 0.69) * mm, "end": v(1.32, 0.71) * mm});
            skLineSegment(sketch, "E2636", {"start": v(1.32, 0.71) * mm, "end": v(1.33, 0.74) * mm});
            skLineSegment(sketch, "E2637", {"start": v(1.33, 0.74) * mm, "end": v(1.33, 0.75) * mm});
            skLineSegment(sketch, "E2638", {"start": v(1.33, 0.75) * mm, "end": v(1.32, 0.75) * mm});
            skLineSegment(sketch, "E2639", {"start": v(1.32, 0.75) * mm, "end": v(1.32, 0.76) * mm});
            skLineSegment(sketch, "E2640", {"start": v(1.32, 0.76) * mm, "end": v(1.32, 0.75) * mm});
            skLineSegment(sketch, "E2641", {"start": v(1.32, 0.75) * mm, "end": v(1.3, 0.74) * mm});
            skLineSegment(sketch, "E2642", {"start": v(-0.23, 0.46) * mm, "end": v(-0.23, 0.46) * mm});
            skLineSegment(sketch, "E2643", {"start": v(-0.23, 0.46) * mm, "end": v(-0.27, 0.43) * mm});
            skLineSegment(sketch, "E2644", {"start": v(-0.27, 0.43) * mm, "end": v(-0.31, 0.39) * mm});
            skLineSegment(sketch, "E2645", {"start": v(-0.31, 0.39) * mm, "end": v(-0.32, 0.38) * mm});
            skLineSegment(sketch, "E2646", {"start": v(-0.32, 0.38) * mm, "end": v(-0.32, 0.37) * mm});
            skLineSegment(sketch, "E2647", {"start": v(-0.32, 0.37) * mm, "end": v(-0.34, 0.35) * mm});
            skLineSegment(sketch, "E2648", {"start": v(-0.34, 0.35) * mm, "end": v(-0.36, 0.32) * mm});
            skLineSegment(sketch, "E2649", {"start": v(-0.36, 0.32) * mm, "end": v(-0.38, 0.29) * mm});
            skLineSegment(sketch, "E2650", {"start": v(-0.38, 0.29) * mm, "end": v(-0.39, 0.27) * mm});
            skLineSegment(sketch, "E2651", {"start": v(-0.39, 0.27) * mm, "end": v(-0.4, 0.27) * mm});
            skLineSegment(sketch, "E2652", {"start": v(-0.4, 0.27) * mm, "end": v(-0.4, 0.26) * mm});
            skLineSegment(sketch, "E2653", {"start": v(-0.4, 0.26) * mm, "end": v(-0.41, 0.24) * mm});
            skLineSegment(sketch, "E2654", {"start": v(-0.41, 0.24) * mm, "end": v(-0.42, 0.22) * mm});
            skLineSegment(sketch, "E2655", {"start": v(-0.42, 0.22) * mm, "end": v(-0.42, 0.21) * mm});
            skLineSegment(sketch, "E2656", {"start": v(-0.42, 0.21) * mm, "end": v(-0.42, 0.2) * mm});
            skLineSegment(sketch, "E2657", {"start": v(-0.42, 0.2) * mm, "end": v(-0.43, 0.17) * mm});
            skLineSegment(sketch, "E2658", {"start": v(-0.43, 0.17) * mm, "end": v(-0.46, 0.14) * mm});
            skLineSegment(sketch, "E2659", {"start": v(-0.46, 0.14) * mm, "end": v(-0.5, 0.11) * mm});
            skLineSegment(sketch, "E2660", {"start": v(-0.5, 0.11) * mm, "end": v(-0.55, 0.1) * mm});
            skLineSegment(sketch, "E2661", {"start": v(-0.55, 0.1) * mm, "end": v(-0.56, 0.1) * mm});
            skLineSegment(sketch, "E2662", {"start": v(-0.56, 0.1) * mm, "end": v(-0.57, 0.1) * mm});
            skLineSegment(sketch, "E2663", {"start": v(-0.57, 0.1) * mm, "end": v(-0.6, 0.1) * mm});
            skLineSegment(sketch, "E2664", {"start": v(-0.6, 0.1) * mm, "end": v(-0.62, 0.1) * mm});
            skLineSegment(sketch, "E2665", {"start": v(-0.62, 0.1) * mm, "end": v(-0.63, 0.1) * mm});
            skLineSegment(sketch, "E2666", {"start": v(-0.63, 0.1) * mm, "end": v(-0.63, 0.1) * mm});
            skLineSegment(sketch, "E2667", {"start": v(-0.63, 0.1) * mm, "end": v(-0.64, 0.12) * mm});
            skLineSegment(sketch, "E2668", {"start": v(-0.64, 0.12) * mm, "end": v(-0.66, 0.13) * mm});
            skLineSegment(sketch, "E2669", {"start": v(-0.66, 0.13) * mm, "end": v(-0.66, 0.13) * mm});
            skLineSegment(sketch, "E2670", {"start": v(-0.66, 0.13) * mm, "end": v(-0.67, 0.13) * mm});
            skLineSegment(sketch, "E2671", {"start": v(-0.67, 0.13) * mm, "end": v(-0.68, 0.14) * mm});
            skLineSegment(sketch, "E2672", {"start": v(-0.68, 0.14) * mm, "end": v(-0.7, 0.16) * mm});
            skLineSegment(sketch, "E2673", {"start": v(-0.7, 0.16) * mm, "end": v(-0.74, 0.2) * mm});
            skLineSegment(sketch, "E2674", {"start": v(-0.74, 0.2) * mm, "end": v(-0.77, 0.21) * mm});
            skLineSegment(sketch, "E2675", {"start": v(-0.77, 0.21) * mm, "end": v(-0.78, 0.22) * mm});
            skLineSegment(sketch, "E2676", {"start": v(-0.78, 0.22) * mm, "end": v(-0.79, 0.23) * mm});
            skLineSegment(sketch, "E2677", {"start": v(-0.79, 0.23) * mm, "end": v(-0.82, 0.26) * mm});
            skLineSegment(sketch, "E2678", {"start": v(-0.82, 0.26) * mm, "end": v(-0.85, 0.3) * mm});
            skLineSegment(sketch, "E2679", {"start": v(-0.85, 0.3) * mm, "end": v(-0.88, 0.32) * mm});
            skLineSegment(sketch, "E2680", {"start": v(-0.88, 0.32) * mm, "end": v(-0.9, 0.34) * mm});
            skLineSegment(sketch, "E2681", {"start": v(-0.9, 0.34) * mm, "end": v(-0.93, 0.35) * mm});
            skLineSegment(sketch, "E2682", {"start": v(-0.93, 0.35) * mm, "end": v(-0.95, 0.36) * mm});
            skLineSegment(sketch, "E2683", {"start": v(-0.95, 0.36) * mm, "end": v(-0.97, 0.37) * mm});
            skLineSegment(sketch, "E2684", {"start": v(-0.97, 0.37) * mm, "end": v(-0.98, 0.38) * mm});
            skLineSegment(sketch, "E2685", {"start": v(-0.98, 0.38) * mm, "end": v(-0.99, 0.38) * mm});
            skLineSegment(sketch, "E2686", {"start": v(-0.99, 0.38) * mm, "end": v(-1, 0.39) * mm});
            skLineSegment(sketch, "E2687", {"start": v(-1, 0.39) * mm, "end": v(-1.04, 0.4) * mm});
            skLineSegment(sketch, "E2688", {"start": v(-1.04, 0.4) * mm, "end": v(-1.08, 0.42) * mm});
            skLineSegment(sketch, "E2689", {"start": v(-1.08, 0.42) * mm, "end": v(-1.08, 0.43) * mm});
            skLineSegment(sketch, "E2690", {"start": v(-1.08, 0.43) * mm, "end": v(-1.1, 0.43) * mm});
            skLineSegment(sketch, "E2691", {"start": v(-1.1, 0.43) * mm, "end": v(-1.11, 0.44) * mm});
            skLineSegment(sketch, "E2692", {"start": v(-1.11, 0.44) * mm, "end": v(-1.13, 0.45) * mm});
            skLineSegment(sketch, "E2693", {"start": v(-1.13, 0.45) * mm, "end": v(-1.14, 0.45) * mm});
            skLineSegment(sketch, "E2694", {"start": v(-1.14, 0.45) * mm, "end": v(-1.14, 0.44) * mm});
            skLineSegment(sketch, "E2695", {"start": v(-1.14, 0.44) * mm, "end": v(-1.14, 0.44) * mm});
            skLineSegment(sketch, "E2696", {"start": v(-1.14, 0.44) * mm, "end": v(-1.14, 0.43) * mm});
            skLineSegment(sketch, "E2697", {"start": v(-1.14, 0.43) * mm, "end": v(-1.17, 0.42) * mm});
            skLineSegment(sketch, "E2698", {"start": v(-1.17, 0.42) * mm, "end": v(-1.17, 0.42) * mm});
            skLineSegment(sketch, "E2699", {"start": v(-1.17, 0.42) * mm, "end": v(-1.18, 0.42) * mm});
            skLineSegment(sketch, "E2700", {"start": v(-1.18, 0.42) * mm, "end": v(-1.18, 0.43) * mm});
            skLineSegment(sketch, "E2701", {"start": v(-1.18, 0.43) * mm, "end": v(-1.17, 0.44) * mm});
            skLineSegment(sketch, "E2702", {"start": v(-1.17, 0.44) * mm, "end": v(-1.17, 0.44) * mm});
            skLineSegment(sketch, "E2703", {"start": v(-1.17, 0.44) * mm, "end": v(-1.16, 0.45) * mm});
            skLineSegment(sketch, "E2704", {"start": v(-1.16, 0.45) * mm, "end": v(-1.16, 0.45) * mm});
            skLineSegment(sketch, "E2705", {"start": v(-1.16, 0.45) * mm, "end": v(-1.17, 0.45) * mm});
            skLineSegment(sketch, "E2706", {"start": v(-1.17, 0.45) * mm, "end": v(-1.17, 0.45) * mm});
            skLineSegment(sketch, "E2707", {"start": v(-1.17, 0.45) * mm, "end": v(-1.18, 0.45) * mm});
            skLineSegment(sketch, "E2708", {"start": v(-1.18, 0.45) * mm, "end": v(-1.2, 0.43) * mm});
            skLineSegment(sketch, "E2709", {"start": v(-1.2, 0.43) * mm, "end": v(-1.2, 0.43) * mm});
            skLineSegment(sketch, "E2710", {"start": v(-1.2, 0.43) * mm, "end": v(-1.2, 0.4) * mm});
            skLineSegment(sketch, "E2711", {"start": v(-1.2, 0.4) * mm, "end": v(-1.23, 0.37) * mm});
            skLineSegment(sketch, "E2712", {"start": v(-1.23, 0.37) * mm, "end": v(-1.23, 0.37) * mm});
            skLineSegment(sketch, "E2713", {"start": v(-1.23, 0.37) * mm, "end": v(-1.24, 0.36) * mm});
            skLineSegment(sketch, "E2714", {"start": v(-1.24, 0.36) * mm, "end": v(-1.25, 0.3) * mm});
            skLineSegment(sketch, "E2715", {"start": v(-1.25, 0.3) * mm, "end": v(-1.26, 0.22) * mm});
            skLineSegment(sketch, "E2716", {"start": v(-1.26, 0.22) * mm, "end": v(-1.27, 0.13) * mm});
            skLineSegment(sketch, "E2717", {"start": v(-1.27, 0.13) * mm, "end": v(-1.27, 0.07) * mm});
            skLineSegment(sketch, "E2718", {"start": v(-1.27, 0.07) * mm, "end": v(-1.26, 0.06) * mm});
            skLineSegment(sketch, "E2719", {"start": v(-1.26, 0.06) * mm, "end": v(-1.26, 0.05) * mm});
            skLineSegment(sketch, "E2720", {"start": v(-1.26, 0.05) * mm, "end": v(-1.26, 0.03) * mm});
            skLineSegment(sketch, "E2721", {"start": v(-1.26, 0.03) * mm, "end": v(-1.27, 0) * mm});
            skLineSegment(sketch, "E2722", {"start": v(-1.27, 0) * mm, "end": v(-1.3, -0.02) * mm});
            skLineSegment(sketch, "E2723", {"start": v(-1.3, -0.02) * mm, "end": v(-1.33, -0.05) * mm});
            skLineSegment(sketch, "E2724", {"start": v(-1.33, -0.05) * mm, "end": v(-1.35, -0.06) * mm});
            skLineSegment(sketch, "E2725", {"start": v(-1.35, -0.06) * mm, "end": v(-1.35, -0.06) * mm});
            skLineSegment(sketch, "E2726", {"start": v(-1.35, -0.06) * mm, "end": v(-1.38, -0.08) * mm});
            skLineSegment(sketch, "E2727", {"start": v(-1.38, -0.08) * mm, "end": v(-1.4, -0.1) * mm});
            skLineSegment(sketch, "E2728", {"start": v(-1.4, -0.1) * mm, "end": v(-1.42, -0.1) * mm});
            skLineSegment(sketch, "E2729", {"start": v(-1.42, -0.1) * mm, "end": v(-1.43, -0.11) * mm});
            skLineSegment(sketch, "E2730", {"start": v(-1.43, -0.11) * mm, "end": v(-1.43, -0.11) * mm});
            skLineSegment(sketch, "E2731", {"start": v(-1.43, -0.11) * mm, "end": v(-1.44, -0.12) * mm});
            skLineSegment(sketch, "E2732", {"start": v(-1.44, -0.12) * mm, "end": v(-1.44, -0.14) * mm});
            skLineSegment(sketch, "E2733", {"start": v(-1.44, -0.14) * mm, "end": v(-1.44, -0.17) * mm});
            skLineSegment(sketch, "E2734", {"start": v(-1.44, -0.17) * mm, "end": v(-1.43, -0.2) * mm});
            skLineSegment(sketch, "E2735", {"start": v(-1.43, -0.2) * mm, "end": v(-1.43, -0.22) * mm});
            skLineSegment(sketch, "E2736", {"start": v(-1.43, -0.22) * mm, "end": v(-1.42, -0.25) * mm});
            skLineSegment(sketch, "E2737", {"start": v(-1.42, -0.25) * mm, "end": v(-1.41, -0.28) * mm});
            skLineSegment(sketch, "E2738", {"start": v(-1.41, -0.28) * mm, "end": v(-1.4, -0.3) * mm});
            skLineSegment(sketch, "E2739", {"start": v(-1.4, -0.3) * mm, "end": v(-1.4, -0.3) * mm});
            skLineSegment(sketch, "E2740", {"start": v(-1.4, -0.3) * mm, "end": v(-1.39, -0.32) * mm});
            skLineSegment(sketch, "E2741", {"start": v(-1.39, -0.32) * mm, "end": v(-1.34, -0.38) * mm});
            skLineSegment(sketch, "E2742", {"start": v(-1.34, -0.38) * mm, "end": v(-1.24, -0.43) * mm});
            skLineSegment(sketch, "E2743", {"start": v(-1.24, -0.43) * mm, "end": v(-1.12, -0.44) * mm});
            skLineSegment(sketch, "E2744", {"start": v(-1.12, -0.44) * mm, "end": v(-1, -0.44) * mm});
            skLineSegment(sketch, "E2745", {"start": v(-1, -0.44) * mm, "end": v(-0.97, -0.43) * mm});
            skLineSegment(sketch, "E2746", {"start": v(-0.97, -0.43) * mm, "end": v(-0.95, -0.42) * mm});
            skLineSegment(sketch, "E2747", {"start": v(-0.95, -0.42) * mm, "end": v(-0.9, -0.41) * mm});
            skLineSegment(sketch, "E2748", {"start": v(-0.9, -0.41) * mm, "end": v(-0.85, -0.41) * mm});
            skLineSegment(sketch, "E2749", {"start": v(-0.85, -0.41) * mm, "end": v(-0.82, -0.41) * mm});
            skLineSegment(sketch, "E2750", {"start": v(-0.82, -0.41) * mm, "end": v(-0.8, -0.42) * mm});
            skLineSegment(sketch, "E2751", {"start": v(-0.8, -0.42) * mm, "end": v(-0.78, -0.43) * mm});
            skLineSegment(sketch, "E2752", {"start": v(-0.78, -0.43) * mm, "end": v(-0.76, -0.44) * mm});
            skLineSegment(sketch, "E2753", {"start": v(-0.76, -0.44) * mm, "end": v(-0.71, -0.48) * mm});
            skLineSegment(sketch, "E2754", {"start": v(-0.71, -0.48) * mm, "end": v(-0.65, -0.54) * mm});
            skLineSegment(sketch, "E2755", {"start": v(-0.65, -0.54) * mm, "end": v(-0.6, -0.61) * mm});
            skLineSegment(sketch, "E2756", {"start": v(-0.6, -0.61) * mm, "end": v(-0.6, -0.65) * mm});
            skLineSegment(sketch, "E2757", {"start": v(-0.6, -0.65) * mm, "end": v(-0.6, -0.66) * mm});
            skLineSegment(sketch, "E2758", {"start": v(-0.6, -0.66) * mm, "end": v(-0.6, -0.66) * mm});
            skLineSegment(sketch, "E2759", {"start": v(-0.6, -0.66) * mm, "end": v(-0.6, -0.67) * mm});
            skLineSegment(sketch, "E2760", {"start": v(-0.6, -0.67) * mm, "end": v(-0.6, -0.69) * mm});
            skLineSegment(sketch, "E2761", {"start": v(-0.6, -0.69) * mm, "end": v(-0.58, -0.7) * mm});
            skLineSegment(sketch, "E2762", {"start": v(-0.58, -0.7) * mm, "end": v(-0.55, -0.71) * mm});
            skLineSegment(sketch, "E2763", {"start": v(-0.55, -0.71) * mm, "end": v(-0.52, -0.73) * mm});
            skLineSegment(sketch, "E2764", {"start": v(-0.52, -0.73) * mm, "end": v(-0.5, -0.74) * mm});
            skLineSegment(sketch, "E2765", {"start": v(-0.5, -0.74) * mm, "end": v(-0.46, -0.75) * mm});
            skLineSegment(sketch, "E2766", {"start": v(-0.46, -0.75) * mm, "end": v(-0.43, -0.75) * mm});
            skLineSegment(sketch, "E2767", {"start": v(-0.43, -0.75) * mm, "end": v(-0.43, -0.75) * mm});
            skLineSegment(sketch, "E2768", {"start": v(-0.43, -0.75) * mm, "end": v(-0.4, -0.75) * mm});
            skLineSegment(sketch, "E2769", {"start": v(-0.4, -0.75) * mm, "end": v(-0.36, -0.74) * mm});
            skLineSegment(sketch, "E2770", {"start": v(-0.36, -0.74) * mm, "end": v(-0.3, -0.7) * mm});
            skLineSegment(sketch, "E2771", {"start": v(-0.3, -0.7) * mm, "end": v(-0.23, -0.62) * mm});
            skLineSegment(sketch, "E2772", {"start": v(-0.23, -0.62) * mm, "end": v(-0.2, -0.57) * mm});
            skLineSegment(sketch, "E2773", {"start": v(-0.2, -0.57) * mm, "end": v(-0.19, -0.54) * mm});
            skLineSegment(sketch, "E2774", {"start": v(-0.19, -0.54) * mm, "end": v(-0.18, -0.53) * mm});
            skLineSegment(sketch, "E2775", {"start": v(-0.18, -0.53) * mm, "end": v(-0.15, -0.48) * mm});
            skLineSegment(sketch, "E2776", {"start": v(-0.15, -0.48) * mm, "end": v(-0.1, -0.46) * mm});
            skLineSegment(sketch, "E2777", {"start": v(-0.1, -0.46) * mm, "end": v(-0.02, -0.49) * mm});
            skLineSegment(sketch, "E2778", {"start": v(-0.02, -0.49) * mm, "end": v(0.06, -0.54) * mm});
            skLineSegment(sketch, "E2779", {"start": v(0.06, -0.54) * mm, "end": v(0.1, -0.56) * mm});
            skLineSegment(sketch, "E2780", {"start": v(0.1, -0.56) * mm, "end": v(0.11, -0.58) * mm});
            skLineSegment(sketch, "E2781", {"start": v(0.11, -0.58) * mm, "end": v(0.18, -0.62) * mm});
            skLineSegment(sketch, "E2782", {"start": v(0.18, -0.62) * mm, "end": v(0.27, -0.67) * mm});
            skLineSegment(sketch, "E2783", {"start": v(0.27, -0.67) * mm, "end": v(0.34, -0.7) * mm});
            skLineSegment(sketch, "E2784", {"start": v(0.34, -0.7) * mm, "end": v(0.37, -0.71) * mm});
            skLineSegment(sketch, "E2785", {"start": v(0.37, -0.71) * mm, "end": v(0.37, -0.7) * mm});
            skLineSegment(sketch, "E2786", {"start": v(0.37, -0.7) * mm, "end": v(0.37, -0.7) * mm});
            skLineSegment(sketch, "E2787", {"start": v(0.37, -0.7) * mm, "end": v(0.38, -0.7) * mm});
            skLineSegment(sketch, "E2788", {"start": v(0.38, -0.7) * mm, "end": v(0.39, -0.71) * mm});
            skLineSegment(sketch, "E2789", {"start": v(0.39, -0.71) * mm, "end": v(0.39, -0.72) * mm});
            skLineSegment(sketch, "E2790", {"start": v(0.39, -0.72) * mm, "end": v(0.39, -0.72) * mm});
            skLineSegment(sketch, "E2791", {"start": v(0.39, -0.72) * mm, "end": v(0.4, -0.72) * mm});
            skLineSegment(sketch, "E2792", {"start": v(0.4, -0.72) * mm, "end": v(0.42, -0.72) * mm});
            skLineSegment(sketch, "E2793", {"start": v(0.42, -0.72) * mm, "end": v(0.45, -0.7) * mm});
            skLineSegment(sketch, "E2794", {"start": v(0.45, -0.7) * mm, "end": v(0.48, -0.68) * mm});
            skLineSegment(sketch, "E2795", {"start": v(0.48, -0.68) * mm, "end": v(0.51, -0.66) * mm});
            skLineSegment(sketch, "E2796", {"start": v(0.51, -0.66) * mm, "end": v(0.54, -0.64) * mm});
            skLineSegment(sketch, "E2797", {"start": v(0.54, -0.64) * mm, "end": v(0.56, -0.62) * mm});
            skLineSegment(sketch, "E2798", {"start": v(0.56, -0.62) * mm, "end": v(0.57, -0.6) * mm});
            skLineSegment(sketch, "E2799", {"start": v(0.57, -0.6) * mm, "end": v(0.57, -0.6) * mm});
            skLineSegment(sketch, "E2800", {"start": v(0.57, -0.6) * mm, "end": v(0.57, -0.59) * mm});
            skLineSegment(sketch, "E2801", {"start": v(0.57, -0.59) * mm, "end": v(0.58, -0.57) * mm});
            skLineSegment(sketch, "E2802", {"start": v(0.58, -0.57) * mm, "end": v(0.6, -0.55) * mm});
            skLineSegment(sketch, "E2803", {"start": v(0.6, -0.55) * mm, "end": v(0.61, -0.53) * mm});
            skLineSegment(sketch, "E2804", {"start": v(0.61, -0.53) * mm, "end": v(0.62, -0.53) * mm});
            skLineSegment(sketch, "E2805", {"start": v(0.62, -0.53) * mm, "end": v(0.62, -0.52) * mm});
            skLineSegment(sketch, "E2806", {"start": v(0.62, -0.52) * mm, "end": v(0.63, -0.5) * mm});
            skLineSegment(sketch, "E2807", {"start": v(0.63, -0.5) * mm, "end": v(0.65, -0.49) * mm});
            skLineSegment(sketch, "E2808", {"start": v(0.65, -0.49) * mm, "end": v(0.66, -0.47) * mm});
            skLineSegment(sketch, "E2809", {"start": v(0.66, -0.47) * mm, "end": v(0.66, -0.45) * mm});
            skLineSegment(sketch, "E2810", {"start": v(0.66, -0.45) * mm, "end": v(0.66, -0.45) * mm});
            skLineSegment(sketch, "E2811", {"start": v(0.66, -0.45) * mm, "end": v(0.67, -0.43) * mm});
            skLineSegment(sketch, "E2812", {"start": v(0.67, -0.43) * mm, "end": v(0.68, -0.41) * mm});
            skLineSegment(sketch, "E2813", {"start": v(0.68, -0.41) * mm, "end": v(0.7, -0.4) * mm});
            skLineSegment(sketch, "E2814", {"start": v(0.7, -0.4) * mm, "end": v(0.72, -0.37) * mm});
            skLineSegment(sketch, "E2815", {"start": v(0.72, -0.37) * mm, "end": v(0.74, -0.35) * mm});
            skLineSegment(sketch, "E2816", {"start": v(0.74, -0.35) * mm, "end": v(0.76, -0.33) * mm});
            skLineSegment(sketch, "E2817", {"start": v(0.76, -0.33) * mm, "end": v(0.79, -0.31) * mm});
            skLineSegment(sketch, "E2818", {"start": v(0.79, -0.31) * mm, "end": v(0.8, -0.3) * mm});
            skLineSegment(sketch, "E2819", {"start": v(0.8, -0.3) * mm, "end": v(0.8, -0.3) * mm});
            skLineSegment(sketch, "E2820", {"start": v(0.8, -0.3) * mm, "end": v(0.81, -0.3) * mm});
            skLineSegment(sketch, "E2821", {"start": v(0.81, -0.3) * mm, "end": v(0.83, -0.3) * mm});
            skLineSegment(sketch, "E2822", {"start": v(0.83, -0.3) * mm, "end": v(0.84, -0.28) * mm});
            skLineSegment(sketch, "E2823", {"start": v(0.84, -0.28) * mm, "end": v(0.84, -0.28) * mm});
            skLineSegment(sketch, "E2824", {"start": v(0.84, -0.28) * mm, "end": v(0.84, -0.27) * mm});
            skLineSegment(sketch, "E2825", {"start": v(0.84, -0.27) * mm, "end": v(0.86, -0.25) * mm});
            skLineSegment(sketch, "E2826", {"start": v(0.86, -0.25) * mm, "end": v(0.89, -0.23) * mm});
            skLineSegment(sketch, "E2827", {"start": v(0.89, -0.23) * mm, "end": v(0.9, -0.22) * mm});
            skLineSegment(sketch, "E2828", {"start": v(0.9, -0.22) * mm, "end": v(0.91, -0.21) * mm});
            skLineSegment(sketch, "E2829", {"start": v(0.91, -0.21) * mm, "end": v(0.96, -0.18) * mm});
            skLineSegment(sketch, "E2830", {"start": v(0.96, -0.18) * mm, "end": v(1, -0.13) * mm});
            skLineSegment(sketch, "E2831", {"start": v(1, -0.13) * mm, "end": v(1.02, -0.06) * mm});
            skLineSegment(sketch, "E2832", {"start": v(1.02, -0.06) * mm, "end": v(1.03, 0) * mm});
            skLineSegment(sketch, "E2833", {"start": v(1.03, 0) * mm, "end": v(1.03, 0.03) * mm});
            skLineSegment(sketch, "E2834", {"start": v(1.03, 0.03) * mm, "end": v(1.03, 0.05) * mm});
            skLineSegment(sketch, "E2835", {"start": v(1.03, 0.05) * mm, "end": v(1.03, 0.13) * mm});
            skLineSegment(sketch, "E2836", {"start": v(1.03, 0.13) * mm, "end": v(1, 0.22) * mm});
            skLineSegment(sketch, "E2837", {"start": v(1, 0.22) * mm, "end": v(0.95, 0.29) * mm});
            skLineSegment(sketch, "E2838", {"start": v(0.95, 0.29) * mm, "end": v(0.88, 0.33) * mm});
            skLineSegment(sketch, "E2839", {"start": v(0.88, 0.33) * mm, "end": v(0.8, 0.35) * mm});
            skLineSegment(sketch, "E2840", {"start": v(0.8, 0.35) * mm, "end": v(0.72, 0.34) * mm});
            skLineSegment(sketch, "E2841", {"start": v(0.72, 0.34) * mm, "end": v(0.63, 0.31) * mm});
            skLineSegment(sketch, "E2842", {"start": v(0.63, 0.31) * mm, "end": v(0.56, 0.26) * mm});
            skLineSegment(sketch, "E2843", {"start": v(0.56, 0.26) * mm, "end": v(0.54, 0.25) * mm});
            skLineSegment(sketch, "E2844", {"start": v(0.54, 0.25) * mm, "end": v(0.53, 0.24) * mm});
            skLineSegment(sketch, "E2845", {"start": v(0.53, 0.24) * mm, "end": v(0.5, 0.22) * mm});
            skLineSegment(sketch, "E2846", {"start": v(0.5, 0.22) * mm, "end": v(0.47, 0.2) * mm});
            skLineSegment(sketch, "E2847", {"start": v(0.47, 0.2) * mm, "end": v(0.42, 0.19) * mm});
            skLineSegment(sketch, "E2848", {"start": v(0.42, 0.19) * mm, "end": v(0.37, 0.18) * mm});
            skLineSegment(sketch, "E2849", {"start": v(0.37, 0.18) * mm, "end": v(0.36, 0.18) * mm});
            skLineSegment(sketch, "E2850", {"start": v(0.36, 0.18) * mm, "end": v(0.35, 0.17) * mm});
            skLineSegment(sketch, "E2851", {"start": v(0.35, 0.17) * mm, "end": v(0.32, 0.17) * mm});
            skLineSegment(sketch, "E2852", {"start": v(0.32, 0.17) * mm, "end": v(0.3, 0.17) * mm});
            skLineSegment(sketch, "E2853", {"start": v(0.3, 0.17) * mm, "end": v(0.28, 0.18) * mm});
            skLineSegment(sketch, "E2854", {"start": v(0.28, 0.18) * mm, "end": v(0.27, 0.18) * mm});
            skLineSegment(sketch, "E2855", {"start": v(0.27, 0.18) * mm, "end": v(0.27, 0.18) * mm});
            skLineSegment(sketch, "E2856", {"start": v(0.27, 0.18) * mm, "end": v(0.27, 0.19) * mm});
            skLineSegment(sketch, "E2857", {"start": v(0.27, 0.19) * mm, "end": v(0.27, 0.2) * mm});
            skLineSegment(sketch, "E2858", {"start": v(0.27, 0.2) * mm, "end": v(0.25, 0.2) * mm});
            skLineSegment(sketch, "E2859", {"start": v(0.25, 0.2) * mm, "end": v(0.22, 0.22) * mm});
            skLineSegment(sketch, "E2860", {"start": v(0.22, 0.22) * mm, "end": v(0.2, 0.22) * mm});
            skLineSegment(sketch, "E2861", {"start": v(0.2, 0.22) * mm, "end": v(0.2, 0.22) * mm});
            skLineSegment(sketch, "E2862", {"start": v(0.2, 0.22) * mm, "end": v(0.18, 0.22) * mm});
            skLineSegment(sketch, "E2863", {"start": v(0.18, 0.22) * mm, "end": v(0.18, 0.23) * mm});
            skLineSegment(sketch, "E2864", {"start": v(0.18, 0.23) * mm, "end": v(0.18, 0.23) * mm});
            skLineSegment(sketch, "E2865", {"start": v(0.18, 0.23) * mm, "end": v(0.19, 0.24) * mm});
            skLineSegment(sketch, "E2866", {"start": v(0.19, 0.24) * mm, "end": v(0.18, 0.24) * mm});
            skLineSegment(sketch, "E2867", {"start": v(0.18, 0.24) * mm, "end": v(0.18, 0.24) * mm});
            skLineSegment(sketch, "E2868", {"start": v(0.18, 0.24) * mm, "end": v(0.16, 0.26) * mm});
            skLineSegment(sketch, "E2869", {"start": v(0.16, 0.26) * mm, "end": v(0.13, 0.28) * mm});
            skLineSegment(sketch, "E2870", {"start": v(0.13, 0.28) * mm, "end": v(0.13, 0.28) * mm});
            skLineSegment(sketch, "E2871", {"start": v(0.13, 0.28) * mm, "end": v(0.1, 0.3) * mm});
            skLineSegment(sketch, "E2872", {"start": v(0.1, 0.3) * mm, "end": v(0.05, 0.35) * mm});
            skLineSegment(sketch, "E2873", {"start": v(0.05, 0.35) * mm, "end": v(0, 0.4) * mm});
            skLineSegment(sketch, "E2874", {"start": v(0, 0.4) * mm, "end": v(-0.05, 0.43) * mm});
            skLineSegment(sketch, "E2875", {"start": v(-0.05, 0.43) * mm, "end": v(-0.09, 0.44) * mm});
            skLineSegment(sketch, "E2876", {"start": v(-0.09, 0.44) * mm, "end": v(-0.1, 0.45) * mm});
            skLineSegment(sketch, "E2877", {"start": v(-0.1, 0.45) * mm, "end": v(-0.11, 0.45) * mm});
            skLineSegment(sketch, "E2878", {"start": v(-0.11, 0.45) * mm, "end": v(-0.14, 0.46) * mm});
            skLineSegment(sketch, "E2879", {"start": v(-0.14, 0.46) * mm, "end": v(-0.17, 0.47) * mm});
            skLineSegment(sketch, "E2880", {"start": v(-0.17, 0.47) * mm, "end": v(-0.2, 0.47) * mm});
            skLineSegment(sketch, "E2881", {"start": v(-0.2, 0.47) * mm, "end": v(-0.22, 0.46) * mm});
            skLineSegment(sketch, "E2882", {"start": v(-0.22, 0.46) * mm, "end": v(-0.23, 0.46) * mm});
            skLineSegment(sketch, "E2883", {"start": v(-0.1, 0.37) * mm, "end": v(-0.1, 0.37) * mm});
            skLineSegment(sketch, "E2884", {"start": v(-0.1, 0.37) * mm, "end": v(-0.11, 0.36) * mm});
            skLineSegment(sketch, "E2885", {"start": v(-0.11, 0.36) * mm, "end": v(-0.12, 0.34) * mm});
            skLineSegment(sketch, "E2886", {"start": v(-0.12, 0.34) * mm, "end": v(-0.13, 0.33) * mm});
            skLineSegment(sketch, "E2887", {"start": v(-0.13, 0.33) * mm, "end": v(-0.13, 0.33) * mm});
            skLineSegment(sketch, "E2888", {"start": v(-0.13, 0.33) * mm, "end": v(-0.14, 0.32) * mm});
            skLineSegment(sketch, "E2889", {"start": v(-0.14, 0.32) * mm, "end": v(-0.15, 0.32) * mm});
            skLineSegment(sketch, "E2890", {"start": v(-0.15, 0.32) * mm, "end": v(-0.15, 0.32) * mm});
            skLineSegment(sketch, "E2891", {"start": v(-0.15, 0.32) * mm, "end": v(-0.16, 0.33) * mm});
            skLineSegment(sketch, "E2892", {"start": v(-0.16, 0.33) * mm, "end": v(-0.16, 0.33) * mm});
            skLineSegment(sketch, "E2893", {"start": v(-0.16, 0.33) * mm, "end": v(-0.16, 0.34) * mm});
            skLineSegment(sketch, "E2894", {"start": v(-0.16, 0.34) * mm, "end": v(-0.16, 0.35) * mm});
            skLineSegment(sketch, "E2895", {"start": v(-0.16, 0.35) * mm, "end": v(-0.17, 0.36) * mm});
            skLineSegment(sketch, "E2896", {"start": v(-0.17, 0.36) * mm, "end": v(-0.17, 0.36) * mm});
            skLineSegment(sketch, "E2897", {"start": v(-0.17, 0.36) * mm, "end": v(-0.17, 0.34) * mm});
            skLineSegment(sketch, "E2898", {"start": v(-0.17, 0.34) * mm, "end": v(-0.17, 0.33) * mm});
            skLineSegment(sketch, "E2899", {"start": v(-0.17, 0.33) * mm, "end": v(-0.17, 0.33) * mm});
            skLineSegment(sketch, "E2900", {"start": v(-0.17, 0.33) * mm, "end": v(-0.17, 0.32) * mm});
            skLineSegment(sketch, "E2901", {"start": v(-0.17, 0.32) * mm, "end": v(-0.18, 0.3) * mm});
            skLineSegment(sketch, "E2902", {"start": v(-0.18, 0.3) * mm, "end": v(-0.2, 0.29) * mm});
            skLineSegment(sketch, "E2903", {"start": v(-0.2, 0.29) * mm, "end": v(-0.2, 0.27) * mm});
            skLineSegment(sketch, "E2904", {"start": v(-0.2, 0.27) * mm, "end": v(-0.23, 0.26) * mm});
            skLineSegment(sketch, "E2905", {"start": v(-0.23, 0.26) * mm, "end": v(-0.24, 0.25) * mm});
            skLineSegment(sketch, "E2906", {"start": v(-0.24, 0.25) * mm, "end": v(-0.26, 0.25) * mm});
            skLineSegment(sketch, "E2907", {"start": v(-0.26, 0.25) * mm, "end": v(-0.27, 0.25) * mm});
            skLineSegment(sketch, "E2908", {"start": v(-0.27, 0.25) * mm, "end": v(-0.27, 0.25) * mm});
            skLineSegment(sketch, "E2909", {"start": v(-0.27, 0.25) * mm, "end": v(-0.27, 0.26) * mm});
            skLineSegment(sketch, "E2910", {"start": v(-0.27, 0.26) * mm, "end": v(-0.28, 0.27) * mm});
            skLineSegment(sketch, "E2911", {"start": v(-0.28, 0.27) * mm, "end": v(-0.28, 0.31) * mm});
            skLineSegment(sketch, "E2912", {"start": v(-0.28, 0.31) * mm, "end": v(-0.27, 0.35) * mm});
            skLineSegment(sketch, "E2913", {"start": v(-0.27, 0.35) * mm, "end": v(-0.26, 0.37) * mm});
            skLineSegment(sketch, "E2914", {"start": v(-0.26, 0.37) * mm, "end": v(-0.25, 0.37) * mm});
            skLineSegment(sketch, "E2915", {"start": v(-0.25, 0.37) * mm, "end": v(-0.24, 0.38) * mm});
            skLineSegment(sketch, "E2916", {"start": v(-0.24, 0.38) * mm, "end": v(-0.22, 0.38) * mm});
            skLineSegment(sketch, "E2917", {"start": v(-0.22, 0.38) * mm, "end": v(-0.17, 0.38) * mm});
            skLineSegment(sketch, "E2918", {"start": v(-0.17, 0.38) * mm, "end": v(-0.13, 0.38) * mm});
            skLineSegment(sketch, "E2919", {"start": v(-0.13, 0.38) * mm, "end": v(-0.11, 0.38) * mm});
            skLineSegment(sketch, "E2920", {"start": v(-0.11, 0.38) * mm, "end": v(-0.1, 0.37) * mm});
            skLineSegment(sketch, "E2921", {"start": v(-0.01, 0.32) * mm, "end": v(0.04, 0.26) * mm});
            skLineSegment(sketch, "E2922", {"start": v(0.04, 0.26) * mm, "end": v(0, 0.23) * mm});
            skLineSegment(sketch, "E2923", {"start": v(0, 0.23) * mm, "end": v(-0.01, 0.22) * mm});
            skLineSegment(sketch, "E2924", {"start": v(-0.01, 0.22) * mm, "end": v(-0.06, 0.2) * mm});
            skLineSegment(sketch, "E2925", {"start": v(-0.06, 0.2) * mm, "end": v(-0.13, 0.18) * mm});
            skLineSegment(sketch, "E2926", {"start": v(-0.13, 0.18) * mm, "end": v(-0.19, 0.17) * mm});
            skLineSegment(sketch, "E2927", {"start": v(-0.19, 0.17) * mm, "end": v(-0.23, 0.18) * mm});
            skLineSegment(sketch, "E2928", {"start": v(-0.23, 0.18) * mm, "end": v(-0.24, 0.19) * mm});
            skLineSegment(sketch, "E2929", {"start": v(-0.24, 0.19) * mm, "end": v(-0.24, 0.2) * mm});
            skLineSegment(sketch, "E2930", {"start": v(-0.24, 0.2) * mm, "end": v(-0.26, 0.2) * mm});
            skLineSegment(sketch, "E2931", {"start": v(-0.26, 0.2) * mm, "end": v(-0.26, 0.22) * mm});
            skLineSegment(sketch, "E2932", {"start": v(-0.26, 0.22) * mm, "end": v(-0.25, 0.23) * mm});
            skLineSegment(sketch, "E2933", {"start": v(-0.25, 0.23) * mm, "end": v(-0.22, 0.24) * mm});
            skLineSegment(sketch, "E2934", {"start": v(-0.22, 0.24) * mm, "end": v(-0.22, 0.25) * mm});
            skLineSegment(sketch, "E2935", {"start": v(-0.22, 0.25) * mm, "end": v(-0.2, 0.25) * mm});
            skLineSegment(sketch, "E2936", {"start": v(-0.2, 0.25) * mm, "end": v(-0.17, 0.27) * mm});
            skLineSegment(sketch, "E2937", {"start": v(-0.17, 0.27) * mm, "end": v(-0.13, 0.3) * mm});
            skLineSegment(sketch, "E2938", {"start": v(-0.13, 0.3) * mm, "end": v(-0.1, 0.33) * mm});
            skLineSegment(sketch, "E2939", {"start": v(-0.1, 0.33) * mm, "end": v(-0.09, 0.35) * mm});
            skLineSegment(sketch, "E2940", {"start": v(-0.09, 0.35) * mm, "end": v(-0.09, 0.36) * mm});
            skLineSegment(sketch, "E2941", {"start": v(-0.09, 0.36) * mm, "end": v(-0.09, 0.36) * mm});
            skLineSegment(sketch, "E2942", {"start": v(-0.09, 0.36) * mm, "end": v(-0.08, 0.37) * mm});
            skLineSegment(sketch, "E2943", {"start": v(-0.08, 0.37) * mm, "end": v(-0.07, 0.37) * mm});
            skLineSegment(sketch, "E2944", {"start": v(-0.07, 0.37) * mm, "end": v(-0.05, 0.35) * mm});
            skLineSegment(sketch, "E2945", {"start": v(-0.05, 0.35) * mm, "end": v(-0.02, 0.32) * mm});
            skLineSegment(sketch, "E2946", {"start": v(-0.02, 0.32) * mm, "end": v(-0.01, 0.32) * mm});
            skLineSegment(sketch, "E2947", {"start": v(-1, 0.32) * mm, "end": v(-1, 0.31) * mm});
            skLineSegment(sketch, "E2948", {"start": v(-1, 0.31) * mm, "end": v(-0.97, 0.3) * mm});
            skLineSegment(sketch, "E2949", {"start": v(-0.97, 0.3) * mm, "end": v(-0.96, 0.27) * mm});
            skLineSegment(sketch, "E2950", {"start": v(-0.96, 0.27) * mm, "end": v(-0.96, 0.26) * mm});
            skLineSegment(sketch, "E2951", {"start": v(-0.96, 0.26) * mm, "end": v(-0.97, 0.25) * mm});
            skLineSegment(sketch, "E2952", {"start": v(-0.97, 0.25) * mm, "end": v(-0.98, 0.26) * mm});
            skLineSegment(sketch, "E2953", {"start": v(-0.98, 0.26) * mm, "end": v(-0.98, 0.26) * mm});
            skLineSegment(sketch, "E2954", {"start": v(-0.98, 0.26) * mm, "end": v(-1, 0.25) * mm});
            skLineSegment(sketch, "E2955", {"start": v(-1, 0.25) * mm, "end": v(-1, 0.25) * mm});
            skLineSegment(sketch, "E2956", {"start": v(-1, 0.25) * mm, "end": v(-1, 0.24) * mm});
            skLineSegment(sketch, "E2957", {"start": v(-1, 0.24) * mm, "end": v(-1, 0.23) * mm});
            skLineSegment(sketch, "E2958", {"start": v(-1, 0.23) * mm, "end": v(-1, 0.23) * mm});
            skLineSegment(sketch, "E2959", {"start": v(-1, 0.23) * mm, "end": v(-1.01, 0.23) * mm});
            skLineSegment(sketch, "E2960", {"start": v(-1.01, 0.23) * mm, "end": v(-1.02, 0.23) * mm});
            skLineSegment(sketch, "E2961", {"start": v(-1.02, 0.23) * mm, "end": v(-1.05, 0.23) * mm});
            skLineSegment(sketch, "E2962", {"start": v(-1.05, 0.23) * mm, "end": v(-1.1, 0.22) * mm});
            skLineSegment(sketch, "E2963", {"start": v(-1.1, 0.22) * mm, "end": v(-1.11, 0.22) * mm});
            skLineSegment(sketch, "E2964", {"start": v(-1.11, 0.22) * mm, "end": v(-1.12, 0.22) * mm});
            skLineSegment(sketch, "E2965", {"start": v(-1.12, 0.22) * mm, "end": v(-1.15, 0.22) * mm});
            skLineSegment(sketch, "E2966", {"start": v(-1.15, 0.22) * mm, "end": v(-1.17, 0.22) * mm});
            skLineSegment(sketch, "E2967", {"start": v(-1.17, 0.22) * mm, "end": v(-1.18, 0.23) * mm});
            skLineSegment(sketch, "E2968", {"start": v(-1.18, 0.23) * mm, "end": v(-1.18, 0.24) * mm});
            skLineSegment(sketch, "E2969", {"start": v(-1.18, 0.24) * mm, "end": v(-1.18, 0.25) * mm});
            skLineSegment(sketch, "E2970", {"start": v(-1.18, 0.25) * mm, "end": v(-1.18, 0.26) * mm});
            skLineSegment(sketch, "E2971", {"start": v(-1.18, 0.26) * mm, "end": v(-1.17, 0.3) * mm});
            skLineSegment(sketch, "E2972", {"start": v(-1.17, 0.3) * mm, "end": v(-1.14, 0.34) * mm});
            skLineSegment(sketch, "E2973", {"start": v(-1.14, 0.34) * mm, "end": v(-1.09, 0.35) * mm});
            skLineSegment(sketch, "E2974", {"start": v(-1.09, 0.35) * mm, "end": v(-1.03, 0.33) * mm});
            skLineSegment(sketch, "E2975", {"start": v(-1.03, 0.33) * mm, "end": v(-1, 0.32) * mm});
            skLineSegment(sketch, "E2976", {"start": v(0.78, 0.29) * mm, "end": v(0.78, 0.28) * mm});
            skLineSegment(sketch, "E2977", {"start": v(0.78, 0.28) * mm, "end": v(0.77, 0.23) * mm});
            skLineSegment(sketch, "E2978", {"start": v(0.77, 0.23) * mm, "end": v(0.76, 0.16) * mm});
            skLineSegment(sketch, "E2979", {"start": v(0.76, 0.16) * mm, "end": v(0.75, 0.07) * mm});
            skLineSegment(sketch, "E2980", {"start": v(0.75, 0.07) * mm, "end": v(0.75, 0) * mm});
            skLineSegment(sketch, "E2981", {"start": v(0.75, 0) * mm, "end": v(0.75, -0.03) * mm});
            skLineSegment(sketch, "E2982", {"start": v(0.75, -0.03) * mm, "end": v(0.75, -0.05) * mm});
            skLineSegment(sketch, "E2983", {"start": v(0.75, -0.05) * mm, "end": v(0.76, -0.1) * mm});
            skLineSegment(sketch, "E2984", {"start": v(0.76, -0.1) * mm, "end": v(0.75, -0.14) * mm});
            skLineSegment(sketch, "E2985", {"start": v(0.75, -0.14) * mm, "end": v(0.75, -0.14) * mm});
            skLineSegment(sketch, "E2986", {"start": v(0.75, -0.14) * mm, "end": v(0.74, -0.13) * mm});
            skLineSegment(sketch, "E2987", {"start": v(0.74, -0.13) * mm, "end": v(0.74, -0.13) * mm});
            skLineSegment(sketch, "E2988", {"start": v(0.74, -0.13) * mm, "end": v(0.72, -0.1) * mm});
            skLineSegment(sketch, "E2989", {"start": v(0.72, -0.1) * mm, "end": v(0.7, -0.02) * mm});
            skLineSegment(sketch, "E2990", {"start": v(0.7, -0.02) * mm, "end": v(0.67, 0.1) * mm});
            skLineSegment(sketch, "E2991", {"start": v(0.67, 0.1) * mm, "end": v(0.67, 0.2) * mm});
            skLineSegment(sketch, "E2992", {"start": v(0.67, 0.2) * mm, "end": v(0.67, 0.26) * mm});
            skLineSegment(sketch, "E2993", {"start": v(0.67, 0.26) * mm, "end": v(0.68, 0.27) * mm});
            skLineSegment(sketch, "E2994", {"start": v(0.68, 0.27) * mm, "end": v(0.68, 0.28) * mm});
            skLineSegment(sketch, "E2995", {"start": v(0.68, 0.28) * mm, "end": v(0.7, 0.29) * mm});
            skLineSegment(sketch, "E2996", {"start": v(0.7, 0.29) * mm, "end": v(0.71, 0.3) * mm});
            skLineSegment(sketch, "E2997", {"start": v(0.71, 0.3) * mm, "end": v(0.73, 0.3) * mm});
            skLineSegment(sketch, "E2998", {"start": v(0.73, 0.3) * mm, "end": v(0.75, 0.31) * mm});
            skLineSegment(sketch, "E2999", {"start": v(0.75, 0.31) * mm, "end": v(0.76, 0.31) * mm});
            skLineSegment(sketch, "E3000", {"start": v(0.76, 0.31) * mm, "end": v(0.78, 0.3) * mm});
            skLineSegment(sketch, "E3001", {"start": v(0.78, 0.3) * mm, "end": v(0.78, 0.3) * mm});
            skLineSegment(sketch, "E3002", {"start": v(0.78, 0.3) * mm, "end": v(0.78, 0.29) * mm});
            skLineSegment(sketch, "E3003", {"start": v(-0.85, 0.2) * mm, "end": v(-0.85, 0.2) * mm});
            skLineSegment(sketch, "E3004", {"start": v(-0.85, 0.2) * mm, "end": v(-0.87, 0.2) * mm});
            skLineSegment(sketch, "E3005", {"start": v(-0.87, 0.2) * mm, "end": v(-0.89, 0.2) * mm});
            skLineSegment(sketch, "E3006", {"start": v(-0.89, 0.2) * mm, "end": v(-0.9, 0.2) * mm});
            skLineSegment(sketch, "E3007", {"start": v(-0.9, 0.2) * mm, "end": v(-0.9, 0.2) * mm});
            skLineSegment(sketch, "E3008", {"start": v(-0.9, 0.2) * mm, "end": v(-0.92, 0.21) * mm});
            skLineSegment(sketch, "E3009", {"start": v(-0.92, 0.21) * mm, "end": v(-0.94, 0.22) * mm});
            skLineSegment(sketch, "E3010", {"start": v(-0.94, 0.22) * mm, "end": v(-0.95, 0.22) * mm});
            skLineSegment(sketch, "E3011", {"start": v(-0.95, 0.22) * mm, "end": v(-0.95, 0.22) * mm});
            skLineSegment(sketch, "E3012", {"start": v(-0.95, 0.22) * mm, "end": v(-0.96, 0.22) * mm});
            skLineSegment(sketch, "E3013", {"start": v(-0.96, 0.22) * mm, "end": v(-0.97, 0.22) * mm});
            skLineSegment(sketch, "E3014", {"start": v(-0.97, 0.22) * mm, "end": v(-0.96, 0.23) * mm});
            skLineSegment(sketch, "E3015", {"start": v(-0.96, 0.23) * mm, "end": v(-0.95, 0.24) * mm});
            skLineSegment(sketch, "E3016", {"start": v(-0.95, 0.24) * mm, "end": v(-0.95, 0.24) * mm});
            skLineSegment(sketch, "E3017", {"start": v(-0.95, 0.24) * mm, "end": v(-0.94, 0.25) * mm});
            skLineSegment(sketch, "E3018", {"start": v(-0.94, 0.25) * mm, "end": v(-0.93, 0.26) * mm});
            skLineSegment(sketch, "E3019", {"start": v(-0.93, 0.26) * mm, "end": v(-0.91, 0.26) * mm});
            skLineSegment(sketch, "E3020", {"start": v(-0.91, 0.26) * mm, "end": v(-0.9, 0.25) * mm});
            skLineSegment(sketch, "E3021", {"start": v(-0.9, 0.25) * mm, "end": v(-0.88, 0.24) * mm});
            skLineSegment(sketch, "E3022", {"start": v(-0.88, 0.24) * mm, "end": v(-0.87, 0.23) * mm});
            skLineSegment(sketch, "E3023", {"start": v(-0.87, 0.23) * mm, "end": v(-0.87, 0.23) * mm});
            skLineSegment(sketch, "E3024", {"start": v(-0.87, 0.23) * mm, "end": v(-0.85, 0.2) * mm});
            skLineSegment(sketch, "E3025", {"start": v(0.93, 0.22) * mm, "end": v(0.92, 0.22) * mm});
            skLineSegment(sketch, "E3026", {"start": v(0.92, 0.22) * mm, "end": v(0.92, 0.2) * mm});
            skLineSegment(sketch, "E3027", {"start": v(0.92, 0.2) * mm, "end": v(0.92, 0.2) * mm});
            skLineSegment(sketch, "E3028", {"start": v(0.92, 0.2) * mm, "end": v(0.93, 0.2) * mm});
            skLineSegment(sketch, "E3029", {"start": v(0.93, 0.2) * mm, "end": v(0.94, 0.2) * mm});
            skLineSegment(sketch, "E3030", {"start": v(0.94, 0.2) * mm, "end": v(0.95, 0.22) * mm});
            skLineSegment(sketch, "E3031", {"start": v(0.95, 0.22) * mm, "end": v(0.95, 0.22) * mm});
            skLineSegment(sketch, "E3032", {"start": v(0.95, 0.22) * mm, "end": v(0.96, 0.22) * mm});
            skLineSegment(sketch, "E3033", {"start": v(0.96, 0.22) * mm, "end": v(0.97, 0.22) * mm});
            skLineSegment(sketch, "E3034", {"start": v(0.97, 0.22) * mm, "end": v(0.98, 0.22) * mm});
            skLineSegment(sketch, "E3035", {"start": v(0.98, 0.22) * mm, "end": v(0.98, 0.21) * mm});
            skLineSegment(sketch, "E3036", {"start": v(0.98, 0.21) * mm, "end": v(1, 0.2) * mm});
            skLineSegment(sketch, "E3037", {"start": v(1, 0.2) * mm, "end": v(1, 0.18) * mm});
            skLineSegment(sketch, "E3038", {"start": v(1, 0.18) * mm, "end": v(0.99, 0.16) * mm});
            skLineSegment(sketch, "E3039", {"start": v(0.99, 0.16) * mm, "end": v(0.97, 0.15) * mm});
            skLineSegment(sketch, "E3040", {"start": v(0.97, 0.15) * mm, "end": v(0.97, 0.15) * mm});
            skLineSegment(sketch, "E3041", {"start": v(0.97, 0.15) * mm, "end": v(0.96, 0.14) * mm});
            skLineSegment(sketch, "E3042", {"start": v(0.96, 0.14) * mm, "end": v(0.94, 0.13) * mm});
            skLineSegment(sketch, "E3043", {"start": v(0.94, 0.13) * mm, "end": v(0.91, 0.1) * mm});
            skLineSegment(sketch, "E3044", {"start": v(0.91, 0.1) * mm, "end": v(0.9, 0.05) * mm});
            skLineSegment(sketch, "E3045", {"start": v(0.9, 0.05) * mm, "end": v(0.89, 0.03) * mm});
            skLineSegment(sketch, "E3046", {"start": v(0.89, 0.03) * mm, "end": v(0.89, 0.02) * mm});
            skLineSegment(sketch, "E3047", {"start": v(0.89, 0.02) * mm, "end": v(0.89, 0.01) * mm});
            skLineSegment(sketch, "E3048", {"start": v(0.89, 0.01) * mm, "end": v(0.88, 0) * mm});
            skLineSegment(sketch, "E3049", {"start": v(0.88, 0) * mm, "end": v(0.86, -0.03) * mm});
            skLineSegment(sketch, "E3050", {"start": v(0.86, -0.03) * mm, "end": v(0.86, -0.03) * mm});
            skLineSegment(sketch, "E3051", {"start": v(0.86, -0.03) * mm, "end": v(0.86, -0.04) * mm});
            skLineSegment(sketch, "E3052", {"start": v(0.86, -0.04) * mm, "end": v(0.84, -0.08) * mm});
            skLineSegment(sketch, "E3053", {"start": v(0.84, -0.08) * mm, "end": v(0.83, -0.12) * mm});
            skLineSegment(sketch, "E3054", {"start": v(0.83, -0.12) * mm, "end": v(0.82, -0.13) * mm});
            skLineSegment(sketch, "E3055", {"start": v(0.82, -0.13) * mm, "end": v(0.82, -0.14) * mm});
            skLineSegment(sketch, "E3056", {"start": v(0.82, -0.14) * mm, "end": v(0.82, -0.17) * mm});
            skLineSegment(sketch, "E3057", {"start": v(0.82, -0.17) * mm, "end": v(0.81, -0.2) * mm});
            skLineSegment(sketch, "E3058", {"start": v(0.81, -0.2) * mm, "end": v(0.8, -0.2) * mm});
            skLineSegment(sketch, "E3059", {"start": v(0.8, -0.2) * mm, "end": v(0.8, -0.2) * mm});
            skLineSegment(sketch, "E3060", {"start": v(0.8, -0.2) * mm, "end": v(0.8, -0.19) * mm});
            skLineSegment(sketch, "E3061", {"start": v(0.8, -0.19) * mm, "end": v(0.8, -0.19) * mm});
            skLineSegment(sketch, "E3062", {"start": v(0.8, -0.19) * mm, "end": v(0.8, -0.18) * mm});
            skLineSegment(sketch, "E3063", {"start": v(0.8, -0.18) * mm, "end": v(0.78, -0.18) * mm});
            skLineSegment(sketch, "E3064", {"start": v(0.78, -0.18) * mm, "end": v(0.77, -0.18) * mm});
            skLineSegment(sketch, "E3065", {"start": v(0.77, -0.18) * mm, "end": v(0.77, -0.18) * mm});
            skLineSegment(sketch, "E3066", {"start": v(0.77, -0.18) * mm, "end": v(0.76, -0.18) * mm});
            skLineSegment(sketch, "E3067", {"start": v(0.76, -0.18) * mm, "end": v(0.75, -0.18) * mm});
            skLineSegment(sketch, "E3068", {"start": v(0.75, -0.18) * mm, "end": v(0.76, -0.18) * mm});
            skLineSegment(sketch, "E3069", {"start": v(0.76, -0.18) * mm, "end": v(0.77, -0.16) * mm});
            skLineSegment(sketch, "E3070", {"start": v(0.77, -0.16) * mm, "end": v(0.77, -0.16) * mm});
            skLineSegment(sketch, "E3071", {"start": v(0.77, -0.16) * mm, "end": v(0.8, -0.12) * mm});
            skLineSegment(sketch, "E3072", {"start": v(0.8, -0.12) * mm, "end": v(0.8, -0.07) * mm});
            skLineSegment(sketch, "E3073", {"start": v(0.8, -0.07) * mm, "end": v(0.8, -0.06) * mm});
            skLineSegment(sketch, "E3074", {"start": v(0.8, -0.06) * mm, "end": v(0.8, -0.05) * mm});
            skLineSegment(sketch, "E3075", {"start": v(0.8, -0.05) * mm, "end": v(0.8, 0) * mm});
            skLineSegment(sketch, "E3076", {"start": v(0.8, 0) * mm, "end": v(0.81, 0.02) * mm});
            skLineSegment(sketch, "E3077", {"start": v(0.81, 0.02) * mm, "end": v(0.81, 0.02) * mm});
            skLineSegment(sketch, "E3078", {"start": v(0.81, 0.02) * mm, "end": v(0.82, 0.04) * mm});
            skLineSegment(sketch, "E3079", {"start": v(0.82, 0.04) * mm, "end": v(0.83, 0.07) * mm});
            skLineSegment(sketch, "E3080", {"start": v(0.83, 0.07) * mm, "end": v(0.83, 0.07) * mm});
            skLineSegment(sketch, "E3081", {"start": v(0.83, 0.07) * mm, "end": v(0.83, 0.09) * mm});
            skLineSegment(sketch, "E3082", {"start": v(0.83, 0.09) * mm, "end": v(0.85, 0.16) * mm});
            skLineSegment(sketch, "E3083", {"start": v(0.85, 0.16) * mm, "end": v(0.89, 0.22) * mm});
            skLineSegment(sketch, "E3084", {"start": v(0.89, 0.22) * mm, "end": v(0.9, 0.23) * mm});
            skLineSegment(sketch, "E3085", {"start": v(0.9, 0.23) * mm, "end": v(0.9, 0.24) * mm});
            skLineSegment(sketch, "E3086", {"start": v(0.9, 0.24) * mm, "end": v(0.92, 0.25) * mm});
            skLineSegment(sketch, "E3087", {"start": v(0.92, 0.25) * mm, "end": v(0.94, 0.26) * mm});
            skLineSegment(sketch, "E3088", {"start": v(0.94, 0.26) * mm, "end": v(0.94, 0.25) * mm});
            skLineSegment(sketch, "E3089", {"start": v(0.94, 0.25) * mm, "end": v(0.93, 0.23) * mm});
            skLineSegment(sketch, "E3090", {"start": v(0.93, 0.23) * mm, "end": v(0.93, 0.22) * mm});
            skLineSegment(sketch, "E3091", {"start": v(0.1, 0.21) * mm, "end": v(0.1, 0.2) * mm});
            skLineSegment(sketch, "E3092", {"start": v(0.1, 0.2) * mm, "end": v(0.13, 0.19) * mm});
            skLineSegment(sketch, "E3093", {"start": v(0.13, 0.19) * mm, "end": v(0.13, 0.17) * mm});
            skLineSegment(sketch, "E3094", {"start": v(0.13, 0.17) * mm, "end": v(0.12, 0.15) * mm});
            skLineSegment(sketch, "E3095", {"start": v(0.12, 0.15) * mm, "end": v(0.1, 0.13) * mm});
            skLineSegment(sketch, "E3096", {"start": v(0.1, 0.13) * mm, "end": v(0.1, 0.12) * mm});
            skLineSegment(sketch, "E3097", {"start": v(0.1, 0.12) * mm, "end": v(0.1, 0.12) * mm});
            skLineSegment(sketch, "E3098", {"start": v(0.1, 0.12) * mm, "end": v(0.07, 0.1) * mm});
            skLineSegment(sketch, "E3099", {"start": v(0.07, 0.1) * mm, "end": v(0.03, 0.1) * mm});
            skLineSegment(sketch, "E3100", {"start": v(0.03, 0.1) * mm, "end": v(0, 0.1) * mm});
            skLineSegment(sketch, "E3101", {"start": v(0, 0.1) * mm, "end": v(-0.02, 0.1) * mm});
            skLineSegment(sketch, "E3102", {"start": v(-0.02, 0.1) * mm, "end": v(-0.03, 0.11) * mm});
            skLineSegment(sketch, "E3103", {"start": v(-0.03, 0.11) * mm, "end": v(-0.03, 0.11) * mm});
            skLineSegment(sketch, "E3104", {"start": v(-0.03, 0.11) * mm, "end": v(-0.04, 0.12) * mm});
            skLineSegment(sketch, "E3105", {"start": v(-0.04, 0.12) * mm, "end": v(-0.06, 0.11) * mm});
            skLineSegment(sketch, "E3106", {"start": v(-0.06, 0.11) * mm, "end": v(-0.06, 0.11) * mm});
            skLineSegment(sketch, "E3107", {"start": v(-0.06, 0.11) * mm, "end": v(-0.09, 0.11) * mm});
            skLineSegment(sketch, "E3108", {"start": v(-0.09, 0.11) * mm, "end": v(-0.12, 0.12) * mm});
            skLineSegment(sketch, "E3109", {"start": v(-0.12, 0.12) * mm, "end": v(-0.13, 0.12) * mm});
            skLineSegment(sketch, "E3110", {"start": v(-0.13, 0.12) * mm, "end": v(-0.2, 0.14) * mm});
            skLineSegment(sketch, "E3111", {"start": v(-0.2, 0.14) * mm, "end": v(-0.14, 0.15) * mm});
            skLineSegment(sketch, "E3112", {"start": v(-0.14, 0.15) * mm, "end": v(-0.13, 0.15) * mm});
            skLineSegment(sketch, "E3113", {"start": v(-0.13, 0.15) * mm, "end": v(-0.08, 0.15) * mm});
            skLineSegment(sketch, "E3114", {"start": v(-0.08, 0.15) * mm, "end": v(-0.04, 0.14) * mm});
            skLineSegment(sketch, "E3115", {"start": v(-0.04, 0.14) * mm, "end": v(-0.03, 0.14) * mm});
            skLineSegment(sketch, "E3116", {"start": v(-0.03, 0.14) * mm, "end": v(-0.02, 0.14) * mm});
            skLineSegment(sketch, "E3117", {"start": v(-0.02, 0.14) * mm, "end": v(0.01, 0.13) * mm});
            skLineSegment(sketch, "E3118", {"start": v(0.01, 0.13) * mm, "end": v(0.03, 0.13) * mm});
            skLineSegment(sketch, "E3119", {"start": v(0.03, 0.13) * mm, "end": v(0.03, 0.13) * mm});
            skLineSegment(sketch, "E3120", {"start": v(0.03, 0.13) * mm, "end": v(0, 0.15) * mm});
            skLineSegment(sketch, "E3121", {"start": v(0, 0.15) * mm, "end": v(0, 0.15) * mm});
            skLineSegment(sketch, "E3122", {"start": v(0, 0.15) * mm, "end": v(-0.03, 0.16) * mm});
            skLineSegment(sketch, "E3123", {"start": v(-0.03, 0.16) * mm, "end": v(-0.04, 0.18) * mm});
            skLineSegment(sketch, "E3124", {"start": v(-0.04, 0.18) * mm, "end": v(-0.03, 0.19) * mm});
            skLineSegment(sketch, "E3125", {"start": v(-0.03, 0.19) * mm, "end": v(0, 0.2) * mm});
            skLineSegment(sketch, "E3126", {"start": v(0, 0.2) * mm, "end": v(0, 0.21) * mm});
            skLineSegment(sketch, "E3127", {"start": v(0, 0.21) * mm, "end": v(0, 0.22) * mm});
            skLineSegment(sketch, "E3128", {"start": v(0, 0.22) * mm, "end": v(0.03, 0.23) * mm});
            skLineSegment(sketch, "E3129", {"start": v(0.03, 0.23) * mm, "end": v(0.06, 0.24) * mm});
            skLineSegment(sketch, "E3130", {"start": v(0.06, 0.24) * mm, "end": v(0.07, 0.23) * mm});
            skLineSegment(sketch, "E3131", {"start": v(0.07, 0.23) * mm, "end": v(0.1, 0.22) * mm});
            skLineSegment(sketch, "E3132", {"start": v(0.1, 0.22) * mm, "end": v(0.1, 0.21) * mm});
            skLineSegment(sketch, "E3133", {"start": v(-0.88, 0.18) * mm, "end": v(-0.87, 0.17) * mm});
            skLineSegment(sketch, "E3134", {"start": v(-0.87, 0.17) * mm, "end": v(-0.84, 0.15) * mm});
            skLineSegment(sketch, "E3135", {"start": v(-0.84, 0.15) * mm, "end": v(-0.82, 0.13) * mm});
            skLineSegment(sketch, "E3136", {"start": v(-0.82, 0.13) * mm, "end": v(-0.83, 0.12) * mm});
            skLineSegment(sketch, "E3137", {"start": v(-0.83, 0.12) * mm, "end": v(-0.85, 0.12) * mm});
            skLineSegment(sketch, "E3138", {"start": v(-0.85, 0.12) * mm, "end": v(-0.86, 0.12) * mm});
            skLineSegment(sketch, "E3139", {"start": v(-0.86, 0.12) * mm, "end": v(-0.87, 0.12) * mm});
            skLineSegment(sketch, "E3140", {"start": v(-0.87, 0.12) * mm, "end": v(-0.9, 0.13) * mm});
            skLineSegment(sketch, "E3141", {"start": v(-0.9, 0.13) * mm, "end": v(-0.91, 0.12) * mm});
            skLineSegment(sketch, "E3142", {"start": v(-0.91, 0.12) * mm, "end": v(-0.91, 0.12) * mm});
            skLineSegment(sketch, "E3143", {"start": v(-0.91, 0.12) * mm, "end": v(-0.92, 0.12) * mm});
            skLineSegment(sketch, "E3144", {"start": v(-0.92, 0.12) * mm, "end": v(-0.94, 0.1) * mm});
            skLineSegment(sketch, "E3145", {"start": v(-0.94, 0.1) * mm, "end": v(-0.97, 0.1) * mm});
            skLineSegment(sketch, "E3146", {"start": v(-0.97, 0.1) * mm, "end": v(-0.98, 0.1) * mm});
            skLineSegment(sketch, "E3147", {"start": v(-0.98, 0.1) * mm, "end": v(-0.98, 0.1) * mm});
            skLineSegment(sketch, "E3148", {"start": v(-0.98, 0.1) * mm, "end": v(-1.02, 0.1) * mm});
            skLineSegment(sketch, "E3149", {"start": v(-1.02, 0.1) * mm, "end": v(-1.03, 0.1) * mm});
            skLineSegment(sketch, "E3150", {"start": v(-1.03, 0.1) * mm, "end": v(-1.03, 0.1) * mm});
            skLineSegment(sketch, "E3151", {"start": v(-1.03, 0.1) * mm, "end": v(-1.04, 0.1) * mm});
            skLineSegment(sketch, "E3152", {"start": v(-1.04, 0.1) * mm, "end": v(-1.04, 0.1) * mm});
            skLineSegment(sketch, "E3153", {"start": v(-1.04, 0.1) * mm, "end": v(-1.06, 0.09) * mm});
            skLineSegment(sketch, "E3154", {"start": v(-1.06, 0.09) * mm, "end": v(-1.08, 0.08) * mm});
            skLineSegment(sketch, "E3155", {"start": v(-1.08, 0.08) * mm, "end": v(-1.11, 0.09) * mm});
            skLineSegment(sketch, "E3156", {"start": v(-1.11, 0.09) * mm, "end": v(-1.14, 0.1) * mm});
            skLineSegment(sketch, "E3157", {"start": v(-1.14, 0.1) * mm, "end": v(-1.16, 0.1) * mm});
            skLineSegment(sketch, "E3158", {"start": v(-1.16, 0.1) * mm, "end": v(-1.17, 0.1) * mm});
            skLineSegment(sketch, "E3159", {"start": v(-1.17, 0.1) * mm, "end": v(-1.18, 0.12) * mm});
            skLineSegment(sketch, "E3160", {"start": v(-1.18, 0.12) * mm, "end": v(-1.18, 0.12) * mm});
            skLineSegment(sketch, "E3161", {"start": v(-1.18, 0.12) * mm, "end": v(-1.18, 0.13) * mm});
            skLineSegment(sketch, "E3162", {"start": v(-1.18, 0.13) * mm, "end": v(-1.18, 0.15) * mm});
            skLineSegment(sketch, "E3163", {"start": v(-1.18, 0.15) * mm, "end": v(-1.15, 0.17) * mm});
            skLineSegment(sketch, "E3164", {"start": v(-1.15, 0.17) * mm, "end": v(-1.12, 0.2) * mm});
            skLineSegment(sketch, "E3165", {"start": v(-1.12, 0.2) * mm, "end": v(-1.08, 0.2) * mm});
            skLineSegment(sketch, "E3166", {"start": v(-1.08, 0.2) * mm, "end": v(-1.03, 0.2) * mm});
            skLineSegment(sketch, "E3167", {"start": v(-1.03, 0.2) * mm, "end": v(-0.98, 0.2) * mm});
            skLineSegment(sketch, "E3168", {"start": v(-0.98, 0.2) * mm, "end": v(-0.93, 0.2) * mm});
            skLineSegment(sketch, "E3169", {"start": v(-0.93, 0.2) * mm, "end": v(-0.9, 0.18) * mm});
            skLineSegment(sketch, "E3170", {"start": v(-0.9, 0.18) * mm, "end": v(-0.88, 0.18) * mm});
            skLineSegment(sketch, "E3171", {"start": v(-0.32, 0.15) * mm, "end": v(-0.31, 0.14) * mm});
            skLineSegment(sketch, "E3172", {"start": v(-0.31, 0.14) * mm, "end": v(-0.3, 0.12) * mm});
            skLineSegment(sketch, "E3173", {"start": v(-0.3, 0.12) * mm, "end": v(-0.3, 0.09) * mm});
            skLineSegment(sketch, "E3174", {"start": v(-0.3, 0.09) * mm, "end": v(-0.3, 0.06) * mm});
            skLineSegment(sketch, "E3175", {"start": v(-0.3, 0.06) * mm, "end": v(-0.3, 0.05) * mm});
            skLineSegment(sketch, "E3176", {"start": v(-0.3, 0.05) * mm, "end": v(-0.3, 0.05) * mm});
            skLineSegment(sketch, "E3177", {"start": v(-0.3, 0.05) * mm, "end": v(-0.32, 0.05) * mm});
            skLineSegment(sketch, "E3178", {"start": v(-0.32, 0.05) * mm, "end": v(-0.34, 0.05) * mm});
            skLineSegment(sketch, "E3179", {"start": v(-0.34, 0.05) * mm, "end": v(-0.38, 0.05) * mm});
            skLineSegment(sketch, "E3180", {"start": v(-0.38, 0.05) * mm, "end": v(-0.42, 0.06) * mm});
            skLineSegment(sketch, "E3181", {"start": v(-0.42, 0.06) * mm, "end": v(-0.44, 0.06) * mm});
            skLineSegment(sketch, "E3182", {"start": v(-0.44, 0.06) * mm, "end": v(-0.45, 0.06) * mm});
            skLineSegment(sketch, "E3183", {"start": v(-0.45, 0.06) * mm, "end": v(-0.45, 0.06) * mm});
            skLineSegment(sketch, "E3184", {"start": v(-0.45, 0.06) * mm, "end": v(-0.44, 0.07) * mm});
            skLineSegment(sketch, "E3185", {"start": v(-0.44, 0.07) * mm, "end": v(-0.44, 0.08) * mm});
            skLineSegment(sketch, "E3186", {"start": v(-0.44, 0.08) * mm, "end": v(-0.42, 0.1) * mm});
            skLineSegment(sketch, "E3187", {"start": v(-0.42, 0.1) * mm, "end": v(-0.4, 0.12) * mm});
            skLineSegment(sketch, "E3188", {"start": v(-0.4, 0.12) * mm, "end": v(-0.39, 0.14) * mm});
            skLineSegment(sketch, "E3189", {"start": v(-0.39, 0.14) * mm, "end": v(-0.37, 0.16) * mm});
            skLineSegment(sketch, "E3190", {"start": v(-0.37, 0.16) * mm, "end": v(-0.36, 0.17) * mm});
            skLineSegment(sketch, "E3191", {"start": v(-0.36, 0.17) * mm, "end": v(-0.35, 0.17) * mm});
            skLineSegment(sketch, "E3192", {"start": v(-0.35, 0.17) * mm, "end": v(-0.35, 0.17) * mm});
            skLineSegment(sketch, "E3193", {"start": v(-0.35, 0.17) * mm, "end": v(-0.34, 0.17) * mm});
            skLineSegment(sketch, "E3194", {"start": v(-0.34, 0.17) * mm, "end": v(-0.32, 0.15) * mm});
            skLineSegment(sketch, "E3195", {"start": v(-0.32, 0.15) * mm, "end": v(-0.32, 0.15) * mm});
            skLineSegment(sketch, "E3196", {"start": v(0.57, 0.15) * mm, "end": v(0.57, 0.14) * mm});
            skLineSegment(sketch, "E3197", {"start": v(0.57, 0.14) * mm, "end": v(0.58, 0.12) * mm});
            skLineSegment(sketch, "E3198", {"start": v(0.58, 0.12) * mm, "end": v(0.58, 0.1) * mm});
            skLineSegment(sketch, "E3199", {"start": v(0.58, 0.1) * mm, "end": v(0.58, 0.07) * mm});
            skLineSegment(sketch, "E3200", {"start": v(0.58, 0.07) * mm, "end": v(0.57, 0.05) * mm});
            skLineSegment(sketch, "E3201", {"start": v(0.57, 0.05) * mm, "end": v(0.56, 0.04) * mm});
            skLineSegment(sketch, "E3202", {"start": v(0.56, 0.04) * mm, "end": v(0.55, 0.03) * mm});
            skLineSegment(sketch, "E3203", {"start": v(0.55, 0.03) * mm, "end": v(0.53, 0.03) * mm});
            skLineSegment(sketch, "E3204", {"start": v(0.53, 0.03) * mm, "end": v(0.52, 0.03) * mm});
            skLineSegment(sketch, "E3205", {"start": v(0.52, 0.03) * mm, "end": v(0.52, 0.04) * mm});
            skLineSegment(sketch, "E3206", {"start": v(0.52, 0.04) * mm, "end": v(0.51, 0.04) * mm});
            skLineSegment(sketch, "E3207", {"start": v(0.51, 0.04) * mm, "end": v(0.5, 0.06) * mm});
            skLineSegment(sketch, "E3208", {"start": v(0.5, 0.06) * mm, "end": v(0.5, 0.08) * mm});
            skLineSegment(sketch, "E3209", {"start": v(0.5, 0.08) * mm, "end": v(0.5, 0.08) * mm});
            skLineSegment(sketch, "E3210", {"start": v(0.5, 0.08) * mm, "end": v(0.5, 0.09) * mm});
            skLineSegment(sketch, "E3211", {"start": v(0.5, 0.09) * mm, "end": v(0.51, 0.11) * mm});
            skLineSegment(sketch, "E3212", {"start": v(0.51, 0.11) * mm, "end": v(0.52, 0.14) * mm});
            skLineSegment(sketch, "E3213", {"start": v(0.52, 0.14) * mm, "end": v(0.52, 0.14) * mm});
            skLineSegment(sketch, "E3214", {"start": v(0.52, 0.14) * mm, "end": v(0.52, 0.15) * mm});
            skLineSegment(sketch, "E3215", {"start": v(0.52, 0.15) * mm, "end": v(0.52, 0.16) * mm});
            skLineSegment(sketch, "E3216", {"start": v(0.52, 0.16) * mm, "end": v(0.52, 0.17) * mm});
            skLineSegment(sketch, "E3217", {"start": v(0.52, 0.17) * mm, "end": v(0.53, 0.17) * mm});
            skLineSegment(sketch, "E3218", {"start": v(0.53, 0.17) * mm, "end": v(0.54, 0.17) * mm});
            skLineSegment(sketch, "E3219", {"start": v(0.54, 0.17) * mm, "end": v(0.54, 0.17) * mm});
            skLineSegment(sketch, "E3220", {"start": v(0.54, 0.17) * mm, "end": v(0.55, 0.17) * mm});
            skLineSegment(sketch, "E3221", {"start": v(0.55, 0.17) * mm, "end": v(0.56, 0.15) * mm});
            skLineSegment(sketch, "E3222", {"start": v(0.56, 0.15) * mm, "end": v(0.57, 0.15) * mm});
            skLineSegment(sketch, "E3223", {"start": v(0.5, 0.12) * mm, "end": v(0.49, 0.11) * mm});
            skLineSegment(sketch, "E3224", {"start": v(0.49, 0.11) * mm, "end": v(0.48, 0.1) * mm});
            skLineSegment(sketch, "E3225", {"start": v(0.48, 0.1) * mm, "end": v(0.47, 0.09) * mm});
            skLineSegment(sketch, "E3226", {"start": v(0.47, 0.09) * mm, "end": v(0.46, 0.07) * mm});
            skLineSegment(sketch, "E3227", {"start": v(0.46, 0.07) * mm, "end": v(0.45, 0.05) * mm});
            skLineSegment(sketch, "E3228", {"start": v(0.45, 0.05) * mm, "end": v(0.43, 0.03) * mm});
            skLineSegment(sketch, "E3229", {"start": v(0.43, 0.03) * mm, "end": v(0.41, 0) * mm});
            skLineSegment(sketch, "E3230", {"start": v(0.41, 0) * mm, "end": v(0.4, 0) * mm});
            skLineSegment(sketch, "E3231", {"start": v(0.4, 0) * mm, "end": v(0.4, 0) * mm});
            skLineSegment(sketch, "E3232", {"start": v(0.4, 0) * mm, "end": v(0.39, 0) * mm});
            skLineSegment(sketch, "E3233", {"start": v(0.39, 0) * mm, "end": v(0.38, 0.01) * mm});
            skLineSegment(sketch, "E3234", {"start": v(0.38, 0.01) * mm, "end": v(0.38, 0.03) * mm});
            skLineSegment(sketch, "E3235", {"start": v(0.38, 0.03) * mm, "end": v(0.39, 0.05) * mm});
            skLineSegment(sketch, "E3236", {"start": v(0.39, 0.05) * mm, "end": v(0.4, 0.08) * mm});
            skLineSegment(sketch, "E3237", {"start": v(0.4, 0.08) * mm, "end": v(0.4, 0.1) * mm});
            skLineSegment(sketch, "E3238", {"start": v(0.4, 0.1) * mm, "end": v(0.42, 0.12) * mm});
            skLineSegment(sketch, "E3239", {"start": v(0.42, 0.12) * mm, "end": v(0.43, 0.13) * mm});
            skLineSegment(sketch, "E3240", {"start": v(0.43, 0.13) * mm, "end": v(0.44, 0.13) * mm});
            skLineSegment(sketch, "E3241", {"start": v(0.44, 0.13) * mm, "end": v(0.45, 0.14) * mm});
            skLineSegment(sketch, "E3242", {"start": v(0.45, 0.14) * mm, "end": v(0.47, 0.15) * mm});
            skLineSegment(sketch, "E3243", {"start": v(0.47, 0.15) * mm, "end": v(0.5, 0.15) * mm});
            skLineSegment(sketch, "E3244", {"start": v(0.5, 0.15) * mm, "end": v(0.5, 0.14) * mm});
            skLineSegment(sketch, "E3245", {"start": v(0.5, 0.14) * mm, "end": v(0.5, 0.12) * mm});
            skLineSegment(sketch, "E3246", {"start": v(0.5, 0.12) * mm, "end": v(0.5, 0.12) * mm});
            skLineSegment(sketch, "E3247", {"start": v(-0.22, 0.05) * mm, "end": v(-0.22, 0.04) * mm});
            skLineSegment(sketch, "E3248", {"start": v(-0.22, 0.04) * mm, "end": v(-0.21, 0) * mm});
            skLineSegment(sketch, "E3249", {"start": v(-0.21, 0) * mm, "end": v(-0.2, -0.06) * mm});
            skLineSegment(sketch, "E3250", {"start": v(-0.2, -0.06) * mm, "end": v(-0.2, -0.07) * mm});
            skLineSegment(sketch, "E3251", {"start": v(-0.2, -0.07) * mm, "end": v(-0.2, -0.08) * mm});
            skLineSegment(sketch, "E3252", {"start": v(-0.2, -0.08) * mm, "end": v(-0.2, -0.11) * mm});
            skLineSegment(sketch, "E3253", {"start": v(-0.2, -0.11) * mm, "end": v(-0.2, -0.13) * mm});
            skLineSegment(sketch, "E3254", {"start": v(-0.2, -0.13) * mm, "end": v(-0.2, -0.14) * mm});
            skLineSegment(sketch, "E3255", {"start": v(-0.2, -0.14) * mm, "end": v(-0.22, -0.15) * mm});
            skLineSegment(sketch, "E3256", {"start": v(-0.22, -0.15) * mm, "end": v(-0.23, -0.15) * mm});
            skLineSegment(sketch, "E3257", {"start": v(-0.23, -0.15) * mm, "end": v(-0.23, -0.15) * mm});
            skLineSegment(sketch, "E3258", {"start": v(-0.23, -0.15) * mm, "end": v(-0.26, -0.16) * mm});
            skLineSegment(sketch, "E3259", {"start": v(-0.26, -0.16) * mm, "end": v(-0.3, -0.16) * mm});
            skLineSegment(sketch, "E3260", {"start": v(-0.3, -0.16) * mm, "end": v(-0.3, -0.17) * mm});
            skLineSegment(sketch, "E3261", {"start": v(-0.3, -0.17) * mm, "end": v(-0.3, -0.17) * mm});
            skLineSegment(sketch, "E3262", {"start": v(-0.3, -0.17) * mm, "end": v(-0.32, -0.17) * mm});
            skLineSegment(sketch, "E3263", {"start": v(-0.32, -0.17) * mm, "end": v(-0.33, -0.17) * mm});
            skLineSegment(sketch, "E3264", {"start": v(-0.33, -0.17) * mm, "end": v(-0.33, -0.16) * mm});
            skLineSegment(sketch, "E3265", {"start": v(-0.33, -0.16) * mm, "end": v(-0.33, -0.15) * mm});
            skLineSegment(sketch, "E3266", {"start": v(-0.33, -0.15) * mm, "end": v(-0.33, -0.15) * mm});
            skLineSegment(sketch, "E3267", {"start": v(-0.33, -0.15) * mm, "end": v(-0.33, -0.14) * mm});
            skLineSegment(sketch, "E3268", {"start": v(-0.33, -0.14) * mm, "end": v(-0.33, -0.13) * mm});
            skLineSegment(sketch, "E3269", {"start": v(-0.33, -0.13) * mm, "end": v(-0.32, -0.12) * mm});
            skLineSegment(sketch, "E3270", {"start": v(-0.32, -0.12) * mm, "end": v(-0.32, -0.12) * mm});
            skLineSegment(sketch, "E3271", {"start": v(-0.32, -0.12) * mm, "end": v(-0.31, -0.11) * mm});
            skLineSegment(sketch, "E3272", {"start": v(-0.31, -0.11) * mm, "end": v(-0.31, -0.1) * mm});
            skLineSegment(sketch, "E3273", {"start": v(-0.31, -0.1) * mm, "end": v(-0.32, -0.07) * mm});
            skLineSegment(sketch, "E3274", {"start": v(-0.32, -0.07) * mm, "end": v(-0.34, -0.04) * mm});
            skLineSegment(sketch, "E3275", {"start": v(-0.34, -0.04) * mm, "end": v(-0.34, -0.03) * mm});
            skLineSegment(sketch, "E3276", {"start": v(-0.34, -0.03) * mm, "end": v(-0.35, -0.03) * mm});
            skLineSegment(sketch, "E3277", {"start": v(-0.35, -0.03) * mm, "end": v(-0.36, 0) * mm});
            skLineSegment(sketch, "E3278", {"start": v(-0.36, 0) * mm, "end": v(-0.37, 0.01) * mm});
            skLineSegment(sketch, "E3279", {"start": v(-0.37, 0.01) * mm, "end": v(-0.37, 0.02) * mm});
            skLineSegment(sketch, "E3280", {"start": v(-0.37, 0.02) * mm, "end": v(-0.36, 0.02) * mm});
            skLineSegment(sketch, "E3281", {"start": v(-0.36, 0.02) * mm, "end": v(-0.35, 0.02) * mm});
            skLineSegment(sketch, "E3282", {"start": v(-0.35, 0.02) * mm, "end": v(-0.35, 0.02) * mm});
            skLineSegment(sketch, "E3283", {"start": v(-0.35, 0.02) * mm, "end": v(-0.33, 0.02) * mm});
            skLineSegment(sketch, "E3284", {"start": v(-0.33, 0.02) * mm, "end": v(-0.3, 0.03) * mm});
            skLineSegment(sketch, "E3285", {"start": v(-0.3, 0.03) * mm, "end": v(-0.3, 0.03) * mm});
            skLineSegment(sketch, "E3286", {"start": v(-0.3, 0.03) * mm, "end": v(-0.28, 0.02) * mm});
            skLineSegment(sketch, "E3287", {"start": v(-0.28, 0.02) * mm, "end": v(-0.28, 0) * mm});
            skLineSegment(sketch, "E3288", {"start": v(-0.28, 0) * mm, "end": v(-0.28, -0.03) * mm});
            skLineSegment(sketch, "E3289", {"start": v(-0.28, -0.03) * mm, "end": v(-0.28, -0.04) * mm});
            skLineSegment(sketch, "E3290", {"start": v(-0.28, -0.04) * mm, "end": v(-0.28, -0.04) * mm});
            skLineSegment(sketch, "E3291", {"start": v(-0.28, -0.04) * mm, "end": v(-0.28, -0.07) * mm});
            skLineSegment(sketch, "E3292", {"start": v(-0.28, -0.07) * mm, "end": v(-0.28, -0.09) * mm});
            skLineSegment(sketch, "E3293", {"start": v(-0.28, -0.09) * mm, "end": v(-0.27, -0.1) * mm});
            skLineSegment(sketch, "E3294", {"start": v(-0.27, -0.1) * mm, "end": v(-0.27, -0.08) * mm});
            skLineSegment(sketch, "E3295", {"start": v(-0.27, -0.08) * mm, "end": v(-0.27, -0.08) * mm});
            skLineSegment(sketch, "E3296", {"start": v(-0.27, -0.08) * mm, "end": v(-0.26, -0.07) * mm});
            skLineSegment(sketch, "E3297", {"start": v(-0.26, -0.07) * mm, "end": v(-0.26, -0.05) * mm});
            skLineSegment(sketch, "E3298", {"start": v(-0.26, -0.05) * mm, "end": v(-0.26, -0.02) * mm});
            skLineSegment(sketch, "E3299", {"start": v(-0.26, -0.02) * mm, "end": v(-0.26, 0.03) * mm});
            skLineSegment(sketch, "E3300", {"start": v(-0.26, 0.03) * mm, "end": v(-0.27, 0.07) * mm});
            skLineSegment(sketch, "E3301", {"start": v(-0.27, 0.07) * mm, "end": v(-0.28, 0.09) * mm});
            skLineSegment(sketch, "E3302", {"start": v(-0.28, 0.09) * mm, "end": v(-0.28, 0.1) * mm});
            skLineSegment(sketch, "E3303", {"start": v(-0.28, 0.1) * mm, "end": v(-0.28, 0.1) * mm});
            skLineSegment(sketch, "E3304", {"start": v(-0.28, 0.1) * mm, "end": v(-0.28, 0.11) * mm});
            skLineSegment(sketch, "E3305", {"start": v(-0.28, 0.11) * mm, "end": v(-0.27, 0.11) * mm});
            skLineSegment(sketch, "E3306", {"start": v(-0.27, 0.11) * mm, "end": v(-0.26, 0.1) * mm});
            skLineSegment(sketch, "E3307", {"start": v(-0.26, 0.1) * mm, "end": v(-0.25, 0.1) * mm});
            skLineSegment(sketch, "E3308", {"start": v(-0.25, 0.1) * mm, "end": v(-0.25, 0.1) * mm});
            skLineSegment(sketch, "E3309", {"start": v(-0.25, 0.1) * mm, "end": v(-0.23, 0.08) * mm});
            skLineSegment(sketch, "E3310", {"start": v(-0.23, 0.08) * mm, "end": v(-0.22, 0.05) * mm});
            skLineSegment(sketch, "E3311", {"start": v(-0.22, 0.05) * mm, "end": v(-0.22, 0.05) * mm});
            skLineSegment(sketch, "E3312", {"start": v(0.37, 0.05) * mm, "end": v(0.37, 0.03) * mm});
            skLineSegment(sketch, "E3313", {"start": v(0.37, 0.03) * mm, "end": v(0.35, 0) * mm});
            skLineSegment(sketch, "E3314", {"start": v(0.35, 0) * mm, "end": v(0.33, -0.03) * mm});
            skLineSegment(sketch, "E3315", {"start": v(0.33, -0.03) * mm, "end": v(0.28, -0.03) * mm});
            skLineSegment(sketch, "E3316", {"start": v(0.28, -0.03) * mm, "end": v(0.23, -0.02) * mm});
            skLineSegment(sketch, "E3317", {"start": v(0.23, -0.02) * mm, "end": v(0.22, 0) * mm});
            skLineSegment(sketch, "E3318", {"start": v(0.22, 0) * mm, "end": v(0.2, 0) * mm});
            skLineSegment(sketch, "E3319", {"start": v(0.2, 0) * mm, "end": v(0.17, 0.02) * mm});
            skLineSegment(sketch, "E3320", {"start": v(0.17, 0.02) * mm, "end": v(0.17, 0.04) * mm});
            skLineSegment(sketch, "E3321", {"start": v(0.17, 0.04) * mm, "end": v(0.19, 0.05) * mm});
            skLineSegment(sketch, "E3322", {"start": v(0.19, 0.05) * mm, "end": v(0.23, 0.05) * mm});
            skLineSegment(sketch, "E3323", {"start": v(0.23, 0.05) * mm, "end": v(0.24, 0.05) * mm});
            skLineSegment(sketch, "E3324", {"start": v(0.24, 0.05) * mm, "end": v(0.25, 0.05) * mm});
            skLineSegment(sketch, "E3325", {"start": v(0.25, 0.05) * mm, "end": v(0.27, 0.06) * mm});
            skLineSegment(sketch, "E3326", {"start": v(0.27, 0.06) * mm, "end": v(0.29, 0.08) * mm});
            skLineSegment(sketch, "E3327", {"start": v(0.29, 0.08) * mm, "end": v(0.3, 0.08) * mm});
            skLineSegment(sketch, "E3328", {"start": v(0.3, 0.08) * mm, "end": v(0.3, 0.09) * mm});
            skLineSegment(sketch, "E3329", {"start": v(0.3, 0.09) * mm, "end": v(0.32, 0.1) * mm});
            skLineSegment(sketch, "E3330", {"start": v(0.32, 0.1) * mm, "end": v(0.35, 0.1) * mm});
            skLineSegment(sketch, "E3331", {"start": v(0.35, 0.1) * mm, "end": v(0.37, 0.09) * mm});
            skLineSegment(sketch, "E3332", {"start": v(0.37, 0.09) * mm, "end": v(0.37, 0.06) * mm});
            skLineSegment(sketch, "E3333", {"start": v(0.37, 0.06) * mm, "end": v(0.37, 0.05) * mm});
            skLineSegment(sketch, "E3334", {"start": v(-0.08, -0.01) * mm, "end": v(-0.08, -0.02) * mm});
            skLineSegment(sketch, "E3335", {"start": v(-0.08, -0.02) * mm, "end": v(-0.08, -0.05) * mm});
            skLineSegment(sketch, "E3336", {"start": v(-0.08, -0.05) * mm, "end": v(-0.1, -0.09) * mm});
            skLineSegment(sketch, "E3337", {"start": v(-0.1, -0.09) * mm, "end": v(-0.11, -0.12) * mm});
            skLineSegment(sketch, "E3338", {"start": v(-0.11, -0.12) * mm, "end": v(-0.13, -0.14) * mm});
            skLineSegment(sketch, "E3339", {"start": v(-0.13, -0.14) * mm, "end": v(-0.14, -0.14) * mm});
            skLineSegment(sketch, "E3340", {"start": v(-0.14, -0.14) * mm, "end": v(-0.14, -0.14) * mm});
            skLineSegment(sketch, "E3341", {"start": v(-0.14, -0.14) * mm, "end": v(-0.15, -0.14) * mm});
            skLineSegment(sketch, "E3342", {"start": v(-0.15, -0.14) * mm, "end": v(-0.16, -0.13) * mm});
            skLineSegment(sketch, "E3343", {"start": v(-0.16, -0.13) * mm, "end": v(-0.17, -0.1) * mm});
            skLineSegment(sketch, "E3344", {"start": v(-0.17, -0.1) * mm, "end": v(-0.17, -0.08) * mm});
            skLineSegment(sketch, "E3345", {"start": v(-0.17, -0.08) * mm, "end": v(-0.17, -0.07) * mm});
            skLineSegment(sketch, "E3346", {"start": v(-0.17, -0.07) * mm, "end": v(-0.18, -0.06) * mm});
            skLineSegment(sketch, "E3347", {"start": v(-0.18, -0.06) * mm, "end": v(-0.18, -0.01) * mm});
            skLineSegment(sketch, "E3348", {"start": v(-0.18, -0.01) * mm, "end": v(-0.2, 0.03) * mm});
            skLineSegment(sketch, "E3349", {"start": v(-0.2, 0.03) * mm, "end": v(-0.2, 0.03) * mm});
            skLineSegment(sketch, "E3350", {"start": v(-0.2, 0.03) * mm, "end": v(-0.2, 0.07) * mm});
            skLineSegment(sketch, "E3351", {"start": v(-0.2, 0.07) * mm, "end": v(-0.14, 0.03) * mm});
            skLineSegment(sketch, "E3352", {"start": v(-0.14, 0.03) * mm, "end": v(-0.13, 0.03) * mm});
            skLineSegment(sketch, "E3353", {"start": v(-0.13, 0.03) * mm, "end": v(-0.1, 0) * mm});
            skLineSegment(sketch, "E3354", {"start": v(-0.1, 0) * mm, "end": v(-0.08, 0) * mm});
            skLineSegment(sketch, "E3355", {"start": v(-0.08, 0) * mm, "end": v(-0.08, -0.01) * mm});
            skLineSegment(sketch, "E3356", {"start": v(0.6, -0.07) * mm, "end": v(0.6, -0.08) * mm});
            skLineSegment(sketch, "E3357", {"start": v(0.6, -0.08) * mm, "end": v(0.6, -0.12) * mm});
            skLineSegment(sketch, "E3358", {"start": v(0.6, -0.12) * mm, "end": v(0.58, -0.17) * mm});
            skLineSegment(sketch, "E3359", {"start": v(0.58, -0.17) * mm, "end": v(0.54, -0.21) * mm});
            skLineSegment(sketch, "E3360", {"start": v(0.54, -0.21) * mm, "end": v(0.5, -0.24) * mm});
            skLineSegment(sketch, "E3361", {"start": v(0.5, -0.24) * mm, "end": v(0.49, -0.25) * mm});
            skLineSegment(sketch, "E3362", {"start": v(0.49, -0.25) * mm, "end": v(0.48, -0.25) * mm});
            skLineSegment(sketch, "E3363", {"start": v(0.48, -0.25) * mm, "end": v(0.47, -0.25) * mm});
            skLineSegment(sketch, "E3364", {"start": v(0.47, -0.25) * mm, "end": v(0.44, -0.25) * mm});
            skLineSegment(sketch, "E3365", {"start": v(0.44, -0.25) * mm, "end": v(0.41, -0.24) * mm});
            skLineSegment(sketch, "E3366", {"start": v(0.41, -0.24) * mm, "end": v(0.4, -0.23) * mm});
            skLineSegment(sketch, "E3367", {"start": v(0.4, -0.23) * mm, "end": v(0.4, -0.23) * mm});
            skLineSegment(sketch, "E3368", {"start": v(0.4, -0.23) * mm, "end": v(0.4, -0.22) * mm});
            skLineSegment(sketch, "E3369", {"start": v(0.4, -0.22) * mm, "end": v(0.4, -0.21) * mm});
            skLineSegment(sketch, "E3370", {"start": v(0.4, -0.21) * mm, "end": v(0.38, -0.2) * mm});
            skLineSegment(sketch, "E3371", {"start": v(0.38, -0.2) * mm, "end": v(0.38, -0.2) * mm});
            skLineSegment(sketch, "E3372", {"start": v(0.38, -0.2) * mm, "end": v(0.37, -0.18) * mm});
            skLineSegment(sketch, "E3373", {"start": v(0.37, -0.18) * mm, "end": v(0.37, -0.18) * mm});
            skLineSegment(sketch, "E3374", {"start": v(0.37, -0.18) * mm, "end": v(0.4, -0.17) * mm});
            skLineSegment(sketch, "E3375", {"start": v(0.4, -0.17) * mm, "end": v(0.44, -0.17) * mm});
            skLineSegment(sketch, "E3376", {"start": v(0.44, -0.17) * mm, "end": v(0.45, -0.17) * mm});
            skLineSegment(sketch, "E3377", {"start": v(0.45, -0.17) * mm, "end": v(0.46, -0.17) * mm});
            skLineSegment(sketch, "E3378", {"start": v(0.46, -0.17) * mm, "end": v(0.48, -0.17) * mm});
            skLineSegment(sketch, "E3379", {"start": v(0.48, -0.17) * mm, "end": v(0.5, -0.17) * mm});
            skLineSegment(sketch, "E3380", {"start": v(0.5, -0.17) * mm, "end": v(0.51, -0.16) * mm});
            skLineSegment(sketch, "E3381", {"start": v(0.51, -0.16) * mm, "end": v(0.5, -0.16) * mm});
            skLineSegment(sketch, "E3382", {"start": v(0.5, -0.16) * mm, "end": v(0.5, -0.16) * mm});
            skLineSegment(sketch, "E3383", {"start": v(0.5, -0.16) * mm, "end": v(0.48, -0.15) * mm});
            skLineSegment(sketch, "E3384", {"start": v(0.48, -0.15) * mm, "end": v(0.47, -0.14) * mm});
            skLineSegment(sketch, "E3385", {"start": v(0.47, -0.14) * mm, "end": v(0.47, -0.13) * mm});
            skLineSegment(sketch, "E3386", {"start": v(0.47, -0.13) * mm, "end": v(0.49, -0.13) * mm});
            skLineSegment(sketch, "E3387", {"start": v(0.49, -0.13) * mm, "end": v(0.5, -0.13) * mm});
            skLineSegment(sketch, "E3388", {"start": v(0.5, -0.13) * mm, "end": v(0.5, -0.13) * mm});
            skLineSegment(sketch, "E3389", {"start": v(0.5, -0.13) * mm, "end": v(0.5, -0.12) * mm});
            skLineSegment(sketch, "E3390", {"start": v(0.5, -0.12) * mm, "end": v(0.52, -0.08) * mm});
            skLineSegment(sketch, "E3391", {"start": v(0.52, -0.08) * mm, "end": v(0.52, -0.07) * mm});
            skLineSegment(sketch, "E3392", {"start": v(0.52, -0.07) * mm, "end": v(0.52, -0.06) * mm});
            skLineSegment(sketch, "E3393", {"start": v(0.52, -0.06) * mm, "end": v(0.53, -0.03) * mm});
            skLineSegment(sketch, "E3394", {"start": v(0.53, -0.03) * mm, "end": v(0.54, 0) * mm});
            skLineSegment(sketch, "E3395", {"start": v(0.54, 0) * mm, "end": v(0.56, 0.03) * mm});
            skLineSegment(sketch, "E3396", {"start": v(0.56, 0.03) * mm, "end": v(0.57, 0.04) * mm});
            skLineSegment(sketch, "E3397", {"start": v(0.57, 0.04) * mm, "end": v(0.59, 0.03) * mm});
            skLineSegment(sketch, "E3398", {"start": v(0.59, 0.03) * mm, "end": v(0.6, 0.01) * mm});
            skLineSegment(sketch, "E3399", {"start": v(0.6, 0.01) * mm, "end": v(0.6, -0.02) * mm});
            skLineSegment(sketch, "E3400", {"start": v(0.6, -0.02) * mm, "end": v(0.6, -0.06) * mm});
            skLineSegment(sketch, "E3401", {"start": v(0.6, -0.06) * mm, "end": v(0.6, -0.07) * mm});
            skLineSegment(sketch, "E3402", {"start": v(0.5, -0.02) * mm, "end": v(0.5, -0.03) * mm});
            skLineSegment(sketch, "E3403", {"start": v(0.5, -0.03) * mm, "end": v(0.5, -0.06) * mm});
            skLineSegment(sketch, "E3404", {"start": v(0.5, -0.06) * mm, "end": v(0.48, -0.09) * mm});
            skLineSegment(sketch, "E3405", {"start": v(0.48, -0.09) * mm, "end": v(0.45, -0.12) * mm});
            skLineSegment(sketch, "E3406", {"start": v(0.45, -0.12) * mm, "end": v(0.43, -0.13) * mm});
            skLineSegment(sketch, "E3407", {"start": v(0.43, -0.13) * mm, "end": v(0.42, -0.14) * mm});
            skLineSegment(sketch, "E3408", {"start": v(0.42, -0.14) * mm, "end": v(0.37, -0.16) * mm});
            skLineSegment(sketch, "E3409", {"start": v(0.37, -0.16) * mm, "end": v(0.33, -0.11) * mm});
            skLineSegment(sketch, "E3410", {"start": v(0.33, -0.11) * mm, "end": v(0.3, -0.07) * mm});
            skLineSegment(sketch, "E3411", {"start": v(0.3, -0.07) * mm, "end": v(0.35, -0.05) * mm});
            skLineSegment(sketch, "E3412", {"start": v(0.35, -0.05) * mm, "end": v(0.36, -0.05) * mm});
            skLineSegment(sketch, "E3413", {"start": v(0.36, -0.05) * mm, "end": v(0.38, -0.04) * mm});
            skLineSegment(sketch, "E3414", {"start": v(0.38, -0.04) * mm, "end": v(0.4, -0.03) * mm});
            skLineSegment(sketch, "E3415", {"start": v(0.4, -0.03) * mm, "end": v(0.42, -0.01) * mm});
            skLineSegment(sketch, "E3416", {"start": v(0.42, -0.01) * mm, "end": v(0.44, 0) * mm});
            skLineSegment(sketch, "E3417", {"start": v(0.44, 0) * mm, "end": v(0.44, 0) * mm});
            skLineSegment(sketch, "E3418", {"start": v(0.44, 0) * mm, "end": v(0.45, 0) * mm});
            skLineSegment(sketch, "E3419", {"start": v(0.45, 0) * mm, "end": v(0.46, 0.02) * mm});
            skLineSegment(sketch, "E3420", {"start": v(0.46, 0.02) * mm, "end": v(0.48, 0.02) * mm});
            skLineSegment(sketch, "E3421", {"start": v(0.48, 0.02) * mm, "end": v(0.5, 0) * mm});
            skLineSegment(sketch, "E3422", {"start": v(0.5, 0) * mm, "end": v(0.5, -0.01) * mm});
            skLineSegment(sketch, "E3423", {"start": v(0.5, -0.01) * mm, "end": v(0.5, -0.02) * mm});
            skLineSegment(sketch, "E3424", {"start": v(-0.78, 0.01) * mm, "end": v(-0.77, 0.01) * mm});
            skLineSegment(sketch, "E3425", {"start": v(-0.77, 0.01) * mm, "end": v(-0.78, 0) * mm});
            skLineSegment(sketch, "E3426", {"start": v(-0.78, 0) * mm, "end": v(-0.8, -0.02) * mm});
            skLineSegment(sketch, "E3427", {"start": v(-0.8, -0.02) * mm, "end": v(-0.8, -0.02) * mm});
            skLineSegment(sketch, "E3428", {"start": v(-0.8, -0.02) * mm, "end": v(-0.8, -0.03) * mm});
            skLineSegment(sketch, "E3429", {"start": v(-0.8, -0.03) * mm, "end": v(-0.83, -0.04) * mm});
            skLineSegment(sketch, "E3430", {"start": v(-0.83, -0.04) * mm, "end": v(-0.87, -0.06) * mm});
            skLineSegment(sketch, "E3431", {"start": v(-0.87, -0.06) * mm, "end": v(-0.92, -0.06) * mm});
            skLineSegment(sketch, "E3432", {"start": v(-0.92, -0.06) * mm, "end": v(-0.95, -0.05) * mm});
            skLineSegment(sketch, "E3433", {"start": v(-0.95, -0.05) * mm, "end": v(-0.96, -0.05) * mm});
            skLineSegment(sketch, "E3434", {"start": v(-0.96, -0.05) * mm, "end": v(-0.96, -0.05) * mm});
            skLineSegment(sketch, "E3435", {"start": v(-0.96, -0.05) * mm, "end": v(-0.99, -0.04) * mm});
            skLineSegment(sketch, "E3436", {"start": v(-0.99, -0.04) * mm, "end": v(-1, -0.03) * mm});
            skLineSegment(sketch, "E3437", {"start": v(-1, -0.03) * mm, "end": v(-1.02, -0.03) * mm});
            skLineSegment(sketch, "E3438", {"start": v(-1.02, -0.03) * mm, "end": v(-1.02, -0.03) * mm});
            skLineSegment(sketch, "E3439", {"start": v(-1.02, -0.03) * mm, "end": v(-1.04, -0.03) * mm});
            skLineSegment(sketch, "E3440", {"start": v(-1.04, -0.03) * mm, "end": v(-1.07, -0.01) * mm});
            skLineSegment(sketch, "E3441", {"start": v(-1.07, -0.01) * mm, "end": v(-1.07, 0) * mm});
            skLineSegment(sketch, "E3442", {"start": v(-1.07, 0) * mm, "end": v(-1.05, 0) * mm});
            skLineSegment(sketch, "E3443", {"start": v(-1.05, 0) * mm, "end": v(-0.97, 0.01) * mm});
            skLineSegment(sketch, "E3444", {"start": v(-0.97, 0.01) * mm, "end": v(-0.87, 0.02) * mm});
            skLineSegment(sketch, "E3445", {"start": v(-0.87, 0.02) * mm, "end": v(-0.8, 0.01) * mm});
            skLineSegment(sketch, "E3446", {"start": v(-0.8, 0.01) * mm, "end": v(-0.78, 0.01) * mm});
            skLineSegment(sketch, "E3447", {"start": v(-0.6, 0) * mm, "end": v(-0.6, 0) * mm});
            skLineSegment(sketch, "E3448", {"start": v(-0.6, 0) * mm, "end": v(-0.58, -0.02) * mm});
            skLineSegment(sketch, "E3449", {"start": v(-0.58, -0.02) * mm, "end": v(-0.55, -0.05) * mm});
            skLineSegment(sketch, "E3450", {"start": v(-0.55, -0.05) * mm, "end": v(-0.53, -0.1) * mm});
            skLineSegment(sketch, "E3451", {"start": v(-0.53, -0.1) * mm, "end": v(-0.51, -0.14) * mm});
            skLineSegment(sketch, "E3452", {"start": v(-0.51, -0.14) * mm, "end": v(-0.51, -0.16) * mm});
            skLineSegment(sketch, "E3453", {"start": v(-0.51, -0.16) * mm, "end": v(-0.5, -0.2) * mm});
            skLineSegment(sketch, "E3454", {"start": v(-0.5, -0.2) * mm, "end": v(-0.56, -0.15) * mm});
            skLineSegment(sketch, "E3455", {"start": v(-0.56, -0.15) * mm, "end": v(-0.57, -0.14) * mm});
            skLineSegment(sketch, "E3456", {"start": v(-0.57, -0.14) * mm, "end": v(-0.6, -0.13) * mm});
            skLineSegment(sketch, "E3457", {"start": v(-0.6, -0.13) * mm, "end": v(-0.62, -0.1) * mm});
            skLineSegment(sketch, "E3458", {"start": v(-0.62, -0.1) * mm, "end": v(-0.65, -0.1) * mm});
            skLineSegment(sketch, "E3459", {"start": v(-0.65, -0.1) * mm, "end": v(-0.66, -0.08) * mm});
            skLineSegment(sketch, "E3460", {"start": v(-0.66, -0.08) * mm, "end": v(-0.67, -0.08) * mm});
            skLineSegment(sketch, "E3461", {"start": v(-0.67, -0.08) * mm, "end": v(-0.67, -0.08) * mm});
            skLineSegment(sketch, "E3462", {"start": v(-0.67, -0.08) * mm, "end": v(-0.71, -0.08) * mm});
            skLineSegment(sketch, "E3463", {"start": v(-0.71, -0.08) * mm, "end": v(-0.75, -0.07) * mm});
            skLineSegment(sketch, "E3464", {"start": v(-0.75, -0.07) * mm, "end": v(-0.75, -0.07) * mm});
            skLineSegment(sketch, "E3465", {"start": v(-0.75, -0.07) * mm, "end": v(-0.76, -0.07) * mm});
            skLineSegment(sketch, "E3466", {"start": v(-0.76, -0.07) * mm, "end": v(-0.78, -0.06) * mm});
            skLineSegment(sketch, "E3467", {"start": v(-0.78, -0.06) * mm, "end": v(-0.79, -0.06) * mm});
            skLineSegment(sketch, "E3468", {"start": v(-0.79, -0.06) * mm, "end": v(-0.78, -0.04) * mm});
            skLineSegment(sketch, "E3469", {"start": v(-0.78, -0.04) * mm, "end": v(-0.77, -0.03) * mm});
            skLineSegment(sketch, "E3470", {"start": v(-0.77, -0.03) * mm, "end": v(-0.77, -0.03) * mm});
            skLineSegment(sketch, "E3471", {"start": v(-0.77, -0.03) * mm, "end": v(-0.77, -0.02) * mm});
            skLineSegment(sketch, "E3472", {"start": v(-0.77, -0.02) * mm, "end": v(-0.74, 0) * mm});
            skLineSegment(sketch, "E3473", {"start": v(-0.74, 0) * mm, "end": v(-0.7, 0) * mm});
            skLineSegment(sketch, "E3474", {"start": v(-0.7, 0) * mm, "end": v(-0.66, 0) * mm});
            skLineSegment(sketch, "E3475", {"start": v(-0.66, 0) * mm, "end": v(-0.62, 0) * mm});
            skLineSegment(sketch, "E3476", {"start": v(-0.62, 0) * mm, "end": v(-0.6, 0) * mm});
            skLineSegment(sketch, "E3477", {"start": v(-0.45, -0.04) * mm, "end": v(-0.44, -0.05) * mm});
            skLineSegment(sketch, "E3478", {"start": v(-0.44, -0.05) * mm, "end": v(-0.43, -0.09) * mm});
            skLineSegment(sketch, "E3479", {"start": v(-0.43, -0.09) * mm, "end": v(-0.42, -0.16) * mm});
            skLineSegment(sketch, "E3480", {"start": v(-0.42, -0.16) * mm, "end": v(-0.42, -0.23) * mm});
            skLineSegment(sketch, "E3481", {"start": v(-0.42, -0.23) * mm, "end": v(-0.43, -0.27) * mm});
            skLineSegment(sketch, "E3482", {"start": v(-0.43, -0.27) * mm, "end": v(-0.43, -0.28) * mm});
            skLineSegment(sketch, "E3483", {"start": v(-0.43, -0.28) * mm, "end": v(-0.44, -0.28) * mm});
            skLineSegment(sketch, "E3484", {"start": v(-0.44, -0.28) * mm, "end": v(-0.45, -0.29) * mm});
            skLineSegment(sketch, "E3485", {"start": v(-0.45, -0.29) * mm, "end": v(-0.46, -0.28) * mm});
            skLineSegment(sketch, "E3486", {"start": v(-0.46, -0.28) * mm, "end": v(-0.47, -0.26) * mm});
            skLineSegment(sketch, "E3487", {"start": v(-0.47, -0.26) * mm, "end": v(-0.48, -0.22) * mm});
            skLineSegment(sketch, "E3488", {"start": v(-0.48, -0.22) * mm, "end": v(-0.48, -0.21) * mm});
            skLineSegment(sketch, "E3489", {"start": v(-0.48, -0.21) * mm, "end": v(-0.48, -0.2) * mm});
            skLineSegment(sketch, "E3490", {"start": v(-0.48, -0.2) * mm, "end": v(-0.48, -0.16) * mm});
            skLineSegment(sketch, "E3491", {"start": v(-0.48, -0.16) * mm, "end": v(-0.5, -0.11) * mm});
            skLineSegment(sketch, "E3492", {"start": v(-0.5, -0.11) * mm, "end": v(-0.5, -0.07) * mm});
            skLineSegment(sketch, "E3493", {"start": v(-0.5, -0.07) * mm, "end": v(-0.52, -0.04) * mm});
            skLineSegment(sketch, "E3494", {"start": v(-0.52, -0.04) * mm, "end": v(-0.53, -0.04) * mm});
            skLineSegment(sketch, "E3495", {"start": v(-0.53, -0.04) * mm, "end": v(-0.53, -0.03) * mm});
            skLineSegment(sketch, "E3496", {"start": v(-0.53, -0.03) * mm, "end": v(-0.55, -0.02) * mm});
            skLineSegment(sketch, "E3497", {"start": v(-0.55, -0.02) * mm, "end": v(-0.55, 0) * mm});
            skLineSegment(sketch, "E3498", {"start": v(-0.55, 0) * mm, "end": v(-0.55, 0) * mm});
            skLineSegment(sketch, "E3499", {"start": v(-0.55, 0) * mm, "end": v(-0.53, 0) * mm});
            skLineSegment(sketch, "E3500", {"start": v(-0.53, 0) * mm, "end": v(-0.52, 0) * mm});
            skLineSegment(sketch, "E3501", {"start": v(-0.52, 0) * mm, "end": v(-0.5, 0) * mm});
            skLineSegment(sketch, "E3502", {"start": v(-0.5, 0) * mm, "end": v(-0.47, -0.02) * mm});
            skLineSegment(sketch, "E3503", {"start": v(-0.47, -0.02) * mm, "end": v(-0.46, -0.03) * mm});
            skLineSegment(sketch, "E3504", {"start": v(-0.46, -0.03) * mm, "end": v(-0.45, -0.04) * mm});
            skLineSegment(sketch, "E3505", {"start": v(0.1, -0.03) * mm, "end": v(0.1, -0.04) * mm});
            skLineSegment(sketch, "E3506", {"start": v(0.1, -0.04) * mm, "end": v(0.1, -0.06) * mm});
            skLineSegment(sketch, "E3507", {"start": v(0.1, -0.06) * mm, "end": v(0.1, -0.1) * mm});
            skLineSegment(sketch, "E3508", {"start": v(0.1, -0.1) * mm, "end": v(0.08, -0.11) * mm});
            skLineSegment(sketch, "E3509", {"start": v(0.08, -0.11) * mm, "end": v(0.06, -0.13) * mm});
            skLineSegment(sketch, "E3510", {"start": v(0.06, -0.13) * mm, "end": v(0.04, -0.13) * mm});
            skLineSegment(sketch, "E3511", {"start": v(0.04, -0.13) * mm, "end": v(0.02, -0.13) * mm});
            skLineSegment(sketch, "E3512", {"start": v(0.02, -0.13) * mm, "end": v(0, -0.11) * mm});
            skLineSegment(sketch, "E3513", {"start": v(0, -0.11) * mm, "end": v(0, -0.1) * mm});
            skLineSegment(sketch, "E3514", {"start": v(0, -0.1) * mm, "end": v(-0.01, -0.09) * mm});
            skLineSegment(sketch, "E3515", {"start": v(-0.01, -0.09) * mm, "end": v(-0.01, -0.08) * mm});
            skLineSegment(sketch, "E3516", {"start": v(-0.01, -0.08) * mm, "end": v(-0.03, -0.04) * mm});
            skLineSegment(sketch, "E3517", {"start": v(-0.03, -0.04) * mm, "end": v(-0.04, -0.02) * mm});
            skLineSegment(sketch, "E3518", {"start": v(-0.04, -0.02) * mm, "end": v(-0.04, -0.02) * mm});
            skLineSegment(sketch, "E3519", {"start": v(-0.04, -0.02) * mm, "end": v(-0.03, 0) * mm});
            skLineSegment(sketch, "E3520", {"start": v(-0.03, 0) * mm, "end": v(0, 0) * mm});
            skLineSegment(sketch, "E3521", {"start": v(0, 0) * mm, "end": v(0.04, 0) * mm});
            skLineSegment(sketch, "E3522", {"start": v(0.04, 0) * mm, "end": v(0.07, 0) * mm});
            skLineSegment(sketch, "E3523", {"start": v(0.07, 0) * mm, "end": v(0.08, 0) * mm});
            skLineSegment(sketch, "E3524", {"start": v(0.08, 0) * mm, "end": v(0.08, 0) * mm});
            skLineSegment(sketch, "E3525", {"start": v(0.08, 0) * mm, "end": v(0.1, -0.01) * mm});
            skLineSegment(sketch, "E3526", {"start": v(0.1, -0.01) * mm, "end": v(0.1, -0.02) * mm});
            skLineSegment(sketch, "E3527", {"start": v(0.1, -0.02) * mm, "end": v(0.1, -0.03) * mm});
            skLineSegment(sketch, "E3528", {"start": v(-1.21, -0.1) * mm, "end": v(-1.21, -0.1) * mm});
            skLineSegment(sketch, "E3529", {"start": v(-1.21, -0.1) * mm, "end": v(-1.2, -0.12) * mm});
            skLineSegment(sketch, "E3530", {"start": v(-1.2, -0.12) * mm, "end": v(-1.2, -0.15) * mm});
            skLineSegment(sketch, "E3531", {"start": v(-1.2, -0.15) * mm, "end": v(-1.19, -0.16) * mm});
            skLineSegment(sketch, "E3532", {"start": v(-1.19, -0.16) * mm, "end": v(-1.18, -0.17) * mm});
            skLineSegment(sketch, "E3533", {"start": v(-1.18, -0.17) * mm, "end": v(-1.18, -0.17) * mm});
            skLineSegment(sketch, "E3534", {"start": v(-1.18, -0.17) * mm, "end": v(-1.17, -0.18) * mm});
            skLineSegment(sketch, "E3535", {"start": v(-1.17, -0.18) * mm, "end": v(-1.17, -0.2) * mm});
            skLineSegment(sketch, "E3536", {"start": v(-1.17, -0.2) * mm, "end": v(-1.18, -0.2) * mm});
            skLineSegment(sketch, "E3537", {"start": v(-1.18, -0.2) * mm, "end": v(-1.18, -0.2) * mm});
            skLineSegment(sketch, "E3538", {"start": v(-1.18, -0.2) * mm, "end": v(-1.18, -0.21) * mm});
            skLineSegment(sketch, "E3539", {"start": v(-1.18, -0.21) * mm, "end": v(-1.16, -0.24) * mm});
            skLineSegment(sketch, "E3540", {"start": v(-1.16, -0.24) * mm, "end": v(-1.13, -0.27) * mm});
            skLineSegment(sketch, "E3541", {"start": v(-1.13, -0.27) * mm, "end": v(-1.1, -0.31) * mm});
            skLineSegment(sketch, "E3542", {"start": v(-1.1, -0.31) * mm, "end": v(-1.08, -0.33) * mm});
            skLineSegment(sketch, "E3543", {"start": v(-1.08, -0.33) * mm, "end": v(-1.03, -0.38) * mm});
            skLineSegment(sketch, "E3544", {"start": v(-1.03, -0.38) * mm, "end": v(-1.1, -0.38) * mm});
            skLineSegment(sketch, "E3545", {"start": v(-1.1, -0.38) * mm, "end": v(-1.1, -0.38) * mm});
            skLineSegment(sketch, "E3546", {"start": v(-1.1, -0.38) * mm, "end": v(-1.12, -0.38) * mm});
            skLineSegment(sketch, "E3547", {"start": v(-1.12, -0.38) * mm, "end": v(-1.14, -0.37) * mm});
            skLineSegment(sketch, "E3548", {"start": v(-1.14, -0.37) * mm, "end": v(-1.17, -0.35) * mm});
            skLineSegment(sketch, "E3549", {"start": v(-1.17, -0.35) * mm, "end": v(-1.2, -0.34) * mm});
            skLineSegment(sketch, "E3550", {"start": v(-1.2, -0.34) * mm, "end": v(-1.22, -0.32) * mm});
            skLineSegment(sketch, "E3551", {"start": v(-1.22, -0.32) * mm, "end": v(-1.23, -0.3) * mm});
            skLineSegment(sketch, "E3552", {"start": v(-1.23, -0.3) * mm, "end": v(-1.25, -0.27) * mm});
            skLineSegment(sketch, "E3553", {"start": v(-1.25, -0.27) * mm, "end": v(-1.25, -0.26) * mm});
            skLineSegment(sketch, "E3554", {"start": v(-1.25, -0.26) * mm, "end": v(-1.26, -0.25) * mm});
            skLineSegment(sketch, "E3555", {"start": v(-1.26, -0.25) * mm, "end": v(-1.26, -0.24) * mm});
            skLineSegment(sketch, "E3556", {"start": v(-1.26, -0.24) * mm, "end": v(-1.26, -0.2) * mm});
            skLineSegment(sketch, "E3557", {"start": v(-1.26, -0.2) * mm, "end": v(-1.27, -0.17) * mm});
            skLineSegment(sketch, "E3558", {"start": v(-1.27, -0.17) * mm, "end": v(-1.27, -0.14) * mm});
            skLineSegment(sketch, "E3559", {"start": v(-1.27, -0.14) * mm, "end": v(-1.27, -0.12) * mm});
            skLineSegment(sketch, "E3560", {"start": v(-1.27, -0.12) * mm, "end": v(-1.28, -0.11) * mm});
            skLineSegment(sketch, "E3561", {"start": v(-1.28, -0.11) * mm, "end": v(-1.28, -0.1) * mm});
            skLineSegment(sketch, "E3562", {"start": v(-1.28, -0.1) * mm, "end": v(-1.28, -0.08) * mm});
            skLineSegment(sketch, "E3563", {"start": v(-1.28, -0.08) * mm, "end": v(-1.27, -0.05) * mm});
            skLineSegment(sketch, "E3564", {"start": v(-1.27, -0.05) * mm, "end": v(-1.26, -0.03) * mm});
            skLineSegment(sketch, "E3565", {"start": v(-1.26, -0.03) * mm, "end": v(-1.24, -0.02) * mm});
            skLineSegment(sketch, "E3566", {"start": v(-1.24, -0.02) * mm, "end": v(-1.24, -0.02) * mm});
            skLineSegment(sketch, "E3567", {"start": v(-1.24, -0.02) * mm, "end": v(-1.24, -0.03) * mm});
            skLineSegment(sketch, "E3568", {"start": v(-1.24, -0.03) * mm, "end": v(-1.23, -0.04) * mm});
            skLineSegment(sketch, "E3569", {"start": v(-1.23, -0.04) * mm, "end": v(-1.22, -0.06) * mm});
            skLineSegment(sketch, "E3570", {"start": v(-1.22, -0.06) * mm, "end": v(-1.22, -0.08) * mm});
            skLineSegment(sketch, "E3571", {"start": v(-1.22, -0.08) * mm, "end": v(-1.21, -0.1) * mm});
            skLineSegment(sketch, "E3572", {"start": v(-1.1, -0.08) * mm, "end": v(-1.09, -0.09) * mm});
            skLineSegment(sketch, "E3573", {"start": v(-1.09, -0.09) * mm, "end": v(-1.07, -0.1) * mm});
            skLineSegment(sketch, "E3574", {"start": v(-1.07, -0.1) * mm, "end": v(-1.04, -0.13) * mm});
            skLineSegment(sketch, "E3575", {"start": v(-1.04, -0.13) * mm, "end": v(-1.02, -0.17) * mm});
            skLineSegment(sketch, "E3576", {"start": v(-1.02, -0.17) * mm, "end": v(-1, -0.19) * mm});
            skLineSegment(sketch, "E3577", {"start": v(-1, -0.19) * mm, "end": v(-1, -0.2) * mm});
            skLineSegment(sketch, "E3578", {"start": v(-1, -0.2) * mm, "end": v(-0.98, -0.2) * mm});
            skLineSegment(sketch, "E3579", {"start": v(-0.98, -0.2) * mm, "end": v(-0.95, -0.25) * mm});
            skLineSegment(sketch, "E3580", {"start": v(-0.95, -0.25) * mm, "end": v(-0.91, -0.29) * mm});
            skLineSegment(sketch, "E3581", {"start": v(-0.91, -0.29) * mm, "end": v(-0.88, -0.32) * mm});
            skLineSegment(sketch, "E3582", {"start": v(-0.88, -0.32) * mm, "end": v(-0.87, -0.33) * mm});
            skLineSegment(sketch, "E3583", {"start": v(-0.87, -0.33) * mm, "end": v(-0.86, -0.33) * mm});
            skLineSegment(sketch, "E3584", {"start": v(-0.86, -0.33) * mm, "end": v(-0.86, -0.33) * mm});
            skLineSegment(sketch, "E3585", {"start": v(-0.86, -0.33) * mm, "end": v(-0.85, -0.33) * mm});
            skLineSegment(sketch, "E3586", {"start": v(-0.85, -0.33) * mm, "end": v(-0.85, -0.34) * mm});
            skLineSegment(sketch, "E3587", {"start": v(-0.85, -0.34) * mm, "end": v(-0.86, -0.35) * mm});
            skLineSegment(sketch, "E3588", {"start": v(-0.86, -0.35) * mm, "end": v(-0.88, -0.36) * mm});
            skLineSegment(sketch, "E3589", {"start": v(-0.88, -0.36) * mm, "end": v(-0.88, -0.36) * mm});
            skLineSegment(sketch, "E3590", {"start": v(-0.88, -0.36) * mm, "end": v(-0.9, -0.36) * mm});
            skLineSegment(sketch, "E3591", {"start": v(-0.9, -0.36) * mm, "end": v(-0.94, -0.34) * mm});
            skLineSegment(sketch, "E3592", {"start": v(-0.94, -0.34) * mm, "end": v(-1, -0.3) * mm});
            skLineSegment(sketch, "E3593", {"start": v(-1, -0.3) * mm, "end": v(-1.08, -0.21) * mm});
            skLineSegment(sketch, "E3594", {"start": v(-1.08, -0.21) * mm, "end": v(-1.11, -0.15) * mm});
            skLineSegment(sketch, "E3595", {"start": v(-1.11, -0.15) * mm, "end": v(-1.12, -0.12) * mm});
            skLineSegment(sketch, "E3596", {"start": v(-1.12, -0.12) * mm, "end": v(-1.13, -0.12) * mm});
            skLineSegment(sketch, "E3597", {"start": v(-1.13, -0.12) * mm, "end": v(-1.14, -0.09) * mm});
            skLineSegment(sketch, "E3598", {"start": v(-1.14, -0.09) * mm, "end": v(-1.15, -0.06) * mm});
            skLineSegment(sketch, "E3599", {"start": v(-1.15, -0.06) * mm, "end": v(-1.15, -0.06) * mm});
            skLineSegment(sketch, "E3600", {"start": v(-1.15, -0.06) * mm, "end": v(-1.15, -0.05) * mm});
            skLineSegment(sketch, "E3601", {"start": v(-1.15, -0.05) * mm, "end": v(-1.15, -0.04) * mm});
            skLineSegment(sketch, "E3602", {"start": v(-1.15, -0.04) * mm, "end": v(-1.15, -0.04) * mm});
            skLineSegment(sketch, "E3603", {"start": v(-1.15, -0.04) * mm, "end": v(-1.13, -0.05) * mm});
            skLineSegment(sketch, "E3604", {"start": v(-1.13, -0.05) * mm, "end": v(-1.1, -0.07) * mm});
            skLineSegment(sketch, "E3605", {"start": v(-1.1, -0.07) * mm, "end": v(-1.1, -0.08) * mm});
            skLineSegment(sketch, "E3606", {"start": v(0.17, -0.06) * mm, "end": v(0.17, -0.06) * mm});
            skLineSegment(sketch, "E3607", {"start": v(0.17, -0.06) * mm, "end": v(0.18, -0.08) * mm});
            skLineSegment(sketch, "E3608", {"start": v(0.18, -0.08) * mm, "end": v(0.2, -0.1) * mm});
            skLineSegment(sketch, "E3609", {"start": v(0.2, -0.1) * mm, "end": v(0.2, -0.13) * mm});
            skLineSegment(sketch, "E3610", {"start": v(0.2, -0.13) * mm, "end": v(0.21, -0.15) * mm});
            skLineSegment(sketch, "E3611", {"start": v(0.21, -0.15) * mm, "end": v(0.21, -0.16) * mm});
            skLineSegment(sketch, "E3612", {"start": v(0.21, -0.16) * mm, "end": v(0.21, -0.17) * mm});
            skLineSegment(sketch, "E3613", {"start": v(0.21, -0.17) * mm, "end": v(0.22, -0.19) * mm});
            skLineSegment(sketch, "E3614", {"start": v(0.22, -0.19) * mm, "end": v(0.23, -0.2) * mm});
            skLineSegment(sketch, "E3615", {"start": v(0.23, -0.2) * mm, "end": v(0.23, -0.2) * mm});
            skLineSegment(sketch, "E3616", {"start": v(0.23, -0.2) * mm, "end": v(0.23, -0.19) * mm});
            skLineSegment(sketch, "E3617", {"start": v(0.23, -0.19) * mm, "end": v(0.22, -0.18) * mm});
            skLineSegment(sketch, "E3618", {"start": v(0.22, -0.18) * mm, "end": v(0.22, -0.18) * mm});
            skLineSegment(sketch, "E3619", {"start": v(0.22, -0.18) * mm, "end": v(0.22, -0.15) * mm});
            skLineSegment(sketch, "E3620", {"start": v(0.22, -0.15) * mm, "end": v(0.23, -0.14) * mm});
            skLineSegment(sketch, "E3621", {"start": v(0.23, -0.14) * mm, "end": v(0.24, -0.15) * mm});
            skLineSegment(sketch, "E3622", {"start": v(0.24, -0.15) * mm, "end": v(0.25, -0.17) * mm});
            skLineSegment(sketch, "E3623", {"start": v(0.25, -0.17) * mm, "end": v(0.27, -0.2) * mm});
            skLineSegment(sketch, "E3624", {"start": v(0.27, -0.2) * mm, "end": v(0.28, -0.23) * mm});
            skLineSegment(sketch, "E3625", {"start": v(0.28, -0.23) * mm, "end": v(0.3, -0.28) * mm});
            skLineSegment(sketch, "E3626", {"start": v(0.3, -0.28) * mm, "end": v(0.3, -0.31) * mm});
            skLineSegment(sketch, "E3627", {"start": v(0.3, -0.31) * mm, "end": v(0.31, -0.32) * mm});
            skLineSegment(sketch, "E3628", {"start": v(0.31, -0.32) * mm, "end": v(0.31, -0.34) * mm});
            skLineSegment(sketch, "E3629", {"start": v(0.31, -0.34) * mm, "end": v(0.32, -0.37) * mm});
            skLineSegment(sketch, "E3630", {"start": v(0.32, -0.37) * mm, "end": v(0.34, -0.4) * mm});
            skLineSegment(sketch, "E3631", {"start": v(0.34, -0.4) * mm, "end": v(0.35, -0.41) * mm});
            skLineSegment(sketch, "E3632", {"start": v(0.35, -0.41) * mm, "end": v(0.37, -0.4) * mm});
            skLineSegment(sketch, "E3633", {"start": v(0.37, -0.4) * mm, "end": v(0.37, -0.4) * mm});
            skLineSegment(sketch, "E3634", {"start": v(0.37, -0.4) * mm, "end": v(0.39, -0.4) * mm});
            skLineSegment(sketch, "E3635", {"start": v(0.39, -0.4) * mm, "end": v(0.38, -0.4) * mm});
            skLineSegment(sketch, "E3636", {"start": v(0.38, -0.4) * mm, "end": v(0.38, -0.4) * mm});
            skLineSegment(sketch, "E3637", {"start": v(0.38, -0.4) * mm, "end": v(0.37, -0.41) * mm});
            skLineSegment(sketch, "E3638", {"start": v(0.37, -0.41) * mm, "end": v(0.37, -0.43) * mm});
            skLineSegment(sketch, "E3639", {"start": v(0.37, -0.43) * mm, "end": v(0.36, -0.45) * mm});
            skLineSegment(sketch, "E3640", {"start": v(0.36, -0.45) * mm, "end": v(0.37, -0.46) * mm});
            skLineSegment(sketch, "E3641", {"start": v(0.37, -0.46) * mm, "end": v(0.37, -0.46) * mm});
            skLineSegment(sketch, "E3642", {"start": v(0.37, -0.46) * mm, "end": v(0.37, -0.47) * mm});
            skLineSegment(sketch, "E3643", {"start": v(0.37, -0.47) * mm, "end": v(0.36, -0.46) * mm});
            skLineSegment(sketch, "E3644", {"start": v(0.36, -0.46) * mm, "end": v(0.36, -0.45) * mm});
            skLineSegment(sketch, "E3645", {"start": v(0.36, -0.45) * mm, "end": v(0.35, -0.45) * mm});
            skLineSegment(sketch, "E3646", {"start": v(0.35, -0.45) * mm, "end": v(0.34, -0.43) * mm});
            skLineSegment(sketch, "E3647", {"start": v(0.34, -0.43) * mm, "end": v(0.32, -0.43) * mm});
            skLineSegment(sketch, "E3648", {"start": v(0.32, -0.43) * mm, "end": v(0.32, -0.43) * mm});
            skLineSegment(sketch, "E3649", {"start": v(0.32, -0.43) * mm, "end": v(0.31, -0.42) * mm});
            skLineSegment(sketch, "E3650", {"start": v(0.31, -0.42) * mm, "end": v(0.3, -0.41) * mm});
            skLineSegment(sketch, "E3651", {"start": v(0.3, -0.41) * mm, "end": v(0.29, -0.4) * mm});
            skLineSegment(sketch, "E3652", {"start": v(0.29, -0.4) * mm, "end": v(0.28, -0.37) * mm});
            skLineSegment(sketch, "E3653", {"start": v(0.28, -0.37) * mm, "end": v(0.28, -0.37) * mm});
            skLineSegment(sketch, "E3654", {"start": v(0.28, -0.37) * mm, "end": v(0.27, -0.36) * mm});
            skLineSegment(sketch, "E3655", {"start": v(0.27, -0.36) * mm, "end": v(0.26, -0.34) * mm});
            skLineSegment(sketch, "E3656", {"start": v(0.26, -0.34) * mm, "end": v(0.25, -0.32) * mm});
            skLineSegment(sketch, "E3657", {"start": v(0.25, -0.32) * mm, "end": v(0.24, -0.3) * mm});
            skLineSegment(sketch, "E3658", {"start": v(0.24, -0.3) * mm, "end": v(0.23, -0.3) * mm});
            skLineSegment(sketch, "E3659", {"start": v(0.23, -0.3) * mm, "end": v(0.23, -0.3) * mm});
            skLineSegment(sketch, "E3660", {"start": v(0.23, -0.3) * mm, "end": v(0.22, -0.3) * mm});
            skLineSegment(sketch, "E3661", {"start": v(0.22, -0.3) * mm, "end": v(0.22, -0.29) * mm});
            skLineSegment(sketch, "E3662", {"start": v(0.22, -0.29) * mm, "end": v(0.22, -0.29) * mm});
            skLineSegment(sketch, "E3663", {"start": v(0.22, -0.29) * mm, "end": v(0.22, -0.28) * mm});
            skLineSegment(sketch, "E3664", {"start": v(0.22, -0.28) * mm, "end": v(0.22, -0.27) * mm});
            skLineSegment(sketch, "E3665", {"start": v(0.22, -0.27) * mm, "end": v(0.22, -0.25) * mm});
            skLineSegment(sketch, "E3666", {"start": v(0.22, -0.25) * mm, "end": v(0.22, -0.25) * mm});
            skLineSegment(sketch, "E3667", {"start": v(0.22, -0.25) * mm, "end": v(0.21, -0.24) * mm});
            skLineSegment(sketch, "E3668", {"start": v(0.21, -0.24) * mm, "end": v(0.21, -0.25) * mm});
            skLineSegment(sketch, "E3669", {"start": v(0.21, -0.25) * mm, "end": v(0.2, -0.25) * mm});
            skLineSegment(sketch, "E3670", {"start": v(0.2, -0.25) * mm, "end": v(0.2, -0.25) * mm});
            skLineSegment(sketch, "E3671", {"start": v(0.2, -0.25) * mm, "end": v(0.19, -0.24) * mm});
            skLineSegment(sketch, "E3672", {"start": v(0.19, -0.24) * mm, "end": v(0.17, -0.23) * mm});
            skLineSegment(sketch, "E3673", {"start": v(0.17, -0.23) * mm, "end": v(0.16, -0.21) * mm});
            skLineSegment(sketch, "E3674", {"start": v(0.16, -0.21) * mm, "end": v(0.15, -0.19) * mm});
            skLineSegment(sketch, "E3675", {"start": v(0.15, -0.19) * mm, "end": v(0.14, -0.16) * mm});
            skLineSegment(sketch, "E3676", {"start": v(0.14, -0.16) * mm, "end": v(0.13, -0.13) * mm});
            skLineSegment(sketch, "E3677", {"start": v(0.13, -0.13) * mm, "end": v(0.13, -0.11) * mm});
            skLineSegment(sketch, "E3678", {"start": v(0.13, -0.11) * mm, "end": v(0.13, -0.1) * mm});
            skLineSegment(sketch, "E3679", {"start": v(0.13, -0.1) * mm, "end": v(0.13, -0.1) * mm});
            skLineSegment(sketch, "E3680", {"start": v(0.13, -0.1) * mm, "end": v(0.13, -0.06) * mm});
            skLineSegment(sketch, "E3681", {"start": v(0.13, -0.06) * mm, "end": v(0.13, -0.04) * mm});
            skLineSegment(sketch, "E3682", {"start": v(0.13, -0.04) * mm, "end": v(0.15, -0.04) * mm});
            skLineSegment(sketch, "E3683", {"start": v(0.15, -0.04) * mm, "end": v(0.16, -0.05) * mm});
            skLineSegment(sketch, "E3684", {"start": v(0.16, -0.05) * mm, "end": v(0.17, -0.06) * mm});
            skLineSegment(sketch, "E3685", {"start": v(1, -0.08) * mm, "end": v(0.99, -0.1) * mm});
            skLineSegment(sketch, "E3686", {"start": v(0.99, -0.1) * mm, "end": v(0.98, -0.1) * mm});
            skLineSegment(sketch, "E3687", {"start": v(0.98, -0.1) * mm, "end": v(0.96, -0.14) * mm});
            skLineSegment(sketch, "E3688", {"start": v(0.96, -0.14) * mm, "end": v(0.94, -0.16) * mm});
            skLineSegment(sketch, "E3689", {"start": v(0.94, -0.16) * mm, "end": v(0.91, -0.18) * mm});
            skLineSegment(sketch, "E3690", {"start": v(0.91, -0.18) * mm, "end": v(0.9, -0.2) * mm});
            skLineSegment(sketch, "E3691", {"start": v(0.9, -0.2) * mm, "end": v(0.87, -0.21) * mm});
            skLineSegment(sketch, "E3692", {"start": v(0.87, -0.21) * mm, "end": v(0.86, -0.22) * mm});
            skLineSegment(sketch, "E3693", {"start": v(0.86, -0.22) * mm, "end": v(0.86, -0.21) * mm});
            skLineSegment(sketch, "E3694", {"start": v(0.86, -0.21) * mm, "end": v(0.86, -0.2) * mm});
            skLineSegment(sketch, "E3695", {"start": v(0.86, -0.2) * mm, "end": v(0.86, -0.2) * mm});
            skLineSegment(sketch, "E3696", {"start": v(0.86, -0.2) * mm, "end": v(0.87, -0.19) * mm});
            skLineSegment(sketch, "E3697", {"start": v(0.87, -0.19) * mm, "end": v(0.88, -0.17) * mm});
            skLineSegment(sketch, "E3698", {"start": v(0.88, -0.17) * mm, "end": v(0.88, -0.15) * mm});
            skLineSegment(sketch, "E3699", {"start": v(0.88, -0.15) * mm, "end": v(0.89, -0.15) * mm});
            skLineSegment(sketch, "E3700", {"start": v(0.89, -0.15) * mm, "end": v(0.89, -0.14) * mm});
            skLineSegment(sketch, "E3701", {"start": v(0.89, -0.14) * mm, "end": v(0.9, -0.1) * mm});
            skLineSegment(sketch, "E3702", {"start": v(0.9, -0.1) * mm, "end": v(0.91, -0.08) * mm});
            skLineSegment(sketch, "E3703", {"start": v(0.91, -0.08) * mm, "end": v(0.91, -0.07) * mm});
            skLineSegment(sketch, "E3704", {"start": v(0.91, -0.07) * mm, "end": v(0.91, -0.07) * mm});
            skLineSegment(sketch, "E3705", {"start": v(0.91, -0.07) * mm, "end": v(0.92, -0.07) * mm});
            skLineSegment(sketch, "E3706", {"start": v(0.92, -0.07) * mm, "end": v(0.93, -0.06) * mm});
            skLineSegment(sketch, "E3707", {"start": v(0.93, -0.06) * mm, "end": v(0.93, -0.06) * mm});
            skLineSegment(sketch, "E3708", {"start": v(0.93, -0.06) * mm, "end": v(0.93, -0.07) * mm});
            skLineSegment(sketch, "E3709", {"start": v(0.93, -0.07) * mm, "end": v(0.95, -0.06) * mm});
            skLineSegment(sketch, "E3710", {"start": v(0.95, -0.06) * mm, "end": v(0.96, -0.05) * mm});
            skLineSegment(sketch, "E3711", {"start": v(0.96, -0.05) * mm, "end": v(0.97, -0.05) * mm});
            skLineSegment(sketch, "E3712", {"start": v(0.97, -0.05) * mm, "end": v(0.97, -0.05) * mm});
            skLineSegment(sketch, "E3713", {"start": v(0.97, -0.05) * mm, "end": v(0.99, -0.04) * mm});
            skLineSegment(sketch, "E3714", {"start": v(0.99, -0.04) * mm, "end": v(1, -0.04) * mm});
            skLineSegment(sketch, "E3715", {"start": v(1, -0.04) * mm, "end": v(1, -0.05) * mm});
            skLineSegment(sketch, "E3716", {"start": v(1, -0.05) * mm, "end": v(1, -0.08) * mm});
            skLineSegment(sketch, "E3717", {"start": v(1, -0.08) * mm, "end": v(1, -0.08) * mm});
            skLineSegment(sketch, "E3718", {"start": v(-0.02, -0.12) * mm, "end": v(-0.02, -0.13) * mm});
            skLineSegment(sketch, "E3719", {"start": v(-0.02, -0.13) * mm, "end": v(-0.04, -0.15) * mm});
            skLineSegment(sketch, "E3720", {"start": v(-0.04, -0.15) * mm, "end": v(-0.06, -0.14) * mm});
            skLineSegment(sketch, "E3721", {"start": v(-0.06, -0.14) * mm, "end": v(-0.07, -0.12) * mm});
            skLineSegment(sketch, "E3722", {"start": v(-0.07, -0.12) * mm, "end": v(-0.07, -0.09) * mm});
            skLineSegment(sketch, "E3723", {"start": v(-0.07, -0.09) * mm, "end": v(-0.07, -0.08) * mm});
            skLineSegment(sketch, "E3724", {"start": v(-0.07, -0.08) * mm, "end": v(-0.06, -0.04) * mm});
            skLineSegment(sketch, "E3725", {"start": v(-0.06, -0.04) * mm, "end": v(-0.04, -0.07) * mm});
            skLineSegment(sketch, "E3726", {"start": v(-0.04, -0.07) * mm, "end": v(-0.03, -0.08) * mm});
            skLineSegment(sketch, "E3727", {"start": v(-0.03, -0.08) * mm, "end": v(-0.02, -0.1) * mm});
            skLineSegment(sketch, "E3728", {"start": v(-0.02, -0.1) * mm, "end": v(-0.02, -0.12) * mm});
            skLineSegment(sketch, "E3729", {"start": v(-0.02, -0.12) * mm, "end": v(-0.02, -0.12) * mm});
            skLineSegment(sketch, "E3730", {"start": v(-0.72, -0.1) * mm, "end": v(-0.72, -0.1) * mm});
            skLineSegment(sketch, "E3731", {"start": v(-0.72, -0.1) * mm, "end": v(-0.71, -0.11) * mm});
            skLineSegment(sketch, "E3732", {"start": v(-0.71, -0.11) * mm, "end": v(-0.7, -0.13) * mm});
            skLineSegment(sketch, "E3733", {"start": v(-0.7, -0.13) * mm, "end": v(-0.69, -0.15) * mm});
            skLineSegment(sketch, "E3734", {"start": v(-0.69, -0.15) * mm, "end": v(-0.67, -0.17) * mm});
            skLineSegment(sketch, "E3735", {"start": v(-0.67, -0.17) * mm, "end": v(-0.66, -0.2) * mm});
            skLineSegment(sketch, "E3736", {"start": v(-0.66, -0.2) * mm, "end": v(-0.65, -0.22) * mm});
            skLineSegment(sketch, "E3737", {"start": v(-0.65, -0.22) * mm, "end": v(-0.65, -0.23) * mm});
            skLineSegment(sketch, "E3738", {"start": v(-0.65, -0.23) * mm, "end": v(-0.65, -0.24) * mm});
            skLineSegment(sketch, "E3739", {"start": v(-0.65, -0.24) * mm, "end": v(-0.65, -0.24) * mm});
            skLineSegment(sketch, "E3740", {"start": v(-0.65, -0.24) * mm, "end": v(-0.66, -0.24) * mm});
            skLineSegment(sketch, "E3741", {"start": v(-0.66, -0.24) * mm, "end": v(-0.67, -0.23) * mm});
            skLineSegment(sketch, "E3742", {"start": v(-0.67, -0.23) * mm, "end": v(-0.69, -0.22) * mm});
            skLineSegment(sketch, "E3743", {"start": v(-0.69, -0.22) * mm, "end": v(-0.7, -0.21) * mm});
            skLineSegment(sketch, "E3744", {"start": v(-0.7, -0.21) * mm, "end": v(-0.71, -0.2) * mm});
            skLineSegment(sketch, "E3745", {"start": v(-0.71, -0.2) * mm, "end": v(-0.72, -0.2) * mm});
            skLineSegment(sketch, "E3746", {"start": v(-0.72, -0.2) * mm, "end": v(-0.73, -0.2) * mm});
            skLineSegment(sketch, "E3747", {"start": v(-0.73, -0.2) * mm, "end": v(-0.75, -0.18) * mm});
            skLineSegment(sketch, "E3748", {"start": v(-0.75, -0.18) * mm, "end": v(-0.77, -0.18) * mm});
            skLineSegment(sketch, "E3749", {"start": v(-0.77, -0.18) * mm, "end": v(-0.78, -0.17) * mm});
            skLineSegment(sketch, "E3750", {"start": v(-0.78, -0.17) * mm, "end": v(-0.78, -0.17) * mm});
            skLineSegment(sketch, "E3751", {"start": v(-0.78, -0.17) * mm, "end": v(-0.8, -0.17) * mm});
            skLineSegment(sketch, "E3752", {"start": v(-0.8, -0.17) * mm, "end": v(-0.8, -0.16) * mm});
            skLineSegment(sketch, "E3753", {"start": v(-0.8, -0.16) * mm, "end": v(-0.8, -0.16) * mm});
            skLineSegment(sketch, "E3754", {"start": v(-0.8, -0.16) * mm, "end": v(-0.8, -0.15) * mm});
            skLineSegment(sketch, "E3755", {"start": v(-0.8, -0.15) * mm, "end": v(-0.83, -0.14) * mm});
            skLineSegment(sketch, "E3756", {"start": v(-0.83, -0.14) * mm, "end": v(-0.84, -0.13) * mm});
            skLineSegment(sketch, "E3757", {"start": v(-0.84, -0.13) * mm, "end": v(-0.86, -0.13) * mm});
            skLineSegment(sketch, "E3758", {"start": v(-0.86, -0.13) * mm, "end": v(-0.9, -0.1) * mm});
            skLineSegment(sketch, "E3759", {"start": v(-0.9, -0.1) * mm, "end": v(-0.92, -0.1) * mm});
            skLineSegment(sketch, "E3760", {"start": v(-0.92, -0.1) * mm, "end": v(-0.9, -0.08) * mm});
            skLineSegment(sketch, "E3761", {"start": v(-0.9, -0.08) * mm, "end": v(-0.86, -0.08) * mm});
            skLineSegment(sketch, "E3762", {"start": v(-0.86, -0.08) * mm, "end": v(-0.84, -0.08) * mm});
            skLineSegment(sketch, "E3763", {"start": v(-0.84, -0.08) * mm, "end": v(-0.83, -0.08) * mm});
            skLineSegment(sketch, "E3764", {"start": v(-0.83, -0.08) * mm, "end": v(-0.8, -0.09) * mm});
            skLineSegment(sketch, "E3765", {"start": v(-0.8, -0.09) * mm, "end": v(-0.77, -0.1) * mm});
            skLineSegment(sketch, "E3766", {"start": v(-0.77, -0.1) * mm, "end": v(-0.74, -0.1) * mm});
            skLineSegment(sketch, "E3767", {"start": v(-0.74, -0.1) * mm, "end": v(-0.73, -0.1) * mm});
            skLineSegment(sketch, "E3768", {"start": v(-0.73, -0.1) * mm, "end": v(-0.72, -0.1) * mm});
            skLineSegment(sketch, "E3769", {"start": v(-1.3, -0.15) * mm, "end": v(-1.3, -0.16) * mm});
            skLineSegment(sketch, "E3770", {"start": v(-1.3, -0.16) * mm, "end": v(-1.3, -0.2) * mm});
            skLineSegment(sketch, "E3771", {"start": v(-1.3, -0.2) * mm, "end": v(-1.28, -0.25) * mm});
            skLineSegment(sketch, "E3772", {"start": v(-1.28, -0.25) * mm, "end": v(-1.26, -0.3) * mm});
            skLineSegment(sketch, "E3773", {"start": v(-1.26, -0.3) * mm, "end": v(-1.24, -0.32) * mm});
            skLineSegment(sketch, "E3774", {"start": v(-1.24, -0.32) * mm, "end": v(-1.23, -0.33) * mm});
            skLineSegment(sketch, "E3775", {"start": v(-1.23, -0.33) * mm, "end": v(-1.23, -0.33) * mm});
            skLineSegment(sketch, "E3776", {"start": v(-1.23, -0.33) * mm, "end": v(-1.22, -0.34) * mm});
            skLineSegment(sketch, "E3777", {"start": v(-1.22, -0.34) * mm, "end": v(-1.21, -0.35) * mm});
            skLineSegment(sketch, "E3778", {"start": v(-1.21, -0.35) * mm, "end": v(-1.22, -0.36) * mm});
            skLineSegment(sketch, "E3779", {"start": v(-1.22, -0.36) * mm, "end": v(-1.23, -0.36) * mm});
            skLineSegment(sketch, "E3780", {"start": v(-1.23, -0.36) * mm, "end": v(-1.24, -0.36) * mm});
            skLineSegment(sketch, "E3781", {"start": v(-1.24, -0.36) * mm, "end": v(-1.24, -0.35) * mm});
            skLineSegment(sketch, "E3782", {"start": v(-1.24, -0.35) * mm, "end": v(-1.27, -0.34) * mm});
            skLineSegment(sketch, "E3783", {"start": v(-1.27, -0.34) * mm, "end": v(-1.3, -0.32) * mm});
            skLineSegment(sketch, "E3784", {"start": v(-1.3, -0.32) * mm, "end": v(-1.32, -0.3) * mm});
            skLineSegment(sketch, "E3785", {"start": v(-1.32, -0.3) * mm, "end": v(-1.34, -0.26) * mm});
            skLineSegment(sketch, "E3786", {"start": v(-1.34, -0.26) * mm, "end": v(-1.36, -0.23) * mm});
            skLineSegment(sketch, "E3787", {"start": v(-1.36, -0.23) * mm, "end": v(-1.37, -0.2) * mm});
            skLineSegment(sketch, "E3788", {"start": v(-1.37, -0.2) * mm, "end": v(-1.37, -0.17) * mm});
            skLineSegment(sketch, "E3789", {"start": v(-1.37, -0.17) * mm, "end": v(-1.36, -0.15) * mm});
            skLineSegment(sketch, "E3790", {"start": v(-1.36, -0.15) * mm, "end": v(-1.36, -0.14) * mm});
            skLineSegment(sketch, "E3791", {"start": v(-1.36, -0.14) * mm, "end": v(-1.35, -0.13) * mm});
            skLineSegment(sketch, "E3792", {"start": v(-1.35, -0.13) * mm, "end": v(-1.34, -0.1) * mm});
            skLineSegment(sketch, "E3793", {"start": v(-1.34, -0.1) * mm, "end": v(-1.32, -0.1) * mm});
            skLineSegment(sketch, "E3794", {"start": v(-1.32, -0.1) * mm, "end": v(-1.31, -0.1) * mm});
            skLineSegment(sketch, "E3795", {"start": v(-1.31, -0.1) * mm, "end": v(-1.3, -0.14) * mm});
            skLineSegment(sketch, "E3796", {"start": v(-1.3, -0.14) * mm, "end": v(-1.3, -0.15) * mm});
            skLineSegment(sketch, "E3797", {"start": v(-0.6, -0.14) * mm, "end": v(-0.6, -0.15) * mm});
            skLineSegment(sketch, "E3798", {"start": v(-0.6, -0.15) * mm, "end": v(-0.57, -0.18) * mm});
            skLineSegment(sketch, "E3799", {"start": v(-0.57, -0.18) * mm, "end": v(-0.53, -0.23) * mm});
            skLineSegment(sketch, "E3800", {"start": v(-0.53, -0.23) * mm, "end": v(-0.5, -0.28) * mm});
            skLineSegment(sketch, "E3801", {"start": v(-0.5, -0.28) * mm, "end": v(-0.49, -0.32) * mm});
            skLineSegment(sketch, "E3802", {"start": v(-0.49, -0.32) * mm, "end": v(-0.49, -0.33) * mm});
            skLineSegment(sketch, "E3803", {"start": v(-0.49, -0.33) * mm, "end": v(-0.49, -0.34) * mm});
            skLineSegment(sketch, "E3804", {"start": v(-0.49, -0.34) * mm, "end": v(-0.49, -0.37) * mm});
            skLineSegment(sketch, "E3805", {"start": v(-0.49, -0.37) * mm, "end": v(-0.49, -0.42) * mm});
            skLineSegment(sketch, "E3806", {"start": v(-0.49, -0.42) * mm, "end": v(-0.5, -0.46) * mm});
            skLineSegment(sketch, "E3807", {"start": v(-0.5, -0.46) * mm, "end": v(-0.5, -0.5) * mm});
            skLineSegment(sketch, "E3808", {"start": v(-0.5, -0.5) * mm, "end": v(-0.5, -0.53) * mm});
            skLineSegment(sketch, "E3809", {"start": v(-0.5, -0.53) * mm, "end": v(-0.5, -0.54) * mm});
            skLineSegment(sketch, "E3810", {"start": v(-0.5, -0.54) * mm, "end": v(-0.51, -0.54) * mm});
            skLineSegment(sketch, "E3811", {"start": v(-0.51, -0.54) * mm, "end": v(-0.52, -0.52) * mm});
            skLineSegment(sketch, "E3812", {"start": v(-0.52, -0.52) * mm, "end": v(-0.52, -0.51) * mm});
            skLineSegment(sketch, "E3813", {"start": v(-0.52, -0.51) * mm, "end": v(-0.52, -0.5) * mm});
            skLineSegment(sketch, "E3814", {"start": v(-0.52, -0.5) * mm, "end": v(-0.53, -0.44) * mm});
            skLineSegment(sketch, "E3815", {"start": v(-0.53, -0.44) * mm, "end": v(-0.54, -0.39) * mm});
            skLineSegment(sketch, "E3816", {"start": v(-0.54, -0.39) * mm, "end": v(-0.56, -0.34) * mm});
            skLineSegment(sketch, "E3817", {"start": v(-0.56, -0.34) * mm, "end": v(-0.58, -0.31) * mm});
            skLineSegment(sketch, "E3818", {"start": v(-0.58, -0.31) * mm, "end": v(-0.59, -0.3) * mm});
            skLineSegment(sketch, "E3819", {"start": v(-0.59, -0.3) * mm, "end": v(-0.6, -0.3) * mm});
            skLineSegment(sketch, "E3820", {"start": v(-0.6, -0.3) * mm, "end": v(-0.6, -0.28) * mm});
            skLineSegment(sketch, "E3821", {"start": v(-0.6, -0.28) * mm, "end": v(-0.62, -0.26) * mm});
            skLineSegment(sketch, "E3822", {"start": v(-0.62, -0.26) * mm, "end": v(-0.62, -0.24) * mm});
            skLineSegment(sketch, "E3823", {"start": v(-0.62, -0.24) * mm, "end": v(-0.63, -0.23) * mm});
            skLineSegment(sketch, "E3824", {"start": v(-0.63, -0.23) * mm, "end": v(-0.63, -0.23) * mm});
            skLineSegment(sketch, "E3825", {"start": v(-0.63, -0.23) * mm, "end": v(-0.63, -0.22) * mm});
            skLineSegment(sketch, "E3826", {"start": v(-0.63, -0.22) * mm, "end": v(-0.63, -0.2) * mm});
            skLineSegment(sketch, "E3827", {"start": v(-0.63, -0.2) * mm, "end": v(-0.65, -0.17) * mm});
            skLineSegment(sketch, "E3828", {"start": v(-0.65, -0.17) * mm, "end": v(-0.65, -0.17) * mm});
            skLineSegment(sketch, "E3829", {"start": v(-0.65, -0.17) * mm, "end": v(-0.65, -0.16) * mm});
            skLineSegment(sketch, "E3830", {"start": v(-0.65, -0.16) * mm, "end": v(-0.67, -0.13) * mm});
            skLineSegment(sketch, "E3831", {"start": v(-0.67, -0.13) * mm, "end": v(-0.66, -0.12) * mm});
            skLineSegment(sketch, "E3832", {"start": v(-0.66, -0.12) * mm, "end": v(-0.65, -0.12) * mm});
            skLineSegment(sketch, "E3833", {"start": v(-0.65, -0.12) * mm, "end": v(-0.62, -0.14) * mm});
            skLineSegment(sketch, "E3834", {"start": v(-0.62, -0.14) * mm, "end": v(-0.6, -0.14) * mm});
            skLineSegment(sketch, "E3835", {"start": v(-0.87, -0.22) * mm, "end": v(-0.86, -0.22) * mm});
            skLineSegment(sketch, "E3836", {"start": v(-0.86, -0.22) * mm, "end": v(-0.82, -0.24) * mm});
            skLineSegment(sketch, "E3837", {"start": v(-0.82, -0.24) * mm, "end": v(-0.77, -0.27) * mm});
            skLineSegment(sketch, "E3838", {"start": v(-0.77, -0.27) * mm, "end": v(-0.73, -0.3) * mm});
            skLineSegment(sketch, "E3839", {"start": v(-0.73, -0.3) * mm, "end": v(-0.7, -0.32) * mm});
            skLineSegment(sketch, "E3840", {"start": v(-0.7, -0.32) * mm, "end": v(-0.7, -0.33) * mm});
            skLineSegment(sketch, "E3841", {"start": v(-0.7, -0.33) * mm, "end": v(-0.7, -0.33) * mm});
            skLineSegment(sketch, "E3842", {"start": v(-0.7, -0.33) * mm, "end": v(-0.68, -0.35) * mm});
            skLineSegment(sketch, "E3843", {"start": v(-0.68, -0.35) * mm, "end": v(-0.66, -0.36) * mm});
            skLineSegment(sketch, "E3844", {"start": v(-0.66, -0.36) * mm, "end": v(-0.65, -0.37) * mm});
            skLineSegment(sketch, "E3845", {"start": v(-0.65, -0.37) * mm, "end": v(-0.65, -0.36) * mm});
            skLineSegment(sketch, "E3846", {"start": v(-0.65, -0.36) * mm, "end": v(-0.65, -0.36) * mm});
            skLineSegment(sketch, "E3847", {"start": v(-0.65, -0.36) * mm, "end": v(-0.65, -0.34) * mm});
            skLineSegment(sketch, "E3848", {"start": v(-0.65, -0.34) * mm, "end": v(-0.65, -0.34) * mm});
            skLineSegment(sketch, "E3849", {"start": v(-0.65, -0.34) * mm, "end": v(-0.64, -0.34) * mm});
            skLineSegment(sketch, "E3850", {"start": v(-0.64, -0.34) * mm, "end": v(-0.64, -0.35) * mm});
            skLineSegment(sketch, "E3851", {"start": v(-0.64, -0.35) * mm, "end": v(-0.63, -0.36) * mm});
            skLineSegment(sketch, "E3852", {"start": v(-0.63, -0.36) * mm, "end": v(-0.63, -0.36) * mm});
            skLineSegment(sketch, "E3853", {"start": v(-0.63, -0.36) * mm, "end": v(-0.63, -0.37) * mm});
            skLineSegment(sketch, "E3854", {"start": v(-0.63, -0.37) * mm, "end": v(-0.63, -0.37) * mm});
            skLineSegment(sketch, "E3855", {"start": v(-0.63, -0.37) * mm, "end": v(-0.62, -0.39) * mm});
            skLineSegment(sketch, "E3856", {"start": v(-0.62, -0.39) * mm, "end": v(-0.6, -0.41) * mm});
            skLineSegment(sketch, "E3857", {"start": v(-0.6, -0.41) * mm, "end": v(-0.6, -0.42) * mm});
            skLineSegment(sketch, "E3858", {"start": v(-0.6, -0.42) * mm, "end": v(-0.6, -0.43) * mm});
            skLineSegment(sketch, "E3859", {"start": v(-0.6, -0.43) * mm, "end": v(-0.58, -0.46) * mm});
            skLineSegment(sketch, "E3860", {"start": v(-0.58, -0.46) * mm, "end": v(-0.57, -0.5) * mm});
            skLineSegment(sketch, "E3861", {"start": v(-0.57, -0.5) * mm, "end": v(-0.56, -0.52) * mm});
            skLineSegment(sketch, "E3862", {"start": v(-0.56, -0.52) * mm, "end": v(-0.57, -0.53) * mm});
            skLineSegment(sketch, "E3863", {"start": v(-0.57, -0.53) * mm, "end": v(-0.57, -0.53) * mm});
            skLineSegment(sketch, "E3864", {"start": v(-0.57, -0.53) * mm, "end": v(-0.59, -0.52) * mm});
            skLineSegment(sketch, "E3865", {"start": v(-0.59, -0.52) * mm, "end": v(-0.61, -0.5) * mm});
            skLineSegment(sketch, "E3866", {"start": v(-0.61, -0.5) * mm, "end": v(-0.62, -0.49) * mm});
            skLineSegment(sketch, "E3867", {"start": v(-0.62, -0.49) * mm, "end": v(-0.63, -0.47) * mm});
            skLineSegment(sketch, "E3868", {"start": v(-0.63, -0.47) * mm, "end": v(-0.66, -0.44) * mm});
            skLineSegment(sketch, "E3869", {"start": v(-0.66, -0.44) * mm, "end": v(-0.7, -0.39) * mm});
            skLineSegment(sketch, "E3870", {"start": v(-0.7, -0.39) * mm, "end": v(-0.76, -0.35) * mm});
            skLineSegment(sketch, "E3871", {"start": v(-0.76, -0.35) * mm, "end": v(-0.79, -0.34) * mm});
            skLineSegment(sketch, "E3872", {"start": v(-0.79, -0.34) * mm, "end": v(-0.8, -0.33) * mm});
            skLineSegment(sketch, "E3873", {"start": v(-0.8, -0.33) * mm, "end": v(-0.8, -0.33) * mm});
            skLineSegment(sketch, "E3874", {"start": v(-0.8, -0.33) * mm, "end": v(-0.82, -0.32) * mm});
            skLineSegment(sketch, "E3875", {"start": v(-0.82, -0.32) * mm, "end": v(-0.85, -0.3) * mm});
            skLineSegment(sketch, "E3876", {"start": v(-0.85, -0.3) * mm, "end": v(-0.89, -0.27) * mm});
            skLineSegment(sketch, "E3877", {"start": v(-0.89, -0.27) * mm, "end": v(-0.92, -0.24) * mm});
            skLineSegment(sketch, "E3878", {"start": v(-0.92, -0.24) * mm, "end": v(-0.96, -0.21) * mm});
            skLineSegment(sketch, "E3879", {"start": v(-0.96, -0.21) * mm, "end": v(-0.99, -0.18) * mm});
            skLineSegment(sketch, "E3880", {"start": v(-0.99, -0.18) * mm, "end": v(-1, -0.17) * mm});
            skLineSegment(sketch, "E3881", {"start": v(-1, -0.17) * mm, "end": v(-1, -0.16) * mm});
            skLineSegment(sketch, "E3882", {"start": v(-1, -0.16) * mm, "end": v(-1, -0.16) * mm});
            skLineSegment(sketch, "E3883", {"start": v(-1, -0.16) * mm, "end": v(-0.99, -0.16) * mm});
            skLineSegment(sketch, "E3884", {"start": v(-0.99, -0.16) * mm, "end": v(-0.96, -0.18) * mm});
            skLineSegment(sketch, "E3885", {"start": v(-0.96, -0.18) * mm, "end": v(-0.92, -0.2) * mm});
            skLineSegment(sketch, "E3886", {"start": v(-0.92, -0.2) * mm, "end": v(-0.88, -0.2) * mm});
            skLineSegment(sketch, "E3887", {"start": v(-0.88, -0.2) * mm, "end": v(-0.87, -0.22) * mm});
            skLineSegment(sketch, "E3888", {"start": v(-0.11, -0.21) * mm, "end": v(-0.11, -0.22) * mm});
            skLineSegment(sketch, "E3889", {"start": v(-0.11, -0.22) * mm, "end": v(-0.13, -0.23) * mm});
            skLineSegment(sketch, "E3890", {"start": v(-0.13, -0.23) * mm, "end": v(-0.16, -0.25) * mm});
            skLineSegment(sketch, "E3891", {"start": v(-0.16, -0.25) * mm, "end": v(-0.2, -0.26) * mm});
            skLineSegment(sketch, "E3892", {"start": v(-0.2, -0.26) * mm, "end": v(-0.24, -0.27) * mm});
            skLineSegment(sketch, "E3893", {"start": v(-0.24, -0.27) * mm, "end": v(-0.26, -0.28) * mm});
            skLineSegment(sketch, "E3894", {"start": v(-0.26, -0.28) * mm, "end": v(-0.26, -0.28) * mm});
            skLineSegment(sketch, "E3895", {"start": v(-0.26, -0.28) * mm, "end": v(-0.29, -0.28) * mm});
            skLineSegment(sketch, "E3896", {"start": v(-0.29, -0.28) * mm, "end": v(-0.3, -0.28) * mm});
            skLineSegment(sketch, "E3897", {"start": v(-0.3, -0.28) * mm, "end": v(-0.32, -0.28) * mm});
            skLineSegment(sketch, "E3898", {"start": v(-0.32, -0.28) * mm, "end": v(-0.31, -0.27) * mm});
            skLineSegment(sketch, "E3899", {"start": v(-0.31, -0.27) * mm, "end": v(-0.3, -0.26) * mm});
            skLineSegment(sketch, "E3900", {"start": v(-0.3, -0.26) * mm, "end": v(-0.28, -0.25) * mm});
            skLineSegment(sketch, "E3901", {"start": v(-0.28, -0.25) * mm, "end": v(-0.25, -0.23) * mm});
            skLineSegment(sketch, "E3902", {"start": v(-0.25, -0.23) * mm, "end": v(-0.22, -0.22) * mm});
            skLineSegment(sketch, "E3903", {"start": v(-0.22, -0.22) * mm, "end": v(-0.2, -0.22) * mm});
            skLineSegment(sketch, "E3904", {"start": v(-0.2, -0.22) * mm, "end": v(-0.2, -0.22) * mm});
            skLineSegment(sketch, "E3905", {"start": v(-0.2, -0.22) * mm, "end": v(-0.16, -0.2) * mm});
            skLineSegment(sketch, "E3906", {"start": v(-0.16, -0.2) * mm, "end": v(-0.13, -0.2) * mm});
            skLineSegment(sketch, "E3907", {"start": v(-0.13, -0.2) * mm, "end": v(-0.12, -0.2) * mm});
            skLineSegment(sketch, "E3908", {"start": v(-0.12, -0.2) * mm, "end": v(-0.11, -0.21) * mm});
            skLineSegment(sketch, "E3909", {"start": v(-0.11, -0.21) * mm, "end": v(-0.11, -0.21) * mm});
            skLineSegment(sketch, "E3910", {"start": v(0.05, -0.22) * mm, "end": v(0.06, -0.23) * mm});
            skLineSegment(sketch, "E3911", {"start": v(0.06, -0.23) * mm, "end": v(0.09, -0.25) * mm});
            skLineSegment(sketch, "E3912", {"start": v(0.09, -0.25) * mm, "end": v(0.12, -0.28) * mm});
            skLineSegment(sketch, "E3913", {"start": v(0.12, -0.28) * mm, "end": v(0.15, -0.32) * mm});
            skLineSegment(sketch, "E3914", {"start": v(0.15, -0.32) * mm, "end": v(0.16, -0.34) * mm});
            skLineSegment(sketch, "E3915", {"start": v(0.16, -0.34) * mm, "end": v(0.16, -0.35) * mm});
            skLineSegment(sketch, "E3916", {"start": v(0.16, -0.35) * mm, "end": v(0.16, -0.35) * mm});
            skLineSegment(sketch, "E3917", {"start": v(0.16, -0.35) * mm, "end": v(0.17, -0.36) * mm});
            skLineSegment(sketch, "E3918", {"start": v(0.17, -0.36) * mm, "end": v(0.18, -0.37) * mm});
            skLineSegment(sketch, "E3919", {"start": v(0.18, -0.37) * mm, "end": v(0.18, -0.37) * mm});
            skLineSegment(sketch, "E3920", {"start": v(0.18, -0.37) * mm, "end": v(0.2, -0.38) * mm});
            skLineSegment(sketch, "E3921", {"start": v(0.2, -0.38) * mm, "end": v(0.2, -0.4) * mm});
            skLineSegment(sketch, "E3922", {"start": v(0.2, -0.4) * mm, "end": v(0.22, -0.43) * mm});
            skLineSegment(sketch, "E3923", {"start": v(0.22, -0.43) * mm, "end": v(0.23, -0.46) * mm});
            skLineSegment(sketch, "E3924", {"start": v(0.23, -0.46) * mm, "end": v(0.24, -0.5) * mm});
            skLineSegment(sketch, "E3925", {"start": v(0.24, -0.5) * mm, "end": v(0.25, -0.53) * mm});
            skLineSegment(sketch, "E3926", {"start": v(0.25, -0.53) * mm, "end": v(0.26, -0.55) * mm});
            skLineSegment(sketch, "E3927", {"start": v(0.26, -0.55) * mm, "end": v(0.26, -0.57) * mm});
            skLineSegment(sketch, "E3928", {"start": v(0.26, -0.57) * mm, "end": v(0.26, -0.57) * mm});
            skLineSegment(sketch, "E3929", {"start": v(0.26, -0.57) * mm, "end": v(0.25, -0.57) * mm});
            skLineSegment(sketch, "E3930", {"start": v(0.25, -0.57) * mm, "end": v(0.24, -0.58) * mm});
            skLineSegment(sketch, "E3931", {"start": v(0.24, -0.58) * mm, "end": v(0.22, -0.57) * mm});
            skLineSegment(sketch, "E3932", {"start": v(0.22, -0.57) * mm, "end": v(0.2, -0.54) * mm});
            skLineSegment(sketch, "E3933", {"start": v(0.2, -0.54) * mm, "end": v(0.17, -0.51) * mm});
            skLineSegment(sketch, "E3934", {"start": v(0.17, -0.51) * mm, "end": v(0.17, -0.5) * mm});
            skLineSegment(sketch, "E3935", {"start": v(0.17, -0.5) * mm, "end": v(0.17, -0.5) * mm});
            skLineSegment(sketch, "E3936", {"start": v(0.17, -0.5) * mm, "end": v(0.15, -0.45) * mm});
            skLineSegment(sketch, "E3937", {"start": v(0.15, -0.45) * mm, "end": v(0.13, -0.42) * mm});
            skLineSegment(sketch, "E3938", {"start": v(0.13, -0.42) * mm, "end": v(0.12, -0.42) * mm});
            skLineSegment(sketch, "E3939", {"start": v(0.12, -0.42) * mm, "end": v(0.12, -0.41) * mm});
            skLineSegment(sketch, "E3940", {"start": v(0.12, -0.41) * mm, "end": v(0.1, -0.4) * mm});
            skLineSegment(sketch, "E3941", {"start": v(0.1, -0.4) * mm, "end": v(0.1, -0.38) * mm});
            skLineSegment(sketch, "E3942", {"start": v(0.1, -0.38) * mm, "end": v(0.1, -0.37) * mm});
            skLineSegment(sketch, "E3943", {"start": v(0.1, -0.37) * mm, "end": v(0.12, -0.36) * mm});
            skLineSegment(sketch, "E3944", {"start": v(0.12, -0.36) * mm, "end": v(0.13, -0.36) * mm});
            skLineSegment(sketch, "E3945", {"start": v(0.13, -0.36) * mm, "end": v(0.13, -0.36) * mm});
            skLineSegment(sketch, "E3946", {"start": v(0.13, -0.36) * mm, "end": v(0.14, -0.36) * mm});
            skLineSegment(sketch, "E3947", {"start": v(0.14, -0.36) * mm, "end": v(0.12, -0.36) * mm});
            skLineSegment(sketch, "E3948", {"start": v(0.12, -0.36) * mm, "end": v(0.12, -0.35) * mm});
            skLineSegment(sketch, "E3949", {"start": v(0.12, -0.35) * mm, "end": v(0.1, -0.35) * mm});
            skLineSegment(sketch, "E3950", {"start": v(0.1, -0.35) * mm, "end": v(0.07, -0.34) * mm});
            skLineSegment(sketch, "E3951", {"start": v(0.07, -0.34) * mm, "end": v(0.03, -0.32) * mm});
            skLineSegment(sketch, "E3952", {"start": v(0.03, -0.32) * mm, "end": v(0.02, -0.32) * mm});
            skLineSegment(sketch, "E3953", {"start": v(0.02, -0.32) * mm, "end": v(0.01, -0.31) * mm});
            skLineSegment(sketch, "E3954", {"start": v(0.01, -0.31) * mm, "end": v(-0.03, -0.3) * mm});
            skLineSegment(sketch, "E3955", {"start": v(-0.03, -0.3) * mm, "end": v(-0.06, -0.28) * mm});
            skLineSegment(sketch, "E3956", {"start": v(-0.06, -0.28) * mm, "end": v(-0.07, -0.28) * mm});
            skLineSegment(sketch, "E3957", {"start": v(-0.07, -0.28) * mm, "end": v(-0.08, -0.28) * mm});
            skLineSegment(sketch, "E3958", {"start": v(-0.08, -0.28) * mm, "end": v(-0.12, -0.28) * mm});
            skLineSegment(sketch, "E3959", {"start": v(-0.12, -0.28) * mm, "end": v(-0.14, -0.27) * mm});
            skLineSegment(sketch, "E3960", {"start": v(-0.14, -0.27) * mm, "end": v(-0.13, -0.25) * mm});
            skLineSegment(sketch, "E3961", {"start": v(-0.13, -0.25) * mm, "end": v(-0.1, -0.24) * mm});
            skLineSegment(sketch, "E3962", {"start": v(-0.1, -0.24) * mm, "end": v(-0.1, -0.23) * mm});
            skLineSegment(sketch, "E3963", {"start": v(-0.1, -0.23) * mm, "end": v(-0.09, -0.23) * mm});
            skLineSegment(sketch, "E3964", {"start": v(-0.09, -0.23) * mm, "end": v(-0.05, -0.21) * mm});
            skLineSegment(sketch, "E3965", {"start": v(-0.05, -0.21) * mm, "end": v(-0.02, -0.2) * mm});
            skLineSegment(sketch, "E3966", {"start": v(-0.02, -0.2) * mm, "end": v(0.02, -0.2) * mm});
            skLineSegment(sketch, "E3967", {"start": v(0.02, -0.2) * mm, "end": v(0.04, -0.22) * mm});
            skLineSegment(sketch, "E3968", {"start": v(0.04, -0.22) * mm, "end": v(0.05, -0.22) * mm});
            skLineSegment(sketch, "E3969", {"start": v(-0.25, -0.3) * mm, "end": v(-0.22, -0.3) * mm});
            skLineSegment(sketch, "E3970", {"start": v(-0.22, -0.3) * mm, "end": v(-0.15, -0.3) * mm});
            skLineSegment(sketch, "E3971", {"start": v(-0.15, -0.3) * mm, "end": v(-0.05, -0.32) * mm});
            skLineSegment(sketch, "E3972", {"start": v(-0.05, -0.32) * mm, "end": v(0.02, -0.35) * mm});
            skLineSegment(sketch, "E3973", {"start": v(0.02, -0.35) * mm, "end": v(0.06, -0.38) * mm});
            skLineSegment(sketch, "E3974", {"start": v(0.06, -0.38) * mm, "end": v(0.06, -0.4) * mm});
            skLineSegment(sketch, "E3975", {"start": v(0.06, -0.4) * mm, "end": v(0.06, -0.4) * mm});
            skLineSegment(sketch, "E3976", {"start": v(0.06, -0.4) * mm, "end": v(0.07, -0.42) * mm});
            skLineSegment(sketch, "E3977", {"start": v(0.07, -0.42) * mm, "end": v(0.08, -0.42) * mm});
            skLineSegment(sketch, "E3978", {"start": v(0.08, -0.42) * mm, "end": v(0.09, -0.42) * mm});
            skLineSegment(sketch, "E3979", {"start": v(0.09, -0.42) * mm, "end": v(0.09, -0.42) * mm});
            skLineSegment(sketch, "E3980", {"start": v(0.09, -0.42) * mm, "end": v(0.1, -0.43) * mm});
            skLineSegment(sketch, "E3981", {"start": v(0.1, -0.43) * mm, "end": v(0.12, -0.45) * mm});
            skLineSegment(sketch, "E3982", {"start": v(0.12, -0.45) * mm, "end": v(0.12, -0.45) * mm});
            skLineSegment(sketch, "E3983", {"start": v(0.12, -0.45) * mm, "end": v(0.13, -0.45) * mm});
            skLineSegment(sketch, "E3984", {"start": v(0.13, -0.45) * mm, "end": v(0.14, -0.47) * mm});
            skLineSegment(sketch, "E3985", {"start": v(0.14, -0.47) * mm, "end": v(0.15, -0.5) * mm});
            skLineSegment(sketch, "E3986", {"start": v(0.15, -0.5) * mm, "end": v(0.16, -0.52) * mm});
            skLineSegment(sketch, "E3987", {"start": v(0.16, -0.52) * mm, "end": v(0.16, -0.53) * mm});
            skLineSegment(sketch, "E3988", {"start": v(0.16, -0.53) * mm, "end": v(0.16, -0.53) * mm});
            skLineSegment(sketch, "E3989", {"start": v(0.16, -0.53) * mm, "end": v(0.15, -0.53) * mm});
            skLineSegment(sketch, "E3990", {"start": v(0.15, -0.53) * mm, "end": v(0.14, -0.52) * mm});
            skLineSegment(sketch, "E3991", {"start": v(0.14, -0.52) * mm, "end": v(0.11, -0.5) * mm});
            skLineSegment(sketch, "E3992", {"start": v(0.11, -0.5) * mm, "end": v(0.1, -0.47) * mm});
            skLineSegment(sketch, "E3993", {"start": v(0.1, -0.47) * mm, "end": v(0.09, -0.46) * mm});
            skLineSegment(sketch, "E3994", {"start": v(0.09, -0.46) * mm, "end": v(0.1, -0.46) * mm});
            skLineSegment(sketch, "E3995", {"start": v(0.1, -0.46) * mm, "end": v(0.1, -0.46) * mm});
            skLineSegment(sketch, "E3996", {"start": v(0.1, -0.46) * mm, "end": v(0.1, -0.45) * mm});
            skLineSegment(sketch, "E3997", {"start": v(0.1, -0.45) * mm, "end": v(0.08, -0.46) * mm});
            skLineSegment(sketch, "E3998", {"start": v(0.08, -0.46) * mm, "end": v(0.08, -0.46) * mm});
            skLineSegment(sketch, "E3999", {"start": v(0.08, -0.46) * mm, "end": v(0.06, -0.46) * mm});
            skLineSegment(sketch, "E4000", {"start": v(0.06, -0.46) * mm, "end": v(0.04, -0.45) * mm});
            skLineSegment(sketch, "E4001", {"start": v(0.04, -0.45) * mm, "end": v(0.02, -0.44) * mm});
            skLineSegment(sketch, "E4002", {"start": v(0.02, -0.44) * mm, "end": v(-0.01, -0.43) * mm});
            skLineSegment(sketch, "E4003", {"start": v(-0.01, -0.43) * mm, "end": v(-0.04, -0.41) * mm});
            skLineSegment(sketch, "E4004", {"start": v(-0.04, -0.41) * mm, "end": v(-0.07, -0.4) * mm});
            skLineSegment(sketch, "E4005", {"start": v(-0.07, -0.4) * mm, "end": v(-0.09, -0.38) * mm});
            skLineSegment(sketch, "E4006", {"start": v(-0.09, -0.38) * mm, "end": v(-0.1, -0.37) * mm});
            skLineSegment(sketch, "E4007", {"start": v(-0.1, -0.37) * mm, "end": v(-0.1, -0.37) * mm});
            skLineSegment(sketch, "E4008", {"start": v(-0.1, -0.37) * mm, "end": v(-0.1, -0.36) * mm});
            skLineSegment(sketch, "E4009", {"start": v(-0.1, -0.36) * mm, "end": v(-0.13, -0.35) * mm});
            skLineSegment(sketch, "E4010", {"start": v(-0.13, -0.35) * mm, "end": v(-0.15, -0.33) * mm});
            skLineSegment(sketch, "E4011", {"start": v(-0.15, -0.33) * mm, "end": v(-0.18, -0.32) * mm});
            skLineSegment(sketch, "E4012", {"start": v(-0.18, -0.32) * mm, "end": v(-0.2, -0.31) * mm});
            skLineSegment(sketch, "E4013", {"start": v(-0.2, -0.31) * mm, "end": v(-0.21, -0.31) * mm});
            skLineSegment(sketch, "E4014", {"start": v(-0.21, -0.31) * mm, "end": v(-0.22, -0.31) * mm});
            skLineSegment(sketch, "E4015", {"start": v(-0.22, -0.31) * mm, "end": v(-0.23, -0.31) * mm});
            skLineSegment(sketch, "E4016", {"start": v(-0.23, -0.31) * mm, "end": v(-0.23, -0.32) * mm});
            skLineSegment(sketch, "E4017", {"start": v(-0.23, -0.32) * mm, "end": v(-0.23, -0.32) * mm});
            skLineSegment(sketch, "E4018", {"start": v(-0.23, -0.32) * mm, "end": v(-0.2, -0.33) * mm});
            skLineSegment(sketch, "E4019", {"start": v(-0.2, -0.33) * mm, "end": v(-0.2, -0.33) * mm});
            skLineSegment(sketch, "E4020", {"start": v(-0.2, -0.33) * mm, "end": v(-0.17, -0.35) * mm});
            skLineSegment(sketch, "E4021", {"start": v(-0.17, -0.35) * mm, "end": v(-0.14, -0.36) * mm});
            skLineSegment(sketch, "E4022", {"start": v(-0.14, -0.36) * mm, "end": v(-0.12, -0.37) * mm});
            skLineSegment(sketch, "E4023", {"start": v(-0.12, -0.37) * mm, "end": v(-0.1, -0.38) * mm});
            skLineSegment(sketch, "E4024", {"start": v(-0.1, -0.38) * mm, "end": v(-0.1, -0.4) * mm});
            skLineSegment(sketch, "E4025", {"start": v(-0.1, -0.4) * mm, "end": v(-0.11, -0.4) * mm});
            skLineSegment(sketch, "E4026", {"start": v(-0.11, -0.4) * mm, "end": v(-0.13, -0.4) * mm});
            skLineSegment(sketch, "E4027", {"start": v(-0.13, -0.4) * mm, "end": v(-0.16, -0.4) * mm});
            skLineSegment(sketch, "E4028", {"start": v(-0.16, -0.4) * mm, "end": v(-0.17, -0.4) * mm});
            skLineSegment(sketch, "E4029", {"start": v(-0.17, -0.4) * mm, "end": v(-0.18, -0.4) * mm});
            skLineSegment(sketch, "E4030", {"start": v(-0.18, -0.4) * mm, "end": v(-0.23, -0.39) * mm});
            skLineSegment(sketch, "E4031", {"start": v(-0.23, -0.39) * mm, "end": v(-0.28, -0.38) * mm});
            skLineSegment(sketch, "E4032", {"start": v(-0.28, -0.38) * mm, "end": v(-0.3, -0.38) * mm});
            skLineSegment(sketch, "E4033", {"start": v(-0.3, -0.38) * mm, "end": v(-0.3, -0.38) * mm});
            skLineSegment(sketch, "E4034", {"start": v(-0.3, -0.38) * mm, "end": v(-0.33, -0.38) * mm});
            skLineSegment(sketch, "E4035", {"start": v(-0.33, -0.38) * mm, "end": v(-0.35, -0.36) * mm});
            skLineSegment(sketch, "E4036", {"start": v(-0.35, -0.36) * mm, "end": v(-0.35, -0.35) * mm});
            skLineSegment(sketch, "E4037", {"start": v(-0.35, -0.35) * mm, "end": v(-0.34, -0.34) * mm});
            skLineSegment(sketch, "E4038", {"start": v(-0.34, -0.34) * mm, "end": v(-0.34, -0.33) * mm});
            skLineSegment(sketch, "E4039", {"start": v(-0.34, -0.33) * mm, "end": v(-0.34, -0.33) * mm});
            skLineSegment(sketch, "E4040", {"start": v(-0.34, -0.33) * mm, "end": v(-0.33, -0.32) * mm});
            skLineSegment(sketch, "E4041", {"start": v(-0.33, -0.32) * mm, "end": v(-0.33, -0.3) * mm});
            skLineSegment(sketch, "E4042", {"start": v(-0.33, -0.3) * mm, "end": v(-0.33, -0.29) * mm});
            skLineSegment(sketch, "E4043", {"start": v(-0.33, -0.29) * mm, "end": v(-0.33, -0.28) * mm});
            skLineSegment(sketch, "E4044", {"start": v(-0.33, -0.28) * mm, "end": v(-0.33, -0.27) * mm});
            skLineSegment(sketch, "E4045", {"start": v(-0.33, -0.27) * mm, "end": v(-0.33, -0.26) * mm});
            skLineSegment(sketch, "E4046", {"start": v(-0.33, -0.26) * mm, "end": v(-0.33, -0.26) * mm});
            skLineSegment(sketch, "E4047", {"start": v(-0.33, -0.26) * mm, "end": v(-0.32, -0.28) * mm});
            skLineSegment(sketch, "E4048", {"start": v(-0.32, -0.28) * mm, "end": v(-0.32, -0.28) * mm});
            skLineSegment(sketch, "E4049", {"start": v(-0.32, -0.28) * mm, "end": v(-0.32, -0.29) * mm});
            skLineSegment(sketch, "E4050", {"start": v(-0.32, -0.29) * mm, "end": v(-0.3, -0.3) * mm});
            skLineSegment(sketch, "E4051", {"start": v(-0.3, -0.3) * mm, "end": v(-0.3, -0.3) * mm});
            skLineSegment(sketch, "E4052", {"start": v(-0.3, -0.3) * mm, "end": v(-0.28, -0.3) * mm});
            skLineSegment(sketch, "E4053", {"start": v(-0.28, -0.3) * mm, "end": v(-0.25, -0.3) * mm});
            skLineSegment(sketch, "E4054", {"start": v(-0.25, -0.3) * mm, "end": v(-0.25, -0.3) * mm});
            skLineSegment(sketch, "E4055", {"start": v(0.74, -0.28) * mm, "end": v(0.74, -0.28) * mm});
            skLineSegment(sketch, "E4056", {"start": v(0.74, -0.28) * mm, "end": v(0.73, -0.3) * mm});
            skLineSegment(sketch, "E4057", {"start": v(0.73, -0.3) * mm, "end": v(0.7, -0.33) * mm});
            skLineSegment(sketch, "E4058", {"start": v(0.7, -0.33) * mm, "end": v(0.68, -0.36) * mm});
            skLineSegment(sketch, "E4059", {"start": v(0.68, -0.36) * mm, "end": v(0.66, -0.37) * mm});
            skLineSegment(sketch, "E4060", {"start": v(0.66, -0.37) * mm, "end": v(0.65, -0.37) * mm});
            skLineSegment(sketch, "E4061", {"start": v(0.65, -0.37) * mm, "end": v(0.65, -0.37) * mm});
            skLineSegment(sketch, "E4062", {"start": v(0.65, -0.37) * mm, "end": v(0.64, -0.36) * mm});
            skLineSegment(sketch, "E4063", {"start": v(0.64, -0.36) * mm, "end": v(0.65, -0.35) * mm});
            skLineSegment(sketch, "E4064", {"start": v(0.65, -0.35) * mm, "end": v(0.65, -0.34) * mm});
            skLineSegment(sketch, "E4065", {"start": v(0.65, -0.34) * mm, "end": v(0.65, -0.34) * mm});
            skLineSegment(sketch, "E4066", {"start": v(0.65, -0.34) * mm, "end": v(0.66, -0.33) * mm});
            skLineSegment(sketch, "E4067", {"start": v(0.66, -0.33) * mm, "end": v(0.66, -0.33) * mm});
            skLineSegment(sketch, "E4068", {"start": v(0.66, -0.33) * mm, "end": v(0.65, -0.33) * mm});
            skLineSegment(sketch, "E4069", {"start": v(0.65, -0.33) * mm, "end": v(0.65, -0.34) * mm});
            skLineSegment(sketch, "E4070", {"start": v(0.65, -0.34) * mm, "end": v(0.64, -0.34) * mm});
            skLineSegment(sketch, "E4071", {"start": v(0.64, -0.34) * mm, "end": v(0.62, -0.35) * mm});
            skLineSegment(sketch, "E4072", {"start": v(0.62, -0.35) * mm, "end": v(0.6, -0.35) * mm});
            skLineSegment(sketch, "E4073", {"start": v(0.6, -0.35) * mm, "end": v(0.6, -0.35) * mm});
            skLineSegment(sketch, "E4074", {"start": v(0.6, -0.35) * mm, "end": v(0.58, -0.35) * mm});
            skLineSegment(sketch, "E4075", {"start": v(0.58, -0.35) * mm, "end": v(0.57, -0.36) * mm});
            skLineSegment(sketch, "E4076", {"start": v(0.57, -0.36) * mm, "end": v(0.57, -0.36) * mm});
            skLineSegment(sketch, "E4077", {"start": v(0.57, -0.36) * mm, "end": v(0.56, -0.36) * mm});
            skLineSegment(sketch, "E4078", {"start": v(0.56, -0.36) * mm, "end": v(0.55, -0.38) * mm});
            skLineSegment(sketch, "E4079", {"start": v(0.55, -0.38) * mm, "end": v(0.53, -0.38) * mm});
            skLineSegment(sketch, "E4080", {"start": v(0.53, -0.38) * mm, "end": v(0.53, -0.38) * mm});
            skLineSegment(sketch, "E4081", {"start": v(0.53, -0.38) * mm, "end": v(0.52, -0.38) * mm});
            skLineSegment(sketch, "E4082", {"start": v(0.52, -0.38) * mm, "end": v(0.51, -0.38) * mm});
            skLineSegment(sketch, "E4083", {"start": v(0.51, -0.38) * mm, "end": v(0.52, -0.39) * mm});
            skLineSegment(sketch, "E4084", {"start": v(0.52, -0.39) * mm, "end": v(0.52, -0.39) * mm});
            skLineSegment(sketch, "E4085", {"start": v(0.52, -0.39) * mm, "end": v(0.52, -0.4) * mm});
            skLineSegment(sketch, "E4086", {"start": v(0.52, -0.4) * mm, "end": v(0.54, -0.4) * mm});
            skLineSegment(sketch, "E4087", {"start": v(0.54, -0.4) * mm, "end": v(0.56, -0.38) * mm});
            skLineSegment(sketch, "E4088", {"start": v(0.56, -0.38) * mm, "end": v(0.56, -0.38) * mm});
            skLineSegment(sketch, "E4089", {"start": v(0.56, -0.38) * mm, "end": v(0.58, -0.37) * mm});
            skLineSegment(sketch, "E4090", {"start": v(0.58, -0.37) * mm, "end": v(0.6, -0.36) * mm});
            skLineSegment(sketch, "E4091", {"start": v(0.6, -0.36) * mm, "end": v(0.6, -0.36) * mm});
            skLineSegment(sketch, "E4092", {"start": v(0.6, -0.36) * mm, "end": v(0.61, -0.37) * mm});
            skLineSegment(sketch, "E4093", {"start": v(0.61, -0.37) * mm, "end": v(0.62, -0.38) * mm});
            skLineSegment(sketch, "E4094", {"start": v(0.62, -0.38) * mm, "end": v(0.61, -0.4) * mm});
            skLineSegment(sketch, "E4095", {"start": v(0.61, -0.4) * mm, "end": v(0.6, -0.42) * mm});
            skLineSegment(sketch, "E4096", {"start": v(0.6, -0.42) * mm, "end": v(0.6, -0.43) * mm});
            skLineSegment(sketch, "E4097", {"start": v(0.6, -0.43) * mm, "end": v(0.6, -0.44) * mm});
            skLineSegment(sketch, "E4098", {"start": v(0.6, -0.44) * mm, "end": v(0.59, -0.44) * mm});
            skLineSegment(sketch, "E4099", {"start": v(0.59, -0.44) * mm, "end": v(0.55, -0.49) * mm});
            skLineSegment(sketch, "E4100", {"start": v(0.55, -0.49) * mm, "end": v(0.52, -0.53) * mm});
            skLineSegment(sketch, "E4101", {"start": v(0.52, -0.53) * mm, "end": v(0.51, -0.54) * mm});
            skLineSegment(sketch, "E4102", {"start": v(0.51, -0.54) * mm, "end": v(0.5, -0.55) * mm});
            skLineSegment(sketch, "E4103", {"start": v(0.5, -0.55) * mm, "end": v(0.48, -0.59) * mm});
            skLineSegment(sketch, "E4104", {"start": v(0.48, -0.59) * mm, "end": v(0.45, -0.62) * mm});
            skLineSegment(sketch, "E4105", {"start": v(0.45, -0.62) * mm, "end": v(0.43, -0.64) * mm});
            skLineSegment(sketch, "E4106", {"start": v(0.43, -0.64) * mm, "end": v(0.41, -0.64) * mm});
            skLineSegment(sketch, "E4107", {"start": v(0.41, -0.64) * mm, "end": v(0.41, -0.64) * mm});
            skLineSegment(sketch, "E4108", {"start": v(0.41, -0.64) * mm, "end": v(0.4, -0.64) * mm});
            skLineSegment(sketch, "E4109", {"start": v(0.4, -0.64) * mm, "end": v(0.4, -0.64) * mm});
            skLineSegment(sketch, "E4110", {"start": v(0.4, -0.64) * mm, "end": v(0.42, -0.62) * mm});
            skLineSegment(sketch, "E4111", {"start": v(0.42, -0.62) * mm, "end": v(0.43, -0.62) * mm});
            skLineSegment(sketch, "E4112", {"start": v(0.43, -0.62) * mm, "end": v(0.43, -0.61) * mm});
            skLineSegment(sketch, "E4113", {"start": v(0.43, -0.61) * mm, "end": v(0.45, -0.6) * mm});
            skLineSegment(sketch, "E4114", {"start": v(0.45, -0.6) * mm, "end": v(0.46, -0.58) * mm});
            skLineSegment(sketch, "E4115", {"start": v(0.46, -0.58) * mm, "end": v(0.47, -0.54) * mm});
            skLineSegment(sketch, "E4116", {"start": v(0.47, -0.54) * mm, "end": v(0.47, -0.5) * mm});
            skLineSegment(sketch, "E4117", {"start": v(0.47, -0.5) * mm, "end": v(0.47, -0.48) * mm});
            skLineSegment(sketch, "E4118", {"start": v(0.47, -0.48) * mm, "end": v(0.48, -0.47) * mm});
            skLineSegment(sketch, "E4119", {"start": v(0.48, -0.47) * mm, "end": v(0.48, -0.44) * mm});
            skLineSegment(sketch, "E4120", {"start": v(0.48, -0.44) * mm, "end": v(0.49, -0.41) * mm});
            skLineSegment(sketch, "E4121", {"start": v(0.49, -0.41) * mm, "end": v(0.49, -0.41) * mm});
            skLineSegment(sketch, "E4122", {"start": v(0.49, -0.41) * mm, "end": v(0.49, -0.4) * mm});
            skLineSegment(sketch, "E4123", {"start": v(0.49, -0.4) * mm, "end": v(0.48, -0.39) * mm});
            skLineSegment(sketch, "E4124", {"start": v(0.48, -0.39) * mm, "end": v(0.47, -0.37) * mm});
            skLineSegment(sketch, "E4125", {"start": v(0.47, -0.37) * mm, "end": v(0.46, -0.37) * mm});
            skLineSegment(sketch, "E4126", {"start": v(0.46, -0.37) * mm, "end": v(0.46, -0.37) * mm});
            skLineSegment(sketch, "E4127", {"start": v(0.46, -0.37) * mm, "end": v(0.45, -0.37) * mm});
            skLineSegment(sketch, "E4128", {"start": v(0.45, -0.37) * mm, "end": v(0.45, -0.35) * mm});
            skLineSegment(sketch, "E4129", {"start": v(0.45, -0.35) * mm, "end": v(0.45, -0.35) * mm});
            skLineSegment(sketch, "E4130", {"start": v(0.45, -0.35) * mm, "end": v(0.45, -0.34) * mm});
            skLineSegment(sketch, "E4131", {"start": v(0.45, -0.34) * mm, "end": v(0.45, -0.32) * mm});
            skLineSegment(sketch, "E4132", {"start": v(0.45, -0.32) * mm, "end": v(0.45, -0.3) * mm});
            skLineSegment(sketch, "E4133", {"start": v(0.45, -0.3) * mm, "end": v(0.45, -0.3) * mm});
            skLineSegment(sketch, "E4134", {"start": v(0.45, -0.3) * mm, "end": v(0.46, -0.3) * mm});
            skLineSegment(sketch, "E4135", {"start": v(0.46, -0.3) * mm, "end": v(0.48, -0.3) * mm});
            skLineSegment(sketch, "E4136", {"start": v(0.48, -0.3) * mm, "end": v(0.48, -0.3) * mm});
            skLineSegment(sketch, "E4137", {"start": v(0.48, -0.3) * mm, "end": v(0.49, -0.31) * mm});
            skLineSegment(sketch, "E4138", {"start": v(0.49, -0.31) * mm, "end": v(0.52, -0.32) * mm});
            skLineSegment(sketch, "E4139", {"start": v(0.52, -0.32) * mm, "end": v(0.57, -0.31) * mm});
            skLineSegment(sketch, "E4140", {"start": v(0.57, -0.31) * mm, "end": v(0.62, -0.3) * mm});
            skLineSegment(sketch, "E4141", {"start": v(0.62, -0.3) * mm, "end": v(0.66, -0.29) * mm});
            skLineSegment(sketch, "E4142", {"start": v(0.66, -0.29) * mm, "end": v(0.67, -0.28) * mm});
            skLineSegment(sketch, "E4143", {"start": v(0.67, -0.28) * mm, "end": v(0.67, -0.27) * mm});
            skLineSegment(sketch, "E4144", {"start": v(0.67, -0.27) * mm, "end": v(0.7, -0.26) * mm});
            skLineSegment(sketch, "E4145", {"start": v(0.7, -0.26) * mm, "end": v(0.71, -0.26) * mm});
            skLineSegment(sketch, "E4146", {"start": v(0.71, -0.26) * mm, "end": v(0.73, -0.26) * mm});
            skLineSegment(sketch, "E4147", {"start": v(0.73, -0.26) * mm, "end": v(0.74, -0.27) * mm});
            skLineSegment(sketch, "E4148", {"start": v(0.74, -0.27) * mm, "end": v(0.74, -0.28) * mm});
            skLineSegment(sketch, "E4149", {"start": v(-0.27, -0.47) * mm, "end": v(-0.27, -0.48) * mm});
            skLineSegment(sketch, "E4150", {"start": v(-0.27, -0.48) * mm, "end": v(-0.3, -0.52) * mm});
            skLineSegment(sketch, "E4151", {"start": v(-0.3, -0.52) * mm, "end": v(-0.32, -0.55) * mm});
            skLineSegment(sketch, "E4152", {"start": v(-0.32, -0.55) * mm, "end": v(-0.33, -0.55) * mm});
            skLineSegment(sketch, "E4153", {"start": v(-0.33, -0.55) * mm, "end": v(-0.33, -0.56) * mm});
            skLineSegment(sketch, "E4154", {"start": v(-0.33, -0.56) * mm, "end": v(-0.34, -0.58) * mm});
            skLineSegment(sketch, "E4155", {"start": v(-0.34, -0.58) * mm, "end": v(-0.35, -0.6) * mm});
            skLineSegment(sketch, "E4156", {"start": v(-0.35, -0.6) * mm, "end": v(-0.34, -0.6) * mm});
            skLineSegment(sketch, "E4157", {"start": v(-0.34, -0.6) * mm, "end": v(-0.34, -0.6) * mm});
            skLineSegment(sketch, "E4158", {"start": v(-0.34, -0.6) * mm, "end": v(-0.34, -0.61) * mm});
            skLineSegment(sketch, "E4159", {"start": v(-0.34, -0.61) * mm, "end": v(-0.35, -0.62) * mm});
            skLineSegment(sketch, "E4160", {"start": v(-0.35, -0.62) * mm, "end": v(-0.36, -0.62) * mm});
            skLineSegment(sketch, "E4161", {"start": v(-0.36, -0.62) * mm, "end": v(-0.37, -0.61) * mm});
            skLineSegment(sketch, "E4162", {"start": v(-0.37, -0.61) * mm, "end": v(-0.37, -0.6) * mm});
            skLineSegment(sketch, "E4163", {"start": v(-0.37, -0.6) * mm, "end": v(-0.37, -0.6) * mm});
            skLineSegment(sketch, "E4164", {"start": v(-0.37, -0.6) * mm, "end": v(-0.38, -0.57) * mm});
            skLineSegment(sketch, "E4165", {"start": v(-0.38, -0.57) * mm, "end": v(-0.38, -0.53) * mm});
            skLineSegment(sketch, "E4166", {"start": v(-0.38, -0.53) * mm, "end": v(-0.38, -0.5) * mm});
            skLineSegment(sketch, "E4167", {"start": v(-0.38, -0.5) * mm, "end": v(-0.38, -0.48) * mm});
            skLineSegment(sketch, "E4168", {"start": v(-0.38, -0.48) * mm, "end": v(-0.38, -0.48) * mm});
            skLineSegment(sketch, "E4169", {"start": v(-0.38, -0.48) * mm, "end": v(-0.37, -0.48) * mm});
            skLineSegment(sketch, "E4170", {"start": v(-0.37, -0.48) * mm, "end": v(-0.37, -0.47) * mm});
            skLineSegment(sketch, "E4171", {"start": v(-0.37, -0.47) * mm, "end": v(-0.36, -0.45) * mm});
            skLineSegment(sketch, "E4172", {"start": v(-0.36, -0.45) * mm, "end": v(-0.36, -0.45) * mm});
            skLineSegment(sketch, "E4173", {"start": v(-0.36, -0.45) * mm, "end": v(-0.36, -0.44) * mm});
            skLineSegment(sketch, "E4174", {"start": v(-0.36, -0.44) * mm, "end": v(-0.35, -0.42) * mm});
            skLineSegment(sketch, "E4175", {"start": v(-0.35, -0.42) * mm, "end": v(-0.32, -0.4) * mm});
            skLineSegment(sketch, "E4176", {"start": v(-0.32, -0.4) * mm, "end": v(-0.32, -0.4) * mm});
            skLineSegment(sketch, "E4177", {"start": v(-0.32, -0.4) * mm, "end": v(-0.3, -0.4) * mm});
            skLineSegment(sketch, "E4178", {"start": v(-0.3, -0.4) * mm, "end": v(-0.28, -0.4) * mm});
            skLineSegment(sketch, "E4179", {"start": v(-0.28, -0.4) * mm, "end": v(-0.26, -0.4) * mm});
            skLineSegment(sketch, "E4180", {"start": v(-0.26, -0.4) * mm, "end": v(-0.25, -0.43) * mm});
            skLineSegment(sketch, "E4181", {"start": v(-0.25, -0.43) * mm, "end": v(-0.27, -0.46) * mm});
            skLineSegment(sketch, "E4182", {"start": v(-0.27, -0.46) * mm, "end": v(-0.27, -0.47) * mm});
            skLineSegment(sketch, "E4183", {"start": v(-0.46, -0.61) * mm, "end": v(-0.46, -0.62) * mm});
            skLineSegment(sketch, "E4184", {"start": v(-0.46, -0.62) * mm, "end": v(-0.47, -0.63) * mm});
            skLineSegment(sketch, "E4185", {"start": v(-0.47, -0.63) * mm, "end": v(-0.49, -0.63) * mm});
            skLineSegment(sketch, "E4186", {"start": v(-0.49, -0.63) * mm, "end": v(-0.5, -0.63) * mm});
            skLineSegment(sketch, "E4187", {"start": v(-0.5, -0.63) * mm, "end": v(-0.5, -0.63) * mm});
            skLineSegment(sketch, "E4188", {"start": v(-0.5, -0.63) * mm, "end": v(-0.5, -0.62) * mm});
            skLineSegment(sketch, "E4189", {"start": v(-0.5, -0.62) * mm, "end": v(-0.51, -0.6) * mm});
            skLineSegment(sketch, "E4190", {"start": v(-0.51, -0.6) * mm, "end": v(-0.5, -0.57) * mm});
            skLineSegment(sketch, "E4191", {"start": v(-0.5, -0.57) * mm, "end": v(-0.5, -0.55) * mm});
            skLineSegment(sketch, "E4192", {"start": v(-0.5, -0.55) * mm, "end": v(-0.5, -0.54) * mm});
            skLineSegment(sketch, "E4193", {"start": v(-0.5, -0.54) * mm, "end": v(-0.5, -0.54) * mm});
            skLineSegment(sketch, "E4194", {"start": v(-0.5, -0.54) * mm, "end": v(-0.48, -0.54) * mm});
            skLineSegment(sketch, "E4195", {"start": v(-0.48, -0.54) * mm, "end": v(-0.47, -0.56) * mm});
            skLineSegment(sketch, "E4196", {"start": v(-0.47, -0.56) * mm, "end": v(-0.46, -0.6) * mm});
            skLineSegment(sketch, "E4197", {"start": v(-0.46, -0.6) * mm, "end": v(-0.46, -0.6) * mm});
            skLineSegment(sketch, "E4198", {"start": v(-0.46, -0.6) * mm, "end": v(-0.46, -0.61) * mm});
            skLineSegment(sketch, "E4199", {"start": v(-1.03, 1.04) * mm, "end": v(-0.98, 1.05) * mm});
            skLineSegment(sketch, "E4200", {"start": v(-0.98, 1.05) * mm, "end": v(-0.92, 1.06) * mm});
            skLineSegment(sketch, "E4201", {"start": v(-0.92, 1.06) * mm, "end": v(-0.87, 1.08) * mm});
            skLineSegment(sketch, "E4202", {"start": v(-0.87, 1.08) * mm, "end": v(-0.82, 1.1) * mm});
            skLineSegment(sketch, "E4203", {"start": v(-0.82, 1.1) * mm, "end": v(-0.78, 1.1) * mm});
            skLineSegment(sketch, "E4204", {"start": v(-0.78, 1.1) * mm, "end": v(-0.77, 1.1) * mm});
            skLineSegment(sketch, "E4205", {"start": v(-0.77, 1.1) * mm, "end": v(-0.77, 1.1) * mm});
            skLineSegment(sketch, "E4206", {"start": v(-0.77, 1.1) * mm, "end": v(-0.78, 1.1) * mm});
            skLineSegment(sketch, "E4207", {"start": v(-0.78, 1.1) * mm, "end": v(-0.82, 1.1) * mm});
            skLineSegment(sketch, "E4208", {"start": v(-0.82, 1.1) * mm, "end": v(-0.91, 1.08) * mm});
            skLineSegment(sketch, "E4209", {"start": v(-0.91, 1.08) * mm, "end": v(-1, 1.07) * mm});
            skLineSegment(sketch, "E4210", {"start": v(-1, 1.07) * mm, "end": v(-1.07, 1.06) * mm});
            skLineSegment(sketch, "E4211", {"start": v(-0.8, -0.97) * mm, "end": v(-0.8, -1.09) * mm});
            skLineSegment(sketch, "E4212", {"start": v(-0.8, -1.09) * mm, "end": v(-0.79, -1.16) * mm});
            skLineSegment(sketch, "E4213", {"start": v(-0.79, -1.16) * mm, "end": v(-0.77, -1.19) * mm});
            skLineSegment(sketch, "E4214", {"start": v(-0.77, -1.19) * mm, "end": v(-0.76, -1.19) * mm});
            skLineSegment(sketch, "E4215", {"start": v(-0.76, -1.19) * mm, "end": v(-0.75, -1.19) * mm});
            skLineSegment(sketch, "E4216", {"start": v(-0.75, -1.19) * mm, "end": v(-0.72, -1.19) * mm});
            skLineSegment(sketch, "E4217", {"start": v(-0.72, -1.19) * mm, "end": v(-0.68, -1.19) * mm});
            skLineSegment(sketch, "E4218", {"start": v(-0.68, -1.19) * mm, "end": v(-0.62, -1.2) * mm});
            skLineSegment(sketch, "E4219", {"start": v(-0.62, -1.2) * mm, "end": v(-0.57, -1.2) * mm});
            skLineSegment(sketch, "E4220", {"start": v(-0.57, -1.2) * mm, "end": v(-0.53, -1.19) * mm});
            skLineSegment(sketch, "E4221", {"start": v(-0.53, -1.19) * mm, "end": v(-0.5, -1.17) * mm});
            skLineSegment(sketch, "E4222", {"start": v(-0.5, -1.17) * mm, "end": v(-0.5, -1.15) * mm});
            skLineSegment(sketch, "E4223", {"start": v(-0.5, -1.15) * mm, "end": v(-0.52, -1.12) * mm});
            skLineSegment(sketch, "E4224", {"start": v(-0.52, -1.12) * mm, "end": v(-0.53, -1.1) * mm});
            skLineSegment(sketch, "E4225", {"start": v(-0.58, -0.98) * mm, "end": v(-0.59, -0.97) * mm});
            skLineSegment(sketch, "E4226", {"start": v(-0.59, -0.97) * mm, "end": v(-0.61, -0.94) * mm});
            skLineSegment(sketch, "E4227", {"start": v(-0.61, -0.94) * mm, "end": v(-0.63, -0.9) * mm});
            skLineSegment(sketch, "E4228", {"start": v(0.5, -1) * mm, "end": v(0.49, -1.04) * mm});
            skLineSegment(sketch, "E4229", {"start": v(0.49, -1.04) * mm, "end": v(0.48, -1.07) * mm});
            skLineSegment(sketch, "E4230", {"start": v(0.48, -1.1) * mm, "end": v(0.49, -1.13) * mm});
            skLineSegment(sketch, "E4231", {"start": v(0.49, -1.13) * mm, "end": v(0.49, -1.16) * mm});
            skLineSegment(sketch, "E4232", {"start": v(0.49, -1.16) * mm, "end": v(0.5, -1.17) * mm});
            skLineSegment(sketch, "E4233", {"start": v(0.5, -1.17) * mm, "end": v(0.5, -1.18) * mm});
            skLineSegment(sketch, "E4234", {"start": v(0.5, -1.18) * mm, "end": v(0.5, -1.18) * mm});
            skLineSegment(sketch, "E4235", {"start": v(0.5, -1.18) * mm, "end": v(0.53, -1.18) * mm});
            skLineSegment(sketch, "E4236", {"start": v(0.53, -1.18) * mm, "end": v(0.6, -1.19) * mm});
            skLineSegment(sketch, "E4237", {"start": v(0.6, -1.19) * mm, "end": v(0.68, -1.2) * mm});
            skLineSegment(sketch, "E4238", {"start": v(0.68, -1.2) * mm, "end": v(0.73, -1.19) * mm});
            skLineSegment(sketch, "E4239", {"start": v(0.73, -1.19) * mm, "end": v(0.76, -1.18) * mm});
            skLineSegment(sketch, "E4240", {"start": v(0.76, -1.18) * mm, "end": v(0.76, -1.17) * mm});
            skLineSegment(sketch, "E4241", {"start": v(0.76, -1.17) * mm, "end": v(0.77, -1.17) * mm});
            skLineSegment(sketch, "E4242", {"start": v(0.77, -1.17) * mm, "end": v(0.78, -1.17) * mm});
            skLineSegment(sketch, "E4243", {"start": v(0.78, -1.17) * mm, "end": v(0.78, -1.14) * mm});
            skLineSegment(sketch, "E4244", {"start": v(0.78, -1.14) * mm, "end": v(0.78, -1.1) * mm});
            skLineSegment(sketch, "E4245", {"start": v(0.79, -1) * mm, "end": v(0.78, -0.94) * mm});
            skLineSegment(sketch, "E4246", {"start": v(0.78, -0.94) * mm, "end": v(0.77, -0.85) * mm});
            skLineSegment(sketch, "E4247", {"start": v(0.77, -0.85) * mm, "end": v(0.75, -0.77) * mm});
            skLineSegment(sketch, "E4248", {"start": v(0.75, -0.77) * mm, "end": v(0.73, -0.73) * mm});
            skLineSegment(sketch, "E4249", {"start": v(0.73, -0.73) * mm, "end": v(0.73, -0.71) * mm});
            skLineSegment(sketch, "E4250", {"start": v(-1.48, 0.57) * mm, "end": v(-1.48, 0.6) * mm});
            skLineSegment(sketch, "E4251", {"start": v(-1.48, 0.6) * mm, "end": v(-1.47, 0.65) * mm});
            skLineSegment(sketch, "E4252", {"start": v(-1.47, 0.65) * mm, "end": v(-1.45, 0.71) * mm});
            skLineSegment(sketch, "E4253", {"start": v(-1.45, 0.71) * mm, "end": v(-1.43, 0.77) * mm});
            skLineSegment(sketch, "E4254", {"start": v(-1.43, 0.77) * mm, "end": v(-1.41, 0.8) * mm});
            skLineSegment(sketch, "E4255", {"start": v(-1.41, 0.8) * mm, "end": v(-1.4, 0.82) * mm});
            skLineSegment(sketch, "E4256", {"start": v(-1.4, 0.82) * mm, "end": v(-1.4, 0.82) * mm});
            skLineSegment(sketch, "E4257", {"start": v(-1.4, 0.82) * mm, "end": v(-1.39, 0.84) * mm});
            skLineSegment(sketch, "E4258", {"start": v(-1.39, 0.84) * mm, "end": v(-1.38, 0.86) * mm});
            skLineSegment(sketch, "E4259", {"start": v(-1.38, 0.86) * mm, "end": v(-1.37, 0.86) * mm});
            skLineSegment(sketch, "E4260", {"start": v(-1.37, 0.86) * mm, "end": v(-1.37, 0.86) * mm});
            skLineSegment(sketch, "E4261", {"start": v(-1.37, 0.86) * mm, "end": v(-1.37, 0.85) * mm});
            skLineSegment(sketch, "E4262", {"start": v(-1.37, 0.85) * mm, "end": v(-1.37, 0.86) * mm});
            skLineSegment(sketch, "E4263", {"start": v(-1.37, 0.86) * mm, "end": v(-1.36, 0.86) * mm});
            skLineSegment(sketch, "E4264", {"start": v(-1.36, 0.86) * mm, "end": v(-1.36, 0.87) * mm});
            skLineSegment(sketch, "E4265", {"start": v(0.3, 0.86) * mm, "end": v(0.31, 0.85) * mm});
            skLineSegment(sketch, "E4266", {"start": v(0.31, 0.85) * mm, "end": v(0.33, 0.82) * mm});
            skLineSegment(sketch, "E4267", {"start": v(0.33, 0.82) * mm, "end": v(0.35, 0.79) * mm});
            skLineSegment(sketch, "E4268", {"start": v(0.35, 0.79) * mm, "end": v(0.37, 0.75) * mm});
            skLineSegment(sketch, "E4269", {"start": v(0.38, 0.74) * mm, "end": v(0.4, 0.71) * mm});
            skLineSegment(sketch, "E4270", {"start": v(0.4, 0.71) * mm, "end": v(0.42, 0.68) * mm});
            skLineSegment(sketch, "E4271", {"start": v(0.42, 0.68) * mm, "end": v(0.43, 0.65) * mm});
            skLineSegment(sketch, "E4272", {"start": v(0.43, 0.65) * mm, "end": v(0.44, 0.64) * mm});
            skLineSegment(sketch, "E4273", {"start": v(1.2, 0.18) * mm, "end": v(1.22, 0.21) * mm});
            skLineSegment(sketch, "E4274", {"start": v(1.22, 0.21) * mm, "end": v(1.28, 0.3) * mm});
            skLineSegment(sketch, "E4275", {"start": v(1.28, 0.3) * mm, "end": v(1.35, 0.42) * mm});
            skLineSegment(sketch, "E4276", {"start": v(1.35, 0.42) * mm, "end": v(1.4, 0.55) * mm});
            skLineSegment(sketch, "E4277", {"start": v(1.4, 0.55) * mm, "end": v(1.43, 0.65) * mm});
            skLineSegment(sketch, "E4278", {"start": v(1.43, 0.65) * mm, "end": v(1.44, 0.68) * mm});
            skLineSegment(sketch, "E4279", {"start": v(-1.75, 0.6) * mm, "end": v(-1.75, 0.57) * mm});
            skLineSegment(sketch, "E4280", {"start": v(-1.75, 0.57) * mm, "end": v(-1.75, 0.53) * mm});
            skLineSegment(sketch, "E4281", {"start": v(-1.75, 0.53) * mm, "end": v(-1.74, 0.45) * mm});
            skLineSegment(sketch, "E4282", {"start": v(-1.74, 0.45) * mm, "end": v(-1.72, 0.36) * mm});
            skLineSegment(sketch, "E4283", {"start": v(-1.72, 0.36) * mm, "end": v(-1.69, 0.3) * mm});
            skLineSegment(sketch, "E4284", {"start": v(1.18, -0.34) * mm, "end": v(1.2, -0.34) * mm});
            skLineSegment(sketch, "E4285", {"start": v(1.2, -0.34) * mm, "end": v(1.24, -0.37) * mm});
            skLineSegment(sketch, "E4286", {"start": v(1.24, -0.37) * mm, "end": v(1.3, -0.42) * mm});
            skLineSegment(sketch, "E4287", {"start": v(1.3, -0.42) * mm, "end": v(1.35, -0.48) * mm});
            skLineSegment(sketch, "E4288", {"start": v(1.35, -0.48) * mm, "end": v(1.4, -0.55) * mm});
            skLineSegment(sketch, "E4289", {"start": v(1.4, -0.55) * mm, "end": v(1.44, -0.62) * mm});
            skLineSegment(sketch, "E4290", {"start": v(1.44, -0.62) * mm, "end": v(1.48, -0.68) * mm});
            skLineSegment(sketch, "E4291", {"start": v(1.48, -0.68) * mm, "end": v(1.52, -0.73) * mm});
            skLineSegment(sketch, "E4292", {"start": v(1.52, -0.73) * mm, "end": v(1.54, -0.75) * mm});
            skLineSegment(sketch, "E4293", {"start": v(1.54, -0.75) * mm, "end": v(1.56, -0.76) * mm});
            skLineSegment(sketch, "E4294", {"start": v(-0.4, 0.26) * mm, "end": v(-0.42, 0.22) * mm});
            skLineSegment(sketch, "E4295", {"start": v(-0.42, 0.2) * mm, "end": v(-0.43, 0.19) * mm});
            skLineSegment(sketch, "E4296", {"start": v(-0.43, 0.19) * mm, "end": v(-0.46, 0.15) * mm});
            skLineSegment(sketch, "E4297", {"start": v(-0.46, 0.15) * mm, "end": v(-0.5, 0.12) * mm});
            skLineSegment(sketch, "E4298", {"start": v(-0.5, 0.12) * mm, "end": v(-0.55, 0.1) * mm});
            skLineSegment(sketch, "E4299", {"start": v(-0.57, 0.1) * mm, "end": v(-0.58, 0.1) * mm});
            skLineSegment(sketch, "E4300", {"start": v(-0.58, 0.1) * mm, "end": v(-0.61, 0.1) * mm});
            skLineSegment(sketch, "E4301", {"start": v(-0.61, 0.1) * mm, "end": v(-0.64, 0.12) * mm});
            skLineSegment(sketch, "E4302", {"start": v(-0.67, 0.13) * mm, "end": v(-0.71, 0.17) * mm});
            skLineSegment(sketch, "E4303", {"start": v(-0.71, 0.17) * mm, "end": v(-0.77, 0.21) * mm});
            skLineSegment(sketch, "E4304", {"start": v(-1.13, 0.45) * mm, "end": v(-1.15, 0.45) * mm});
            skLineSegment(sketch, "E4305", {"start": v(-1.15, 0.45) * mm, "end": v(-1.16, 0.45) * mm});
            skLineSegment(sketch, "E4306", {"start": v(0.53, 0.24) * mm, "end": v(0.5, 0.21) * mm});
            skLineSegment(sketch, "E4307", {"start": v(0.5, 0.21) * mm, "end": v(0.46, 0.2) * mm});
            skLineSegment(sketch, "E4308", {"start": v(0.46, 0.2) * mm, "end": v(0.41, 0.18) * mm});
            skLineSegment(sketch, "E4309", {"start": v(0.41, 0.18) * mm, "end": v(0.37, 0.17) * mm});
            skLineSegment(sketch, "E4310", {"start": v(0.37, 0.17) * mm, "end": v(0.36, 0.18) * mm});
            skLineSegment(sketch, "E4311", {"start": v(0.36, 0.18) * mm, "end": v(0.34, 0.18) * mm});
            skLineSegment(sketch, "E4312", {"start": v(0.34, 0.18) * mm, "end": v(0.27, 0.2) * mm});
            skLineSegment(sketch, "E4313", {"start": v(0.27, 0.2) * mm, "end": v(0.2, 0.23) * mm});
            skLineSegment(sketch, "E4314", {"start": v(0.2, 0.23) * mm, "end": v(0.16, 0.26) * mm});
            skLineSegment(sketch, "E4315", {"start": v(0.16, 0.26) * mm, "end": v(0.14, 0.28) * mm});
            skLineSegment(sketch, "E4316", {"start": v(0.14, 0.28) * mm, "end": v(0.13, 0.28) * mm});
            skSolve(sketch);
        }
        {
            var Q0;
            Q0=makeQuery(id+"F0.imprint","IMPRINT",FACE,{"disambiguationData":[TD([[makeQuery(id+"F0.imprint","IMPRINT",EDGE,{"derivedFrom":sQuery(id+"F0.wireOp",EDGE,"E92")}),1.0]])]});
            extrude(context, id + "F1", {"entities" : qUnion([Q0]), "depth" : 25.4 * mm, "offsetDistance" : 25.4 * mm});
        }
    });
